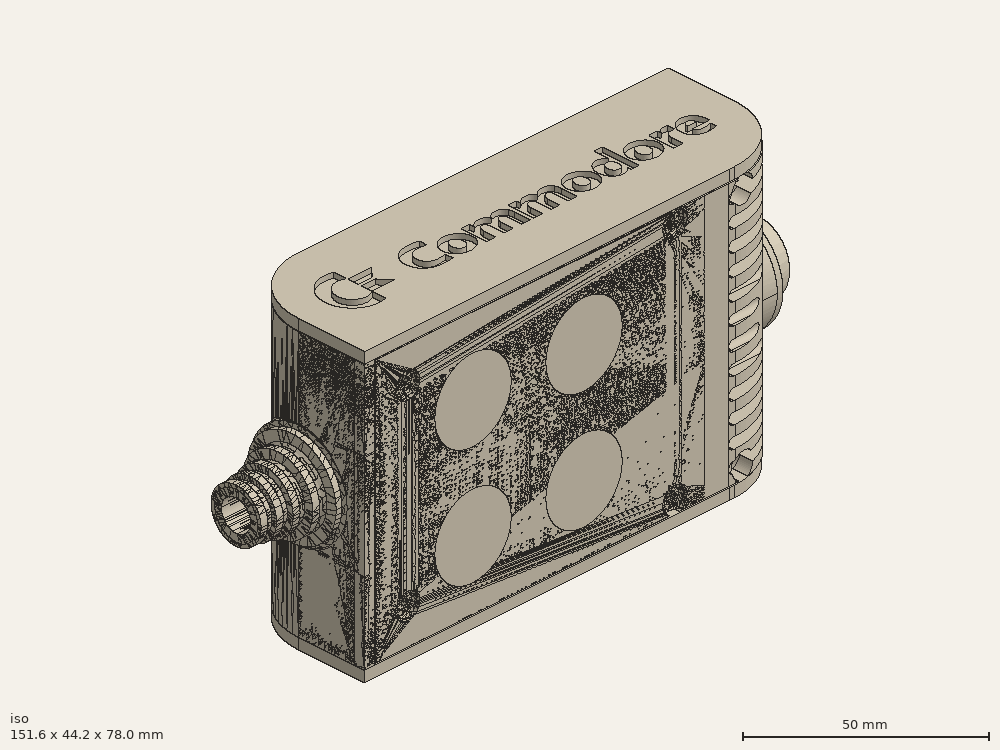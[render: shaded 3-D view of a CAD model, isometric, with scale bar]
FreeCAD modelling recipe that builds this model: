
FCSTD DOCUMENT  (FreeCAD 0.19R0.19.2)
Label: enclosure_219FCStd
License: All rights reserved
LicenseURL: http://en.wikipedia.org/wiki/All_rights_reserved
objects: Part::Revolution×152, Part::MultiFuse×146, Part::Feature×146, Sketcher::SketchObject×90, Part::Extrusion×74, Part::Cut×72, Part::Cylinder×70, Part::Fillet×58, Part::Box×36, App::MeasureDistance×4, Part::Chamfer×4, Part::FeaturePython×2, Image::ImagePlane×1, PartDesign::Body×1, Part::Mirroring×1
note: 852 computed .brp shape members not serialized (recipe doc carries the construction recipe); baked Part::Feature solids carry a one-line shape summary decoded from their .brp

FEATURE [Sketcher::SketchObject] Sketch  label="topSketch"
  FullyConstrained = true
  sketch-geometry (20):
    g0: LineSegment StartX=5.21097e-06 StartY=3 StartZ=0 EndX=5.21097e-06 EndY=19 EndZ=0
    g1: ArcOfCircle CenterX=19 CenterY=19 CenterZ=0 NormalX=0 NormalY=0 NormalZ=1 AngleXU=0 Radius=19 StartAngle=1.5708 EndAngle=3.14159
    g2: ArcOfCircle CenterX=19 CenterY=19 CenterZ=0 NormalX=0 NormalY=0 NormalZ=1 AngleXU=0 Radius=16 StartAngle=1.5708 EndAngle=3.14159
    g3: LineSegment StartX=114 StartY=35 StartZ=0 EndX=19 EndY=35 EndZ=0
    g4: LineSegment StartX=5.21097e-06 StartY=3 StartZ=0 EndX=5.21097e-06 EndY=0 EndZ=0
    g5: LineSegment StartX=3 StartY=0 StartZ=0 EndX=5.21097e-06 EndY=0 EndZ=0
    g6: LineSegment StartX=3 StartY=19 StartZ=0 EndX=3 EndY=0 EndZ=0
    g7: LineSegment StartX=19 StartY=38 StartZ=0 EndX=124 EndY=38 EndZ=0
    g8: Circle CenterX=119 CenterY=35 CenterZ=0 NormalX=0 NormalY=0 NormalZ=1 AngleXU=0 Radius=1
    g9: Circle CenterX=121 CenterY=35 CenterZ=0 NormalX=0 NormalY=0 NormalZ=1 AngleXU=0 Radius=1
    g10: Circle CenterX=121 CenterY=33 CenterZ=0 NormalX=0 NormalY=0 NormalZ=1 AngleXU=0 Radius=1
    g11: BSplineCurve PolesCount=3 KnotsCount=2 Degree=2 IsPeriodic=0
    g12: GeomPoint X=119 Y=35 Z=0
    g13: GeomPoint X=121 Y=33 Z=0
    g14: LineSegment StartX=119 StartY=35 StartZ=0 EndX=114 EndY=35 EndZ=0
    g15: ArcOfCircle CenterX=105 CenterY=19 CenterZ=0 NormalX=0 NormalY=0 NormalZ=1 AngleXU=0 Radius=19 StartAngle=5.7297 EndAngle=6.28319
    g16: ArcOfCircle CenterX=105 CenterY=19 CenterZ=0 NormalX=0 NormalY=0 NormalZ=1 AngleXU=0 Radius=16 StartAngle=5.60905 EndAngle=6.28319
    g17: LineSegment StartX=121 StartY=33 StartZ=0 EndX=121 EndY=19 EndZ=0
    g18: LineSegment StartX=124 StartY=38 StartZ=0 EndX=124 EndY=19 EndZ=0
    g19: LineSegment StartX=117.5 StartY=9.01251 StartZ=0 EndX=121.163 EndY=9.0125 EndZ=0
  constraints (46):
    c: Vertical(g0)
    c: Block(g0)
    c: Coincident(g1,g0)
    c: Block(g1)
    c: Coincident(g2,g1)
    c: Block(g2)
    c: Coincident(g3,g2)
    c: Horizontal(g3)
    c: Tangent(g3,g2)
    c: Coincident(g4,g0)
    c: Distance(g4) = 3
    c: Vertical(g4)
    c: Coincident(g5,g4)
    c: Horizontal(g5)
    c: Coincident(g6,g2)
    c: Coincident(g6,g5)
    c: Vertical(g6)
    c: Horizontal(g7)
    c: Distance(g7) = 105
    c: Coincident(g7,g1)
    c: Block(g3)
    c: Weight(g8) = 1
    c: Equal(g8,g9)
    c: Equal(g8,g10)
    c: InternalAlignment(g8,g11)
    c: InternalAlignment(g9,g11)
    c: InternalAlignment(g10,g11)
    c: InternalAlignment(g12,g11)
    c: InternalAlignment(g13,g11)
    c: Block(g11)
    c: Coincident(g14,g11)
    c: Coincident(g14,g3)
    c: Horizontal(g14)
    c: Block(g15)
    c: Coincident(g16,g15)
    c: Block(g16)
    c: Coincident(g17,g11)
    c: Coincident(g17,g16)
    c: Vertical(g17)
    c: Distance(g17) = 14
    c: Coincident(g18,g7)
    c: Coincident(g18,g15)
    c: Vertical(g18)
    c: Distance(g18) = 19
    c: Coincident(g19,g16)
    c: Coincident(g19,g15)
FEATURE [Sketcher::SketchObject] Sketch001  label="bottomSketch"
  FullyConstrained = true
  sketch-geometry (32):
    g0: LineSegment StartX=3.3 StartY=-6.03275e-07 StartZ=0 EndX=98 EndY=-6.03275e-07 EndZ=0
    g1: ArcOfCircle CenterX=98 CenterY=19 CenterZ=0 NormalX=0 NormalY=0 NormalZ=1 AngleXU=0 Radius=19 StartAngle=4.71239 EndAngle=5.71103
    g2: LineSegment StartX=6.3 StartY=8 StartZ=0 EndX=3.3 EndY=8 EndZ=0
    g3: LineSegment StartX=3.3 StartY=8 StartZ=0 EndX=3.3 EndY=-6.03275e-07 EndZ=0
    g4: ArcOfCircle CenterX=8.3 CenterY=5 CenterZ=0 NormalX=0 NormalY=0 NormalZ=1 AngleXU=0 Radius=2 StartAngle=3.14159 EndAngle=4.71239
    g5: LineSegment StartX=6.3 StartY=8 StartZ=0 EndX=6.3 EndY=5 EndZ=0
    g6: ArcOfCircle CenterX=98 CenterY=19 CenterZ=0 NormalX=0 NormalY=0 NormalZ=1 AngleXU=0 Radius=12.7 StartAngle=4.71239 EndAngle=6.28319
    g7: LineSegment StartX=94.7 StartY=3 StartZ=0 EndX=8.3 EndY=3 EndZ=0
    g8-g12: Circle x5 (B-spline internal-alignment scaffolding for g13; pole/knot coordinates omitted)
    g13: BSplineCurve PolesCount=5 KnotsCount=3 Degree=3 IsPeriodic=0
    g14: GeomPoint X=98 Y=6.3 Z=0
    g15: GeomPoint X=96.3938 Y=4.71946 Z=0
    g16: GeomPoint X=94.7 Y=3 Z=0
    g17-g23: Circle x7 (B-spline internal-alignment scaffolding for g24; pole/knot coordinates omitted)
    g24: BSplineCurve PolesCount=7 KnotsCount=5 Degree=3 IsPeriodic=0
    g25-g29: GeomPoint x5 (B-spline internal-alignment scaffolding for g24; pole/knot coordinates omitted)
    g30: ArcOfCircle CenterX=98 CenterY=19 CenterZ=0 NormalX=0 NormalY=0 NormalZ=1 AngleXU=0 Radius=15.7 StartAngle=5.81226 EndAngle=6.28319
    g31: LineSegment StartX=110.7 StartY=19 StartZ=0 EndX=113.7 EndY=19 EndZ=0
  constraints (41):
    c: Horizontal(g0)
    c: Coincident(g1,g0)
    c: Block(g1)
    c: Horizontal(g2)
    c: Distance(g2) = 3
    c: Coincident(g3,g2)
    c: Vertical(g3)
    c: Coincident(g3,g0)
    c: Block(g4)
    c: Block(g2)
    c: Coincident(g5,g2)
    c: Coincident(g5,g4)
    c: Vertical(g5)
    c: Coincident(g6,g1)
    c: Block(g6)
    c: Coincident(g7,g4)
    c: Horizontal(g7)
    c: Block(g0)
    c: Block(g7)
    c: Block(g3)
    c: Coincident(g13,g6)
    c: Weight(g8) = 1
    c: Equal(g8, g9-g12) x4
    c: Coincident(g13,g7)
    c: InternalAlignment(g8-g12 -> g13) x5
    c: InternalAlignment(g14,g13)
    c: InternalAlignment(g15,g13)
    c: InternalAlignment(g16,g13)
    c: Block(g13)
    c: Weight(g17) = 1
    c: Equal(g17, g18-g23) x6
    c: Coincident(g24,g1)
    c: InternalAlignment(g17-g23 -> g24) x7
    c: InternalAlignment(g25-g29 -> g24) x5
    c: Block(g24)
    c: Coincident(g30,g24)
    c: Coincident(g31,g6)
    c: Coincident(g31,g30)
    c: Horizontal(g31)
    c: Block(g31)
    c: Block(g30)
FEATURE [Part::Extrusion] Extrude  label="top"
  Base = -> Sketch
  Dir = (0,0,1)
  DirMode = 2
  FaceMakerClass = Part::FaceMakerBullseye
  LengthFwd = 72
  LengthRev = 0
  Solid = true
  Symmetric = false
FEATURE [Part::Extrusion] Extrude001  label="bottom"
  Base = -> Sketch001
  Dir = (0,0,1)
  DirMode = 2
  FaceMakerClass = Part::FaceMakerBullseye
  LengthFwd = 71.4
  LengthRev = 0
  Placement = pos=(0,0,0.3) rot=(0,0,1;0rad)
  Solid = true
  Symmetric = false
FEATURE [Sketcher::SketchObject] Sketch002  label="topSketch001"
  FullyConstrained = true
  sketch-geometry (8):
    g0: ArcOfCircle CenterX=19 CenterY=19.0975 CenterZ=0 NormalX=0 NormalY=0 NormalZ=1 AngleXU=0 Radius=18.9025 StartAngle=1.5708 EndAngle=3.14674
    g1: LineSegment StartX=0.0977805 StartY=19.0003 StartZ=0 EndX=0.0977805 EndY=0.000251602 EndZ=0
    g2: LineSegment StartX=19 StartY=38 StartZ=0 EndX=124 EndY=38 EndZ=0
    g3: LineSegment StartX=0.0977805 StartY=0.000251602 StartZ=0 EndX=105.098 EndY=0.000251602 EndZ=0
    g4: LineSegment StartX=124 StartY=38 StartZ=0 EndX=125.616 EndY=38 EndZ=0
    g5: LineSegment StartX=105.098 StartY=0.000251602 StartZ=0 EndX=106.713 EndY=0.000251602 EndZ=0
    g6: ArcOfCircle CenterX=106.616 CenterY=19 CenterZ=0 NormalX=0 NormalY=0 NormalZ=1 AngleXU=0 Radius=19 StartAngle=4.71754 EndAngle=6.28319
    g7: LineSegment StartX=125.616 StartY=38 StartZ=0 EndX=125.616 EndY=19 EndZ=0
  constraints (21):
    c: Block(g0)
    c: Coincident(g1,g0)
    c: Vertical(g1)
    c: Horizontal(g2)
    c: Distance(g2) = 105
    c: Coincident(g2,g0)
    c: Distance(g1) = 19
    c: Coincident(g3,g1)
    c: Horizontal(g3)
    c: Distance(g3) = 105
    c: Coincident(g4,g2)
    c: Horizontal(g4)
    c: Distance(g4) = 1.61553
    c: Horizontal(g5)
    c: Equal(g4,g5) = 1.61553
    c: Coincident(g5,g3)
    c: Block(g6)
    c: Coincident(g6,g5)
    c: Coincident(g7,g4)
    c: Coincident(g7,g6)
    c: Vertical(g7)
FEATURE [Part::Extrusion] Extrude002  label="sideA"
  Base = -> Sketch002
  Dir = (0,0,1)
  DirMode = 2
  FaceMakerClass = Part::FaceMakerBullseye
  LengthFwd = 3
  LengthRev = 0
  Placement = pos=(0,0,-3) rot=(0,0,1;0rad)
  Solid = true
  Symmetric = false
FEATURE [Sketcher::SketchObject] Sketch003  label="topSketch002"
  FullyConstrained = true
  sketch-geometry (6):
    g0: LineSegment StartX=19 StartY=38 StartZ=0 EndX=117 EndY=38 EndZ=0
    g1: ArcOfCircle CenterX=19 CenterY=19 CenterZ=0 NormalX=0 NormalY=0 NormalZ=1 AngleXU=0 Radius=19 StartAngle=1.5708 EndAngle=3.14159
    g2: LineSegment StartX=117 StartY=38 StartZ=0 EndX=117 EndY=19 EndZ=0
    g3: LineSegment StartX=98 StartY=1.0161e-12 StartZ=0 EndX=5.22862e-06 EndY=1.0161e-12 EndZ=0
    g4: LineSegment StartX=5.22862e-06 StartY=19 StartZ=0 EndX=5.22862e-06 EndY=1.0161e-12 EndZ=0
    g5: ArcOfCircle CenterX=98 CenterY=19 CenterZ=0 NormalX=0 NormalY=0 NormalZ=1 AngleXU=0 Radius=19 StartAngle=4.71239 EndAngle=6.28319
  constraints (16):
    c: Horizontal(g0)
    c: Distance(g0) = 98
    c: Coincident(g1,g0)
    c: Block(g1)
    c: Coincident(g2,g0)
    c: Vertical(g2)
    c: Distance(g2) = 19
    c: Horizontal(g3)
    c: Coincident(g4,g1)
    c: Vertical(g4)
    c: Coincident(g3,g4)
    c: Block(g3)
    c: Coincident(g5,g2)
    c: Coincident(g5,g3)
    c: Block(g0)
    c: Block(g5)
FEATURE [Sketcher::SketchObject] Sketch004
  FullyConstrained = true
  MapMode = 3
  Placement = pos=(0,0,0) rot=(1,0,0;1.5708rad)
  Support = -> [Extrude]
  sketch-geometry (8):
    g0: Circle CenterX=80.351 CenterY=-67.6202 CenterZ=0 NormalX=0 NormalY=0 NormalZ=1 AngleXU=0 Radius=2
    g1: Circle CenterX=80.351 CenterY=-67.6202 CenterZ=0 NormalX=0 NormalY=0 NormalZ=1 AngleXU=0 Radius=3
    g2: Circle CenterX=80.351 CenterY=-4.92017 CenterZ=0 NormalX=0 NormalY=0 NormalZ=1 AngleXU=0 Radius=2
    g3: Circle CenterX=80.351 CenterY=-4.92017 CenterZ=0 NormalX=0 NormalY=0 NormalZ=1 AngleXU=0 Radius=3
    g4: Circle CenterX=23.851 CenterY=-4.92017 CenterZ=0 NormalX=0 NormalY=0 NormalZ=1 AngleXU=0 Radius=2
    g5: Circle CenterX=23.851 CenterY=-4.92017 CenterZ=0 NormalX=0 NormalY=0 NormalZ=1 AngleXU=0 Radius=3
    g6: Circle CenterX=23.851 CenterY=-67.6202 CenterZ=0 NormalX=0 NormalY=0 NormalZ=1 AngleXU=0 Radius=2
    g7: Circle CenterX=23.851 CenterY=-67.6202 CenterZ=0 NormalX=0 NormalY=0 NormalZ=1 AngleXU=0 Radius=3
  constraints (8):
    c: Block(g3)
    c: Block(g2)
    c: Block(g1)
    c: Block(g0)
    c: Block(g6)
    c: Block(g7)
    c: Block(g4)
    c: Block(g5)
FEATURE [Part::Extrusion] Extrude004
  Base = -> Sketch004
  Dir = (0,-1,2e-16)
  DirMode = 2
  FaceMakerClass = Part::FaceMakerBullseye
  LengthFwd = 6
  LengthRev = 0
  Placement = pos=(0,9,0) rot=(0,0,1;0rad)
  Solid = true
  Symmetric = false
FEATURE [Sketcher::SketchObject] Sketch005
  FullyConstrained = true
  MapMode = 3
  Placement = pos=(0,0,0) rot=(1,0,0;1.5708rad)
  Support = -> [Extrude]
  sketch-geometry (8):
    g0: Circle CenterX=80.351 CenterY=-67.6202 CenterZ=0 NormalX=0 NormalY=0 NormalZ=1 AngleXU=0 Radius=3
    g1: Circle CenterX=80.351 CenterY=-4.92017 CenterZ=0 NormalX=0 NormalY=0 NormalZ=1 AngleXU=0 Radius=3
    g2: Circle CenterX=23.851 CenterY=-4.92017 CenterZ=0 NormalX=0 NormalY=0 NormalZ=1 AngleXU=0 Radius=3
    g3: Circle CenterX=23.851 CenterY=-67.6202 CenterZ=0 NormalX=0 NormalY=0 NormalZ=1 AngleXU=0 Radius=3
    g4: Circle CenterX=23.851 CenterY=-67.6202 CenterZ=0 NormalX=0 NormalY=0 NormalZ=1 AngleXU=0 Radius=5
    g5: Circle CenterX=80.351 CenterY=-67.6202 CenterZ=0 NormalX=0 NormalY=0 NormalZ=1 AngleXU=0 Radius=5
    g6: Circle CenterX=23.851 CenterY=-4.92017 CenterZ=0 NormalX=0 NormalY=0 NormalZ=1 AngleXU=0 Radius=5
    g7: Circle CenterX=80.351 CenterY=-4.92017 CenterZ=0 NormalX=0 NormalY=0 NormalZ=1 AngleXU=0 Radius=5
  constraints (8):
    c: Block(g1)
    c: Block(g0)
    c: Block(g3)
    c: Block(g2)
    c: Block(g5)
    c: Block(g4)
    c: Block(g6)
    c: Block(g7)
FEATURE [Part::Extrusion] Extrude005
  Base = -> Sketch005
  Dir = (0,-1,2e-16)
  DirMode = 2
  FaceMakerClass = Part::FaceMakerBullseye
  LengthFwd = 2
  LengthRev = 0
  Solid = true
  Symmetric = false
FEATURE [Sketcher::SketchObject] Sketch006
  FullyConstrained = true
  MapMode = 3
  Placement = pos=(0,0,0) rot=(1,0,0;1.5708rad)
  sketch-geometry (8):
    g0: Circle CenterX=80.351 CenterY=-67.6202 CenterZ=0 NormalX=0 NormalY=0 NormalZ=1 AngleXU=0 Radius=3
    g1: Circle CenterX=80.351 CenterY=-4.92017 CenterZ=0 NormalX=0 NormalY=0 NormalZ=1 AngleXU=0 Radius=3
    g2: Circle CenterX=23.851 CenterY=-4.92017 CenterZ=0 NormalX=0 NormalY=0 NormalZ=1 AngleXU=0 Radius=3
    g3: Circle CenterX=23.851 CenterY=-67.6202 CenterZ=0 NormalX=0 NormalY=0 NormalZ=1 AngleXU=0 Radius=3
    g4: Circle CenterX=23.851 CenterY=-67.6202 CenterZ=0 NormalX=0 NormalY=0 NormalZ=1 AngleXU=0 Radius=5
    g5: Circle CenterX=80.351 CenterY=-67.6202 CenterZ=0 NormalX=0 NormalY=0 NormalZ=1 AngleXU=0 Radius=5
    g6: Circle CenterX=23.851 CenterY=-4.92017 CenterZ=0 NormalX=0 NormalY=0 NormalZ=1 AngleXU=0 Radius=5
    g7: Circle CenterX=80.351 CenterY=-4.92017 CenterZ=0 NormalX=0 NormalY=0 NormalZ=1 AngleXU=0 Radius=5
  constraints (8):
    c: Block(g1)
    c: Block(g0)
    c: Block(g3)
    c: Block(g2)
    c: Block(g5)
    c: Block(g4)
    c: Block(g6)
    c: Block(g7)
FEATURE [Part::Extrusion] Extrude007
  Base = -> Sketch006
  Dir = (0,-1,2e-16)
  DirMode = 2
  FaceMakerClass = Part::FaceMakerBullseye
  LengthFwd = 2
  LengthRev = 0
  Solid = true
  Symmetric = false
FEATURE [Part::Fillet] Fillet
  Base = -> Extrude007
  Edges = 4 edges r=1.99: [Edge6,Edge12,Edge18,Edge24]
FEATURE [Part::Cut] Cut
  Base = -> Extrude005
  Placement = pos=(0,5,0) rot=(0,0,1;0rad)
  Tool = -> Fillet
FEATURE [Part::MultiFuse] Fusion  label="pCBScrews"
  Placement = pos=(-2.5,0,72.3) rot=(0,0,1;0rad)
  Shapes = -> [Extrude004,Cut]
FEATURE [App::MeasureDistance] Distance  label="Distance: 0.69 mm"
  Distance = 0.685967
  P1 = (24.0138,2.9647,0.3)
  P2 = (23.8901,3,-0.373787)
FEATURE [App::MeasureDistance] Distance001  label="Distance: 0.53 mm"
  Distance = 0.533607
  P1 = (80.2939,3,72.2334)
  P2 = (80.281,2.99661,71.7)
FEATURE [Part::Fillet] Fillet001
  Base = -> Extrude001
  Edges = 1 edges r=2.4: [Edge17]
FEATURE [Part::Fillet] Fillet002  label="bottom001"
  Base = -> Fillet001
  Edges = 1 edges r=2.4: [Edge36]
FEATURE [Part::Fillet] Fillet003  label="top001"
  Base = -> Extrude
  Edges = 1 edges r=2: [Edge1]
FEATURE [Sketcher::SketchObject] Sketch007
  FullyConstrained = true
  sketch-geometry (16):
    g0: LineSegment StartX=4 StartY=0 StartZ=0 EndX=4 EndY=2.4 EndZ=0
    g1: LineSegment StartX=4 StartY=2.4 StartZ=0 EndX=7 EndY=2.4 EndZ=0
    g2: LineSegment StartX=4 StartY=0 StartZ=0 EndX=5.7 EndY=0 EndZ=0
    g3: LineSegment StartX=5.7 StartY=0 StartZ=0 EndX=5.7 EndY=-5.6 EndZ=0
    g4-g8: Circle x5 (B-spline internal-alignment scaffolding for g9; pole/knot coordinates omitted)
    g9: BSplineCurve PolesCount=5 KnotsCount=3 Degree=3 IsPeriodic=0
    g10: GeomPoint X=7 Y=2.4 Z=0
    g11: GeomPoint X=10.4582 Y=-1.55472 Z=0
    g12: GeomPoint X=14 Y=-5.6 Z=0
    g13: LineSegment StartX=14 StartY=-5.6 StartZ=0 EndX=14 EndY=-14.1 EndZ=0
    g14: LineSegment StartX=14 StartY=-14.1 StartZ=0 EndX=6.5 EndY=-14.1 EndZ=0
    g15: LineSegment StartX=5.7 StartY=-5.6 StartZ=0 EndX=6.5 EndY=-14.1 EndZ=0
  constraints (28):
    c: Distance(g0) = 2.4
    c: Vertical(g0)
    c: Block(g0)
    c: Coincident(g1,g0)
    c: Horizontal(g1)
    c: Distance(g1) = 3
    c: Coincident(g2,g0)
    c: Horizontal(g2)
    c: Distance(g2) = 1.7
    c: Coincident(g3,g2)
    c: Vertical(g3)
    c: Distance(g3) = 5.6
    c: Coincident(g9,g1)
    c: Weight(g4) = 1
    c: Equal(g4, g5-g8) x4
    c: InternalAlignment(g4-g8 -> g9) x5
    c: InternalAlignment(g10,g9)
    c: InternalAlignment(g11,g9)
    c: InternalAlignment(g12,g9)
    c: Block(g9)
    c: Coincident(g13,g9)
    c: Vertical(g13)
    c: Distance(g13) = 8.5
    c: Coincident(g14,g13)
    c: Horizontal(g14)
    c: Distance(g14) = 7.5
    c: Coincident(g15,g3)
    c: Coincident(g15,g14)
FEATURE [Part::Feature] Face
  shape: bbox 10 x 16.5 x 2e-07 mm, 1 faces, 0 solids (baked)
FEATURE [Part::Revolution] Revolve  label="plugHousing"
  Angle = 360
  Axis = (0,1,0)
  Base = (0,0,0)
  FaceMakerClass = Part::FaceMakerBullseye
  Placement = pos=(0,0,36.15) rot=(0,0,1;0rad)
  Solid = false
  Source = -> Face
  Symmetric = false
FEATURE [Part::Feature] Face001
  shape: bbox 10 x 16.5 x 2e-07 mm, 1 faces, 0 solids (baked)
FEATURE [Part::Revolution] Revolve001  label="plugHousing001"
  Angle = 360
  Axis = (0,1,0)
  Base = (0,0,0)
  FaceMakerClass = Part::FaceMakerBullseye
  Placement = pos=(0,0,36.15) rot=(0,0,1;0rad)
  Solid = false
  Source = -> Face001
  Symmetric = false
FEATURE [Part::MultiFuse] Fusion001  label="plugHousing002"
  Placement = pos=(0,0,0) rot=(0,0,1;1.5708rad)
  Shapes = -> [Revolve001,Revolve]
FEATURE [Part::Feature] Face002
  shape: bbox 10 x 16.5 x 2e-07 mm, 1 faces, 0 solids (baked)
FEATURE [Part::Revolution] Revolve003  label="plugHousing005"
  Angle = 360
  Axis = (0,1,0)
  Base = (0,0,0)
  FaceMakerClass = Part::FaceMakerBullseye
  Placement = pos=(0,0,36.15) rot=(0,0,1;0rad)
  Solid = false
  Source = -> Face002
  Symmetric = false
FEATURE [Part::Feature] Face003
  shape: bbox 10 x 16.5 x 2e-07 mm, 1 faces, 0 solids (baked)
FEATURE [Part::Revolution] Revolve002  label="plugHousing003"
  Angle = 360
  Axis = (0,1,0)
  Base = (0,0,0)
  FaceMakerClass = Part::FaceMakerBullseye
  Placement = pos=(0,0,36.15) rot=(0,0,1;0rad)
  Solid = false
  Source = -> Face003
  Symmetric = false
FEATURE [Part::MultiFuse] Fusion002  label="plugHousing004"
  Placement = pos=(0,0,0) rot=(0,0,1;1.5708rad)
  Shapes = -> [Revolve002,Revolve003]
FEATURE [Part::MultiFuse] Fusion003  label="plugHousing006"
  Placement = pos=(0,19,0) rot=(0,0,1;3.14159rad)
  Shapes = -> [Fusion002,Fusion001]
FEATURE [Part::Feature] Face004
  shape: bbox 10 x 16.5 x 2e-07 mm, 1 faces, 0 solids (baked)
FEATURE [Part::Revolution] Revolve006  label="plugHousing010"
  Angle = 360
  Axis = (0,1,0)
  Base = (0,0,0)
  FaceMakerClass = Part::FaceMakerBullseye
  Placement = pos=(0,0,36.15) rot=(0,0,1;0rad)
  Solid = false
  Source = -> Face004
  Symmetric = false
FEATURE [Part::Feature] Face005
  shape: bbox 10 x 16.5 x 2e-07 mm, 1 faces, 0 solids (baked)
FEATURE [Part::Revolution] Revolve007  label="plugHousing011"
  Angle = 360
  Axis = (0,1,0)
  Base = (0,0,0)
  FaceMakerClass = Part::FaceMakerBullseye
  Placement = pos=(0,0,36.15) rot=(0,0,1;0rad)
  Solid = false
  Source = -> Face005
  Symmetric = false
FEATURE [Part::Feature] Face006
  shape: bbox 10 x 16.5 x 2e-07 mm, 1 faces, 0 solids (baked)
FEATURE [Part::Revolution] Revolve004  label="plugHousing007"
  Angle = 360
  Axis = (0,1,0)
  Base = (0,0,0)
  FaceMakerClass = Part::FaceMakerBullseye
  Placement = pos=(0,0,36.15) rot=(0,0,1;0rad)
  Solid = false
  Source = -> Face006
  Symmetric = false
FEATURE [Part::MultiFuse] Fusion004  label="plugHousing009"
  Placement = pos=(0,0,0) rot=(0,0,1;1.5708rad)
  Shapes = -> [Revolve004,Revolve007]
FEATURE [Part::Feature] Face007
  shape: bbox 10 x 16.5 x 2e-07 mm, 1 faces, 0 solids (baked)
FEATURE [Part::Revolution] Revolve005  label="plugHousing008"
  Angle = 360
  Axis = (0,1,0)
  Base = (0,0,0)
  FaceMakerClass = Part::FaceMakerBullseye
  Placement = pos=(0,0,36.15) rot=(0,0,1;0rad)
  Solid = false
  Source = -> Face007
  Symmetric = false
FEATURE [Part::MultiFuse] Fusion005  label="plugHousing012"
  Placement = pos=(0,0,0) rot=(0,0,1;1.5708rad)
  Shapes = -> [Revolve006,Revolve005]
FEATURE [Part::MultiFuse] Fusion006  label="plugHousing013"
  Placement = pos=(0,19,0) rot=(0,0,1;3.14159rad)
  Shapes = -> [Fusion005,Fusion004]
FEATURE [Part::MultiFuse] Fusion007  label="plugHousing014"
  Placement = pos=(122.621,0,-0.15) rot=(0,0,1;0rad)
  Shapes = -> [Fusion003,Fusion006]
FEATURE [Part::Cylinder] Cylinder002
  Angle = 360
  AttacherType = Attacher::AttachEngine3D
  Height = 20
  Placement = pos=(0,0,36.15) rot=(0,0,1;0rad)
  Radius = 4
FEATURE [Part::Cylinder] Cylinder003
  Angle = 360
  AttacherType = Attacher::AttachEngine3D
  Height = 10
  Placement = pos=(0,0,36.15) rot=(0,0,1;0rad)
  Radius = 4
FEATURE [Part::MultiFuse] Fusion009  label="removeToCreateHoleForPlugHousing"
  Placement = pos=(70,19,36.15) rot=(0,1,0;1.5708rad)
  Shapes = -> [Cylinder002,Cylinder003]
FEATURE [Part::Cylinder] Cylinder004
  Angle = 360
  AttacherType = Attacher::AttachEngine3D
  Height = 20
  Placement = pos=(0,0,36.15) rot=(0,0,1;0rad)
  Radius = 4
FEATURE [Part::Cylinder] Cylinder005
  Angle = 360
  AttacherType = Attacher::AttachEngine3D
  Height = 10
  Placement = pos=(0,0,36.15) rot=(0,0,1;0rad)
  Radius = 4
FEATURE [Part::MultiFuse] Fusion010  label="removeToCreateHoleForPlugHousing001"
  Placement = pos=(70,19,36.15) rot=(0,1,0;1.5708rad)
  Shapes = -> [Cylinder004,Cylinder005]
FEATURE [Part::Cut] Cut001
  Base = -> Fillet003
  Tool = -> Fusion010
FEATURE [Part::Cut] Cut002  label="Bottom"
  Base = -> Fillet002
  Tool = -> Fusion009
FEATURE [Part::Feature] Face008
  shape: bbox 10 x 16.5 x 2e-07 mm, 1 faces, 0 solids (baked)
FEATURE [Part::Revolution] Revolve011  label="plugHousing021"
  Angle = 360
  Axis = (0,1,0)
  Base = (0,0,0)
  FaceMakerClass = Part::FaceMakerBullseye
  Placement = pos=(0,0,36.15) rot=(0,0,1;0rad)
  Solid = false
  Source = -> Face008
  Symmetric = false
FEATURE [Part::Feature] Face009
  shape: bbox 10 x 16.5 x 2e-07 mm, 1 faces, 0 solids (baked)
FEATURE [Part::Revolution] Revolve012  label="plugHousing022"
  Angle = 360
  Axis = (0,1,0)
  Base = (0,0,0)
  FaceMakerClass = Part::FaceMakerBullseye
  Placement = pos=(0,0,36.15) rot=(0,0,1;0rad)
  Solid = false
  Source = -> Face009
  Symmetric = false
FEATURE [Part::Feature] Face010 .. Face013  x4 (patterned run collapsed; names and placements below)
  shape: bbox 10 x 16.5 x 2e-07 mm, 1 faces, 0 solids (baked)
FEATURE [Part::Revolution] Revolve015  label="plugHousing027"
  Angle = 360
  Axis = (0,1,0)
  Base = (0,0,0)
  FaceMakerClass = Part::FaceMakerBullseye
  Placement = pos=(0,0,36.15) rot=(0,0,1;0rad)
  Solid = false
  Source = -> Face013
  Symmetric = false
FEATURE [Part::Feature] Face014
  shape: bbox 10 x 16.5 x 2e-07 mm, 1 faces, 0 solids (baked)
FEATURE [Part::Feature] Face015
  shape: bbox 10 x 16.5 x 2e-07 mm, 1 faces, 0 solids (baked)
FEATURE [Part::Feature] Face016
  shape: bbox 10 x 16.5 x 2e-07 mm, 1 faces, 0 solids (baked)
FEATURE [Part::Revolution] Revolve019  label="plugHousing033"
  Angle = 360
  Axis = (0,1,0)
  Base = (0,0,0)
  FaceMakerClass = Part::FaceMakerBullseye
  Placement = pos=(0,0,36.15) rot=(0,0,1;0rad)
  Solid = false
  Source = -> Face016
  Symmetric = false
FEATURE [Part::Feature] Face017
  shape: bbox 10 x 16.5 x 2e-07 mm, 1 faces, 0 solids (baked)
FEATURE [Part::Revolution] Revolve020  label="plugHousing034"
  Angle = 360
  Axis = (0,1,0)
  Base = (0,0,0)
  FaceMakerClass = Part::FaceMakerBullseye
  Placement = pos=(0,0,36.15) rot=(0,0,1;0rad)
  Solid = false
  Source = -> Face017
  Symmetric = false
FEATURE [Part::Feature] Face018
  shape: bbox 10 x 16.5 x 2e-07 mm, 1 faces, 0 solids (baked)
FEATURE [Part::Revolution] Revolve016  label="plugHousing030"
  Angle = 360
  Axis = (0,1,0)
  Base = (0,0,0)
  FaceMakerClass = Part::FaceMakerBullseye
  Placement = pos=(0,0,36.15) rot=(0,0,1;0rad)
  Solid = false
  Source = -> Face018
  Symmetric = false
FEATURE [Part::MultiFuse] Fusion020  label="plugHousing038"
  Placement = pos=(0,0,0) rot=(0,0,1;1.5708rad)
  Shapes = -> [Revolve016,Revolve020]
FEATURE [Part::Feature] Face019
  shape: bbox 10 x 16.5 x 2e-07 mm, 1 faces, 0 solids (baked)
FEATURE [Part::Feature] Face020
  shape: bbox 10 x 16.5 x 2e-07 mm, 1 faces, 0 solids (baked)
FEATURE [Part::Revolution] Revolve017  label="plugHousing031"
  Angle = 360
  Axis = (0,1,0)
  Base = (0,0,0)
  FaceMakerClass = Part::FaceMakerBullseye
  Placement = pos=(0,0,36.15) rot=(0,0,1;0rad)
  Solid = false
  Source = -> Face020
  Symmetric = false
FEATURE [Part::MultiFuse] Fusion021  label="plugHousing039"
  Placement = pos=(0,0,0) rot=(0,0,1;1.5708rad)
  Shapes = -> [Revolve019,Revolve017]
FEATURE [Part::MultiFuse] Fusion023  label="plugHousing041"
  Placement = pos=(0,19,0) rot=(0,0,1;3.14159rad)
  Shapes = -> [Fusion021,Fusion020]
FEATURE [Part::Revolution] Revolve022  label="plugHousing043"
  Angle = 360
  Axis = (0,1,0)
  Base = (0,0,0)
  FaceMakerClass = Part::FaceMakerBullseye
  Placement = pos=(0,0,36.15) rot=(0,0,1;0rad)
  Solid = false
  Source = -> Face019
  Symmetric = false
FEATURE [Part::Feature] Face021
  shape: bbox 10 x 16.5 x 2e-07 mm, 1 faces, 0 solids (baked)
FEATURE [Part::Revolution] Revolve023  label="plugHousing044"
  Angle = 360
  Axis = (0,1,0)
  Base = (0,0,0)
  FaceMakerClass = Part::FaceMakerBullseye
  Placement = pos=(0,0,36.15) rot=(0,0,1;0rad)
  Solid = false
  Source = -> Face021
  Symmetric = false
FEATURE [Part::Feature] Face022
  shape: bbox 10 x 16.5 x 2e-07 mm, 1 faces, 0 solids (baked)
FEATURE [Part::Revolution] Revolve018  label="plugHousing032"
  Angle = 360
  Axis = (0,1,0)
  Base = (0,0,0)
  FaceMakerClass = Part::FaceMakerBullseye
  Placement = pos=(0,0,36.15) rot=(0,0,1;0rad)
  Solid = false
  Source = -> Face022
  Symmetric = false
FEATURE [Part::MultiFuse] Fusion022  label="plugHousing040"
  Placement = pos=(0,0,0) rot=(0,0,1;1.5708rad)
  Shapes = -> [Revolve018,Revolve023]
FEATURE [Part::Feature] Face023
  shape: bbox 10 x 16.5 x 2e-07 mm, 1 faces, 0 solids (baked)
FEATURE [Part::Revolution] Revolve021  label="plugHousing035"
  Angle = 360
  Axis = (0,1,0)
  Base = (0,0,0)
  FaceMakerClass = Part::FaceMakerBullseye
  Placement = pos=(0,0,36.15) rot=(0,0,1;0rad)
  Solid = false
  Source = -> Face023
  Symmetric = false
FEATURE [Part::MultiFuse] Fusion018  label="plugHousing036"
  Placement = pos=(0,0,0) rot=(0,0,1;1.5708rad)
  Shapes = -> [Revolve022,Revolve021]
FEATURE [Part::MultiFuse] Fusion019  label="plugHousing037"
  Placement = pos=(0,19,0) rot=(0,0,1;3.14159rad)
  Shapes = -> [Fusion018,Fusion022]
FEATURE [Part::MultiFuse] Fusion024  label="plugHousing042"
  Placement = pos=(122.621,0,-0.15) rot=(0,0,1;0rad)
  Shapes = -> [Fusion023,Fusion019]
FEATURE [Part::Cylinder] Cylinder006
  Angle = 360
  AttacherType = Attacher::AttachEngine3D
  Height = 20
  Placement = pos=(0,0,36.15) rot=(0,0,1;0rad)
  Radius = 14.3
FEATURE [Part::Cylinder] Cylinder007
  Angle = 360
  AttacherType = Attacher::AttachEngine3D
  Height = 10
  Placement = pos=(0,0,36.15) rot=(0,0,1;0rad)
  Radius = 4
FEATURE [Part::MultiFuse] Fusion026  label="removeToCreteHoleForPlugHousing"
  Placement = pos=(70,19,36) rot=(0,1,0;1.5708rad)
  Shapes = -> [Cylinder006,Cylinder007]
FEATURE [Part::Box] Box001  label="Cube001"
  AttacherType = Attacher::AttachEngine3D
  Height = 28
  Length = 3
  Placement = pos=(110.7,19,22) rot=(0,0,1;0rad)
  Width = 15.7
FEATURE [Part::Cut] Cut003  label="top002"
  Base = -> Cut001
  Tool = -> Fusion007
FEATURE [Part::Revolution] Revolve008  label="plugHousing015"
  Angle = 360
  Axis = (0,1,0)
  Base = (0,0,0)
  FaceMakerClass = Part::FaceMakerBullseye
  Placement = pos=(0,0,36.15) rot=(0,0,1;0rad)
  Solid = false
  Source = -> Face010
  Symmetric = false
FEATURE [Part::MultiFuse] Fusion013  label="plugHousing020"
  Placement = pos=(0,0,0) rot=(0,0,1;1.5708rad)
  Shapes = -> [Revolve008,Revolve012]
FEATURE [Part::Cut] Cut004  label="top003"
  Base = -> Cut003
  Placement = pos=(1,0,0) rot=(0,0,1;0rad)
  Tool = -> Fusion026
FEATURE [Part::Cylinder] Cylinder008
  Angle = 360
  AttacherType = Attacher::AttachEngine3D
  Height = 20
  Placement = pos=(0,0,36.15) rot=(0,0,1;0rad)
  Radius = 10.3
FEATURE [Part::Cylinder] Cylinder009
  Angle = 360
  AttacherType = Attacher::AttachEngine3D
  Height = 10
  Placement = pos=(0,0,36.15) rot=(0,0,1;0rad)
  Radius = 4
FEATURE [Part::MultiFuse] Fusion027  label="removeToCreteHoleForPlugHousing001"
  Placement = pos=(70,19,36) rot=(0,1,0;1.5708rad)
  Shapes = -> [Cylinder008,Cylinder009]
FEATURE [Part::Cut] Cut005  label="plugHousingTab"
  Base = -> Box001
  Tool = -> Fusion027
FEATURE [Part::MultiFuse] Fusion028  label="plugHousing045"
  Shapes = -> [Fusion024,Cut005]
FEATURE [Part::Box] Box002  label="Cube002"
  AttacherType = Attacher::AttachEngine3D
  Height = 28.8
  Length = 3
  Placement = pos=(107.3,28,21.6) rot=(0,0,1;0rad)
  Width = 7
FEATURE [Part::Box] Box003  label="Cube003"
  AttacherType = Attacher::AttachEngine3D
  Height = 3
  Length = 6.4
  Placement = pos=(107.3,28,18.6) rot=(0,0,1;0rad)
  Width = 7
FEATURE [Part::Box] Box004  label="Cube004"
  AttacherType = Attacher::AttachEngine3D
  Height = 3
  Length = 6.4
  Placement = pos=(107.3,28,50.4) rot=(0,0,1;0rad)
  Width = 7
FEATURE [Part::MultiFuse] Fusion029  label="plugHousingBracketHolder"
  Shapes = -> [Box004,Box002,Box003]
FEATURE [Part::Cylinder] Cylinder010
  Angle = 360
  AttacherType = Attacher::AttachEngine3D
  Height = 20
  Placement = pos=(0,0,36.15) rot=(0,0,1;0rad)
  Radius = 14.3
FEATURE [Part::Cylinder] Cylinder011
  Angle = 360
  AttacherType = Attacher::AttachEngine3D
  Height = 10
  Placement = pos=(0,0,36.15) rot=(0,0,1;0rad)
  Radius = 4
FEATURE [Part::MultiFuse] Fusion030  label="removeToCreteHoleForPlugHousing002"
  Placement = pos=(70,19,36) rot=(0,1,0;1.5708rad)
  Shapes = -> [Cylinder010,Cylinder011]
FEATURE [Part::Cut] Cut006  label="plugHousingBracketHolder001"
  Base = -> Fusion029
  Tool = -> Fusion030
FEATURE [Part::Cylinder] Cylinder012
  Angle = 360
  AttacherType = Attacher::AttachEngine3D
  Height = 20
  Placement = pos=(0,0,36.15) rot=(0,0,1;0rad)
  Radius = 7
FEATURE [Part::Cylinder] Cylinder013
  Angle = 360
  AttacherType = Attacher::AttachEngine3D
  Height = 10
  Placement = pos=(0,0,36.15) rot=(0,0,1;0rad)
  Radius = 4
FEATURE [Part::MultiFuse] Fusion032  label="removeToCreteHoleForPlugHousing003"
  Placement = pos=(70,19,36) rot=(0,1,0;1.5708rad)
  Shapes = -> [Cylinder012,Cylinder013]
FEATURE [Part::Cut] Cut007  label="bottom002"
  Base = -> Cut002
  Tool = -> Fusion032
FEATURE [Sketcher::SketchObject] Sketch008
  FullyConstrained = true
  sketch-geometry (54):
    g0: LineSegment StartX=-4.2 StartY=0 StartZ=0 EndX=-6.2 EndY=0 EndZ=0
    g1: LineSegment StartX=-14 StartY=-18 StartZ=0 EndX=-14 EndY=-26.5 EndZ=0
    g2: LineSegment StartX=-4.2 StartY=0 StartZ=0 EndX=-4.2 EndY=-13.4877 EndZ=0
    g3: Circle CenterX=-4.2 CenterY=-13.4877 CenterZ=0 NormalX=0 NormalY=0 NormalZ=1 AngleXU=0 Radius=1
    g4: Circle CenterX=-4.2 CenterY=-26.5 CenterZ=0 NormalX=0 NormalY=0 NormalZ=1 AngleXU=0 Radius=1
    g5: Circle CenterX=-8.2 CenterY=-26.5 CenterZ=0 NormalX=0 NormalY=0 NormalZ=1 AngleXU=0 Radius=1
    g6: BSplineCurve PolesCount=3 KnotsCount=2 Degree=2 IsPeriodic=0
    g7: GeomPoint X=-4.2 Y=-13.4877 Z=0
    g8: GeomPoint X=-8.2 Y=-26.5 Z=0
    g9: LineSegment StartX=-14 StartY=-26.5 StartZ=0 EndX=-8.2 EndY=-26.5 EndZ=0
    g10: LineSegment StartX=-10.15 StartY=-12 StartZ=0 EndX=-10.15 EndY=-14 EndZ=0
    g11: LineSegment StartX=-12.8401 StartY=-16 StartZ=0 EndX=-10.1571 EndY=-16 EndZ=0
    g12: LineSegment StartX=-10.15 StartY=-14 StartZ=0 EndX=-8.70761 EndY=-14 EndZ=0
    g13: LineSegment StartX=-12.8401 StartY=-16 StartZ=0 EndX=-12.8401 EndY=-17.6958 EndZ=0
    g14: LineSegment StartX=-10.15 StartY=-12 StartZ=0 EndX=-7.79258 EndY=-12 EndZ=0
    g15: Circle CenterX=-6.2215 CenterY=-2 CenterZ=0 NormalX=0 NormalY=0 NormalZ=1 AngleXU=0 Radius=1
    g16: Circle CenterX=-6.22762 CenterY=-2.58724 CenterZ=0 NormalX=0 NormalY=0 NormalZ=1 AngleXU=0 Radius=1
    g17: Circle CenterX=-6.32538 CenterY=-4 CenterZ=0 NormalX=0 NormalY=0 NormalZ=1 AngleXU=0 Radius=1
    g18: BSplineCurve PolesCount=3 KnotsCount=2 Degree=2 IsPeriodic=0
    g19: GeomPoint X=-6.2215 Y=-2 Z=0
    g20: GeomPoint X=-6.32538 Y=-4 Z=0
    g21: Circle CenterX=-6.48644 CenterY=-5.99526 CenterZ=0 NormalX=0 NormalY=0 NormalZ=1 AngleXU=0 Radius=1
    g22: Circle CenterX=-6.58486 CenterY=-6.99526 CenterZ=0 NormalX=0 NormalY=0 NormalZ=1 AngleXU=0 Radius=1
    g23: Circle CenterX=-6.77343 CenterY=-8 CenterZ=0 NormalX=0 NormalY=0 NormalZ=1 AngleXU=0 Radius=1
    g24: BSplineCurve PolesCount=3 KnotsCount=2 Degree=2 IsPeriodic=0
    g25: GeomPoint X=-6.48644 Y=-5.99526 Z=0
    g26: GeomPoint X=-6.77343 Y=-8 Z=0
    g27: Circle CenterX=-7.19003 CenterY=-10 CenterZ=0 NormalX=0 NormalY=0 NormalZ=1 AngleXU=0 Radius=1
    g28: Circle CenterX=-7.44407 CenterY=-11.0915 CenterZ=0 NormalX=0 NormalY=0 NormalZ=1 AngleXU=0 Radius=1
    g29: Circle CenterX=-7.79258 CenterY=-12 CenterZ=0 NormalX=0 NormalY=0 NormalZ=1 AngleXU=0 Radius=1
    g30: BSplineCurve PolesCount=3 KnotsCount=2 Degree=2 IsPeriodic=0
    g31: GeomPoint X=-7.19003 Y=-10 Z=0
    g32: GeomPoint X=-7.79258 Y=-12 Z=0
    g33: Circle CenterX=-8.70761 CenterY=-14 CenterZ=0 NormalX=0 NormalY=0 NormalZ=1 AngleXU=0 Radius=1
    g34: Circle CenterX=-9.33087 CenterY=-15.1837 CenterZ=0 NormalX=0 NormalY=0 NormalZ=1 AngleXU=0 Radius=1
    g35: Circle CenterX=-10.1571 CenterY=-16 CenterZ=0 NormalX=0 NormalY=0 NormalZ=1 AngleXU=0 Radius=1
    g36: BSplineCurve PolesCount=3 KnotsCount=2 Degree=2 IsPeriodic=0
    g37: GeomPoint X=-8.70761 Y=-14 Z=0
    g38: GeomPoint X=-10.1571 Y=-16 Z=0
    g39: Circle CenterX=-12.8401 CenterY=-17.6958 CenterZ=0 NormalX=0 NormalY=0 NormalZ=1 AngleXU=0 Radius=1
    g40: Circle CenterX=-13.3521 CenterY=-17.9027 CenterZ=0 NormalX=0 NormalY=0 NormalZ=1 AngleXU=0 Radius=1
    g41: Circle CenterX=-14 CenterY=-18 CenterZ=0 NormalX=0 NormalY=0 NormalZ=1 AngleXU=0 Radius=1
    g42: BSplineCurve PolesCount=3 KnotsCount=2 Degree=2 IsPeriodic=0
    g43: GeomPoint X=-12.8401 Y=-17.6958 Z=0
    g44: GeomPoint X=-14 Y=-18 Z=0
    g45: LineSegment StartX=-6.2 StartY=0 StartZ=0 EndX=-7.2 EndY=0 EndZ=0
    g46: LineSegment StartX=-7.2 StartY=0 StartZ=0 EndX=-7.2 EndY=-2 EndZ=0
    g47: LineSegment StartX=-7.2 StartY=-2 StartZ=0 EndX=-6.2215 EndY=-2 EndZ=0
    g48: LineSegment StartX=-6.32538 StartY=-4 StartZ=0 EndX=-7.65538 EndY=-4 EndZ=0
    g49: LineSegment StartX=-7.65538 StartY=-4 StartZ=0 EndX=-7.65538 EndY=-5.99526 EndZ=0
    g50: LineSegment StartX=-7.65538 StartY=-5.99526 StartZ=0 EndX=-6.48644 EndY=-5.99526 EndZ=0
    g51: LineSegment StartX=-6.77343 StartY=-8 StartZ=0 EndX=-8.43343 EndY=-8 EndZ=0
    g52: LineSegment StartX=-8.43343 StartY=-8 StartZ=0 EndX=-8.43343 EndY=-10 EndZ=0
    g53: LineSegment StartX=-8.43343 StartY=-10 StartZ=0 EndX=-7.19003 EndY=-10 EndZ=0
  constraints (112):
    c: Horizontal(g0)
    c: Distance(g0) = 2
    c: Block(g0)
    c: Vertical(g1)
    c: Coincident(g2,g0)
    c: Vertical(g2)
    c: Block(g2)
    c: Coincident(g6,g2)
    c: Weight(g3) = 1
    c: Equal(g3,g4)
    c: Equal(g3,g5)
    c: InternalAlignment(g3,g6)
    c: InternalAlignment(g4,g6)
    c: InternalAlignment(g5,g6)
    c: InternalAlignment(g7,g6)
    c: InternalAlignment(g8,g6)
    c: Block(g6)
    c: Coincident(g9,g1)
    c: Coincident(g9,g6)
    c: Horizontal(g9)
    c: Vertical(g10)
    c: Block(g10)
    c: Horizontal(g11)
    c: Block(g11)
    c: Coincident(g12,g10)
    c: Horizontal(g12)
    c: Block(g12)
    c: Coincident(g13,g11)
    c: Vertical(g13)
    c: Block(g13)
    c: Coincident(g14,g10)
    c: Horizontal(g14)
    c: Block(g14)
    c: Block(g9)
    c: Block(g1)
    c: Weight(g15) = 1
    c: Equal(g15,g16)
    c: Equal(g15,g17)
    c: InternalAlignment(g15,g18)
    c: InternalAlignment(g16,g18)
    c: InternalAlignment(g17,g18)
    c: InternalAlignment(g19,g18)
    c: InternalAlignment(g20,g18)
    c: Weight(g21) = 1
    c: Equal(g21,g22)
    c: Equal(g21,g23)
    c: InternalAlignment(g21,g24)
    c: InternalAlignment(g22,g24)
    c: InternalAlignment(g23,g24)
    c: InternalAlignment(g25,g24)
    c: InternalAlignment(g26,g24)
    c: Weight(g27) = 1
    c: Equal(g27,g28)
    c: Equal(g27,g29)
    c: Coincident(g30,g14)
    c: InternalAlignment(g27,g30)
    c: InternalAlignment(g28,g30)
    c: InternalAlignment(g29,g30)
    c: InternalAlignment(g31,g30)
    c: InternalAlignment(g32,g30)
    c: Coincident(g36,g12)
    c: Weight(g33) = 1
    c: Equal(g33,g34)
    c: Equal(g33,g35)
    c: Coincident(g36,g11)
    c: InternalAlignment(g33,g36)
    c: InternalAlignment(g34,g36)
    c: InternalAlignment(g35,g36)
    c: InternalAlignment(g37,g36)
    c: InternalAlignment(g38,g36)
    c: Coincident(g42,g13)
    c: Weight(g39) = 1
    c: Equal(g39,g40)
    c: Equal(g39,g41)
    c: Coincident(g42,g1)
    c: InternalAlignment(g39,g42)
    c: InternalAlignment(g40,g42)
    c: InternalAlignment(g41,g42)
    c: InternalAlignment(g43,g42)
    c: InternalAlignment(g44,g42)
    c: Block(g18)
    c: Block(g24)
    c: Block(g30)
    c: Block(g36)
    c: Block(g42)
    c: Horizontal(g45)
    c: Coincident(g45,g0)
    c: Vertical(g46)
    c: Coincident(g46,g45)
    c: Coincident(g47,g46)
    c: Coincident(g47,g18)
    c: Horizontal(g47)
    c: Block(g46)
    c: Coincident(g48,g18)
    c: Horizontal(g48)
    c: Distance(g48) = 1.33
    c: Vertical(g49)
    c: Coincident(g49,g48)
    c: Coincident(g50,g49)
    c: Coincident(g50,g24)
    c: Horizontal(g50)
    c: Tangent(g50,g22)
    c: Horizontal(g51)
    c: Coincident(g51,g24)
    c: Block(g51)
    c: Vertical(g52)
    c: Block(g52)
    c: Coincident(g52,g51)
    c: Coincident(g53,g52)
    c: Coincident(g53,g30)
    c: Horizontal(g53)
    c: Distance(g1) = 8.5
FEATURE [Part::Feature] Face024
  shape: bbox 9.8 x 26.5 x 2e-07 mm, 1 faces, 0 solids (baked)
FEATURE [Part::Revolution] Revolve024
  Angle = 360
  Axis = (0,1,0)
  Base = (0,0,0)
  FaceMakerClass = Part::FaceMakerBullseye
  Placement = pos=(0,0,0) rot=(0,0,1;1.5708rad)
  Solid = false
  Source = -> Face024
  Symmetric = false
FEATURE [Part::Feature] Face025
  shape: bbox 9.8 x 26.5 x 2e-07 mm, 1 faces, 0 solids (baked)
FEATURE [Part::Revolution] Revolve025
  Angle = 360
  Axis = (0,1,0)
  Base = (0,0,0)
  FaceMakerClass = Part::FaceMakerBullseye
  Placement = pos=(0,0,0) rot=(0,0,1;1.5708rad)
  Solid = false
  Source = -> Face025
  Symmetric = false
FEATURE [Part::MultiFuse] Fusion033
  Placement = pos=(-18,19,36) rot=(0,0,1;0rad)
  Shapes = -> [Revolve025,Revolve024]
FEATURE [Part::Cylinder] Cylinder014
  Angle = 360
  AttacherType = Attacher::AttachEngine3D
  Height = 20
  Placement = pos=(0,0,36.15) rot=(0,0,1;0rad)
  Radius = 14.3
FEATURE [Part::Cylinder] Cylinder015
  Angle = 360
  AttacherType = Attacher::AttachEngine3D
  Height = 10
  Placement = pos=(0,0,36.15) rot=(0,0,1;0rad)
  Radius = 4
FEATURE [Part::MultiFuse] Fusion034  label="removeToCreteHoleForPlugHousing004"
  Placement = pos=(-42,19,36) rot=(0,1,0;1.5708rad)
  Shapes = -> [Cylinder014,Cylinder015]
FEATURE [Part::Cut] Cut008  label="top004"
  Base = -> Cut004
  Placement = pos=(-1,0,0) rot=(0,0,1;0rad)
  Tool = -> Fusion034
FEATURE [Part::Box] Box005  label="Cube005"
  AttacherType = Attacher::AttachEngine3D
  Height = 28
  Length = 3
  Placement = pos=(110.7,19,22) rot=(0,0,1;0rad)
  Width = 15.7
FEATURE [Part::Cylinder] Cylinder016
  Angle = 360
  AttacherType = Attacher::AttachEngine3D
  Height = 10
  Placement = pos=(0,0,36.15) rot=(0,0,1;0rad)
  Radius = 4
FEATURE [Part::Cylinder] Cylinder017
  Angle = 360
  AttacherType = Attacher::AttachEngine3D
  Height = 20
  Placement = pos=(0,0,36.15) rot=(0,0,1;0rad)
  Radius = 10.3
FEATURE [Part::MultiFuse] Fusion035  label="removeToCreteHoleForPlugHousing005"
  Placement = pos=(70,19,36) rot=(0,1,0;1.5708rad)
  Shapes = -> [Cylinder017,Cylinder016]
FEATURE [Part::Cut] Cut009  label="plugHousingTab001"
  Base = -> Box005
  Placement = pos=(-107.4,-14,0) rot=(0,0,1;0rad)
  Tool = -> Fusion035
FEATURE [Part::Box] Box006  label="Cube006"
  AttacherType = Attacher::AttachEngine3D
  Height = 28
  Length = 3
  Placement = pos=(110.7,19,22) rot=(0,0,1;0rad)
  Width = 15.7
FEATURE [Part::Cylinder] Cylinder018
  Angle = 360
  AttacherType = Attacher::AttachEngine3D
  Height = 10
  Placement = pos=(0,0,36.15) rot=(0,0,1;0rad)
  Radius = 4
FEATURE [Part::Cylinder] Cylinder019
  Angle = 360
  AttacherType = Attacher::AttachEngine3D
  Height = 20
  Placement = pos=(0,0,36.15) rot=(0,0,1;0rad)
  Radius = 10.3
FEATURE [Part::MultiFuse] Fusion036  label="removeToCreteHoleForPlugHousing006"
  Placement = pos=(70,19,36) rot=(0,1,0;1.5708rad)
  Shapes = -> [Cylinder019,Cylinder018]
FEATURE [Part::Cut] Cut010  label="plugHousingTab002"
  Base = -> Box006
  Placement = pos=(-107.4,-14,0) rot=(0,0,1;0rad)
  Tool = -> Fusion036
FEATURE [Part::MultiFuse] Fusion037
  Placement = pos=(9.6,23,0) rot=(0,0,1;3.14159rad)
  Shapes = -> [Cut009,Cut010]
FEATURE [Part::Box] Box  label="Cube"
  AttacherType = Attacher::AttachEngine3D
  Height = 10
  Length = 3
  Placement = pos=(3.3,4,12) rot=(0,0,1;0rad)
  Width = 10
FEATURE [Part::Fillet] Fillet004
  Base = -> Fusion028
  Edges = 1 edges r=2: [Edge25]
FEATURE [Part::Fillet] Fillet005  label="plugHousing046"
  Base = -> Fillet004
  Edges = 1 edges r=2: [Edge8]
FEATURE [Part::Fillet] Fillet006
  Base = -> Box
  Edges = 1 edges r=2: [Edge11]
FEATURE [Part::Box] Box007  label="Cube007"
  AttacherType = Attacher::AttachEngine3D
  Height = 10
  Length = 3
  Placement = pos=(3.3,4,50) rot=(0,0,1;0rad)
  Width = 10
FEATURE [Part::Fillet] Fillet007
  Base = -> Box007
  Edges = 1 edges r=2: [Edge12]
FEATURE [Part::Box] Box008  label="Cube008"
  AttacherType = Attacher::AttachEngine3D
  Height = 28
  Length = 4
  Placement = pos=(5,0,22) rot=(0,0,1;0rad)
  Width = 10
FEATURE [Part::Fillet] Fillet008
  Base = -> Box008
  Edges = 1 edges r=1: [Edge7]
FEATURE [Part::Fillet] Fillet009
  Base = -> Fillet008
  Edges = 1 edges r=2: [Edge5]
FEATURE [Part::Fillet] Fillet010
  Base = -> Fillet009
  Edges = 1 edges r=2: [Edge2]
FEATURE [Sketcher::SketchObject] Sketch009  label="topSketch003"
  FullyConstrained = true
  sketch-geometry (4):
    g0: LineSegment StartX=16.8446 StartY=31.512 StartZ=0 EndX=16.3251 EndY=34.4666 EndZ=0
    g1: ArcOfCircle CenterX=19 CenterY=19.2524 CenterZ=0 NormalX=0 NormalY=0 NormalZ=1 AngleXU=0 Radius=15.4476 StartAngle=1.74483 EndAngle=2.72717
    g2: ArcOfCircle CenterX=19 CenterY=19.2524 CenterZ=0 NormalX=0 NormalY=0 NormalZ=1 AngleXU=0 Radius=12.4476 StartAngle=1.74483 EndAngle=2.73189
    g3: LineSegment StartX=4.86004 StartY=25.4725 StartZ=0 EndX=7.58253 EndY=24.2107 EndZ=0
  constraints (7):
    c: Block(g0)
    c: Coincident(g1,g0)
    c: Coincident(g2,g0)
    c: Coincident(g3,g1)
    c: Coincident(g3,g2)
    c: Block(g1)
    c: Block(g2)
FEATURE [Part::Extrusion] Extrude008
  Base = -> Sketch009
  Dir = (0,0,1)
  DirMode = 2
  FaceMakerClass = Part::FaceMakerBullseye
  LengthFwd = 10
  LengthRev = 0
  Placement = pos=(0,0,31) rot=(0,0,1;0rad)
  Solid = true
  Symmetric = false
FEATURE [Part::Cylinder] Cylinder020
  Angle = 360
  AttacherType = Attacher::AttachEngine3D
  Height = 20
  Placement = pos=(0,0,36.15) rot=(0,0,1;0rad)
  Radius = 8.2
FEATURE [Part::Cylinder] Cylinder021
  Angle = 360
  AttacherType = Attacher::AttachEngine3D
  Height = 10
  Placement = pos=(0,0,36.15) rot=(0,0,1;0rad)
  Radius = 4
FEATURE [Part::MultiFuse] Fusion038  label="removeToCreteHoleForPlugHousing007"
  Placement = pos=(-42,19,36) rot=(0,1,0;1.5708rad)
  Shapes = -> [Cylinder020,Cylinder021]
FEATURE [Part::Cut] Cut011
  Base = -> Extrude008
  Tool = -> Fusion038
FEATURE [Part::Fillet] Fillet011
  Base = -> Cut011
  Edges = 1 edges r=2: [Edge1]
FEATURE [Part::Fillet] Fillet012
  Base = -> Fillet011
  Edges = 1 edges r=2.5: [Edge1]
FEATURE [Part::Fillet] Fillet013
  Base = -> Fillet012
  Edges = 1 edges r=2.5: [Edge2]
FEATURE [Part::Box] Box010  label="Cube010"
  AttacherType = Attacher::AttachEngine3D
  Height = 16
  Length = 8
  Placement = pos=(12.7,31.52,28) rot=(0,0,1;0rad)
  Width = 4
FEATURE [Sketcher::SketchObject] Sketch010  label="topSketch004"
  FullyConstrained = true
  sketch-geometry (4):
    g0: LineSegment StartX=16.8446 StartY=31.512 StartZ=0 EndX=16.3251 EndY=34.4666 EndZ=0
    g1: ArcOfCircle CenterX=19 CenterY=19.2524 CenterZ=0 NormalX=0 NormalY=0 NormalZ=1 AngleXU=0 Radius=15.4476 StartAngle=1.74483 EndAngle=2.72717
    g2: ArcOfCircle CenterX=19 CenterY=19.2524 CenterZ=0 NormalX=0 NormalY=0 NormalZ=1 AngleXU=0 Radius=12.4476 StartAngle=1.74483 EndAngle=2.73189
    g3: LineSegment StartX=4.86004 StartY=25.4725 StartZ=0 EndX=7.58253 EndY=24.2107 EndZ=0
  constraints (7):
    c: Block(g0)
    c: Coincident(g1,g0)
    c: Coincident(g2,g0)
    c: Coincident(g3,g1)
    c: Coincident(g3,g2)
    c: Block(g1)
    c: Block(g2)
FEATURE [Part::Cylinder] Cylinder022
  Angle = 360
  AttacherType = Attacher::AttachEngine3D
  Height = 10
  Placement = pos=(0,0,36.15) rot=(0,0,1;0rad)
  Radius = 4
FEATURE [Sketcher::SketchObject] Sketch011  label="topSketch005"
  FullyConstrained = true
  sketch-geometry (4):
    g0: LineSegment StartX=16.8446 StartY=31.512 StartZ=0 EndX=16.3251 EndY=34.4666 EndZ=0
    g1: ArcOfCircle CenterX=19 CenterY=19.2524 CenterZ=0 NormalX=0 NormalY=0 NormalZ=1 AngleXU=0 Radius=15.4476 StartAngle=1.74483 EndAngle=2.72717
    g2: ArcOfCircle CenterX=19 CenterY=19.2524 CenterZ=0 NormalX=0 NormalY=0 NormalZ=1 AngleXU=0 Radius=12.4476 StartAngle=1.74483 EndAngle=2.73189
    g3: LineSegment StartX=4.86004 StartY=25.4725 StartZ=0 EndX=7.58253 EndY=24.2107 EndZ=0
  constraints (7):
    c: Block(g0)
    c: Coincident(g1,g0)
    c: Coincident(g2,g0)
    c: Coincident(g3,g1)
    c: Coincident(g3,g2)
    c: Block(g1)
    c: Block(g2)
FEATURE [Part::Extrusion] Extrude010
  Base = -> Sketch011
  Dir = (0,0,1)
  DirMode = 2
  FaceMakerClass = Part::FaceMakerBullseye
  LengthFwd = 10.6
  LengthRev = 0
  Placement = pos=(0,0,31) rot=(0,0,1;0rad)
  Solid = true
  Symmetric = false
FEATURE [Part::Cylinder] Cylinder023
  Angle = 360
  AttacherType = Attacher::AttachEngine3D
  Height = 20
  Placement = pos=(0,0,36.15) rot=(0,0,1;0rad)
  Radius = 8.2
FEATURE [Part::MultiFuse] Fusion039  label="removeToCreteHoleForPlugHousing008"
  Placement = pos=(-42,19,36) rot=(0,1,0;1.5708rad)
  Shapes = -> [Cylinder023,Cylinder022]
FEATURE [Part::Cut] Cut012
  Base = -> Extrude010
  Placement = pos=(0,0,-0.3) rot=(0,0,1;0rad)
  Tool = -> Fusion039
FEATURE [Part::Cut] Cut013
  Base = -> Box010
  Tool = -> Cut012
FEATURE [Part::Fillet] Fillet014
  Base = -> Cut013
  Edges = 1 edges r=0.7: [Edge13]
FEATURE [Part::Fillet] Fillet015
  Base = -> Fillet014
  Edges = 1 edges r=0.7: [Edge13]
FEATURE [Part::Fillet] Fillet016
  Base = -> Fillet015
  Edges = 1 edges r=0.7: [Edge16]
FEATURE [Part::Fillet] Fillet017
  Base = -> Fillet016
  Edges = 1 edges r=0.7: [Edge11]
FEATURE [Part::Fillet] Fillet018
  Base = -> Fillet017
  Edges = 1 edges r=0.7: [Edge10]
FEATURE [Part::Fillet] Fillet019
  Base = -> Fillet018
  Edges = 1 edges r=1.2: [Edge5]
FEATURE [Part::Fillet] Fillet020
  Base = -> Fillet019
  Edges = 1 edges r=1.2: [Edge12]
FEATURE [Part::Fillet] Fillet021
  Base = -> Fillet020
  Edges = 1 edges r=2: [Edge1]
  Placement = pos=(0.3,0,0) rot=(0,0,1;0rad)
FEATURE [Part::MultiFuse] Fusion040  label="top005"
  Shapes = -> [Cut008,Fillet021]
FEATURE [Part::MultiFuse] Fusion041  label="wireHolder"
  Shapes = -> [Fusion033,Fillet013]
FEATURE [Part::MultiFuse] Fusion042
  Shapes = -> [Fillet007,Fusion041]
FEATURE [Part::MultiFuse] Fusion043  label="wireHolder001"
  Shapes = -> [Fusion042,Fillet010]
FEATURE [Part::MultiFuse] Fusion044  label="wireHolder002"
  Shapes = -> [Fillet006,Fusion037,Fusion043]
FEATURE [Part::Feature] Face026
  shape: bbox 11 x 6 x 2e-07 mm, 1 faces, 0 solids (baked)
FEATURE [Part::Revolution] Revolve026
  Angle = 360
  Axis = (0,1,0)
  Base = (0,0,0)
  FaceMakerClass = Part::FaceMakerBullseye
  Placement = pos=(30.3,-1,19.7) rot=(0,0,1;0rad)
  Solid = false
  Source = -> Face026
  Symmetric = false
FEATURE [Sketcher::SketchObject] Sketch013  label="topSketch006"
  FullyConstrained = true
  sketch-geometry (13):
    g0: LineSegment StartX=117 StartY=19 StartZ=0 EndX=117 EndY=38 EndZ=0
    g1: ArcOfCircle CenterX=98 CenterY=19 CenterZ=0 NormalX=0 NormalY=0 NormalZ=1 AngleXU=0 Radius=19 StartAngle=5.7297 EndAngle=6.28319
    g2: LineSegment StartX=0 StartY=3 StartZ=0 EndX=0 EndY=19 EndZ=0
    g3: LineSegment StartX=19 StartY=38 StartZ=0 EndX=117 EndY=38 EndZ=0
    g4: ArcOfCircle CenterX=19 CenterY=19 CenterZ=0 NormalX=0 NormalY=0 NormalZ=1 AngleXU=0 Radius=19 StartAngle=1.5708 EndAngle=3.14159
    g5: ArcOfCircle CenterX=19 CenterY=19 CenterZ=0 NormalX=0 NormalY=0 NormalZ=1 AngleXU=0 Radius=16 StartAngle=1.5708 EndAngle=3.14159
    g6: ArcOfCircle CenterX=98 CenterY=19 CenterZ=0 NormalX=0 NormalY=0 NormalZ=1 AngleXU=0 Radius=16 StartAngle=5.60905 EndAngle=6.28319
    g7: LineSegment StartX=114 StartY=19 StartZ=0 EndX=114 EndY=35 EndZ=0
    g8: LineSegment StartX=110.5 StartY=9.01251 StartZ=0 EndX=114.163 EndY=9.01251 EndZ=0
    g9: LineSegment StartX=114 StartY=35 StartZ=0 EndX=19 EndY=35 EndZ=0
    g10: LineSegment StartX=0 StartY=3 StartZ=0 EndX=0 EndY=0 EndZ=0
    g11: LineSegment StartX=3 StartY=0 StartZ=0 EndX=0 EndY=0 EndZ=0
    g12: LineSegment StartX=3 StartY=19 StartZ=0 EndX=3 EndY=0 EndZ=0
  constraints (33):
    c: Vertical(g0)
    c: Distance(g0) = 19
    c: Block(g0)
    c: Coincident(g1,g0)
    c: Block(g1)
    c: Vertical(g2)
    c: Block(g2)
    c: Coincident(g3,g0)
    c: Horizontal(g3)
    c: Distance(g3) = 98
    c: Coincident(g4,g3)
    c: Coincident(g4,g2)
    c: Block(g4)
    c: Coincident(g5,g4)
    c: Coincident(g6,g1)
    c: Block(g6)
    c: Block(g5)
    c: Coincident(g7,g6)
    c: Vertical(g7)
    c: Coincident(g8,g6)
    c: Coincident(g8,g1)
    c: Coincident(g9,g7)
    c: Coincident(g9,g5)
    c: Horizontal(g9)
    c: Tangent(g9,g5)
    c: Coincident(g10,g2)
    c: Distance(g10) = 3
    c: Vertical(g10)
    c: Coincident(g11,g10)
    c: Horizontal(g11)
    c: Coincident(g12,g5)
    c: Coincident(g12,g11)
    c: Vertical(g12)
FEATURE [Part::Extrusion] Extrude011  label="top006"
  Base = -> Sketch013
  Dir = (0,0,1)
  DirMode = 2
  FaceMakerClass = Part::FaceMakerBullseye
  LengthFwd = 72
  LengthRev = 0
  Solid = true
  Symmetric = false
FEATURE [Sketcher::SketchObject] Sketch014
  FullyConstrained = true
  MapMode = 3
  Placement = pos=(0,0,0) rot=(1,0,0;1.5708rad)
  Support = -> [Extrude011]
  sketch-geometry (8):
    g0: Circle CenterX=80.351 CenterY=-67.6202 CenterZ=0 NormalX=0 NormalY=0 NormalZ=1 AngleXU=0 Radius=2
    g1: Circle CenterX=80.351 CenterY=-67.6202 CenterZ=0 NormalX=0 NormalY=0 NormalZ=1 AngleXU=0 Radius=3
    g2: Circle CenterX=80.351 CenterY=-4.92017 CenterZ=0 NormalX=0 NormalY=0 NormalZ=1 AngleXU=0 Radius=2
    g3: Circle CenterX=80.351 CenterY=-4.92017 CenterZ=0 NormalX=0 NormalY=0 NormalZ=1 AngleXU=0 Radius=3
    g4: Circle CenterX=23.851 CenterY=-4.92017 CenterZ=0 NormalX=0 NormalY=0 NormalZ=1 AngleXU=0 Radius=2
    g5: Circle CenterX=23.851 CenterY=-4.92017 CenterZ=0 NormalX=0 NormalY=0 NormalZ=1 AngleXU=0 Radius=3
    g6: Circle CenterX=23.851 CenterY=-67.6202 CenterZ=0 NormalX=0 NormalY=0 NormalZ=1 AngleXU=0 Radius=2
    g7: Circle CenterX=23.851 CenterY=-67.6202 CenterZ=0 NormalX=0 NormalY=0 NormalZ=1 AngleXU=0 Radius=3
  constraints (8):
    c: Block(g3)
    c: Block(g2)
    c: Block(g1)
    c: Block(g0)
    c: Block(g6)
    c: Block(g7)
    c: Block(g4)
    c: Block(g5)
FEATURE [Part::Feature] Face027
  shape: bbox 11 x 6 x 2e-07 mm, 1 faces, 0 solids (baked)
FEATURE [Part::Revolution] Revolve027
  Angle = 360
  Axis = (0,1,0)
  Base = (0,0,0)
  FaceMakerClass = Part::FaceMakerBullseye
  Placement = pos=(30.3,-1,51.7) rot=(0,0,1;0rad)
  Solid = false
  Source = -> Face027
  Symmetric = false
FEATURE [Part::Feature] Face028
  shape: bbox 11 x 6 x 2e-07 mm, 1 faces, 0 solids (baked)
FEATURE [Part::Revolution] Revolve028
  Angle = 360
  Axis = (0,1,0)
  Base = (0,0,0)
  FaceMakerClass = Part::FaceMakerBullseye
  Placement = pos=(62.3,-1,19.7) rot=(0,0,1;0rad)
  Solid = false
  Source = -> Face028
  Symmetric = false
FEATURE [Part::Feature] Face029
  shape: bbox 11 x 6 x 2e-07 mm, 1 faces, 0 solids (baked)
FEATURE [Part::Revolution] Revolve029
  Angle = 360
  Axis = (0,1,0)
  Base = (0,0,0)
  FaceMakerClass = Part::FaceMakerBullseye
  Placement = pos=(62.3,-1,51.7) rot=(0,0,1;0rad)
  Solid = false
  Source = -> Face029
  Symmetric = false
FEATURE [Part::Feature] Wire
  shape: bbox 11 x 5.2 x 2e-07 mm, 0 faces, 0 solids (baked)
FEATURE [Part::Revolution] Revolve030
  Angle = 360
  Axis = (0,1,0)
  Base = (0,0,0)
  FaceMakerClass = Part::FaceMakerBullseye
  Placement = pos=(30.3,38,19.7) rot=(0,0,1;0rad)
  Solid = true
  Source = -> Wire
  Symmetric = false
FEATURE [Part::Feature] Wire001
  shape: bbox 11 x 5.2 x 2e-07 mm, 0 faces, 0 solids (baked)
FEATURE [Part::Revolution] Revolve031
  Angle = 360
  Axis = (0,1,0)
  Base = (0,0,0)
  FaceMakerClass = Part::FaceMakerBullseye
  Placement = pos=(30.3,38,51.7) rot=(0,0,1;0rad)
  Solid = true
  Source = -> Wire001
  Symmetric = false
FEATURE [Part::Feature] Wire002
  shape: bbox 11 x 5.2 x 2e-07 mm, 0 faces, 0 solids (baked)
FEATURE [Part::Revolution] Revolve032
  Angle = 360
  Axis = (0,1,0)
  Base = (0,0,0)
  FaceMakerClass = Part::FaceMakerBullseye
  Placement = pos=(62.3,38,51.7) rot=(0,0,1;0rad)
  Solid = true
  Source = -> Wire002
  Symmetric = false
FEATURE [Part::Feature] Wire003
  shape: bbox 11 x 5.2 x 2e-07 mm, 0 faces, 0 solids (baked)
FEATURE [Part::Revolution] Revolve033
  Angle = 360
  Axis = (0,1,0)
  Base = (0,0,0)
  FaceMakerClass = Part::FaceMakerBullseye
  Placement = pos=(62.3,38,19.7) rot=(0,0,1;0rad)
  Solid = true
  Source = -> Wire003
  Symmetric = false
FEATURE [Part::MultiFuse] Fusion045  label="altRandScrewHousing"
  Shapes = -> [Revolve029,Revolve027,Revolve028,Revolve026]
FEATURE [Part::MultiFuse] Fusion046  label="fanScrewHousing"
  Shapes = -> [Revolve033,Revolve032,Revolve031,Revolve030]
FEATURE [Sketcher::SketchObject] Sketch015
  FullyConstrained = true
  sketch-geometry (17):
    g0: Circle CenterX=-3.5 CenterY=23.5 CenterZ=0 NormalX=0 NormalY=0 NormalZ=1 AngleXU=0 Radius=1
    g1: Circle CenterX=-1 CenterY=15.25 CenterZ=0 NormalX=0 NormalY=0 NormalZ=1 AngleXU=0 Radius=1
    g2: Circle CenterX=-3.5 CenterY=7 CenterZ=0 NormalX=0 NormalY=0 NormalZ=1 AngleXU=0 Radius=1
    g3: BSplineCurve PolesCount=3 KnotsCount=2 Degree=2 IsPeriodic=0
    g4: GeomPoint X=-3.5 Y=23.5 Z=0
    g5: GeomPoint X=-3.5 Y=7 Z=0
    g6: Circle CenterX=-4.8 CenterY=30.5 CenterZ=0 NormalX=0 NormalY=0 NormalZ=1 AngleXU=0 Radius=1
    g7: Circle CenterX=-3.5 CenterY=30.5 CenterZ=0 NormalX=0 NormalY=0 NormalZ=1 AngleXU=0 Radius=1
    g8: Circle CenterX=-3.5 CenterY=29.2 CenterZ=0 NormalX=0 NormalY=0 NormalZ=1 AngleXU=0 Radius=1
    g9: BSplineCurve PolesCount=3 KnotsCount=2 Degree=2 IsPeriodic=0
    g10: GeomPoint X=-4.8 Y=30.5 Z=0
    g11: GeomPoint X=-3.5 Y=29.2 Z=0
    g12: LineSegment StartX=-3.5 StartY=29.2 StartZ=0 EndX=-3.5 EndY=23.5 EndZ=0
    g13: LineSegment StartX=-4.8 StartY=30.5 StartZ=0 EndX=0 EndY=30.5 EndZ=0
    g14: LineSegment StartX=-3.5 StartY=0.3 StartZ=0 EndX=0 EndY=0.3 EndZ=0
    g15: LineSegment StartX=-3.5 StartY=0.3 StartZ=0 EndX=-3.5 EndY=7 EndZ=0
    g16: LineSegment StartX=0 StartY=0.3 StartZ=0 EndX=0 EndY=30.5 EndZ=0
  constraints (34):
    c: Weight(g0) = 1
    c: Equal(g0,g1)
    c: Equal(g0,g2)
    c: InternalAlignment(g0,g3)
    c: InternalAlignment(g1,g3)
    c: InternalAlignment(g2,g3)
    c: InternalAlignment(g4,g3)
    c: InternalAlignment(g5,g3)
    c: Block(g3)
    c: Weight(g6) = 1
    c: Equal(g6,g7)
    c: Equal(g6,g8)
    c: InternalAlignment(g6,g9)
    c: InternalAlignment(g7,g9)
    c: InternalAlignment(g8,g9)
    c: InternalAlignment(g10,g9)
    c: InternalAlignment(g11,g9)
    c: Block(g9)
    c: Coincident(g12,g9)
    c: Coincident(g12,g3)
    c: Vertical(g12)
    c: Coincident(g13,g9)
    c: Horizontal(g13)
    c: Distance(g13) = 4.8
    c: Horizontal(g14)
    c: Block(g14)
    c: Coincident(g15,g14)
    c: Coincident(g15,g3)
    c: Vertical(g15)
    c: Coincident(g16,g14)
    c: Coincident(g16,g13)
    c: Vertical(g16)
    c: Tangent(g16,g1)
    c: Distance(g14) = 3.5
FEATURE [Sketcher::SketchObject] Sketch016
  FullyConstrained = true
  sketch-geometry (16):
    g0: Circle CenterX=-3.5 CenterY=23.5 CenterZ=0 NormalX=0 NormalY=0 NormalZ=1 AngleXU=0 Radius=1
    g1: Circle CenterX=-1 CenterY=15.25 CenterZ=0 NormalX=0 NormalY=0 NormalZ=1 AngleXU=0 Radius=1
    g2: Circle CenterX=-3.5 CenterY=7 CenterZ=0 NormalX=0 NormalY=0 NormalZ=1 AngleXU=0 Radius=1
    g3: BSplineCurve PolesCount=3 KnotsCount=2 Degree=2 IsPeriodic=0
    g4: GeomPoint X=-3.5 Y=23.5 Z=0
    g5: GeomPoint X=-3.5 Y=7 Z=0
    g6: LineSegment StartX=-3.5 StartY=28.2 StartZ=0 EndX=-3.5 EndY=23.5 EndZ=0
    g7: LineSegment StartX=0 StartY=29.5 StartZ=0 EndX=0 EndY=30 EndZ=0
    g8: LineSegment StartX=-3.5 StartY=28.2 StartZ=0 EndX=-3.5 EndY=30 EndZ=0
    g9: LineSegment StartX=0 StartY=30 StartZ=0 EndX=0 EndY=30.5 EndZ=0
    g10: LineSegment StartX=0 StartY=30.5 StartZ=0 EndX=-3.5 EndY=30.5 EndZ=0
    g11: LineSegment StartX=-3.5 StartY=30.5 StartZ=0 EndX=-3.5 EndY=30 EndZ=0
    g12: LineSegment StartX=0 StartY=29.5 StartZ=0 EndX=0 EndY=5 EndZ=0
    g13: LineSegment StartX=-3.5 StartY=0.3 StartZ=0 EndX=-3.5 EndY=7 EndZ=0
    g14: LineSegment StartX=-3.5 StartY=0.3 StartZ=0 EndX=0 EndY=0.3 EndZ=0
    g15: LineSegment StartX=0 StartY=5 StartZ=0 EndX=0 EndY=0.3 EndZ=0
  constraints (39):
    c: Weight(g0) = 1
    c: Equal(g0,g1)
    c: Equal(g0,g2)
    c: InternalAlignment(g0,g3)
    c: InternalAlignment(g1,g3)
    c: InternalAlignment(g2,g3)
    c: InternalAlignment(g4,g3)
    c: InternalAlignment(g5,g3)
    c: Block(g3)
    c: Coincident(g6,g3)
    c: Vertical(g6)
    c: Vertical(g7)
    c: Distance(g7) = 0.5
    c: Coincident(g8,g6)
    c: Vertical(g8)
    c: Block(g6)
    c: Block(g7)
    c: Vertical(g9)
    c: Equal(g7,g9) = 0.5
    c: Block(g9)
    c: Coincident(g9,g7)
    c: Horizontal(g10)
    c: Coincident(g10,g9)
    c: Coincident(g11,g10)
    c: Coincident(g11,g8)
    c: Vertical(g11)
    c: Block(g11)
    c: Coincident(g12,g7)
    c: Vertical(g12)
    c: Coincident(g13,g3)
    c: Vertical(g13)
    c: Distance(g13) = 6.7
    c: Coincident(g14,g13)
    c: Horizontal(g14)
    c: Block(g14)
    c: Coincident(g15,g12)
    c: Coincident(g15,g14)
    c: Vertical(g15)
    c: Block(g15)
FEATURE [Sketcher::SketchObject] Sketch017
  FullyConstrained = true
  sketch-geometry (11):
    g0: LineSegment StartX=-3.5 StartY=1e-16 StartZ=0 EndX=-1.6 EndY=1e-16 EndZ=0
    g1: LineSegment StartX=-1.6 StartY=1e-16 StartZ=0 EndX=-1.6 EndY=1.5 EndZ=0
    g2: LineSegment StartX=-3.5 StartY=1.5 StartZ=0 EndX=-1.6 EndY=1.5 EndZ=0
    g3: LineSegment StartX=-3.5 StartY=1e-16 StartZ=0 EndX=-4.8 EndY=1e-16 EndZ=0
    g4: Circle CenterX=-3.5 CenterY=1.3 CenterZ=0 NormalX=0 NormalY=0 NormalZ=1 AngleXU=0 Radius=1
    g5: Circle CenterX=-3.5 CenterY=1e-16 CenterZ=0 NormalX=0 NormalY=0 NormalZ=1 AngleXU=0 Radius=1
    g6: Circle CenterX=-4.8 CenterY=1e-16 CenterZ=0 NormalX=0 NormalY=0 NormalZ=1 AngleXU=0 Radius=1
    g7: BSplineCurve PolesCount=3 KnotsCount=2 Degree=2 IsPeriodic=0
    g8: GeomPoint X=-3.5 Y=1.3 Z=0
    g9: GeomPoint X=-4.8 Y=1e-16 Z=0
    g10: LineSegment StartX=-3.5 StartY=1.3 StartZ=0 EndX=-3.5 EndY=1.5 EndZ=0
  constraints (24):
    c: Horizontal(g0)
    c: Distance(g0) = 1.9
    c: Block(g0)
    c: Coincident(g1,g0)
    c: Vertical(g1)
    c: Coincident(g2,g1)
    c: Horizontal(g2)
    c: Coincident(g3,g0)
    c: Horizontal(g3)
    c: Distance(g3) = 1.3
    c: Weight(g4) = 1
    c: Equal(g4,g5)
    c: Coincident(g5,g0)
    c: Equal(g4,g6)
    c: Coincident(g7,g3)
    c: InternalAlignment(g4,g7)
    c: InternalAlignment(g5,g7)
    c: InternalAlignment(g6,g7)
    c: InternalAlignment(g8,g7)
    c: InternalAlignment(g9,g7)
    c: Coincident(g10,g7)
    c: Coincident(g10,g2)
    c: Vertical(g10)
    c: Block(g10)
FEATURE [Part::Feature] Face035
  shape: bbox 3.2 x 1.5 x 2e-07 mm, 1 faces, 0 solids (baked)
FEATURE [Part::Revolution] Revolve039  label="backCaseScrewRetainer"
  Angle = 360
  Axis = (0,1,0)
  Base = (0,0,0)
  FaceMakerClass = Part::FaceMakerBullseye
  Placement = pos=(12.5,3,62) rot=(0,0,1;0rad)
  Solid = false
  Source = -> Face035
  Symmetric = false
FEATURE [Part::Feature] Face036
  shape: bbox 3.2 x 1.5 x 2e-07 mm, 1 faces, 0 solids (baked)
FEATURE [Part::Feature] Face039
  shape: bbox 4.8 x 30.2 x 2e-07 mm, 1 faces, 0 solids (baked)
FEATURE [Part::Revolution] Revolve043  label="frontCaseScrewPost002"
  Angle = 360
  Axis = (0,1,0)
  Base = (0,0,0)
  FaceMakerClass = Part::FaceMakerBullseye
  Placement = pos=(89.5,4.5,3.5) rot=(0,0,1;0rad)
  Solid = false
  Source = -> Face039
  Symmetric = false
FEATURE [Part::Feature] Face042
  shape: bbox 4.8 x 30.2 x 2e-07 mm, 1 faces, 0 solids (baked)
FEATURE [Part::Revolution] Revolve046  label="frontCaseScrewPost003"
  Angle = 360
  Axis = (0,1,0)
  Base = (0,0,0)
  FaceMakerClass = Part::FaceMakerBullseye
  Placement = pos=(89.5,4.5,68.5) rot=(0,0,1;0rad)
  Solid = false
  Source = -> Face042
  Symmetric = false
FEATURE [Part::Feature] Face043
  shape: bbox 3.2 x 1.5 x 2e-07 mm, 1 faces, 0 solids (baked)
FEATURE [Part::Revolution] Revolve047  label="frontCaseScrewRetainer002"
  Angle = 360
  Axis = (0,1,0)
  Base = (0,0,0)
  FaceMakerClass = Part::FaceMakerBullseye
  Placement = pos=(89.5,3,68.5) rot=(0,0,1;0rad)
  Solid = false
  Source = -> Face043
  Symmetric = false
FEATURE [Part::Feature] Face044
  shape: bbox 3.2 x 1.5 x 2e-07 mm, 1 faces, 0 solids (baked)
FEATURE [Part::Revolution] Revolve048  label="frontCaseScrewRetainer003"
  Angle = 360
  Axis = (0,1,0)
  Base = (0,0,0)
  FaceMakerClass = Part::FaceMakerBullseye
  Placement = pos=(89.5,3,3.5) rot=(0,0,1;0rad)
  Solid = false
  Source = -> Face044
  Symmetric = false
FEATURE [App::MeasureDistance] Distance002  label="Distance: 1.67 mm"
  Distance = 1.66921
  P1 = (99.2361,4.7524,71.7)
  P2 = (99.2347,6.42161,71.7)
FEATURE [Sketcher::SketchObject] Sketch018
  FullyConstrained = true
  sketch-geometry (7):
    g0: LineSegment StartX=0 StartY=0 StartZ=0 EndX=0 EndY=6 EndZ=0
    g1: Circle CenterX=0 CenterY=0 CenterZ=0 NormalX=0 NormalY=0 NormalZ=1 AngleXU=0 Radius=1
    g2: Circle CenterX=8 CenterY=6 CenterZ=0 NormalX=0 NormalY=0 NormalZ=1 AngleXU=0 Radius=1
    g3: BSplineCurve PolesCount=3 KnotsCount=2 Degree=2 IsPeriodic=0
    g4: GeomPoint X=0 Y=0 Z=0
    g5: GeomPoint X=8 Y=6 Z=0
    g6: LineSegment StartX=0 StartY=6 StartZ=0 EndX=8 EndY=6 EndZ=0
  constraints (14):
    c: Coincident(g0,g-1)
    c: Distance(g0) = 6
    c: Vertical(g0)
    c: Coincident(g3,g0)
    c: Weight(g1) = 1
    c: Equal(g1,g2)
    c: InternalAlignment(g1,g3)
    c: InternalAlignment(g2,g3)
    c: InternalAlignment(g4,g3)
    c: InternalAlignment(g5,g3)
    c: Block(g3)
    c: Coincident(g6,g0)
    c: Coincident(g6,g3)
    c: Horizontal(g6)
FEATURE [Part::Extrusion] Extrude012  label="caseScrewPillarBracket"
  Base = -> Sketch018
  Dir = (0,0,1)
  DirMode = 2
  FaceMakerClass = Part::FaceMakerBullseye
  LengthFwd = 2.4
  LengthRev = 0
  Placement = pos=(15.76,29,8.8) rot=(0,1,0;0rad)
  Solid = true
  Symmetric = false
FEATURE [Sketcher::SketchObject] Sketch019
  FullyConstrained = true
  sketch-geometry (7):
    g0: LineSegment StartX=0 StartY=0 StartZ=0 EndX=0 EndY=6 EndZ=0
    g1: Circle CenterX=0 CenterY=0 CenterZ=0 NormalX=0 NormalY=0 NormalZ=1 AngleXU=0 Radius=1
    g2: Circle CenterX=8 CenterY=6 CenterZ=0 NormalX=0 NormalY=0 NormalZ=1 AngleXU=0 Radius=1
    g3: BSplineCurve PolesCount=3 KnotsCount=2 Degree=2 IsPeriodic=0
    g4: GeomPoint X=0 Y=0 Z=0
    g5: GeomPoint X=8 Y=6 Z=0
    g6: LineSegment StartX=0 StartY=6 StartZ=0 EndX=8 EndY=6 EndZ=0
  constraints (14):
    c: Coincident(g0,g-1)
    c: Distance(g0) = 6
    c: Vertical(g0)
    c: Coincident(g3,g0)
    c: Weight(g1) = 1
    c: Equal(g1,g2)
    c: InternalAlignment(g1,g3)
    c: InternalAlignment(g2,g3)
    c: InternalAlignment(g4,g3)
    c: InternalAlignment(g5,g3)
    c: Block(g3)
    c: Coincident(g6,g0)
    c: Coincident(g6,g3)
    c: Horizontal(g6)
FEATURE [Part::Extrusion] Extrude013  label="caseScrewPillarBracket001"
  Base = -> Sketch019
  Dir = (0,0,1)
  DirMode = 2
  FaceMakerClass = Part::FaceMakerBullseye
  LengthFwd = 2.4
  LengthRev = 0
  Placement = pos=(15.76,29,60.8) rot=(0,0,1;0rad)
  Solid = true
  Symmetric = false
FEATURE [Sketcher::SketchObject] Sketch020
  FullyConstrained = true
  sketch-geometry (7):
    g0: LineSegment StartX=0 StartY=0 StartZ=0 EndX=0 EndY=6 EndZ=0
    g1: Circle CenterX=0 CenterY=0 CenterZ=0 NormalX=0 NormalY=0 NormalZ=1 AngleXU=0 Radius=1
    g2: Circle CenterX=8 CenterY=6 CenterZ=0 NormalX=0 NormalY=0 NormalZ=1 AngleXU=0 Radius=1
    g3: BSplineCurve PolesCount=3 KnotsCount=2 Degree=2 IsPeriodic=0
    g4: GeomPoint X=0 Y=0 Z=0
    g5: GeomPoint X=8 Y=6 Z=0
    g6: LineSegment StartX=0 StartY=6 StartZ=0 EndX=8 EndY=6 EndZ=0
  constraints (14):
    c: Coincident(g0,g-1)
    c: Distance(g0) = 6
    c: Vertical(g0)
    c: Coincident(g3,g0)
    c: Weight(g1) = 1
    c: Equal(g1,g2)
    c: InternalAlignment(g1,g3)
    c: InternalAlignment(g2,g3)
    c: InternalAlignment(g4,g3)
    c: InternalAlignment(g5,g3)
    c: Block(g3)
    c: Coincident(g6,g0)
    c: Coincident(g6,g3)
    c: Horizontal(g6)
FEATURE [Part::Extrusion] Extrude014  label="caseScrewPillarBracket002"
  Base = -> Sketch020
  Dir = (0,0,1)
  DirMode = 2
  FaceMakerClass = Part::FaceMakerBullseye
  LengthFwd = 2.4
  LengthRev = 0
  Placement = pos=(13.7,29,13.26) rot=(0,-1,0;1.5708rad)
  Solid = true
  Symmetric = false
FEATURE [Sketcher::SketchObject] Sketch021
  FullyConstrained = true
  sketch-geometry (7):
    g0: LineSegment StartX=0 StartY=0 StartZ=0 EndX=0 EndY=6 EndZ=0
    g1: Circle CenterX=0 CenterY=0 CenterZ=0 NormalX=0 NormalY=0 NormalZ=1 AngleXU=0 Radius=1
    g2: Circle CenterX=8 CenterY=6 CenterZ=0 NormalX=0 NormalY=0 NormalZ=1 AngleXU=0 Radius=1
    g3: BSplineCurve PolesCount=3 KnotsCount=2 Degree=2 IsPeriodic=0
    g4: GeomPoint X=0 Y=0 Z=0
    g5: GeomPoint X=8 Y=6 Z=0
    g6: LineSegment StartX=0 StartY=6 StartZ=0 EndX=8 EndY=6 EndZ=0
  constraints (14):
    c: Coincident(g0,g-1)
    c: Distance(g0) = 6
    c: Vertical(g0)
    c: Coincident(g3,g0)
    c: Weight(g1) = 1
    c: Equal(g1,g2)
    c: InternalAlignment(g1,g3)
    c: InternalAlignment(g2,g3)
    c: InternalAlignment(g4,g3)
    c: InternalAlignment(g5,g3)
    c: Block(g3)
    c: Coincident(g6,g0)
    c: Coincident(g6,g3)
    c: Horizontal(g6)
FEATURE [Part::Extrusion] Extrude015  label="caseScrewPillarBracket003"
  Base = -> Sketch021
  Dir = (0,0,1)
  DirMode = 2
  FaceMakerClass = Part::FaceMakerBullseye
  LengthFwd = 2.4
  LengthRev = 0
  Placement = pos=(11.3,29,58.74) rot=(0,1,0;1.5708rad)
  Solid = true
  Symmetric = false
FEATURE [Sketcher::SketchObject] Sketch022
  FullyConstrained = true
  sketch-geometry (7):
    g0: LineSegment StartX=0 StartY=0 StartZ=0 EndX=0 EndY=6 EndZ=0
    g1: Circle CenterX=0 CenterY=0 CenterZ=0 NormalX=0 NormalY=0 NormalZ=1 AngleXU=0 Radius=1
    g2: Circle CenterX=8 CenterY=6 CenterZ=0 NormalX=0 NormalY=0 NormalZ=1 AngleXU=0 Radius=1
    g3: BSplineCurve PolesCount=3 KnotsCount=2 Degree=2 IsPeriodic=0
    g4: GeomPoint X=0 Y=0 Z=0
    g5: GeomPoint X=8 Y=6 Z=0
    g6: LineSegment StartX=0 StartY=6 StartZ=0 EndX=8 EndY=6 EndZ=0
  constraints (14):
    c: Coincident(g0,g-1)
    c: Distance(g0) = 6
    c: Vertical(g0)
    c: Coincident(g3,g0)
    c: Weight(g1) = 1
    c: Equal(g1,g2)
    c: InternalAlignment(g1,g3)
    c: InternalAlignment(g2,g3)
    c: InternalAlignment(g4,g3)
    c: InternalAlignment(g5,g3)
    c: Block(g3)
    c: Coincident(g6,g0)
    c: Coincident(g6,g3)
    c: Horizontal(g6)
FEATURE [Part::Extrusion] Extrude016  label="caseScrewPillarBracket004"
  Base = -> Sketch022
  Dir = (0,0,1)
  DirMode = 2
  FaceMakerClass = Part::FaceMakerBullseye
  LengthFwd = 2.4
  LengthRev = 0
  Placement = pos=(88.3,29,65.23) rot=(0,1,0;1.5708rad)
  Solid = true
  Symmetric = false
FEATURE [Sketcher::SketchObject] Sketch023
  FullyConstrained = true
  sketch-geometry (7):
    g0: LineSegment StartX=0 StartY=0 StartZ=0 EndX=0 EndY=6 EndZ=0
    g1: Circle CenterX=0 CenterY=0 CenterZ=0 NormalX=0 NormalY=0 NormalZ=1 AngleXU=0 Radius=1
    g2: Circle CenterX=8 CenterY=6 CenterZ=0 NormalX=0 NormalY=0 NormalZ=1 AngleXU=0 Radius=1
    g3: BSplineCurve PolesCount=3 KnotsCount=2 Degree=2 IsPeriodic=0
    g4: GeomPoint X=0 Y=0 Z=0
    g5: GeomPoint X=8 Y=6 Z=0
    g6: LineSegment StartX=0 StartY=6 StartZ=0 EndX=8 EndY=6 EndZ=0
  constraints (14):
    c: Coincident(g0,g-1)
    c: Distance(g0) = 6
    c: Vertical(g0)
    c: Coincident(g3,g0)
    c: Weight(g1) = 1
    c: Equal(g1,g2)
    c: InternalAlignment(g1,g3)
    c: InternalAlignment(g2,g3)
    c: InternalAlignment(g4,g3)
    c: InternalAlignment(g5,g3)
    c: Block(g3)
    c: Coincident(g6,g0)
    c: Coincident(g6,g3)
    c: Horizontal(g6)
FEATURE [Part::Extrusion] Extrude017  label="caseScrewPillarBracket005"
  Base = -> Sketch023
  Dir = (0,0,1)
  DirMode = 2
  FaceMakerClass = Part::FaceMakerBullseye
  LengthFwd = 2.4
  LengthRev = 0
  Placement = pos=(90.7,29,6.77) rot=(0,-1,0;1.5708rad)
  Solid = true
  Symmetric = false
FEATURE [Sketcher::SketchObject] Sketch024
  FullyConstrained = true
  sketch-geometry (7):
    g0: LineSegment StartX=0 StartY=0 StartZ=0 EndX=0 EndY=6 EndZ=0
    g1: Circle CenterX=0 CenterY=0 CenterZ=0 NormalX=0 NormalY=0 NormalZ=1 AngleXU=0 Radius=1
    g2: Circle CenterX=8 CenterY=6 CenterZ=0 NormalX=0 NormalY=0 NormalZ=1 AngleXU=0 Radius=1
    g3: BSplineCurve PolesCount=3 KnotsCount=2 Degree=2 IsPeriodic=0
    g4: GeomPoint X=0 Y=0 Z=0
    g5: GeomPoint X=8 Y=6 Z=0
    g6: LineSegment StartX=0 StartY=6 StartZ=0 EndX=8 EndY=6 EndZ=0
  constraints (14):
    c: Coincident(g0,g-1)
    c: Distance(g0) = 6
    c: Vertical(g0)
    c: Coincident(g3,g0)
    c: Weight(g1) = 1
    c: Equal(g1,g2)
    c: InternalAlignment(g1,g3)
    c: InternalAlignment(g2,g3)
    c: InternalAlignment(g4,g3)
    c: InternalAlignment(g5,g3)
    c: Block(g3)
    c: Coincident(g6,g0)
    c: Coincident(g6,g3)
    c: Horizontal(g6)
FEATURE [Part::Extrusion] Extrude018  label="caseScrewPillarBracket006"
  Base = -> Sketch024
  Dir = (0,0,1)
  DirMode = 2
  FaceMakerClass = Part::FaceMakerBullseye
  LengthFwd = 2.4
  LengthRev = 0
  Placement = pos=(103.7,29,6.77) rot=(0,-1,0;1.5708rad)
  Solid = true
  Symmetric = false
FEATURE [Sketcher::SketchObject] Sketch025
  FullyConstrained = true
  sketch-geometry (7):
    g0: LineSegment StartX=0 StartY=0 StartZ=0 EndX=0 EndY=6 EndZ=0
    g1: Circle CenterX=0 CenterY=0 CenterZ=0 NormalX=0 NormalY=0 NormalZ=1 AngleXU=0 Radius=1
    g2: Circle CenterX=8 CenterY=6 CenterZ=0 NormalX=0 NormalY=0 NormalZ=1 AngleXU=0 Radius=1
    g3: BSplineCurve PolesCount=3 KnotsCount=2 Degree=2 IsPeriodic=0
    g4: GeomPoint X=0 Y=0 Z=0
    g5: GeomPoint X=8 Y=6 Z=0
    g6: LineSegment StartX=0 StartY=6 StartZ=0 EndX=8 EndY=6 EndZ=0
  constraints (14):
    c: Coincident(g0,g-1)
    c: Distance(g0) = 6
    c: Vertical(g0)
    c: Coincident(g3,g0)
    c: Weight(g1) = 1
    c: Equal(g1,g2)
    c: InternalAlignment(g1,g3)
    c: InternalAlignment(g2,g3)
    c: InternalAlignment(g4,g3)
    c: InternalAlignment(g5,g3)
    c: Block(g3)
    c: Coincident(g6,g0)
    c: Coincident(g6,g3)
    c: Horizontal(g6)
FEATURE [Part::Extrusion] Extrude019  label="caseScrewPillarBracket007"
  Base = -> Sketch025
  Dir = (0,0,1)
  DirMode = 2
  FaceMakerClass = Part::FaceMakerBullseye
  LengthFwd = 2.4
  LengthRev = 0
  Placement = pos=(101.3,29,65.23) rot=(0,1,0;1.5708rad)
  Solid = true
  Symmetric = false
FEATURE [Part::Box] Box011  label="frontCaseScrewPillarBracket"
  AttacherType = Attacher::AttachEngine3D
  Height = 2.4
  Length = 16
  Placement = pos=(87,28,2.3) rot=(0,0,1;0rad)
  Width = 7
FEATURE [Part::Box] Box012  label="frontCaseScrewPillarBracket001"
  AttacherType = Attacher::AttachEngine3D
  Height = 2.4
  Length = 16
  Placement = pos=(87,28,67.3) rot=(0,0,1;0rad)
  Width = 7
FEATURE [Sketcher::SketchObject] Sketch026
  FullyConstrained = true
  sketch-geometry (17):
    g0: Circle CenterX=-3.5 CenterY=23.5 CenterZ=0 NormalX=0 NormalY=0 NormalZ=1 AngleXU=0 Radius=1
    g1: Circle CenterX=-1 CenterY=15.25 CenterZ=0 NormalX=0 NormalY=0 NormalZ=1 AngleXU=0 Radius=1
    g2: Circle CenterX=-3.5 CenterY=7 CenterZ=0 NormalX=0 NormalY=0 NormalZ=1 AngleXU=0 Radius=1
    g3: BSplineCurve PolesCount=3 KnotsCount=2 Degree=2 IsPeriodic=0
    g4: GeomPoint X=-3.5 Y=23.5 Z=0
    g5: GeomPoint X=-3.5 Y=7 Z=0
    g6: Circle CenterX=-4.8 CenterY=30.5 CenterZ=0 NormalX=0 NormalY=0 NormalZ=1 AngleXU=0 Radius=1
    g7: Circle CenterX=-3.5 CenterY=30.5 CenterZ=0 NormalX=0 NormalY=0 NormalZ=1 AngleXU=0 Radius=1
    g8: Circle CenterX=-3.5 CenterY=29.2 CenterZ=0 NormalX=0 NormalY=0 NormalZ=1 AngleXU=0 Radius=1
    g9: BSplineCurve PolesCount=3 KnotsCount=2 Degree=2 IsPeriodic=0
    g10: GeomPoint X=-4.8 Y=30.5 Z=0
    g11: GeomPoint X=-3.5 Y=29.2 Z=0
    g12: LineSegment StartX=-3.5 StartY=29.2 StartZ=0 EndX=-3.5 EndY=23.5 EndZ=0
    g13: LineSegment StartX=-4.8 StartY=30.5 StartZ=0 EndX=0 EndY=30.5 EndZ=0
    g14: LineSegment StartX=-3.5 StartY=5 StartZ=0 EndX=-3.5 EndY=7 EndZ=0
    g15: LineSegment StartX=0 StartY=5 StartZ=0 EndX=0 EndY=30.5 EndZ=0
    g16: LineSegment StartX=-3.5 StartY=5 StartZ=0 EndX=0 EndY=5 EndZ=0
  constraints (33):
    c: Weight(g0) = 1
    c: Equal(g0,g1)
    c: Equal(g0,g2)
    c: InternalAlignment(g0,g3)
    c: InternalAlignment(g1,g3)
    c: InternalAlignment(g2,g3)
    c: InternalAlignment(g4,g3)
    c: InternalAlignment(g5,g3)
    c: Block(g3)
    c: Weight(g6) = 1
    c: Equal(g6,g7)
    c: Equal(g6,g8)
    c: InternalAlignment(g6,g9)
    c: InternalAlignment(g7,g9)
    c: InternalAlignment(g8,g9)
    c: InternalAlignment(g10,g9)
    c: InternalAlignment(g11,g9)
    c: Block(g9)
    c: Coincident(g12,g9)
    c: Coincident(g12,g3)
    c: Vertical(g12)
    c: Coincident(g13,g9)
    c: Horizontal(g13)
    c: Distance(g13) = 4.8
    c: Coincident(g14,g3)
    c: Vertical(g14)
    c: Coincident(g15,g13)
    c: Vertical(g15)
    c: Tangent(g15,g1)
    c: Distance(g14) = 2
    c: Coincident(g16,g14)
    c: Horizontal(g16)
    c: Coincident(g15,g16)
FEATURE [Part::Feature] Face050
  shape: bbox 4.8 x 25.5 x 2e-07 mm, 1 faces, 0 solids (baked)
FEATURE [Part::Revolution] Revolve054  label="moreFrontCaseScrewPost001"
  Angle = 360
  Axis = (0,1,0)
  Base = (0,0,0)
  FaceMakerClass = Part::FaceMakerBullseye
  Placement = pos=(102.5,4.5,3.5) rot=(0,0,1;0rad)
  Solid = false
  Source = -> Face050
  Symmetric = false
FEATURE [Part::Feature] Face051
  shape: bbox 4.8 x 25.5 x 2e-07 mm, 1 faces, 0 solids (baked)
FEATURE [Part::Revolution] Revolve055  label="moreFrontCaseScrewPost002"
  Angle = 360
  Axis = (0,1,0)
  Base = (0,0,0)
  FaceMakerClass = Part::FaceMakerBullseye
  Placement = pos=(102.5,4.5,68.5) rot=(0,0,1;0rad)
  Solid = false
  Source = -> Face051
  Symmetric = false
FEATURE [Sketcher::SketchObject] Sketch027
  FullyConstrained = true
  sketch-geometry (10):
    g0: LineSegment StartX=-1.6 StartY=4.7 StartZ=0 EndX=-1.6 EndY=1.7 EndZ=0
    g1: LineSegment StartX=-3.5 StartY=4.7 StartZ=0 EndX=-1.6 EndY=4.7 EndZ=0
    g2: LineSegment StartX=-1.6 StartY=1.7 StartZ=0 EndX=-1.6 EndY=1.5 EndZ=0
    g3: LineSegment StartX=-1.6 StartY=1.5 StartZ=0 EndX=-5.2 EndY=1.5 EndZ=0
    g4: Circle CenterX=-3.5 CenterY=4.7 CenterZ=0 NormalX=0 NormalY=0 NormalZ=1 AngleXU=0 Radius=1
    g5: Circle CenterX=-3.59627 CenterY=2.99743 CenterZ=0 NormalX=0 NormalY=0 NormalZ=1 AngleXU=0 Radius=1
    g6: Circle CenterX=-5.2 CenterY=1.5 CenterZ=0 NormalX=0 NormalY=0 NormalZ=1 AngleXU=0 Radius=1
    g7: BSplineCurve PolesCount=3 KnotsCount=2 Degree=2 IsPeriodic=0
    g8: GeomPoint X=-3.5 Y=4.7 Z=0
    g9: GeomPoint X=-5.2 Y=1.5 Z=0
  constraints (23):
    c: Vertical(g0)
    c: Distance(g0) = 3
    c: Coincident(g1,g0)
    c: Horizontal(g1)
    c: Block(g0)
    c: Block(g1)
    c: Coincident(g2,g0)
    c: Vertical(g2)
    c: Distance(g2) = 0.2
    c: Coincident(g3,g2)
    c: Horizontal(g3)
    c: Block(g3)
    c: Coincident(g7,g1)
    c: Weight(g4) = 1
    c: Equal(g4,g5)
    c: Equal(g4,g6)
    c: Coincident(g7,g3)
    c: InternalAlignment(g4,g7)
    c: InternalAlignment(g5,g7)
    c: InternalAlignment(g6,g7)
    c: InternalAlignment(g8,g7)
    c: InternalAlignment(g9,g7)
    c: Block(g7)
FEATURE [Sketcher::SketchObject] Sketch028
  FullyConstrained = true
  sketch-geometry (18):
    g0: LineSegment StartX=0 StartY=3e-16 StartZ=0 EndX=0 EndY=1.7 EndZ=0
    g1: LineSegment StartX=-3.5 StartY=0 StartZ=0 EndX=-3.5 EndY=0.9 EndZ=0
    g2: Circle CenterX=-2.7 CenterY=1.7 CenterZ=0 NormalX=0 NormalY=0 NormalZ=1 AngleXU=0 Radius=1
    g3: Circle CenterX=-3.5 CenterY=1.7 CenterZ=0 NormalX=0 NormalY=0 NormalZ=1 AngleXU=0 Radius=1
    g4: Circle CenterX=-3.5 CenterY=0.9 CenterZ=0 NormalX=0 NormalY=0 NormalZ=1 AngleXU=0 Radius=1
    g5: BSplineCurve PolesCount=3 KnotsCount=2 Degree=2 IsPeriodic=0
    g6: GeomPoint X=-2.7 Y=1.7 Z=0
    g7: GeomPoint X=-3.5 Y=0.9 Z=0
    g8: LineSegment StartX=-3.5 StartY=0 StartZ=0 EndX=-3.5 EndY=-7 EndZ=0
    g9: LineSegment StartX=0 StartY=3e-16 StartZ=0 EndX=0 EndY=-7 EndZ=0
    g10: LineSegment StartX=-3.5 StartY=-7 StartZ=0 EndX=0 EndY=-7 EndZ=0
    g11: LineSegment StartX=-2.7 StartY=1.7 StartZ=0 EndX=-1.6 EndY=1.7 EndZ=0
    g12: LineSegment StartX=0 StartY=1.7 StartZ=0 EndX=0 EndY=4.5 EndZ=0
    g13: LineSegment StartX=0 StartY=4.5 StartZ=0 EndX=0 EndY=10.8 EndZ=0
    g14: LineSegment StartX=0 StartY=10.8 StartZ=0 EndX=-2 EndY=10.8 EndZ=0
    g15: LineSegment StartX=-1.6 StartY=4.7 StartZ=0 EndX=-1.6 EndY=1.7 EndZ=0
    g16: LineSegment StartX=-1.6 StartY=4.7 StartZ=0 EndX=-2 EndY=4.7 EndZ=0
    g17: LineSegment StartX=-2 StartY=4.7 StartZ=0 EndX=-2 EndY=10.8 EndZ=0
  constraints (44):
    c: Vertical(g0)
    c: Vertical(g1)
    c: Distance(g1) = 0.9
    c: Block(g0)
    c: Distance(g0) = 1.7
    c: Weight(g2) = 1
    c: Equal(g2,g3)
    c: Equal(g2,g4)
    c: Coincident(g5,g1)
    c: InternalAlignment(g2,g5)
    c: InternalAlignment(g3,g5)
    c: InternalAlignment(g4,g5)
    c: InternalAlignment(g6,g5)
    c: InternalAlignment(g7,g5)
    c: Block(g5)
    c: Coincident(g8,g1)
    c: Vertical(g8)
    c: Distance(g8) = 7
    c: Vertical(g9)
    c: Equal(g8,g9) = 7
    c: Coincident(g9,g0)
    c: Coincident(g10,g8)
    c: Coincident(g10,g9)
    c: Horizontal(g10)
    c: Coincident(g11,g5)
    c: Horizontal(g11)
    c: Coincident(g12,g0)
    c: Vertical(g12)
    c: Distance(g12) = 2.8
    c: Coincident(g13,g12)
    c: Vertical(g13)
    c: Distance(g13) = 6.3
    c: Coincident(g14,g13)
    c: Horizontal(g14)
    c: Distance(g14) = 2
    c: Vertical(g15)
    c: Distance(g15) = 3
    c: Block(g11)
    c: Coincident(g15,g11)
    c: Coincident(g16,g15)
    c: Horizontal(g16)
    c: Coincident(g17,g16)
    c: Coincident(g17,g14)
    c: Vertical(g17)
FEATURE [Part::Revolution] Revolve040  label="backCaseScrewRetainer001"
  Angle = 360
  Axis = (0,1,0)
  Base = (0,0,0)
  FaceMakerClass = Part::FaceMakerBullseye
  Placement = pos=(12.5,3,10) rot=(0,0,1;0rad)
  Solid = false
  Source = -> Face036
  Symmetric = false
FEATURE [Part::Feature] Face055
  shape: bbox 3.5 x 30.2 x 2e-07 mm, 1 faces, 0 solids (baked)
FEATURE [Part::Revolution] Revolve059  label="backCaseScrewPost"
  Angle = 360
  Axis = (0,1,0)
  Base = (0,0,0)
  FaceMakerClass = Part::FaceMakerBullseye
  Placement = pos=(12.5,4.5,10) rot=(0,0,1;0rad)
  Solid = false
  Source = -> Face055
  Symmetric = false
FEATURE [Part::Feature] Face056
  shape: bbox 3.5 x 30.2 x 2e-07 mm, 1 faces, 0 solids (baked)
FEATURE [Part::Revolution] Revolve060  label="backCaseScrewPost001"
  Angle = 360
  Axis = (0,1,0)
  Base = (0,0,0)
  FaceMakerClass = Part::FaceMakerBullseye
  Placement = pos=(12.5,4.5,62) rot=(0,0,1;0rad)
  Solid = false
  Source = -> Face056
  Symmetric = false
FEATURE [Part::Feature] Face057
  shape: bbox 3.5 x 17.8 x 2e-07 mm, 1 faces, 0 solids (baked)
FEATURE [Part::Revolution] Revolve061  label="removeToCreateScrewAndThreadedInsertHole"
  Angle = 360
  Axis = (0,1,0)
  Base = (0,0,0)
  FaceMakerClass = Part::FaceMakerBullseye
  Placement = pos=(12.5,0,10) rot=(0,0,1;0rad)
  Solid = false
  Source = -> Face057
  Symmetric = false
FEATURE [Part::Feature] Face058
  shape: bbox 3.5 x 17.8 x 2e-07 mm, 1 faces, 0 solids (baked)
FEATURE [Part::Revolution] Revolve062  label="removeToCreateScrewAndThreadedInsertHole001"
  Angle = 360
  Axis = (0,1,0)
  Base = (0,0,0)
  FaceMakerClass = Part::FaceMakerBullseye
  Placement = pos=(12.5,0,62) rot=(0,0,1;0rad)
  Solid = false
  Source = -> Face058
  Symmetric = false
FEATURE [Part::Feature] Face059
  shape: bbox 3.5 x 17.8 x 2e-07 mm, 1 faces, 0 solids (baked)
FEATURE [Part::Revolution] Revolve063  label="removeToCreateScrewAndThreadedInsertHole002"
  Angle = 360
  Axis = (0,1,0)
  Base = (0,0,0)
  FaceMakerClass = Part::FaceMakerBullseye
  Placement = pos=(89.5,0,68.5) rot=(0,0,1;0rad)
  Solid = false
  Source = -> Face059
  Symmetric = false
FEATURE [Part::Feature] Face060
  shape: bbox 3.5 x 17.8 x 2e-07 mm, 1 faces, 0 solids (baked)
FEATURE [Part::Revolution] Revolve064  label="removeToCreateScrewAndThreadedInsertHole003"
  Angle = 360
  Axis = (0,1,0)
  Base = (0,0,0)
  FaceMakerClass = Part::FaceMakerBullseye
  Placement = pos=(89.5,0,3.5) rot=(0,0,1;0rad)
  Solid = false
  Source = -> Face060
  Symmetric = false
FEATURE [Part::Feature] Face061
  shape: bbox 3.5 x 17.8 x 2e-07 mm, 1 faces, 0 solids (baked)
FEATURE [Part::Revolution] Revolve065  label="removeToCreateScrewAndThreadedInsertHole004"
  Angle = 360
  Axis = (0,1,0)
  Base = (0,0,0)
  FaceMakerClass = Part::FaceMakerBullseye
  Placement = pos=(102.5,4.7,3.5) rot=(0,0,1;0rad)
  Solid = false
  Source = -> Face061
  Symmetric = false
FEATURE [Part::Feature] Face062
  shape: bbox 3.5 x 17.8 x 2e-07 mm, 1 faces, 0 solids (baked)
FEATURE [Part::Revolution] Revolve066  label="removeToCreateScrewAndThreadedInsertHole005"
  Angle = 360
  Axis = (0,1,0)
  Base = (0,0,0)
  FaceMakerClass = Part::FaceMakerBullseye
  Placement = pos=(102.5,4.7,68.5) rot=(0,0,1;0rad)
  Solid = false
  Source = -> Face062
  Symmetric = false
FEATURE [Part::MultiFuse] Fusion047  label="makeHoles"
  Shapes = -> [Revolve066,Revolve065,Revolve064,Revolve063,Revolve062,Revolve061]
FEATURE [Part::Feature] Face063
  shape: bbox 3.6 x 3.2 x 2e-07 mm, 1 faces, 0 solids (baked)
FEATURE [Part::Revolution] Revolve067  label="moreFrontCaseScrewRetainer002"
  Angle = 360
  Axis = (0,1,0)
  Base = (0,0,0)
  FaceMakerClass = Part::FaceMakerBullseye
  Placement = pos=(102.5,4.5,68.5) rot=(0,0,1;0rad)
  Solid = false
  Source = -> Face063
  Symmetric = false
FEATURE [Part::Feature] Face064
  shape: bbox 3.6 x 3.2 x 2e-07 mm, 1 faces, 0 solids (baked)
FEATURE [Part::Revolution] Revolve068  label="moreFrontCaseScrewRetainer003"
  Angle = 360
  Axis = (0,1,0)
  Base = (0,0,0)
  FaceMakerClass = Part::FaceMakerBullseye
  Placement = pos=(102.5,4.5,3.5) rot=(0,0,1;0rad)
  Solid = false
  Source = -> Face064
  Symmetric = false
FEATURE [Part::Feature] Face065
  shape: bbox 3.5 x 17.8 x 2e-07 mm, 1 faces, 0 solids (baked)
FEATURE [Part::Revolution] Revolve069  label="removeToCreateScrewAndThreadedInsertHole006"
  Angle = 360
  Axis = (0,1,0)
  Base = (0,0,0)
  FaceMakerClass = Part::FaceMakerBullseye
  Placement = pos=(12.5,0,10) rot=(0,0,1;0rad)
  Solid = false
  Source = -> Face065
  Symmetric = false
FEATURE [Part::Feature] Face066
  shape: bbox 3.5 x 17.8 x 2e-07 mm, 1 faces, 0 solids (baked)
FEATURE [Part::Revolution] Revolve070  label="removeToCreateScrewAndThreadedInsertHole007"
  Angle = 360
  Axis = (0,1,0)
  Base = (0,0,0)
  FaceMakerClass = Part::FaceMakerBullseye
  Placement = pos=(12.5,0,62) rot=(0,0,1;0rad)
  Solid = false
  Source = -> Face066
  Symmetric = false
FEATURE [Part::Feature] Face067
  shape: bbox 3.5 x 17.8 x 2e-07 mm, 1 faces, 0 solids (baked)
FEATURE [Part::Revolution] Revolve071  label="removeToCreateScrewAndThreadedInsertHole008"
  Angle = 360
  Axis = (0,1,0)
  Base = (0,0,0)
  FaceMakerClass = Part::FaceMakerBullseye
  Placement = pos=(89.5,0,68.5) rot=(0,0,1;0rad)
  Solid = false
  Source = -> Face067
  Symmetric = false
FEATURE [Part::Feature] Face068
  shape: bbox 3.5 x 17.8 x 2e-07 mm, 1 faces, 0 solids (baked)
FEATURE [Part::Revolution] Revolve072  label="removeToCreateScrewAndThreadedInsertHole009"
  Angle = 360
  Axis = (0,1,0)
  Base = (0,0,0)
  FaceMakerClass = Part::FaceMakerBullseye
  Placement = pos=(89.5,0,3.5) rot=(0,0,1;0rad)
  Solid = false
  Source = -> Face068
  Symmetric = false
FEATURE [Part::Feature] Face069
  shape: bbox 3.5 x 17.8 x 2e-07 mm, 1 faces, 0 solids (baked)
FEATURE [Part::Feature] Face070
  shape: bbox 3.5 x 17.8 x 2e-07 mm, 1 faces, 0 solids (baked)
FEATURE [Part::Revolution] Revolve073  label="removeToCreateScrewAndThreadedInsertHole010"
  Angle = 360
  Axis = (0,1,0)
  Base = (0,0,0)
  FaceMakerClass = Part::FaceMakerBullseye
  Placement = pos=(102.5,4.7,3.5) rot=(0,0,1;0rad)
  Solid = false
  Source = -> Face069
  Symmetric = false
FEATURE [Part::Revolution] Revolve074  label="removeToCreateScrewAndThreadedInsertHole011"
  Angle = 360
  Axis = (0,1,0)
  Base = (0,0,0)
  FaceMakerClass = Part::FaceMakerBullseye
  Placement = pos=(102.5,4.7,68.5) rot=(0,0,1;0rad)
  Solid = false
  Source = -> Face070
  Symmetric = false
FEATURE [Part::MultiFuse] Fusion048  label="makeHoles001"
  Shapes = -> [Revolve074,Revolve073,Revolve072,Revolve071,Revolve070,Revolve069]
FEATURE [Part::MultiFuse] Fusion049  label="caseScrewRetainers"
  Shapes = -> [Revolve067,Revolve068,Revolve048,Revolve047,Revolve039,Revolve040]
FEATURE [Part::Cut] Cut015  label="caseScrewRetainers001"
  Base = -> Fusion049
  Tool = -> Fusion048
FEATURE [Part::MultiFuse] Fusion050  label="casePillars"
  Shapes = -> [Revolve055,Revolve054,Revolve043,Revolve046,Revolve059,Revolve060]
FEATURE [Part::Feature] Face071 .. Face076  x6 (patterned run collapsed; names and placements below)
  shape: bbox 3.5 x 17.8 x 2e-07 mm, 1 faces, 0 solids (baked)
FEATURE [Part::Revolution] Revolve075  label="removeToCreateScrewAndThreadedInsertHole012"
  Angle = 360
  Axis = (0,1,0)
  Base = (0,0,0)
  FaceMakerClass = Part::FaceMakerBullseye
  Placement = pos=(12.5,0,10) rot=(0,0,1;0rad)
  Solid = false
  Source = -> Face071
  Symmetric = false
FEATURE [Part::Revolution] Revolve076  label="removeToCreateScrewAndThreadedInsertHole013"
  Angle = 360
  Axis = (0,1,0)
  Base = (0,0,0)
  FaceMakerClass = Part::FaceMakerBullseye
  Placement = pos=(12.5,0,62) rot=(0,0,1;0rad)
  Solid = false
  Source = -> Face072
  Symmetric = false
FEATURE [Part::Revolution] Revolve077  label="removeToCreateScrewAndThreadedInsertHole014"
  Angle = 360
  Axis = (0,1,0)
  Base = (0,0,0)
  FaceMakerClass = Part::FaceMakerBullseye
  Placement = pos=(89.5,0,68.5) rot=(0,0,1;0rad)
  Solid = false
  Source = -> Face073
  Symmetric = false
FEATURE [Part::Revolution] Revolve078  label="removeToCreateScrewAndThreadedInsertHole015"
  Angle = 360
  Axis = (0,1,0)
  Base = (0,0,0)
  FaceMakerClass = Part::FaceMakerBullseye
  Placement = pos=(89.5,0,3.5) rot=(0,0,1;0rad)
  Solid = false
  Source = -> Face074
  Symmetric = false
FEATURE [Part::Revolution] Revolve079  label="removeToCreateScrewAndThreadedInsertHole016"
  Angle = 360
  Axis = (0,1,0)
  Base = (0,0,0)
  FaceMakerClass = Part::FaceMakerBullseye
  Placement = pos=(102.5,4.7,3.5) rot=(0,0,1;0rad)
  Solid = false
  Source = -> Face075
  Symmetric = false
FEATURE [Part::Revolution] Revolve080  label="removeToCreateScrewAndThreadedInsertHole017"
  Angle = 360
  Axis = (0,1,0)
  Base = (0,0,0)
  FaceMakerClass = Part::FaceMakerBullseye
  Placement = pos=(102.5,4.7,68.5) rot=(0,0,1;0rad)
  Solid = false
  Source = -> Face076
  Symmetric = false
FEATURE [Part::MultiFuse] Fusion051  label="makeHoles002"
  Shapes = -> [Revolve080,Revolve079,Revolve078,Revolve077,Revolve076,Revolve075]
FEATURE [Part::Cut] Cut016  label="caesPillars"
  Base = -> Fusion050
  Tool = -> Fusion051
FEATURE [Part::Revolution] Revolve009  label="plugHousing016"
  Angle = 360
  Axis = (0,1,0)
  Base = (0,0,0)
  FaceMakerClass = Part::FaceMakerBullseye
  Placement = pos=(0,0,36.15) rot=(0,0,1;0rad)
  Solid = false
  Source = -> Face012
  Symmetric = false
FEATURE [Part::MultiFuse] Fusion014  label="plugHousing023"
  Placement = pos=(0,0,0) rot=(0,0,1;1.5708rad)
  Shapes = -> [Revolve011,Revolve009]
FEATURE [Part::Revolution] Revolve010  label="plugHousing017"
  Angle = 360
  Axis = (0,1,0)
  Base = (0,0,0)
  FaceMakerClass = Part::FaceMakerBullseye
  Placement = pos=(0,0,36.15) rot=(0,0,1;0rad)
  Solid = false
  Source = -> Face014
  Symmetric = false
FEATURE [Part::MultiFuse] Fusion015  label="plugHousing024"
  Placement = pos=(0,0,0) rot=(0,0,1;1.5708rad)
  Shapes = -> [Revolve010,Revolve015]
FEATURE [Part::Revolution] Revolve014  label="plugHousing026"
  Angle = 360
  Axis = (0,1,0)
  Base = (0,0,0)
  FaceMakerClass = Part::FaceMakerBullseye
  Placement = pos=(0,0,36.15) rot=(0,0,1;0rad)
  Solid = false
  Source = -> Face011
  Symmetric = false
FEATURE [Part::Revolution] Revolve013  label="plugHousing025"
  Angle = 360
  Axis = (0,1,0)
  Base = (0,0,0)
  FaceMakerClass = Part::FaceMakerBullseye
  Placement = pos=(0,0,36.15) rot=(0,0,1;0rad)
  Solid = false
  Source = -> Face015
  Symmetric = false
FEATURE [Part::MultiFuse] Fusion016  label="plugHousing028"
  Placement = pos=(0,19,0) rot=(0,0,1;3.14159rad)
  Shapes = -> [Fusion014,Fusion013]
FEATURE [Part::MultiFuse] Fusion011  label="plugHousing018"
  Placement = pos=(0,0,0) rot=(0,0,1;1.5708rad)
  Shapes = -> [Revolve014,Revolve013]
FEATURE [Part::MultiFuse] Fusion012  label="plugHousing019"
  Placement = pos=(0,19,0) rot=(0,0,1;3.14159rad)
  Shapes = -> [Fusion011,Fusion015]
FEATURE [Part::MultiFuse] Fusion017  label="plugHousing029"
  Placement = pos=(122.621,0,-0.15) rot=(0,0,1;0rad)
  Shapes = -> [Fusion016,Fusion012]
FEATURE [Part::MultiFuse] Fusion052  label="casePillarRetainers"
  Shapes = -> [Extrude012,Extrude013,Extrude014,Extrude015,Extrude016,Extrude017,Extrude018,Extrude019,Box011,Box012]
FEATURE [Part::Feature] Face077
  shape: bbox 3.5 x 17.8 x 2e-07 mm, 1 faces, 0 solids (baked)
FEATURE [Part::Revolution] Revolve081  label="removeToCreateScrewAndThreadedInsertHole018"
  Angle = 360
  Axis = (0,1,0)
  Base = (0,0,0)
  FaceMakerClass = Part::FaceMakerBullseye
  Placement = pos=(62.3,30.3,19.7) rot=(0,0,1;0rad)
  Solid = false
  Source = -> Face077
  Symmetric = false
FEATURE [Part::Feature] Face078
  shape: bbox 3.5 x 17.8 x 2e-07 mm, 1 faces, 0 solids (baked)
FEATURE [Part::Revolution] Revolve082  label="removeToCreateScrewAndThreadedInsertHole019"
  Angle = 360
  Axis = (0,1,0)
  Base = (0,0,0)
  FaceMakerClass = Part::FaceMakerBullseye
  Placement = pos=(62.3,30.3,51.7) rot=(0,0,1;0rad)
  Solid = false
  Source = -> Face078
  Symmetric = false
FEATURE [Part::Feature] Face079
  shape: bbox 3.5 x 17.8 x 2e-07 mm, 1 faces, 0 solids (baked)
FEATURE [Part::Revolution] Revolve083  label="removeToCreateScrewAndThreadedInsertHole020"
  Angle = 360
  Axis = (0,1,0)
  Base = (0,0,0)
  FaceMakerClass = Part::FaceMakerBullseye
  Placement = pos=(30.3,30.3,19.7) rot=(0,0,1;0rad)
  Solid = false
  Source = -> Face079
  Symmetric = false
FEATURE [Part::Feature] Face080
  shape: bbox 3.5 x 17.8 x 2e-07 mm, 1 faces, 0 solids (baked)
FEATURE [Part::Revolution] Revolve084  label="removeToCreateScrewAndThreadedInsertHole021"
  Angle = 360
  Axis = (0,1,0)
  Base = (0,0,0)
  FaceMakerClass = Part::FaceMakerBullseye
  Placement = pos=(30.3,30.3,51.7) rot=(0,0,1;0rad)
  Solid = false
  Source = -> Face080
  Symmetric = false
FEATURE [Part::MultiFuse] Fusion053  label="createThreadedInsertHolesForFan"
  Shapes = -> [Revolve081,Revolve082,Revolve083,Revolve084]
FEATURE [Part::Cut] Cut017  label="fanScrewHousing001"
  Base = -> Fusion046
  Tool = -> Fusion053
FEATURE [Part::Feature] Face081
  shape: bbox 3.5 x 17.8 x 2e-07 mm, 1 faces, 0 solids (baked)
FEATURE [Part::Revolution] Revolve085  label="removeToCreateScrewAndThreadedInsertHole022"
  Angle = 360
  Axis = (0,1,0)
  Base = (0,0,0)
  FaceMakerClass = Part::FaceMakerBullseye
  Placement = pos=(62.3,30.3,19.7) rot=(0,0,1;0rad)
  Solid = false
  Source = -> Face081
  Symmetric = false
FEATURE [Part::Feature] Face082
  shape: bbox 3.5 x 17.8 x 2e-07 mm, 1 faces, 0 solids (baked)
FEATURE [Part::Revolution] Revolve086  label="removeToCreateScrewAndThreadedInsertHole023"
  Angle = 360
  Axis = (0,1,0)
  Base = (0,0,0)
  FaceMakerClass = Part::FaceMakerBullseye
  Placement = pos=(62.3,30.3,51.7) rot=(0,0,1;0rad)
  Solid = false
  Source = -> Face082
  Symmetric = false
FEATURE [Part::Feature] Face083
  shape: bbox 3.5 x 17.8 x 2e-07 mm, 1 faces, 0 solids (baked)
FEATURE [Part::Revolution] Revolve087  label="removeToCreateScrewAndThreadedInsertHole024"
  Angle = 360
  Axis = (0,1,0)
  Base = (0,0,0)
  FaceMakerClass = Part::FaceMakerBullseye
  Placement = pos=(30.3,30.3,19.7) rot=(0,0,1;0rad)
  Solid = false
  Source = -> Face083
  Symmetric = false
FEATURE [Part::Feature] Face084
  shape: bbox 3.5 x 17.8 x 2e-07 mm, 1 faces, 0 solids (baked)
FEATURE [Part::Revolution] Revolve088  label="removeToCreateScrewAndThreadedInsertHole025"
  Angle = 360
  Axis = (0,1,0)
  Base = (0,0,0)
  FaceMakerClass = Part::FaceMakerBullseye
  Placement = pos=(30.3,30.3,51.7) rot=(0,0,1;0rad)
  Solid = false
  Source = -> Face084
  Symmetric = false
FEATURE [Part::MultiFuse] Fusion054  label="createThreadedInsertHolesForFan001"
  Shapes = -> [Revolve085,Revolve086,Revolve087,Revolve088]
FEATURE [Part::Cut] Cut018  label="top007"
  Base = -> Fusion040
  Tool = -> Fusion054
FEATURE [Sketcher::SketchObject] Sketch029
  FullyConstrained = false
  Placement = pos=(0,0,0) rot=(1,0,0;1.5708rad)
  sketch-geometry (24):
    g0: ArcOfCircle CenterX=-4 CenterY=-10.5 CenterZ=0 NormalX=0 NormalY=0 NormalZ=1 AngleXU=0 Radius=1.5 StartAngle=6e-16 EndAngle=3.14159
    g1: ArcOfCircle CenterX=-34.2 CenterY=-10.5 CenterZ=0 NormalX=0 NormalY=0 NormalZ=1 AngleXU=0 Radius=1.5 StartAngle=0 EndAngle=3.14159
    g2: ArcOfCircle CenterX=-34.2 CenterY=-27.7 CenterZ=0 NormalX=0 NormalY=0 NormalZ=1 AngleXU=0 Radius=1.5 StartAngle=3.14159 EndAngle=6.28319
    g3: ArcOfCircle CenterX=-4 CenterY=-27.7 CenterZ=0 NormalX=0 NormalY=0 NormalZ=1 AngleXU=0 Radius=1.5 StartAngle=3.1416 EndAngle=6.28319
    g4: ArcOfCircle CenterX=-10 CenterY=-4.3 CenterZ=0 NormalX=0 NormalY=0 NormalZ=1 AngleXU=0 Radius=1.5 StartAngle=2e-16 EndAngle=3.14159
    g5: ArcOfCircle CenterX=-16.1 CenterY=-1.8 CenterZ=0 NormalX=0 NormalY=0 NormalZ=1 AngleXU=0 Radius=1.5 StartAngle=5e-16 EndAngle=3.14159
    g6: ArcOfCircle CenterX=-22.1 CenterY=-1.8 CenterZ=0 NormalX=0 NormalY=0 NormalZ=1 AngleXU=0 Radius=1.5 StartAngle=5e-16 EndAngle=3.14159
    g7: ArcOfCircle CenterX=-28.2 CenterY=-4.3 CenterZ=0 NormalX=0 NormalY=0 NormalZ=1 AngleXU=0 Radius=1.5 StartAngle=2e-16 EndAngle=3.14159
    g8: ArcOfCircle CenterX=-10 CenterY=-33.9 CenterZ=0 NormalX=0 NormalY=0 NormalZ=1 AngleXU=0 Radius=1.5 StartAngle=3.14159 EndAngle=6.28319
    g9: ArcOfCircle CenterX=-16.1 CenterY=-36.4 CenterZ=0 NormalX=0 NormalY=0 NormalZ=1 AngleXU=0 Radius=1.5 StartAngle=3.14159 EndAngle=6.28319
    g10: ArcOfCircle CenterX=-22.1 CenterY=-36.4 CenterZ=0 NormalX=0 NormalY=0 NormalZ=1 AngleXU=0 Radius=1.5 StartAngle=3.14159 EndAngle=6.28319
    g11: ArcOfCircle CenterX=-28.2 CenterY=-33.9 CenterZ=0 NormalX=0 NormalY=0 NormalZ=1 AngleXU=0 Radius=1.5 StartAngle=3.14159 EndAngle=6.28319
    g12: LineSegment StartX=-35.7 StartY=-10.5 StartZ=0 EndX=-35.7 EndY=-27.7 EndZ=0
    g13: LineSegment StartX=-32.7 StartY=-10.5 StartZ=0 EndX=-32.7 EndY=-27.7 EndZ=0
    g14: LineSegment StartX=-29.7 StartY=-33.9 StartZ=0 EndX=-29.7 EndY=-4.3 EndZ=0
    g15: LineSegment StartX=-26.7 StartY=-33.9 StartZ=0 EndX=-26.7 EndY=-4.3 EndZ=0
    g16: LineSegment StartX=-2.5 StartY=-10.5 StartZ=0 EndX=-2.5 EndY=-27.7 EndZ=0
    g17: LineSegment StartX=-8.5 StartY=-4.3 StartZ=0 EndX=-8.5 EndY=-33.9 EndZ=0
    g18: LineSegment StartX=-5.5 StartY=-10.5 StartZ=0 EndX=-5.5 EndY=-27.7 EndZ=0
    g19: LineSegment StartX=-11.5 StartY=-4.3 StartZ=0 EndX=-11.5 EndY=-33.9 EndZ=0
    g20: LineSegment StartX=-14.6 StartY=-1.8 StartZ=0 EndX=-14.6 EndY=-36.4 EndZ=0
    g21: LineSegment StartX=-17.6 StartY=-1.8 StartZ=0 EndX=-17.6 EndY=-36.4 EndZ=0
    g22: LineSegment StartX=-20.6 StartY=-36.4 StartZ=0 EndX=-20.6 EndY=-1.8 EndZ=0
    g23: LineSegment StartX=-23.6 StartY=-1.8 StartZ=0 EndX=-23.6 EndY=-36.4 EndZ=0
  constraints (48):
    c: Block(g0)
    c: Block(g1)
    c: Block(g2)
    c: Block(g3)
    c: Block(g4)
    c: Block(g5)
    c: Block(g6)
    c: Block(g7)
    c: Block(g8)
    c: Block(g9)
    c: Block(g10)
    c: Block(g11)
    c: Coincident(g12,g1)
    c: Coincident(g12,g2)
    c: Vertical(g12)
    c: Coincident(g13,g1)
    c: Coincident(g13,g2)
    c: Vertical(g13)
    c: Coincident(g14,g11)
    c: Coincident(g14,g7)
    c: Vertical(g14)
    c: Coincident(g15,g11)
    c: Coincident(g15,g7)
    c: Vertical(g15)
    c: Coincident(g16,g0)
    c: Coincident(g16,g3)
    c: Vertical(g16)
    c: Coincident(g17,g4)
    c: Coincident(g17,g8)
    c: Vertical(g17)
    c: Coincident(g18,g0)
    c: Coincident(g18,g3)
    c: Vertical(g18)
    c: Coincident(g19,g4)
    c: Coincident(g19,g8)
    c: Vertical(g19)
    c: Coincident(g20,g5)
    c: Coincident(g20,g9)
    c: Vertical(g20)
    c: Coincident(g21,g5)
    c: Coincident(g21,g9)
    c: Vertical(g21)
    c: Coincident(g22,g10)
    c: Coincident(g22,g6)
    c: Vertical(g22)
    c: Coincident(g23,g6)
    c: Coincident(g23,g10)
    c: Vertical(g23)
FEATURE [Part::Extrusion] Extrude020  label="removeToCreateFanGrillHoles"
  Base = -> Sketch029
  Dir = (0,-1,6e-16)
  DirMode = 2
  FaceMakerClass = Part::FaceMakerBullseye
  LengthFwd = 10
  LengthRev = 0
  Placement = pos=(65.4,44,54.82) rot=(0,0,1;0rad)
  Solid = true
  Symmetric = false
FEATURE [Part::MultiFuse] Fusion055  label="top008"
  Shapes = -> [Cut017,Cut018]
FEATURE [Part::Cut] Cut019  label="top009"
  Base = -> Fusion055
  Tool = -> Extrude020
FEATURE [App::MeasureDistance] Distance003  label="Distance: 71.95 mm"
  Distance = 71.9513
  P1 = (117,38,72)
  P2 = (117,38,0.0487319)
FEATURE [Sketcher::SketchObject] Sketch030
  FullyConstrained = true
  Placement = pos=(117,19,0) rot=(0.57735,0.57735,0.57735;2.0944rad)
  sketch-geometry (48):
    g0: LineSegment StartX=-49.19 StartY=69.25 StartZ=0 EndX=-49.19 EndY=66.25 EndZ=0
    g1: LineSegment StartX=-49.19 StartY=63.5 StartZ=0 EndX=-49.19 EndY=60.5 EndZ=0
    g2: LineSegment StartX=-49.19 StartY=57.75 StartZ=0 EndX=-49.19 EndY=54.75 EndZ=0
    g3: LineSegment StartX=-49.19 StartY=52 StartZ=0 EndX=-49.19 EndY=49 EndZ=0
    g4: LineSegment StartX=-49.19 StartY=46.25 StartZ=0 EndX=-49.19 EndY=43.25 EndZ=0
    g5: LineSegment StartX=-49.19 StartY=40.5 StartZ=0 EndX=-49.19 EndY=37.5 EndZ=0
    g6: LineSegment StartX=-49.19 StartY=34.5 StartZ=0 EndX=-49.19 EndY=31.5 EndZ=0
    g7: LineSegment StartX=-49.19 StartY=28.75 StartZ=0 EndX=-49.19 EndY=25.75 EndZ=0
    g8: LineSegment StartX=-49.19 StartY=23 StartZ=0 EndX=-49.19 EndY=20 EndZ=0
    g9: LineSegment StartX=-49.19 StartY=17.25 StartZ=0 EndX=-49.19 EndY=14.25 EndZ=0
    g10: LineSegment StartX=-49.19 StartY=11.5 StartZ=0 EndX=-49.19 EndY=8.5 EndZ=0
    g11: LineSegment StartX=-49.19 StartY=5.75 StartZ=0 EndX=-49.19 EndY=2.75 EndZ=0
    g12: ArcOfCircle CenterX=-1.5 CenterY=67.75 CenterZ=0 NormalX=0 NormalY=0 NormalZ=1 AngleXU=0 Radius=1.5 StartAngle=4.71239 EndAngle=7.85398
    g13: ArcOfCircle CenterX=-1.5 CenterY=62 CenterZ=0 NormalX=0 NormalY=0 NormalZ=1 AngleXU=0 Radius=1.5 StartAngle=4.71239 EndAngle=7.85398
    g14: ArcOfCircle CenterX=-1.5 CenterY=56.25 CenterZ=0 NormalX=0 NormalY=0 NormalZ=1 AngleXU=0 Radius=1.5 StartAngle=4.71239 EndAngle=7.85398
    g15: ArcOfCircle CenterX=-11.49 CenterY=50.5 CenterZ=0 NormalX=0 NormalY=0 NormalZ=1 AngleXU=0 Radius=1.5 StartAngle=4.71239 EndAngle=7.85398
    g16: ArcOfCircle CenterX=-16.28 CenterY=44.75 CenterZ=0 NormalX=0 NormalY=0 NormalZ=1 AngleXU=0 Radius=1.5 StartAngle=4.71239 EndAngle=7.85398
    g17: ArcOfCircle CenterX=-18.2337 CenterY=39 CenterZ=0 NormalX=0 NormalY=0 NormalZ=1 AngleXU=0 Radius=1.5 StartAngle=4.71485 EndAngle=7.85398
    g18: ArcOfCircle CenterX=-16.2837 CenterY=27.25 CenterZ=0 NormalX=0 NormalY=0 NormalZ=1 AngleXU=0 Radius=1.5 StartAngle=4.71485 EndAngle=7.85398
    g19: ArcOfCircle CenterX=-18.2337 CenterY=33 CenterZ=0 NormalX=0 NormalY=0 NormalZ=1 AngleXU=0 Radius=1.5 StartAngle=4.71485 EndAngle=7.85398
    g20: ArcOfCircle CenterX=-11.49 CenterY=21.5 CenterZ=0 NormalX=0 NormalY=0 NormalZ=1 AngleXU=0 Radius=1.5 StartAngle=4.71239 EndAngle=7.85398
    g21: ArcOfCircle CenterX=-1.5 CenterY=4.25 CenterZ=0 NormalX=0 NormalY=0 NormalZ=1 AngleXU=0 Radius=1.5 StartAngle=4.71239 EndAngle=7.85398
    g22: ArcOfCircle CenterX=-1.5 CenterY=10 CenterZ=0 NormalX=0 NormalY=0 NormalZ=1 AngleXU=0 Radius=1.5 StartAngle=4.71239 EndAngle=7.85398
    g23: ArcOfCircle CenterX=-1.5 CenterY=15.75 CenterZ=0 NormalX=0 NormalY=0 NormalZ=1 AngleXU=0 Radius=1.5 StartAngle=4.71239 EndAngle=7.85398
    g24: LineSegment StartX=-49.19 StartY=69.25 StartZ=0 EndX=-1.5 EndY=69.25 EndZ=0
    g25: LineSegment StartX=-49.19 StartY=66.25 StartZ=0 EndX=-1.5 EndY=66.25 EndZ=0
    g26: LineSegment StartX=-49.19 StartY=63.5 StartZ=0 EndX=-1.5 EndY=63.5 EndZ=0
    g27: LineSegment StartX=-49.19 StartY=60.5 StartZ=0 EndX=-1.5 EndY=60.5 EndZ=0
    g28: LineSegment StartX=-49.19 StartY=57.75 StartZ=0 EndX=-1.5 EndY=57.75 EndZ=0
    g29: LineSegment StartX=-49.19 StartY=54.75 StartZ=0 EndX=-1.5 EndY=54.75 EndZ=0
    g30: LineSegment StartX=-49.19 StartY=52 StartZ=0 EndX=-11.49 EndY=52 EndZ=0
    g31: LineSegment StartX=-49.19 StartY=49 StartZ=0 EndX=-11.49 EndY=49 EndZ=0
    g32: LineSegment StartX=-49.19 StartY=46.25 StartZ=0 EndX=-16.28 EndY=46.25 EndZ=0
    g33: LineSegment StartX=-49.19 StartY=43.25 StartZ=0 EndX=-16.28 EndY=43.25 EndZ=0
    g34: LineSegment StartX=-49.19 StartY=40.5 StartZ=0 EndX=-18.2337 EndY=40.5 EndZ=0
    g35: LineSegment StartX=-49.19 StartY=37.5 StartZ=0 EndX=-18.23 EndY=37.5 EndZ=0
    g36: LineSegment StartX=-49.19 StartY=34.5 StartZ=0 EndX=-18.2337 EndY=34.5 EndZ=0
    g37: LineSegment StartX=-49.19 StartY=31.5 StartZ=0 EndX=-18.23 EndY=31.5 EndZ=0
    g38: LineSegment StartX=-49.19 StartY=28.75 StartZ=0 EndX=-16.2837 EndY=28.75 EndZ=0
    g39: LineSegment StartX=-49.19 StartY=25.75 StartZ=0 EndX=-16.28 EndY=25.75 EndZ=0
    g40: LineSegment StartX=-49.19 StartY=23 StartZ=0 EndX=-11.49 EndY=23 EndZ=0
    g41: LineSegment StartX=-49.19 StartY=20 StartZ=0 EndX=-11.49 EndY=20 EndZ=0
    g42: LineSegment StartX=-49.19 StartY=17.25 StartZ=0 EndX=-1.5 EndY=17.25 EndZ=0
    g43: LineSegment StartX=-49.19 StartY=14.25 StartZ=0 EndX=-1.5 EndY=14.25 EndZ=0
    g44: LineSegment StartX=-49.19 StartY=11.5 StartZ=0 EndX=-1.5 EndY=11.5 EndZ=0
    g45: LineSegment StartX=-49.19 StartY=8.5 StartZ=0 EndX=-1.5 EndY=8.5 EndZ=0
    g46: LineSegment StartX=-49.19 StartY=5.75 StartZ=0 EndX=-1.5 EndY=5.75 EndZ=0
    g47: LineSegment StartX=-49.19 StartY=2.75 StartZ=0 EndX=-1.5 EndY=2.75 EndZ=0
  constraints (120):
    c: Vertical(g0)
    c: Distance(g0) = 3
    c: Block(g0)
    c: Vertical(g1)
    c: Distance(g1) = 3
    c: Vertical(g2)
    c: Equal(g0,g2) = 3
    c: Block(g2)
    c: Vertical(g3)
    c: Equal(g1,g3) = 3
    c: Vertical(g4)
    c: Equal(g0,g4) = 3
    c: Block(g4)
    c: Vertical(g5)
    c: Equal(g1,g5) = 3
    c: Vertical(g6)
    c: Equal(g0,g6) = 3
    c: Block(g6)
    c: Vertical(g7)
    c: Equal(g1,g7) = 3
    c: Vertical(g8)
    c: Equal(g0,g8) = 3
    c: Block(g8)
    c: Vertical(g9)
    c: Equal(g1,g9) = 3
    c: Vertical(g10)
    c: Equal(g0,g10) = 3
    c: Block(g10)
    c: Vertical(g11)
    c: Equal(g1,g11) = 3
    c: Block(g12)
    c: Block(g13)
    c: Block(g14)
    c: Block(g15)
    c: Block(g16)
    c: Block(g17)
    c: Block(g18)
    c: Block(g19)
    c: Block(g20)
    c: Block(g21)
    c: Block(g22)
    c: Block(g23)
    c: Block(g11)
    c: Block(g9)
    c: Block(g7)
    c: Block(g5)
    c: Block(g3)
    c: Block(g1)
    c: Coincident(g24,g0)
    c: Coincident(g24,g12)
    c: Horizontal(g24)
    c: Coincident(g25,g0)
    c: Coincident(g25,g12)
    c: Horizontal(g25)
    c: Coincident(g26,g1)
    c: Coincident(g26,g13)
    c: Horizontal(g26)
    c: Coincident(g27,g1)
    c: Coincident(g27,g13)
    c: Horizontal(g27)
    c: Coincident(g28,g2)
    c: Coincident(g28,g14)
    c: Horizontal(g28)
    c: Coincident(g29,g2)
    c: Coincident(g29,g14)
    c: Horizontal(g29)
    c: Coincident(g30,g3)
    c: Coincident(g30,g15)
    c: Horizontal(g30)
    c: Coincident(g31,g3)
    c: Coincident(g31,g15)
    c: Horizontal(g31)
    c: Coincident(g32,g4)
    c: Coincident(g32,g16)
    c: Horizontal(g32)
    c: Coincident(g33,g4)
    c: Coincident(g33,g16)
    c: Horizontal(g33)
    c: Coincident(g34,g5)
    c: Coincident(g34,g17)
    c: Horizontal(g34)
    c: Coincident(g35,g5)
    c: Coincident(g35,g17)
    c: Horizontal(g35)
    c: Coincident(g36,g6)
    c: Coincident(g36,g19)
    c: Horizontal(g36)
    c: Coincident(g37,g6)
    c: Coincident(g37,g19)
    c: Horizontal(g37)
    c: Coincident(g38,g7)
    c: Coincident(g38,g18)
    c: Horizontal(g38)
    c: Coincident(g39,g7)
    c: Coincident(g39,g18)
    c: Horizontal(g39)
    c: Coincident(g40,g8)
    c: Coincident(g40,g20)
    c: Horizontal(g40)
    c: Coincident(g41,g8)
    c: Coincident(g41,g20)
    c: Horizontal(g41)
    c: Coincident(g42,g9)
    c: Coincident(g42,g23)
    c: Horizontal(g42)
    c: Coincident(g43,g9)
    c: Coincident(g43,g23)
    c: Horizontal(g43)
    c: Coincident(g44,g10)
    c: Coincident(g44,g22)
    c: Horizontal(g44)
    c: Coincident(g45,g10)
    c: Coincident(g45,g22)
    c: Horizontal(g45)
    c: Coincident(g46,g11)
    c: Coincident(g46,g21)
    c: Horizontal(g46)
    c: Coincident(g47,g11)
    c: Coincident(g47,g21)
    c: Horizontal(g47)
FEATURE [Sketcher::SketchObject] Sketch031
  FullyConstrained = true
  Placement = pos=(117,19,0) rot=(0.57735,0.57735,0.57735;2.0944rad)
  sketch-geometry (24):
    g0: ArcOfCircle CenterX=-49.19 CenterY=67.75 CenterZ=0 NormalX=0 NormalY=0 NormalZ=1 AngleXU=0 Radius=1.5 StartAngle=1.5708 EndAngle=4.71239
    g1: ArcOfCircle CenterX=-49.19 CenterY=62 CenterZ=0 NormalX=0 NormalY=0 NormalZ=1 AngleXU=0 Radius=1.5 StartAngle=1.5708 EndAngle=4.71239
    g2: ArcOfCircle CenterX=-49.19 CenterY=56.25 CenterZ=0 NormalX=0 NormalY=0 NormalZ=1 AngleXU=0 Radius=1.5 StartAngle=1.5708 EndAngle=4.71239
    g3: ArcOfCircle CenterX=-49.19 CenterY=50.5 CenterZ=0 NormalX=0 NormalY=0 NormalZ=1 AngleXU=0 Radius=1.5 StartAngle=1.5708 EndAngle=4.71239
    g4: ArcOfCircle CenterX=-49.19 CenterY=44.75 CenterZ=0 NormalX=0 NormalY=0 NormalZ=1 AngleXU=0 Radius=1.5 StartAngle=1.5708 EndAngle=4.71239
    g5: ArcOfCircle CenterX=-49.19 CenterY=39 CenterZ=0 NormalX=0 NormalY=0 NormalZ=1 AngleXU=0 Radius=1.5 StartAngle=1.5708 EndAngle=4.71239
    g6: ArcOfCircle CenterX=-49.19 CenterY=33 CenterZ=0 NormalX=0 NormalY=0 NormalZ=1 AngleXU=0 Radius=1.5 StartAngle=1.5708 EndAngle=4.71239
    g7: ArcOfCircle CenterX=-49.19 CenterY=27.25 CenterZ=0 NormalX=0 NormalY=0 NormalZ=1 AngleXU=0 Radius=1.5 StartAngle=1.5708 EndAngle=4.71239
    g8: ArcOfCircle CenterX=-49.19 CenterY=21.5 CenterZ=0 NormalX=0 NormalY=0 NormalZ=1 AngleXU=0 Radius=1.5 StartAngle=1.5708 EndAngle=4.71239
    g9: ArcOfCircle CenterX=-49.19 CenterY=15.75 CenterZ=0 NormalX=0 NormalY=0 NormalZ=1 AngleXU=0 Radius=1.5 StartAngle=1.5708 EndAngle=4.71239
    g10: ArcOfCircle CenterX=-49.19 CenterY=10 CenterZ=0 NormalX=0 NormalY=0 NormalZ=1 AngleXU=0 Radius=1.5 StartAngle=1.5708 EndAngle=4.71239
    g11: ArcOfCircle CenterX=-49.19 CenterY=4.25 CenterZ=0 NormalX=0 NormalY=0 NormalZ=1 AngleXU=0 Radius=1.5 StartAngle=1.5708 EndAngle=4.71239
    g12: LineSegment StartX=-49.19 StartY=69.25 StartZ=0 EndX=-49.19 EndY=66.25 EndZ=0
    g13: LineSegment StartX=-49.19 StartY=63.5 StartZ=0 EndX=-49.19 EndY=60.5 EndZ=0
    g14: LineSegment StartX=-49.19 StartY=57.75 StartZ=0 EndX=-49.19 EndY=54.75 EndZ=0
    g15: LineSegment StartX=-49.19 StartY=52 StartZ=0 EndX=-49.19 EndY=49 EndZ=0
    g16: LineSegment StartX=-49.19 StartY=46.25 StartZ=0 EndX=-49.19 EndY=43.25 EndZ=0
    g17: LineSegment StartX=-49.19 StartY=40.5 StartZ=0 EndX=-49.19 EndY=37.5 EndZ=0
    g18: LineSegment StartX=-49.19 StartY=34.5 StartZ=0 EndX=-49.19 EndY=31.5 EndZ=0
    g19: LineSegment StartX=-49.19 StartY=28.75 StartZ=0 EndX=-49.19 EndY=25.75 EndZ=0
    g20: LineSegment StartX=-49.19 StartY=23 StartZ=0 EndX=-49.19 EndY=20 EndZ=0
    g21: LineSegment StartX=-49.19 StartY=17.25 StartZ=0 EndX=-49.19 EndY=14.25 EndZ=0
    g22: LineSegment StartX=-49.19 StartY=11.5 StartZ=0 EndX=-49.19 EndY=8.5 EndZ=0
    g23: LineSegment StartX=-49.19 StartY=5.75 StartZ=0 EndX=-49.19 EndY=2.75 EndZ=0
  constraints (48):
    c: Block(g0)
    c: Block(g1)
    c: Block(g2)
    c: Block(g3)
    c: Block(g4)
    c: Block(g5)
    c: Block(g6)
    c: Block(g7)
    c: Block(g8)
    c: Block(g9)
    c: Block(g10)
    c: Block(g11)
    c: Coincident(g12,g0)
    c: Coincident(g12,g0)
    c: Vertical(g12)
    c: Vertical(g13)
    c: Coincident(g13,g1)
    c: Vertical(g14)
    c: Coincident(g14,g2)
    c: Vertical(g15)
    c: Coincident(g15,g3)
    c: Vertical(g16)
    c: Coincident(g16,g4)
    c: Vertical(g17)
    c: Coincident(g17,g5)
    c: Vertical(g18)
    c: Coincident(g18,g6)
    c: Vertical(g19)
    c: Coincident(g19,g7)
    c: Vertical(g20)
    c: Coincident(g20,g8)
    c: Vertical(g21)
    c: Coincident(g21,g9)
    c: Vertical(g22)
    c: Coincident(g22,g10)
    c: Vertical(g23)
    c: Coincident(g23,g11)
    c: Block(g23)
    c: Block(g22)
    c: Block(g21)
    c: Block(g20)
    c: Block(g13)
    c: Block(g14)
    c: Block(g15)
    c: Block(g16)
    c: Block(g17)
    c: Block(g18)
    c: Block(g19)
FEATURE [Part::Extrusion] Extrude022
  Base = -> Sketch030
  Dir = (1,-2e-16,2e-16)
  DirMode = 2
  FaceMakerClass = Part::FaceMakerBullseye
  LengthFwd = 19
  LengthRev = 0
  Placement = pos=(-19,0,0) rot=(0,0,1;0rad)
  Solid = true
  Symmetric = false
FEATURE [Part::Fillet] Fillet022
  Base = -> Extrude022
  Edges = 24 edges r=1.49: [Edge6,Edge11,Edge18,Edge23,Edge30,Edge35,Edge42,Edge47,Edge54,Edge59,Edge66,Edge71,Edge78,Edge83,Edge90,Edge95,Edge102,Edge107,Edge114,Edge119,Edge126,Edge131,Edge138,Edge143]
FEATURE [Part::Cut] Cut020  label="top010"
  Base = -> Cut019
  Tool = -> Fillet022
FEATURE [Sketcher::SketchObject] Sketch032
  FullyConstrained = true
  Placement = pos=(117,19,0) rot=(0.57735,0.57735,0.57735;2.0944rad)
  sketch-geometry (48):
    g0: LineSegment StartX=-49.19 StartY=69.25 StartZ=0 EndX=-49.19 EndY=66.25 EndZ=0
    g1: LineSegment StartX=-49.19 StartY=63.5 StartZ=0 EndX=-49.19 EndY=60.5 EndZ=0
    g2: LineSegment StartX=-49.19 StartY=57.75 StartZ=0 EndX=-49.19 EndY=54.75 EndZ=0
    g3: LineSegment StartX=-49.19 StartY=52 StartZ=0 EndX=-49.19 EndY=49 EndZ=0
    g4: LineSegment StartX=-49.19 StartY=46.25 StartZ=0 EndX=-49.19 EndY=43.25 EndZ=0
    g5: LineSegment StartX=-49.19 StartY=40.5 StartZ=0 EndX=-49.19 EndY=37.5 EndZ=0
    g6: LineSegment StartX=-49.19 StartY=34.5 StartZ=0 EndX=-49.19 EndY=31.5 EndZ=0
    g7: LineSegment StartX=-49.19 StartY=28.75 StartZ=0 EndX=-49.19 EndY=25.75 EndZ=0
    g8: LineSegment StartX=-49.19 StartY=23 StartZ=0 EndX=-49.19 EndY=20 EndZ=0
    g9: LineSegment StartX=-49.19 StartY=17.25 StartZ=0 EndX=-49.19 EndY=14.25 EndZ=0
    g10: LineSegment StartX=-49.19 StartY=11.5 StartZ=0 EndX=-49.19 EndY=8.5 EndZ=0
    g11: LineSegment StartX=-49.19 StartY=5.75 StartZ=0 EndX=-49.19 EndY=2.75 EndZ=0
    g12: ArcOfCircle CenterX=-1.5 CenterY=67.75 CenterZ=0 NormalX=0 NormalY=0 NormalZ=1 AngleXU=0 Radius=1.5 StartAngle=4.71239 EndAngle=7.85398
    g13: ArcOfCircle CenterX=-1.5 CenterY=62 CenterZ=0 NormalX=0 NormalY=0 NormalZ=1 AngleXU=0 Radius=1.5 StartAngle=4.71239 EndAngle=7.85398
    g14: ArcOfCircle CenterX=-1.5 CenterY=56.25 CenterZ=0 NormalX=0 NormalY=0 NormalZ=1 AngleXU=0 Radius=1.5 StartAngle=4.71239 EndAngle=7.85398
    g15: ArcOfCircle CenterX=-11.49 CenterY=50.5 CenterZ=0 NormalX=0 NormalY=0 NormalZ=1 AngleXU=0 Radius=1.5 StartAngle=4.71239 EndAngle=7.85398
    g16: ArcOfCircle CenterX=-16.28 CenterY=44.75 CenterZ=0 NormalX=0 NormalY=0 NormalZ=1 AngleXU=0 Radius=1.5 StartAngle=4.71239 EndAngle=7.85398
    g17: ArcOfCircle CenterX=-18.2337 CenterY=39 CenterZ=0 NormalX=0 NormalY=0 NormalZ=1 AngleXU=0 Radius=1.5 StartAngle=4.71485 EndAngle=7.85398
    g18: ArcOfCircle CenterX=-16.2837 CenterY=27.25 CenterZ=0 NormalX=0 NormalY=0 NormalZ=1 AngleXU=0 Radius=1.5 StartAngle=4.71485 EndAngle=7.85398
    g19: ArcOfCircle CenterX=-18.2337 CenterY=33 CenterZ=0 NormalX=0 NormalY=0 NormalZ=1 AngleXU=0 Radius=1.5 StartAngle=4.71485 EndAngle=7.85398
    g20: ArcOfCircle CenterX=-11.49 CenterY=21.5 CenterZ=0 NormalX=0 NormalY=0 NormalZ=1 AngleXU=0 Radius=1.5 StartAngle=4.71239 EndAngle=7.85398
    g21: ArcOfCircle CenterX=-1.5 CenterY=4.25 CenterZ=0 NormalX=0 NormalY=0 NormalZ=1 AngleXU=0 Radius=1.5 StartAngle=4.71239 EndAngle=7.85398
    g22: ArcOfCircle CenterX=-1.5 CenterY=10 CenterZ=0 NormalX=0 NormalY=0 NormalZ=1 AngleXU=0 Radius=1.5 StartAngle=4.71239 EndAngle=7.85398
    g23: ArcOfCircle CenterX=-1.5 CenterY=15.75 CenterZ=0 NormalX=0 NormalY=0 NormalZ=1 AngleXU=0 Radius=1.5 StartAngle=4.71239 EndAngle=7.85398
    g24: LineSegment StartX=-49.19 StartY=69.25 StartZ=0 EndX=-1.5 EndY=69.25 EndZ=0
    g25: LineSegment StartX=-49.19 StartY=66.25 StartZ=0 EndX=-1.5 EndY=66.25 EndZ=0
    g26: LineSegment StartX=-49.19 StartY=63.5 StartZ=0 EndX=-1.5 EndY=63.5 EndZ=0
    g27: LineSegment StartX=-49.19 StartY=60.5 StartZ=0 EndX=-1.5 EndY=60.5 EndZ=0
    g28: LineSegment StartX=-49.19 StartY=57.75 StartZ=0 EndX=-1.5 EndY=57.75 EndZ=0
    g29: LineSegment StartX=-49.19 StartY=54.75 StartZ=0 EndX=-1.5 EndY=54.75 EndZ=0
    g30: LineSegment StartX=-49.19 StartY=52 StartZ=0 EndX=-11.49 EndY=52 EndZ=0
    g31: LineSegment StartX=-49.19 StartY=49 StartZ=0 EndX=-11.49 EndY=49 EndZ=0
    g32: LineSegment StartX=-49.19 StartY=46.25 StartZ=0 EndX=-16.28 EndY=46.25 EndZ=0
    g33: LineSegment StartX=-49.19 StartY=43.25 StartZ=0 EndX=-16.28 EndY=43.25 EndZ=0
    g34: LineSegment StartX=-49.19 StartY=40.5 StartZ=0 EndX=-18.2337 EndY=40.5 EndZ=0
    g35: LineSegment StartX=-49.19 StartY=37.5 StartZ=0 EndX=-18.23 EndY=37.5 EndZ=0
    g36: LineSegment StartX=-49.19 StartY=34.5 StartZ=0 EndX=-18.2337 EndY=34.5 EndZ=0
    g37: LineSegment StartX=-49.19 StartY=31.5 StartZ=0 EndX=-18.23 EndY=31.5 EndZ=0
    g38: LineSegment StartX=-49.19 StartY=28.75 StartZ=0 EndX=-16.2837 EndY=28.75 EndZ=0
    g39: LineSegment StartX=-49.19 StartY=25.75 StartZ=0 EndX=-16.28 EndY=25.75 EndZ=0
    g40: LineSegment StartX=-49.19 StartY=23 StartZ=0 EndX=-11.49 EndY=23 EndZ=0
    g41: LineSegment StartX=-49.19 StartY=20 StartZ=0 EndX=-11.49 EndY=20 EndZ=0
    g42: LineSegment StartX=-49.19 StartY=17.25 StartZ=0 EndX=-1.5 EndY=17.25 EndZ=0
    g43: LineSegment StartX=-49.19 StartY=14.25 StartZ=0 EndX=-1.5 EndY=14.25 EndZ=0
    g44: LineSegment StartX=-49.19 StartY=11.5 StartZ=0 EndX=-1.5 EndY=11.5 EndZ=0
    g45: LineSegment StartX=-49.19 StartY=8.5 StartZ=0 EndX=-1.5 EndY=8.5 EndZ=0
    g46: LineSegment StartX=-49.19 StartY=5.75 StartZ=0 EndX=-1.5 EndY=5.75 EndZ=0
    g47: LineSegment StartX=-49.19 StartY=2.75 StartZ=0 EndX=-1.5 EndY=2.75 EndZ=0
  constraints (120):
    c: Vertical(g0)
    c: Distance(g0) = 3
    c: Block(g0)
    c: Vertical(g1)
    c: Distance(g1) = 3
    c: Vertical(g2)
    c: Equal(g0,g2) = 3
    c: Block(g2)
    c: Vertical(g3)
    c: Equal(g1,g3) = 3
    c: Vertical(g4)
    c: Equal(g0,g4) = 3
    c: Block(g4)
    c: Vertical(g5)
    c: Equal(g1,g5) = 3
    c: Vertical(g6)
    c: Equal(g0,g6) = 3
    c: Block(g6)
    c: Vertical(g7)
    c: Equal(g1,g7) = 3
    c: Vertical(g8)
    c: Equal(g0,g8) = 3
    c: Block(g8)
    c: Vertical(g9)
    c: Equal(g1,g9) = 3
    c: Vertical(g10)
    c: Equal(g0,g10) = 3
    c: Block(g10)
    c: Vertical(g11)
    c: Equal(g1,g11) = 3
    c: Block(g12)
    c: Block(g13)
    c: Block(g14)
    c: Block(g15)
    c: Block(g16)
    c: Block(g17)
    c: Block(g18)
    c: Block(g19)
    c: Block(g20)
    c: Block(g21)
    c: Block(g22)
    c: Block(g23)
    c: Block(g11)
    c: Block(g9)
    c: Block(g7)
    c: Block(g5)
    c: Block(g3)
    c: Block(g1)
    c: Coincident(g24,g0)
    c: Coincident(g24,g12)
    c: Horizontal(g24)
    c: Coincident(g25,g0)
    c: Coincident(g25,g12)
    c: Horizontal(g25)
    c: Coincident(g26,g1)
    c: Coincident(g26,g13)
    c: Horizontal(g26)
    c: Coincident(g27,g1)
    c: Coincident(g27,g13)
    c: Horizontal(g27)
    c: Coincident(g28,g2)
    c: Coincident(g28,g14)
    c: Horizontal(g28)
    c: Coincident(g29,g2)
    c: Coincident(g29,g14)
    c: Horizontal(g29)
    c: Coincident(g30,g3)
    c: Coincident(g30,g15)
    c: Horizontal(g30)
    c: Coincident(g31,g3)
    c: Coincident(g31,g15)
    c: Horizontal(g31)
    c: Coincident(g32,g4)
    c: Coincident(g32,g16)
    c: Horizontal(g32)
    c: Coincident(g33,g4)
    c: Coincident(g33,g16)
    c: Horizontal(g33)
    c: Coincident(g34,g5)
    c: Coincident(g34,g17)
    c: Horizontal(g34)
    c: Coincident(g35,g5)
    c: Coincident(g35,g17)
    c: Horizontal(g35)
    c: Coincident(g36,g6)
    c: Coincident(g36,g19)
    c: Horizontal(g36)
    c: Coincident(g37,g6)
    c: Coincident(g37,g19)
    c: Horizontal(g37)
    c: Coincident(g38,g7)
    c: Coincident(g38,g18)
    c: Horizontal(g38)
    c: Coincident(g39,g7)
    c: Coincident(g39,g18)
    c: Horizontal(g39)
    c: Coincident(g40,g8)
    c: Coincident(g40,g20)
    c: Horizontal(g40)
    c: Coincident(g41,g8)
    c: Coincident(g41,g20)
    c: Horizontal(g41)
    c: Coincident(g42,g9)
    c: Coincident(g42,g23)
    c: Horizontal(g42)
    c: Coincident(g43,g9)
    c: Coincident(g43,g23)
    c: Horizontal(g43)
    c: Coincident(g44,g10)
    c: Coincident(g44,g22)
    c: Horizontal(g44)
    c: Coincident(g45,g10)
    c: Coincident(g45,g22)
    c: Horizontal(g45)
    c: Coincident(g46,g11)
    c: Coincident(g46,g21)
    c: Horizontal(g46)
    c: Coincident(g47,g11)
    c: Coincident(g47,g21)
    c: Horizontal(g47)
FEATURE [Part::Extrusion] Extrude023
  Base = -> Sketch032
  Dir = (1,-2e-16,2e-16)
  DirMode = 2
  FaceMakerClass = Part::FaceMakerBullseye
  LengthFwd = 19
  LengthRev = 0
  Placement = pos=(-19,0,0) rot=(0,0,1;0rad)
  Solid = true
  Symmetric = false
FEATURE [Part::Fillet] Fillet023
  Base = -> Extrude023
  Edges = <same value as first occurrence — deduplicated (x6 in doc)>
  Placement = pos=(0,0.05,0) rot=(0,0,1;0rad)
FEATURE [Part::Cut] Cut014  label="bottom003"
  Base = -> Cut007
  Tool = -> Fusion047
FEATURE [Part::Cut] Cut021  label="bottom004"
  Base = -> Cut014
  Tool = -> Fillet023
FEATURE [Sketcher::SketchObject] Sketch033
  FullyConstrained = true
  Placement = pos=(117,19,0) rot=(0.57735,0.57735,0.57735;2.0944rad)
  sketch-geometry (8):
    g0: LineSegment StartX=-49.19 StartY=69.25 StartZ=0 EndX=-49.19 EndY=66.25 EndZ=0
    g1: LineSegment StartX=-49.19 StartY=5.75 StartZ=0 EndX=-49.19 EndY=2.75 EndZ=0
    g2: ArcOfCircle CenterX=-1.5 CenterY=67.75 CenterZ=0 NormalX=0 NormalY=0 NormalZ=1 AngleXU=0 Radius=1.5 StartAngle=4.71239 EndAngle=7.85398
    g3: ArcOfCircle CenterX=-1.5 CenterY=4.25 CenterZ=0 NormalX=0 NormalY=0 NormalZ=1 AngleXU=0 Radius=1.5 StartAngle=4.71239 EndAngle=7.85398
    g4: LineSegment StartX=-49.19 StartY=69.25 StartZ=0 EndX=-1.5 EndY=69.25 EndZ=0
    g5: LineSegment StartX=-49.19 StartY=66.25 StartZ=0 EndX=-1.5 EndY=66.25 EndZ=0
    g6: LineSegment StartX=-49.19 StartY=5.75 StartZ=0 EndX=-1.5 EndY=5.75 EndZ=0
    g7: LineSegment StartX=-49.19 StartY=2.75 StartZ=0 EndX=-1.5 EndY=2.75 EndZ=0
  constraints (19):
    c: Vertical(g0)
    c: Distance(g0) = 3
    c: Block(g0)
    c: Vertical(g1)
    c: Block(g2)
    c: Block(g3)
    c: Block(g1)
    c: Coincident(g4,g0)
    c: Coincident(g4,g2)
    c: Horizontal(g4)
    c: Coincident(g5,g0)
    c: Coincident(g5,g2)
    c: Horizontal(g5)
    c: Coincident(g6,g1)
    c: Coincident(g6,g3)
    c: Horizontal(g6)
    c: Coincident(g7,g1)
    c: Coincident(g7,g3)
    c: Horizontal(g7)
FEATURE [Sketcher::SketchObject] Sketch034
  FullyConstrained = true
  Placement = pos=(117,19,0) rot=(0.57735,0.57735,0.57735;2.0944rad)
  sketch-geometry (8):
    g0: LineSegment StartX=-49.19 StartY=63.5 StartZ=0 EndX=-49.19 EndY=60.5 EndZ=0
    g1: LineSegment StartX=-49.19 StartY=11.5 StartZ=0 EndX=-49.19 EndY=8.5 EndZ=0
    g2: ArcOfCircle CenterX=-1.5 CenterY=62 CenterZ=0 NormalX=0 NormalY=0 NormalZ=1 AngleXU=0 Radius=1.5 StartAngle=4.71239 EndAngle=7.85398
    g3: ArcOfCircle CenterX=-1.5 CenterY=10 CenterZ=0 NormalX=0 NormalY=0 NormalZ=1 AngleXU=0 Radius=1.5 StartAngle=4.71239 EndAngle=7.85398
    g4: LineSegment StartX=-49.19 StartY=63.5 StartZ=0 EndX=-1.5 EndY=63.5 EndZ=0
    g5: LineSegment StartX=-49.19 StartY=60.5 StartZ=0 EndX=-1.5 EndY=60.5 EndZ=0
    g6: LineSegment StartX=-49.19 StartY=11.5 StartZ=0 EndX=-1.5 EndY=11.5 EndZ=0
    g7: LineSegment StartX=-49.19 StartY=8.5 StartZ=0 EndX=-1.5 EndY=8.5 EndZ=0
  constraints (19):
    c: Vertical(g0)
    c: Distance(g0) = 3
    c: Vertical(g1)
    c: Block(g1)
    c: Block(g2)
    c: Block(g3)
    c: Block(g0)
    c: Coincident(g4,g0)
    c: Coincident(g4,g2)
    c: Horizontal(g4)
    c: Coincident(g5,g0)
    c: Coincident(g5,g2)
    c: Horizontal(g5)
    c: Coincident(g6,g1)
    c: Coincident(g6,g3)
    c: Horizontal(g6)
    c: Coincident(g7,g1)
    c: Coincident(g7,g3)
    c: Horizontal(g7)
FEATURE [Part::Extrusion] Extrude024
  Base = -> Sketch033
  Dir = (1,0,0)
  DirMode = 2
  FaceMakerClass = Part::FaceMakerBullseye
  LengthFwd = 10
  LengthRev = 0
  Solid = true
  Symmetric = false
FEATURE [Part::Extrusion] Extrude025
  Base = -> Sketch034
  Dir = (1,0,0)
  DirMode = 2
  FaceMakerClass = Part::FaceMakerBullseye
  LengthFwd = 10
  LengthRev = 0
  Solid = true
  Symmetric = false
FEATURE [Part::Fillet] Fillet024  label="removeFromtMoreFrontCaseScrewRetainers"
  Base = -> Extrude024
  Edges = 4 edges r=1.49: [Edge6,Edge11,Edge18,Edge23]
  Placement = pos=(-11,0,0) rot=(0,0,1;0rad)
FEATURE [Part::Fillet] Fillet025  label="removeFromtMoreFrontCaseScrewRetainers001"
  Base = -> Extrude025
  Edges = 4 edges r=1.49: [Edge6,Edge11,Edge18,Edge23]
  Placement = pos=(-19,0,0) rot=(0,0,1;0rad)
FEATURE [Part::Cut] Cut022
  Base = -> Cut015
  Tool = -> Fillet025
FEATURE [Part::Cut] Cut023  label="screwRetainers"
  Base = -> Cut022
  Tool = -> Fillet024
FEATURE [Part::MultiFuse] Fusion056  label="bottom005"
  Shapes = -> [Fusion044,Cut021]
FEATURE [Part::MultiFuse] Fusion057  label="casePillars001"
  Shapes = -> [Cut016,Fusion052]
FEATURE [Part::MultiFuse] Fusion058  label="bottom006"
  Shapes = -> [Fusion056,Cut023]
FEATURE [Part::MultiFuse] Fusion059  label="bottom007"
  Shapes = -> [Fusion058,Fillet005]
FEATURE [Part::MultiFuse] Fusion060  label="bottom008"
  Shapes = -> [Fusion059,Fusion]
FEATURE [Part::MultiFuse] Fusion061  label="top011"
  Shapes = -> [Cut006,Cut020]
FEATURE [Part::MultiFuse] Fusion062  label="top012"
  Shapes = -> [Fusion057,Fusion061]
FEATURE [Sketcher::SketchObject] Sketch035  label="topSketch007"
  FullyConstrained = true
  sketch-geometry (6):
    g0: LineSegment StartX=19 StartY=38 StartZ=0 EndX=117 EndY=38 EndZ=0
    g1: ArcOfCircle CenterX=19 CenterY=19 CenterZ=0 NormalX=0 NormalY=0 NormalZ=1 AngleXU=0 Radius=19 StartAngle=1.5708 EndAngle=3.14159
    g2: LineSegment StartX=117 StartY=38 StartZ=0 EndX=117 EndY=19 EndZ=0
    g3: LineSegment StartX=98 StartY=1.0161e-12 StartZ=0 EndX=5.22862e-06 EndY=1.0161e-12 EndZ=0
    g4: LineSegment StartX=5.22862e-06 StartY=19 StartZ=0 EndX=5.22862e-06 EndY=1.0161e-12 EndZ=0
    g5: ArcOfCircle CenterX=98 CenterY=19 CenterZ=0 NormalX=0 NormalY=0 NormalZ=1 AngleXU=0 Radius=19 StartAngle=4.71239 EndAngle=6.28319
  constraints (16):
    c: Horizontal(g0)
    c: Distance(g0) = 98
    c: Coincident(g1,g0)
    c: Block(g1)
    c: Coincident(g2,g0)
    c: Vertical(g2)
    c: Distance(g2) = 19
    c: Horizontal(g3)
    c: Coincident(g4,g1)
    c: Vertical(g4)
    c: Coincident(g3,g4)
    c: Block(g3)
    c: Coincident(g5,g2)
    c: Coincident(g5,g3)
    c: Block(g0)
    c: Block(g5)
FEATURE [Part::Extrusion] Extrude026  label="sideA001"
  Base = -> Sketch035
  Dir = (0,0,1)
  DirMode = 2
  FaceMakerClass = Part::FaceMakerBullseye
  LengthFwd = 3
  LengthRev = 0
  Placement = pos=(0,0,-2.7) rot=(0,0,1;0rad)
  Solid = true
  Symmetric = false
FEATURE [Sketcher::SketchObject] Sketch036  label="topSketch008"
  FullyConstrained = true
  sketch-geometry (6):
    g0: LineSegment StartX=19 StartY=38 StartZ=0 EndX=117 EndY=38 EndZ=0
    g1: ArcOfCircle CenterX=19 CenterY=19 CenterZ=0 NormalX=0 NormalY=0 NormalZ=1 AngleXU=0 Radius=19 StartAngle=1.5708 EndAngle=3.14159
    g2: LineSegment StartX=117 StartY=38 StartZ=0 EndX=117 EndY=19 EndZ=0
    g3: LineSegment StartX=98 StartY=1.0161e-12 StartZ=0 EndX=5.22862e-06 EndY=1.0161e-12 EndZ=0
    g4: LineSegment StartX=5.22862e-06 StartY=19 StartZ=0 EndX=5.22862e-06 EndY=1.0161e-12 EndZ=0
    g5: ArcOfCircle CenterX=98 CenterY=19 CenterZ=0 NormalX=0 NormalY=0 NormalZ=1 AngleXU=0 Radius=19 StartAngle=4.71239 EndAngle=6.28319
  constraints (16):
    c: Horizontal(g0)
    c: Distance(g0) = 98
    c: Coincident(g1,g0)
    c: Block(g1)
    c: Coincident(g2,g0)
    c: Vertical(g2)
    c: Distance(g2) = 19
    c: Horizontal(g3)
    c: Coincident(g4,g1)
    c: Vertical(g4)
    c: Coincident(g3,g4)
    c: Block(g3)
    c: Coincident(g5,g2)
    c: Coincident(g5,g3)
    c: Block(g0)
    c: Block(g5)
FEATURE [Part::Extrusion] Extrude027  label="sideB001"
  Base = -> Sketch036
  Dir = (0,0,1)
  DirMode = 2
  FaceMakerClass = Part::FaceMakerBullseye
  LengthFwd = 3
  LengthRev = 0
  Placement = pos=(0,0,71.7) rot=(0,0,1;0rad)
  Solid = true
  Symmetric = false
FEATURE [Part::MultiFuse] Fusion064  label="removeFromBottom"
  Shapes = -> [Extrude026,Extrude027]
FEATURE [Part::Cut] Cut024  label="bottom009"
  Base = -> Fusion060
  Tool = -> Fusion064
FEATURE [Sketcher::SketchObject] Sketch037  label="topSketch009"
  FullyConstrained = true
  sketch-geometry (8):
    g0: ArcOfCircle CenterX=19 CenterY=19.1201 CenterZ=0 NormalX=0 NormalY=0 NormalZ=1 AngleXU=0 Radius=18.8799 StartAngle=1.5708 EndAngle=3.14793
    g1: LineSegment StartX=0.120501 StartY=19.0004 StartZ=0 EndX=0.120501 EndY=0.000382114 EndZ=0
    g2: LineSegment StartX=19 StartY=38 StartZ=0 EndX=124 EndY=38 EndZ=0
    g3: LineSegment StartX=0.120501 StartY=0.000382114 StartZ=0 EndX=105.121 EndY=0.000382114 EndZ=0
    g4: LineSegment StartX=124 StartY=38 StartZ=0 EndX=125.616 EndY=38 EndZ=0
    g5: LineSegment StartX=105.121 StartY=0.000382114 StartZ=0 EndX=106.736 EndY=0.000382114 EndZ=0
    g6: ArcOfCircle CenterX=106.616 CenterY=19 CenterZ=0 NormalX=0 NormalY=0 NormalZ=1 AngleXU=0 Radius=19 StartAngle=4.71873 EndAngle=6.28319
    g7: LineSegment StartX=125.616 StartY=38 StartZ=0 EndX=125.616 EndY=19 EndZ=0
  constraints (21):
    c: Block(g0)
    c: Coincident(g1,g0)
    c: Vertical(g1)
    c: Horizontal(g2)
    c: Distance(g2) = 105
    c: Coincident(g2,g0)
    c: Distance(g1) = 19
    c: Coincident(g3,g1)
    c: Horizontal(g3)
    c: Distance(g3) = 105
    c: Coincident(g4,g2)
    c: Horizontal(g4)
    c: Distance(g4) = 1.61553
    c: Horizontal(g5)
    c: Equal(g4,g5) = 1.61553
    c: Coincident(g5,g3)
    c: Block(g6)
    c: Coincident(g6,g5)
    c: Coincident(g7,g4)
    c: Coincident(g7,g6)
    c: Vertical(g7)
FEATURE [Part::Extrusion] Extrude028  label="sideB"
  Base = -> Sketch037
  Dir = (0,0,1)
  DirMode = 2
  FaceMakerClass = Part::FaceMakerBullseye
  LengthFwd = 3
  LengthRev = 0
  Placement = pos=(0,0,72) rot=(0,0,1;0rad)
  Solid = true
  Symmetric = false
FEATURE [Sketcher::SketchObject] Sketch038  label="topSketch010"
  FullyConstrained = true
  sketch-geometry (22):
    g0: LineSegment StartX=5.21097e-06 StartY=3 StartZ=0 EndX=5.21097e-06 EndY=19 EndZ=0
    g1: ArcOfCircle CenterX=19 CenterY=19 CenterZ=0 NormalX=0 NormalY=0 NormalZ=1 AngleXU=0 Radius=19 StartAngle=1.5708 EndAngle=3.14159
    g2: ArcOfCircle CenterX=19 CenterY=19 CenterZ=0 NormalX=0 NormalY=0 NormalZ=1 AngleXU=0 Radius=16 StartAngle=1.5708 EndAngle=3.14159
    g3: LineSegment StartX=114 StartY=35 StartZ=0 EndX=19 EndY=35 EndZ=0
    g4: LineSegment StartX=5.21097e-06 StartY=3 StartZ=0 EndX=5.21097e-06 EndY=0 EndZ=0
    g5: LineSegment StartX=3 StartY=0 StartZ=0 EndX=5.21097e-06 EndY=0 EndZ=0
    g6: LineSegment StartX=3 StartY=19 StartZ=0 EndX=3 EndY=0 EndZ=0
    g7: LineSegment StartX=19 StartY=38 StartZ=0 EndX=124 EndY=38 EndZ=0
    g8: Circle CenterX=119 CenterY=35 CenterZ=0 NormalX=0 NormalY=0 NormalZ=1 AngleXU=0 Radius=1
    g9: Circle CenterX=121 CenterY=35 CenterZ=0 NormalX=0 NormalY=0 NormalZ=1 AngleXU=0 Radius=1
    g10: Circle CenterX=121 CenterY=33 CenterZ=0 NormalX=0 NormalY=0 NormalZ=1 AngleXU=0 Radius=1
    g11: BSplineCurve PolesCount=3 KnotsCount=2 Degree=2 IsPeriodic=0
    g12: GeomPoint X=119 Y=35 Z=0
    g13: GeomPoint X=121 Y=33 Z=0
    g14: LineSegment StartX=119 StartY=35 StartZ=0 EndX=114 EndY=35 EndZ=0
    g15: ArcOfCircle CenterX=105 CenterY=19 CenterZ=0 NormalX=0 NormalY=0 NormalZ=1 AngleXU=0 Radius=16 StartAngle=5.60905 EndAngle=6.28319
    g16: LineSegment StartX=121 StartY=33 StartZ=0 EndX=121 EndY=19 EndZ=0
    g17: LineSegment StartX=117.5 StartY=9.01251 StartZ=0 EndX=121.163 EndY=9.0125 EndZ=0
    g18: ArcOfCircle CenterX=105 CenterY=19 CenterZ=0 NormalX=0 NormalY=0 NormalZ=1 AngleXU=0 Radius=20.6155 StartAngle=5.7297 EndAngle=6.28319
    g19: LineSegment StartX=121.163 StartY=9.0125 StartZ=0 EndX=122.538 EndY=8.16329 EndZ=0
    g20: LineSegment StartX=124 StartY=38 StartZ=0 EndX=125.616 EndY=38 EndZ=0
    g21: LineSegment StartX=125.616 StartY=19 StartZ=0 EndX=125.616 EndY=38 EndZ=0
  constraints (49):
    c: Vertical(g0)
    c: Block(g0)
    c: Coincident(g1,g0)
    c: Block(g1)
    c: Coincident(g2,g1)
    c: Block(g2)
    c: Coincident(g3,g2)
    c: Horizontal(g3)
    c: Tangent(g3,g2)
    c: Coincident(g4,g0)
    c: Distance(g4) = 3
    c: Vertical(g4)
    c: Coincident(g5,g4)
    c: Horizontal(g5)
    c: Coincident(g6,g2)
    c: Coincident(g6,g5)
    c: Vertical(g6)
    c: Horizontal(g7)
    c: Distance(g7) = 105
    c: Coincident(g7,g1)
    c: Block(g3)
    c: Weight(g8) = 1
    c: Equal(g8,g9)
    c: Equal(g8,g10)
    c: InternalAlignment(g8,g11)
    c: InternalAlignment(g9,g11)
    c: InternalAlignment(g10,g11)
    c: InternalAlignment(g12,g11)
    c: InternalAlignment(g13,g11)
    c: Block(g11)
    c: Coincident(g14,g11)
    c: Coincident(g14,g3)
    c: Horizontal(g14)
    c: Block(g15)
    c: Coincident(g16,g11)
    c: Coincident(g16,g15)
    c: Vertical(g16)
    c: Distance(g16) = 14
    c: Coincident(g17,g15)
    c: Block(g18)
    c: Coincident(g19,g18)
    c: Coincident(g20,g7)
    c: Horizontal(g20)
    c: Vertical(g21)
    c: Coincident(g20,g21)
    c: Block(g20)
    c: Block(g21)
    c: Block(g19)
    c: Block(g17)
FEATURE [Part::Extrusion] Extrude029
  Base = -> Sketch038
  Dir = (0,0,1)
  DirMode = 2
  FaceMakerClass = Part::FaceMakerBullseye
  LengthFwd = 72
  LengthRev = 0
  Solid = true
  Symmetric = false
FEATURE [Part::Feature] Face085
  shape: bbox 4.8 x 25.5 x 2e-07 mm, 1 faces, 0 solids (baked)
FEATURE [Part::Revolution] Revolve089  label="moreFrontCaseScrewPost003"
  Angle = 360
  Axis = (0,1,0)
  Base = (0,0,0)
  FaceMakerClass = Part::FaceMakerBullseye
  Placement = pos=(109.5,4.5,3.5) rot=(0,0,1;0rad)
  Solid = false
  Source = -> Face085
  Symmetric = false
FEATURE [Part::Feature] Face086
  shape: bbox 4.8 x 25.5 x 2e-07 mm, 1 faces, 0 solids (baked)
FEATURE [Part::Revolution] Revolve090  label="moreFrontCaseScrewPost004"
  Angle = 360
  Axis = (0,1,0)
  Base = (0,0,0)
  FaceMakerClass = Part::FaceMakerBullseye
  Placement = pos=(109.5,4.5,68.5) rot=(0,0,1;0rad)
  Solid = false
  Source = -> Face086
  Symmetric = false
FEATURE [Part::Fillet] Fillet026  label="top013"
  Base = -> Extrude029
  Edges = 1 edges r=2: [Edge35]
FEATURE [Sketcher::SketchObject] Sketch039
  FullyConstrained = true
  sketch-geometry (7):
    g0: LineSegment StartX=0 StartY=0 StartZ=0 EndX=0 EndY=6 EndZ=0
    g1: Circle CenterX=0 CenterY=0 CenterZ=0 NormalX=0 NormalY=0 NormalZ=1 AngleXU=0 Radius=1
    g2: Circle CenterX=8 CenterY=6 CenterZ=0 NormalX=0 NormalY=0 NormalZ=1 AngleXU=0 Radius=1
    g3: BSplineCurve PolesCount=3 KnotsCount=2 Degree=2 IsPeriodic=0
    g4: GeomPoint X=0 Y=0 Z=0
    g5: GeomPoint X=8 Y=6 Z=0
    g6: LineSegment StartX=0 StartY=6 StartZ=0 EndX=8 EndY=6 EndZ=0
  constraints (14):
    c: Coincident(g0,g-1)
    c: Distance(g0) = 6
    c: Vertical(g0)
    c: Coincident(g3,g0)
    c: Weight(g1) = 1
    c: Equal(g1,g2)
    c: InternalAlignment(g1,g3)
    c: InternalAlignment(g2,g3)
    c: InternalAlignment(g4,g3)
    c: InternalAlignment(g5,g3)
    c: Block(g3)
    c: Coincident(g6,g0)
    c: Coincident(g6,g3)
    c: Horizontal(g6)
FEATURE [Sketcher::SketchObject] Sketch040
  FullyConstrained = true
  sketch-geometry (7):
    g0: LineSegment StartX=0 StartY=0 StartZ=0 EndX=0 EndY=6 EndZ=0
    g1: Circle CenterX=0 CenterY=0 CenterZ=0 NormalX=0 NormalY=0 NormalZ=1 AngleXU=0 Radius=1
    g2: Circle CenterX=8 CenterY=6 CenterZ=0 NormalX=0 NormalY=0 NormalZ=1 AngleXU=0 Radius=1
    g3: BSplineCurve PolesCount=3 KnotsCount=2 Degree=2 IsPeriodic=0
    g4: GeomPoint X=0 Y=0 Z=0
    g5: GeomPoint X=8 Y=6 Z=0
    g6: LineSegment StartX=0 StartY=6 StartZ=0 EndX=8 EndY=6 EndZ=0
  constraints (14):
    c: Coincident(g0,g-1)
    c: Distance(g0) = 6
    c: Vertical(g0)
    c: Coincident(g3,g0)
    c: Weight(g1) = 1
    c: Equal(g1,g2)
    c: InternalAlignment(g1,g3)
    c: InternalAlignment(g2,g3)
    c: InternalAlignment(g4,g3)
    c: InternalAlignment(g5,g3)
    c: Block(g3)
    c: Coincident(g6,g0)
    c: Coincident(g6,g3)
    c: Horizontal(g6)
FEATURE [Sketcher::SketchObject] Sketch041
  FullyConstrained = true
  sketch-geometry (7):
    g0: LineSegment StartX=0 StartY=0 StartZ=0 EndX=0 EndY=6 EndZ=0
    g1: Circle CenterX=0 CenterY=0 CenterZ=0 NormalX=0 NormalY=0 NormalZ=1 AngleXU=0 Radius=1
    g2: Circle CenterX=8 CenterY=6 CenterZ=0 NormalX=0 NormalY=0 NormalZ=1 AngleXU=0 Radius=1
    g3: BSplineCurve PolesCount=3 KnotsCount=2 Degree=2 IsPeriodic=0
    g4: GeomPoint X=0 Y=0 Z=0
    g5: GeomPoint X=8 Y=6 Z=0
    g6: LineSegment StartX=0 StartY=6 StartZ=0 EndX=8 EndY=6 EndZ=0
  constraints (14):
    c: Coincident(g0,g-1)
    c: Distance(g0) = 6
    c: Vertical(g0)
    c: Coincident(g3,g0)
    c: Weight(g1) = 1
    c: Equal(g1,g2)
    c: InternalAlignment(g1,g3)
    c: InternalAlignment(g2,g3)
    c: InternalAlignment(g4,g3)
    c: InternalAlignment(g5,g3)
    c: Block(g3)
    c: Coincident(g6,g0)
    c: Coincident(g6,g3)
    c: Horizontal(g6)
FEATURE [Sketcher::SketchObject] Sketch042
  FullyConstrained = true
  sketch-geometry (7):
    g0: LineSegment StartX=0 StartY=0 StartZ=0 EndX=0 EndY=6 EndZ=0
    g1: Circle CenterX=0 CenterY=0 CenterZ=0 NormalX=0 NormalY=0 NormalZ=1 AngleXU=0 Radius=1
    g2: Circle CenterX=8 CenterY=6 CenterZ=0 NormalX=0 NormalY=0 NormalZ=1 AngleXU=0 Radius=1
    g3: BSplineCurve PolesCount=3 KnotsCount=2 Degree=2 IsPeriodic=0
    g4: GeomPoint X=0 Y=0 Z=0
    g5: GeomPoint X=8 Y=6 Z=0
    g6: LineSegment StartX=0 StartY=6 StartZ=0 EndX=8 EndY=6 EndZ=0
  constraints (14):
    c: Coincident(g0,g-1)
    c: Distance(g0) = 6
    c: Vertical(g0)
    c: Coincident(g3,g0)
    c: Weight(g1) = 1
    c: Equal(g1,g2)
    c: InternalAlignment(g1,g3)
    c: InternalAlignment(g2,g3)
    c: InternalAlignment(g4,g3)
    c: InternalAlignment(g5,g3)
    c: Block(g3)
    c: Coincident(g6,g0)
    c: Coincident(g6,g3)
    c: Horizontal(g6)
FEATURE [Part::Extrusion] Extrude030  label="caseScrewPillarBracket008"
  Base = -> Sketch039
  Dir = (0,0,1)
  DirMode = 2
  FaceMakerClass = Part::FaceMakerBullseye
  LengthFwd = 2.4
  LengthRev = 0
  Placement = pos=(15.76,29,8.8) rot=(0,1,0;0rad)
  Solid = true
  Symmetric = false
FEATURE [Part::Extrusion] Extrude031  label="caseScrewPillarBracket009"
  Base = -> Sketch040
  Dir = (0,0,1)
  DirMode = 2
  FaceMakerClass = Part::FaceMakerBullseye
  LengthFwd = 2.4
  LengthRev = 0
  Placement = pos=(15.76,29,60.8) rot=(0,0,1;0rad)
  Solid = true
  Symmetric = false
FEATURE [Part::Extrusion] Extrude032  label="caseScrewPillarBracket010"
  Base = -> Sketch041
  Dir = (0,0,1)
  DirMode = 2
  FaceMakerClass = Part::FaceMakerBullseye
  LengthFwd = 2.4
  LengthRev = 0
  Placement = pos=(13.7,29,13.26) rot=(0,-1,0;1.5708rad)
  Solid = true
  Symmetric = false
FEATURE [Part::Extrusion] Extrude033  label="caseScrewPillarBracket011"
  Base = -> Sketch042
  Dir = (0,0,1)
  DirMode = 2
  FaceMakerClass = Part::FaceMakerBullseye
  LengthFwd = 2.4
  LengthRev = 0
  Placement = pos=(11.3,29,58.74) rot=(0,1,0;1.5708rad)
  Solid = true
  Symmetric = false
FEATURE [Sketcher::SketchObject] Sketch043
  FullyConstrained = true
  sketch-geometry (7):
    g0: LineSegment StartX=0 StartY=0 StartZ=0 EndX=0 EndY=6 EndZ=0
    g1: Circle CenterX=0 CenterY=0 CenterZ=0 NormalX=0 NormalY=0 NormalZ=1 AngleXU=0 Radius=1
    g2: Circle CenterX=8 CenterY=6 CenterZ=0 NormalX=0 NormalY=0 NormalZ=1 AngleXU=0 Radius=1
    g3: BSplineCurve PolesCount=3 KnotsCount=2 Degree=2 IsPeriodic=0
    g4: GeomPoint X=0 Y=0 Z=0
    g5: GeomPoint X=8 Y=6 Z=0
    g6: LineSegment StartX=0 StartY=6 StartZ=0 EndX=8 EndY=6 EndZ=0
  constraints (14):
    c: Coincident(g0,g-1)
    c: Distance(g0) = 6
    c: Vertical(g0)
    c: Coincident(g3,g0)
    c: Weight(g1) = 1
    c: Equal(g1,g2)
    c: InternalAlignment(g1,g3)
    c: InternalAlignment(g2,g3)
    c: InternalAlignment(g4,g3)
    c: InternalAlignment(g5,g3)
    c: Block(g3)
    c: Coincident(g6,g0)
    c: Coincident(g6,g3)
    c: Horizontal(g6)
FEATURE [Part::Extrusion] Extrude034  label="caseScrewPillarBracket012"
  Base = -> Sketch043
  Dir = (0,0,1)
  DirMode = 2
  FaceMakerClass = Part::FaceMakerBullseye
  LengthFwd = 2.4
  LengthRev = 0
  Placement = pos=(88.3,29,65.23) rot=(0,1,0;1.5708rad)
  Solid = true
  Symmetric = false
FEATURE [Sketcher::SketchObject] Sketch044
  FullyConstrained = true
  sketch-geometry (7):
    g0: LineSegment StartX=0 StartY=0 StartZ=0 EndX=0 EndY=6 EndZ=0
    g1: Circle CenterX=0 CenterY=0 CenterZ=0 NormalX=0 NormalY=0 NormalZ=1 AngleXU=0 Radius=1
    g2: Circle CenterX=8 CenterY=6 CenterZ=0 NormalX=0 NormalY=0 NormalZ=1 AngleXU=0 Radius=1
    g3: BSplineCurve PolesCount=3 KnotsCount=2 Degree=2 IsPeriodic=0
    g4: GeomPoint X=0 Y=0 Z=0
    g5: GeomPoint X=8 Y=6 Z=0
    g6: LineSegment StartX=0 StartY=6 StartZ=0 EndX=8 EndY=6 EndZ=0
  constraints (14):
    c: Coincident(g0,g-1)
    c: Distance(g0) = 6
    c: Vertical(g0)
    c: Coincident(g3,g0)
    c: Weight(g1) = 1
    c: Equal(g1,g2)
    c: InternalAlignment(g1,g3)
    c: InternalAlignment(g2,g3)
    c: InternalAlignment(g4,g3)
    c: InternalAlignment(g5,g3)
    c: Block(g3)
    c: Coincident(g6,g0)
    c: Coincident(g6,g3)
    c: Horizontal(g6)
FEATURE [Part::Extrusion] Extrude035  label="caseScrewPillarBracket013"
  Base = -> Sketch044
  Dir = (0,0,1)
  DirMode = 2
  FaceMakerClass = Part::FaceMakerBullseye
  LengthFwd = 2.4
  LengthRev = 0
  Placement = pos=(90.7,29,6.77) rot=(0,-1,0;1.5708rad)
  Solid = true
  Symmetric = false
FEATURE [Sketcher::SketchObject] Sketch045
  FullyConstrained = true
  sketch-geometry (7):
    g0: LineSegment StartX=0 StartY=0 StartZ=0 EndX=0 EndY=6 EndZ=0
    g1: Circle CenterX=0 CenterY=0 CenterZ=0 NormalX=0 NormalY=0 NormalZ=1 AngleXU=0 Radius=1
    g2: Circle CenterX=8 CenterY=6 CenterZ=0 NormalX=0 NormalY=0 NormalZ=1 AngleXU=0 Radius=1
    g3: BSplineCurve PolesCount=3 KnotsCount=2 Degree=2 IsPeriodic=0
    g4: GeomPoint X=0 Y=0 Z=0
    g5: GeomPoint X=8 Y=6 Z=0
    g6: LineSegment StartX=0 StartY=6 StartZ=0 EndX=8 EndY=6 EndZ=0
  constraints (14):
    c: Coincident(g0,g-1)
    c: Distance(g0) = 6
    c: Vertical(g0)
    c: Coincident(g3,g0)
    c: Weight(g1) = 1
    c: Equal(g1,g2)
    c: InternalAlignment(g1,g3)
    c: InternalAlignment(g2,g3)
    c: InternalAlignment(g4,g3)
    c: InternalAlignment(g5,g3)
    c: Block(g3)
    c: Coincident(g6,g0)
    c: Coincident(g6,g3)
    c: Horizontal(g6)
FEATURE [Sketcher::SketchObject] Sketch046
  FullyConstrained = true
  sketch-geometry (7):
    g0: LineSegment StartX=0 StartY=0 StartZ=0 EndX=0 EndY=6 EndZ=0
    g1: Circle CenterX=0 CenterY=0 CenterZ=0 NormalX=0 NormalY=0 NormalZ=1 AngleXU=0 Radius=1
    g2: Circle CenterX=8 CenterY=6 CenterZ=0 NormalX=0 NormalY=0 NormalZ=1 AngleXU=0 Radius=1
    g3: BSplineCurve PolesCount=3 KnotsCount=2 Degree=2 IsPeriodic=0
    g4: GeomPoint X=0 Y=0 Z=0
    g5: GeomPoint X=8 Y=6 Z=0
    g6: LineSegment StartX=0 StartY=6 StartZ=0 EndX=8 EndY=6 EndZ=0
  constraints (14):
    c: Coincident(g0,g-1)
    c: Distance(g0) = 6
    c: Vertical(g0)
    c: Coincident(g3,g0)
    c: Weight(g1) = 1
    c: Equal(g1,g2)
    c: InternalAlignment(g1,g3)
    c: InternalAlignment(g2,g3)
    c: InternalAlignment(g4,g3)
    c: InternalAlignment(g5,g3)
    c: Block(g3)
    c: Coincident(g6,g0)
    c: Coincident(g6,g3)
    c: Horizontal(g6)
FEATURE [Part::Extrusion] Extrude036  label="caseScrewPillarBracket014"
  Base = -> Sketch045
  Dir = (0,0,1)
  DirMode = 2
  FaceMakerClass = Part::FaceMakerBullseye
  LengthFwd = 2.4
  LengthRev = 0
  Placement = pos=(110.7,29,6.77) rot=(0,-1,0;1.5708rad)
  Solid = true
  Symmetric = false
FEATURE [Part::Extrusion] Extrude037  label="caseScrewPillarBracket015"
  Base = -> Sketch046
  Dir = (0,0,1)
  DirMode = 2
  FaceMakerClass = Part::FaceMakerBullseye
  LengthFwd = 2.4
  LengthRev = 0
  Placement = pos=(108.3,29,65.23) rot=(0,1,0;1.5708rad)
  Solid = true
  Symmetric = false
FEATURE [Part::Box] Box013  label="frontCaseScrewPillarBracket002"
  AttacherType = Attacher::AttachEngine3D
  Height = 2.4
  Length = 22
  Placement = pos=(87,28,2.3) rot=(0,0,1;0rad)
  Width = 7
FEATURE [Part::Box] Box014  label="frontCaseScrewPillarBracket003"
  AttacherType = Attacher::AttachEngine3D
  Height = 2.4
  Length = 22
  Placement = pos=(87,28,67.3) rot=(0,0,1;0rad)
  Width = 7
FEATURE [Part::Feature] Face087
  shape: bbox 4.8 x 30.2 x 2e-07 mm, 1 faces, 0 solids (baked)
FEATURE [Part::Revolution] Revolve091  label="frontCaseScrewPost004"
  Angle = 360
  Axis = (0,1,0)
  Base = (0,0,0)
  FaceMakerClass = Part::FaceMakerBullseye
  Placement = pos=(89.5,4.5,3.5) rot=(0,0,1;0rad)
  Solid = false
  Source = -> Face087
  Symmetric = false
FEATURE [Part::Feature] Face088
  shape: bbox 4.8 x 30.2 x 2e-07 mm, 1 faces, 0 solids (baked)
FEATURE [Part::Revolution] Revolve092  label="frontCaseScrewPost005"
  Angle = 360
  Axis = (0,1,0)
  Base = (0,0,0)
  FaceMakerClass = Part::FaceMakerBullseye
  Placement = pos=(89.5,4.5,68.5) rot=(0,0,1;0rad)
  Solid = false
  Source = -> Face088
  Symmetric = false
FEATURE [Part::Feature] Face089
  shape: bbox 3.5 x 30.2 x 2e-07 mm, 1 faces, 0 solids (baked)
FEATURE [Part::Revolution] Revolve093  label="backCaseScrewPost002"
  Angle = 360
  Axis = (0,1,0)
  Base = (0,0,0)
  FaceMakerClass = Part::FaceMakerBullseye
  Placement = pos=(12.5,4.5,10) rot=(0,0,1;0rad)
  Solid = false
  Source = -> Face089
  Symmetric = false
FEATURE [Part::Feature] Face090
  shape: bbox 3.5 x 30.2 x 2e-07 mm, 1 faces, 0 solids (baked)
FEATURE [Part::Revolution] Revolve094  label="backCaseScrewPost003"
  Angle = 360
  Axis = (0,1,0)
  Base = (0,0,0)
  FaceMakerClass = Part::FaceMakerBullseye
  Placement = pos=(12.5,4.5,62) rot=(0,0,1;0rad)
  Solid = false
  Source = -> Face090
  Symmetric = false
FEATURE [Part::Box] Box015  label="Cube011"
  AttacherType = Attacher::AttachEngine3D
  Height = 28.8
  Length = 3
  Placement = pos=(107.3,28,21.6) rot=(0,0,1;0rad)
  Width = 7
FEATURE [Part::Box] Box016  label="Cube012"
  AttacherType = Attacher::AttachEngine3D
  Height = 3
  Length = 7.4
  Placement = pos=(107.3,28,18.6) rot=(0,0,1;0rad)
  Width = 7
FEATURE [Part::Box] Box017  label="Cube013"
  AttacherType = Attacher::AttachEngine3D
  Height = 3
  Length = 7.4
  Placement = pos=(107.3,28,50.4) rot=(0,0,1;0rad)
  Width = 7
FEATURE [Part::Cylinder] Cylinder024
  Angle = 360
  AttacherType = Attacher::AttachEngine3D
  Height = 20
  Placement = pos=(0,0,36.15) rot=(0,0,1;0rad)
  Radius = 14.3
FEATURE [Part::Cylinder] Cylinder025
  Angle = 360
  AttacherType = Attacher::AttachEngine3D
  Height = 10
  Placement = pos=(0,0,36.15) rot=(0,0,1;0rad)
  Radius = 4
FEATURE [Part::MultiFuse] Fusion066  label="removeToCreteHoleForPlugHousing009"
  Placement = pos=(70,19,36) rot=(0,1,0;1.5708rad)
  Shapes = -> [Cylinder024,Cylinder025]
FEATURE [Part::MultiFuse] Fusion065  label="plugHousingBracketHolder002"
  Shapes = -> [Box017,Box015,Box016]
FEATURE [Part::Cut] Cut025  label="plugHousingBracketHolder003"
  Base = -> Fusion065
  Placement = pos=(7,0,0) rot=(0,0,1;0rad)
  Tool = -> Fusion066
FEATURE [Sketcher::SketchObject] Sketch047
  FullyConstrained = false
  Placement = pos=(0,0,0) rot=(1,0,0;1.5708rad)
  sketch-geometry (24):
    g0: ArcOfCircle CenterX=-4 CenterY=-10.5 CenterZ=0 NormalX=0 NormalY=0 NormalZ=1 AngleXU=0 Radius=1.5 StartAngle=6e-16 EndAngle=3.14159
    g1: ArcOfCircle CenterX=-34.2 CenterY=-10.5 CenterZ=0 NormalX=0 NormalY=0 NormalZ=1 AngleXU=0 Radius=1.5 StartAngle=0 EndAngle=3.14159
    g2: ArcOfCircle CenterX=-34.2 CenterY=-27.7 CenterZ=0 NormalX=0 NormalY=0 NormalZ=1 AngleXU=0 Radius=1.5 StartAngle=3.14159 EndAngle=6.28319
    g3: ArcOfCircle CenterX=-4 CenterY=-27.7 CenterZ=0 NormalX=0 NormalY=0 NormalZ=1 AngleXU=0 Radius=1.5 StartAngle=3.1416 EndAngle=6.28319
    g4: ArcOfCircle CenterX=-10 CenterY=-4.3 CenterZ=0 NormalX=0 NormalY=0 NormalZ=1 AngleXU=0 Radius=1.5 StartAngle=2e-16 EndAngle=3.14159
    g5: ArcOfCircle CenterX=-16.1 CenterY=-1.8 CenterZ=0 NormalX=0 NormalY=0 NormalZ=1 AngleXU=0 Radius=1.5 StartAngle=5e-16 EndAngle=3.14159
    g6: ArcOfCircle CenterX=-22.1 CenterY=-1.8 CenterZ=0 NormalX=0 NormalY=0 NormalZ=1 AngleXU=0 Radius=1.5 StartAngle=5e-16 EndAngle=3.14159
    g7: ArcOfCircle CenterX=-28.2 CenterY=-4.3 CenterZ=0 NormalX=0 NormalY=0 NormalZ=1 AngleXU=0 Radius=1.5 StartAngle=2e-16 EndAngle=3.14159
    g8: ArcOfCircle CenterX=-10 CenterY=-33.9 CenterZ=0 NormalX=0 NormalY=0 NormalZ=1 AngleXU=0 Radius=1.5 StartAngle=3.14159 EndAngle=6.28319
    g9: ArcOfCircle CenterX=-16.1 CenterY=-36.4 CenterZ=0 NormalX=0 NormalY=0 NormalZ=1 AngleXU=0 Radius=1.5 StartAngle=3.14159 EndAngle=6.28319
    g10: ArcOfCircle CenterX=-22.1 CenterY=-36.4 CenterZ=0 NormalX=0 NormalY=0 NormalZ=1 AngleXU=0 Radius=1.5 StartAngle=3.14159 EndAngle=6.28319
    g11: ArcOfCircle CenterX=-28.2 CenterY=-33.9 CenterZ=0 NormalX=0 NormalY=0 NormalZ=1 AngleXU=0 Radius=1.5 StartAngle=3.14159 EndAngle=6.28319
    g12: LineSegment StartX=-35.7 StartY=-10.5 StartZ=0 EndX=-35.7 EndY=-27.7 EndZ=0
    g13: LineSegment StartX=-32.7 StartY=-10.5 StartZ=0 EndX=-32.7 EndY=-27.7 EndZ=0
    g14: LineSegment StartX=-29.7 StartY=-33.9 StartZ=0 EndX=-29.7 EndY=-4.3 EndZ=0
    g15: LineSegment StartX=-26.7 StartY=-33.9 StartZ=0 EndX=-26.7 EndY=-4.3 EndZ=0
    g16: LineSegment StartX=-2.5 StartY=-10.5 StartZ=0 EndX=-2.5 EndY=-27.7 EndZ=0
    g17: LineSegment StartX=-8.5 StartY=-4.3 StartZ=0 EndX=-8.5 EndY=-33.9 EndZ=0
    g18: LineSegment StartX=-5.5 StartY=-10.5 StartZ=0 EndX=-5.5 EndY=-27.7 EndZ=0
    g19: LineSegment StartX=-11.5 StartY=-4.3 StartZ=0 EndX=-11.5 EndY=-33.9 EndZ=0
    g20: LineSegment StartX=-14.6 StartY=-1.8 StartZ=0 EndX=-14.6 EndY=-36.4 EndZ=0
    g21: LineSegment StartX=-17.6 StartY=-1.8 StartZ=0 EndX=-17.6 EndY=-36.4 EndZ=0
    g22: LineSegment StartX=-20.6 StartY=-36.4 StartZ=0 EndX=-20.6 EndY=-1.8 EndZ=0
    g23: LineSegment StartX=-23.6 StartY=-1.8 StartZ=0 EndX=-23.6 EndY=-36.4 EndZ=0
  constraints (48):
    c: Block(g0)
    c: Block(g1)
    c: Block(g2)
    c: Block(g3)
    c: Block(g4)
    c: Block(g5)
    c: Block(g6)
    c: Block(g7)
    c: Block(g8)
    c: Block(g9)
    c: Block(g10)
    c: Block(g11)
    c: Coincident(g12,g1)
    c: Coincident(g12,g2)
    c: Vertical(g12)
    c: Coincident(g13,g1)
    c: Coincident(g13,g2)
    c: Vertical(g13)
    c: Coincident(g14,g11)
    c: Coincident(g14,g7)
    c: Vertical(g14)
    c: Coincident(g15,g11)
    c: Coincident(g15,g7)
    c: Vertical(g15)
    c: Coincident(g16,g0)
    c: Coincident(g16,g3)
    c: Vertical(g16)
    c: Coincident(g17,g4)
    c: Coincident(g17,g8)
    c: Vertical(g17)
    c: Coincident(g18,g0)
    c: Coincident(g18,g3)
    c: Vertical(g18)
    c: Coincident(g19,g4)
    c: Coincident(g19,g8)
    c: Vertical(g19)
    c: Coincident(g20,g5)
    c: Coincident(g20,g9)
    c: Vertical(g20)
    c: Coincident(g21,g5)
    c: Coincident(g21,g9)
    c: Vertical(g21)
    c: Coincident(g22,g10)
    c: Coincident(g22,g6)
    c: Vertical(g22)
    c: Coincident(g23,g6)
    c: Coincident(g23,g10)
    c: Vertical(g23)
FEATURE [Part::Extrusion] Extrude038  label="removeToCreateFanGrillHoles001"
  Base = -> Sketch047
  Dir = (0,-1,6e-16)
  DirMode = 2
  FaceMakerClass = Part::FaceMakerBullseye
  LengthFwd = 10
  LengthRev = 0
  Placement = pos=(65.4,44,54.82) rot=(0,0,1;0rad)
  Solid = true
  Symmetric = false
FEATURE [Part::Feature] Wire004
  shape: bbox 11 x 5.2 x 2e-07 mm, 0 faces, 0 solids (baked)
FEATURE [Part::Revolution] Revolve095
  Angle = 360
  Axis = (0,1,0)
  Base = (0,0,0)
  FaceMakerClass = Part::FaceMakerBullseye
  Placement = pos=(30.3,38,19.7) rot=(0,0,1;0rad)
  Solid = true
  Source = -> Wire004
  Symmetric = false
FEATURE [Part::Feature] Wire005
  shape: bbox 11 x 5.2 x 2e-07 mm, 0 faces, 0 solids (baked)
FEATURE [Part::Revolution] Revolve096
  Angle = 360
  Axis = (0,1,0)
  Base = (0,0,0)
  FaceMakerClass = Part::FaceMakerBullseye
  Placement = pos=(30.3,38,51.7) rot=(0,0,1;0rad)
  Solid = true
  Source = -> Wire005
  Symmetric = false
FEATURE [Part::Feature] Wire006
  shape: bbox 11 x 5.2 x 2e-07 mm, 0 faces, 0 solids (baked)
FEATURE [Part::Revolution] Revolve097
  Angle = 360
  Axis = (0,1,0)
  Base = (0,0,0)
  FaceMakerClass = Part::FaceMakerBullseye
  Placement = pos=(62.3,38,51.7) rot=(0,0,1;0rad)
  Solid = true
  Source = -> Wire006
  Symmetric = false
FEATURE [Part::Feature] Wire007
  shape: bbox 11 x 5.2 x 2e-07 mm, 0 faces, 0 solids (baked)
FEATURE [Part::Revolution] Revolve098
  Angle = 360
  Axis = (0,1,0)
  Base = (0,0,0)
  FaceMakerClass = Part::FaceMakerBullseye
  Placement = pos=(62.3,38,19.7) rot=(0,0,1;0rad)
  Solid = true
  Source = -> Wire007
  Symmetric = false
FEATURE [Part::MultiFuse] Fusion067  label="fanScrewHousing002"
  Shapes = -> [Revolve098,Revolve097,Revolve096,Revolve095]
FEATURE [Part::Feature] Face091 .. Face094  x4 (patterned run collapsed; names and placements below)
  shape: bbox 3.5 x 17.8 x 2e-07 mm, 1 faces, 0 solids (baked)
FEATURE [Part::Revolution] Revolve099  label="removeToCreateScrewAndThreadedInsertHole026"
  Angle = 360
  Axis = (0,1,0)
  Base = (0,0,0)
  FaceMakerClass = Part::FaceMakerBullseye
  Placement = pos=(62.3,30.3,19.7) rot=(0,0,1;0rad)
  Solid = false
  Source = -> Face091
  Symmetric = false
FEATURE [Part::Revolution] Revolve100  label="removeToCreateScrewAndThreadedInsertHole027"
  Angle = 360
  Axis = (0,1,0)
  Base = (0,0,0)
  FaceMakerClass = Part::FaceMakerBullseye
  Placement = pos=(62.3,30.3,51.7) rot=(0,0,1;0rad)
  Solid = false
  Source = -> Face092
  Symmetric = false
FEATURE [Part::Revolution] Revolve101  label="removeToCreateScrewAndThreadedInsertHole028"
  Angle = 360
  Axis = (0,1,0)
  Base = (0,0,0)
  FaceMakerClass = Part::FaceMakerBullseye
  Placement = pos=(30.3,30.3,19.7) rot=(0,0,1;0rad)
  Solid = false
  Source = -> Face093
  Symmetric = false
FEATURE [Part::Revolution] Revolve102  label="removeToCreateScrewAndThreadedInsertHole029"
  Angle = 360
  Axis = (0,1,0)
  Base = (0,0,0)
  FaceMakerClass = Part::FaceMakerBullseye
  Placement = pos=(30.3,30.3,51.7) rot=(0,0,1;0rad)
  Solid = false
  Source = -> Face094
  Symmetric = false
FEATURE [Part::MultiFuse] Fusion068  label="createThreadedInsertHolesForFan002"
  Shapes = -> [Revolve099,Revolve100,Revolve101,Revolve102]
FEATURE [Part::Cut] Cut026  label="fanScrewHousing003"
  Base = -> Fusion067
  Tool = -> Fusion068
FEATURE [Sketcher::SketchObject] Sketch048
  FullyConstrained = false
  Placement = pos=(0,0,0) rot=(1,0,0;1.5708rad)
  sketch-geometry (24):
    g0: ArcOfCircle CenterX=-4 CenterY=-10.5 CenterZ=0 NormalX=0 NormalY=0 NormalZ=1 AngleXU=0 Radius=1.5 StartAngle=6e-16 EndAngle=3.14159
    g1: ArcOfCircle CenterX=-34.2 CenterY=-10.5 CenterZ=0 NormalX=0 NormalY=0 NormalZ=1 AngleXU=0 Radius=1.5 StartAngle=0 EndAngle=3.14159
    g2: ArcOfCircle CenterX=-34.2 CenterY=-27.7 CenterZ=0 NormalX=0 NormalY=0 NormalZ=1 AngleXU=0 Radius=1.5 StartAngle=3.14159 EndAngle=6.28319
    g3: ArcOfCircle CenterX=-4 CenterY=-27.7 CenterZ=0 NormalX=0 NormalY=0 NormalZ=1 AngleXU=0 Radius=1.5 StartAngle=3.1416 EndAngle=6.28319
    g4: ArcOfCircle CenterX=-10 CenterY=-4.3 CenterZ=0 NormalX=0 NormalY=0 NormalZ=1 AngleXU=0 Radius=1.5 StartAngle=2e-16 EndAngle=3.14159
    g5: ArcOfCircle CenterX=-16.1 CenterY=-1.8 CenterZ=0 NormalX=0 NormalY=0 NormalZ=1 AngleXU=0 Radius=1.5 StartAngle=5e-16 EndAngle=3.14159
    g6: ArcOfCircle CenterX=-22.1 CenterY=-1.8 CenterZ=0 NormalX=0 NormalY=0 NormalZ=1 AngleXU=0 Radius=1.5 StartAngle=5e-16 EndAngle=3.14159
    g7: ArcOfCircle CenterX=-28.2 CenterY=-4.3 CenterZ=0 NormalX=0 NormalY=0 NormalZ=1 AngleXU=0 Radius=1.5 StartAngle=2e-16 EndAngle=3.14159
    g8: ArcOfCircle CenterX=-10 CenterY=-33.9 CenterZ=0 NormalX=0 NormalY=0 NormalZ=1 AngleXU=0 Radius=1.5 StartAngle=3.14159 EndAngle=6.28319
    g9: ArcOfCircle CenterX=-16.1 CenterY=-36.4 CenterZ=0 NormalX=0 NormalY=0 NormalZ=1 AngleXU=0 Radius=1.5 StartAngle=3.14159 EndAngle=6.28319
    g10: ArcOfCircle CenterX=-22.1 CenterY=-36.4 CenterZ=0 NormalX=0 NormalY=0 NormalZ=1 AngleXU=0 Radius=1.5 StartAngle=3.14159 EndAngle=6.28319
    g11: ArcOfCircle CenterX=-28.2 CenterY=-33.9 CenterZ=0 NormalX=0 NormalY=0 NormalZ=1 AngleXU=0 Radius=1.5 StartAngle=3.14159 EndAngle=6.28319
    g12: LineSegment StartX=-35.7 StartY=-10.5 StartZ=0 EndX=-35.7 EndY=-27.7 EndZ=0
    g13: LineSegment StartX=-32.7 StartY=-10.5 StartZ=0 EndX=-32.7 EndY=-27.7 EndZ=0
    g14: LineSegment StartX=-29.7 StartY=-33.9 StartZ=0 EndX=-29.7 EndY=-4.3 EndZ=0
    g15: LineSegment StartX=-26.7 StartY=-33.9 StartZ=0 EndX=-26.7 EndY=-4.3 EndZ=0
    g16: LineSegment StartX=-2.5 StartY=-10.5 StartZ=0 EndX=-2.5 EndY=-27.7 EndZ=0
    g17: LineSegment StartX=-8.5 StartY=-4.3 StartZ=0 EndX=-8.5 EndY=-33.9 EndZ=0
    g18: LineSegment StartX=-5.5 StartY=-10.5 StartZ=0 EndX=-5.5 EndY=-27.7 EndZ=0
    g19: LineSegment StartX=-11.5 StartY=-4.3 StartZ=0 EndX=-11.5 EndY=-33.9 EndZ=0
    g20: LineSegment StartX=-14.6 StartY=-1.8 StartZ=0 EndX=-14.6 EndY=-36.4 EndZ=0
    g21: LineSegment StartX=-17.6 StartY=-1.8 StartZ=0 EndX=-17.6 EndY=-36.4 EndZ=0
    g22: LineSegment StartX=-20.6 StartY=-36.4 StartZ=0 EndX=-20.6 EndY=-1.8 EndZ=0
    g23: LineSegment StartX=-23.6 StartY=-1.8 StartZ=0 EndX=-23.6 EndY=-36.4 EndZ=0
  constraints (48):
    c: Block(g0)
    c: Block(g1)
    c: Block(g2)
    c: Block(g3)
    c: Block(g4)
    c: Block(g5)
    c: Block(g6)
    c: Block(g7)
    c: Block(g8)
    c: Block(g9)
    c: Block(g10)
    c: Block(g11)
    c: Coincident(g12,g1)
    c: Coincident(g12,g2)
    c: Vertical(g12)
    c: Coincident(g13,g1)
    c: Coincident(g13,g2)
    c: Vertical(g13)
    c: Coincident(g14,g11)
    c: Coincident(g14,g7)
    c: Vertical(g14)
    c: Coincident(g15,g11)
    c: Coincident(g15,g7)
    c: Vertical(g15)
    c: Coincident(g16,g0)
    c: Coincident(g16,g3)
    c: Vertical(g16)
    c: Coincident(g17,g4)
    c: Coincident(g17,g8)
    c: Vertical(g17)
    c: Coincident(g18,g0)
    c: Coincident(g18,g3)
    c: Vertical(g18)
    c: Coincident(g19,g4)
    c: Coincident(g19,g8)
    c: Vertical(g19)
    c: Coincident(g20,g5)
    c: Coincident(g20,g9)
    c: Vertical(g20)
    c: Coincident(g21,g5)
    c: Coincident(g21,g9)
    c: Vertical(g21)
    c: Coincident(g22,g10)
    c: Coincident(g22,g6)
    c: Vertical(g22)
    c: Coincident(g23,g6)
    c: Coincident(g23,g10)
    c: Vertical(g23)
FEATURE [Part::Extrusion] Extrude039  label="removeToCreateFanGrillHoles002"
  Base = -> Sketch048
  Dir = (0,-1,6e-16)
  DirMode = 2
  FaceMakerClass = Part::FaceMakerBullseye
  LengthFwd = 10
  LengthRev = 0
  Placement = pos=(65.4,44,54.82) rot=(0,0,1;0rad)
  Solid = true
  Symmetric = false
FEATURE [Part::Cut] Cut027  label="fanScrewHousing004"
  Base = -> Cut026
  Tool = -> Extrude038
FEATURE [Part::Cut] Cut028  label="top014"
  Base = -> Fillet026
  Tool = -> Extrude039
FEATURE [Part::Feature] Face095 .. Face098  x4 (patterned run collapsed; names and placements below)
  shape: bbox 3.5 x 17.8 x 2e-07 mm, 1 faces, 0 solids (baked)
FEATURE [Part::Revolution] Revolve103  label="removeToCreateScrewAndThreadedInsertHole030"
  Angle = 360
  Axis = (0,1,0)
  Base = (0,0,0)
  FaceMakerClass = Part::FaceMakerBullseye
  Placement = pos=(62.3,30.3,19.7) rot=(0,0,1;0rad)
  Solid = false
  Source = -> Face095
  Symmetric = false
FEATURE [Part::Revolution] Revolve104  label="removeToCreateScrewAndThreadedInsertHole031"
  Angle = 360
  Axis = (0,1,0)
  Base = (0,0,0)
  FaceMakerClass = Part::FaceMakerBullseye
  Placement = pos=(62.3,30.3,51.7) rot=(0,0,1;0rad)
  Solid = false
  Source = -> Face096
  Symmetric = false
FEATURE [Part::Revolution] Revolve105  label="removeToCreateScrewAndThreadedInsertHole032"
  Angle = 360
  Axis = (0,1,0)
  Base = (0,0,0)
  FaceMakerClass = Part::FaceMakerBullseye
  Placement = pos=(30.3,30.3,19.7) rot=(0,0,1;0rad)
  Solid = false
  Source = -> Face097
  Symmetric = false
FEATURE [Part::Revolution] Revolve106  label="removeToCreateScrewAndThreadedInsertHole033"
  Angle = 360
  Axis = (0,1,0)
  Base = (0,0,0)
  FaceMakerClass = Part::FaceMakerBullseye
  Placement = pos=(30.3,30.3,51.7) rot=(0,0,1;0rad)
  Solid = false
  Source = -> Face098
  Symmetric = false
FEATURE [Part::MultiFuse] Fusion069  label="createThreadedInsertHolesForFan003"
  Shapes = -> [Revolve103,Revolve104,Revolve105,Revolve106]
FEATURE [Part::Cut] Cut029  label="top015"
  Base = -> Cut028
  Tool = -> Fusion054
FEATURE [Part::Cut] Cut030  label="fanScrewHousing005"
  Base = -> Cut027
  Tool = -> Fusion069
FEATURE [Part::Cylinder] Cylinder026  label="removeToCreteHoleForPlugHousing010"
  Angle = 360
  AttacherType = Attacher::AttachEngine3D
  Height = 20
  Placement = pos=(-2,19,36) rot=(0,1,0;1.5708rad)
  Radius = 14.3
FEATURE [Part::Box] Box018  label="removeToCreteHoleForPlugHousing011"
  AttacherType = Attacher::AttachEngine3D
  Height = 28.6
  Length = 10
  Placement = pos=(-2,0,21.7) rot=(0,0,1;0rad)
  Width = 19
FEATURE [Part::Box] Box019  label="wireHolderBottomCaseBit"
  AttacherType = Attacher::AttachEngine3D
  Height = 28
  Length = 3
  Placement = pos=(0,0,22) rot=(0,0,1;0rad)
  Width = 21
FEATURE [Part::Cylinder] Cylinder027  label="removeToCreteHoleForPlugHousing012"
  Angle = 360
  AttacherType = Attacher::AttachEngine3D
  Height = 20
  Placement = pos=(-2,19,36) rot=(0,1,0;1.5708rad)
  Radius = 14.3
FEATURE [Part::Cut] Cut031  label="wireHolderBottomCaseBit001"
  Base = -> Box019
  Tool = -> Cylinder027
FEATURE [Part::MultiFuse] Fusion070  label="removeToCreteHoleForPlugHousing013"
  Shapes = -> [Box018,Cylinder026]
FEATURE [Part::Cut] Cut032  label="top016"
  Base = -> Cut029
  Tool = -> Fusion070
FEATURE [Part::Cylinder] Cylinder028
  Angle = 360
  AttacherType = Attacher::AttachEngine3D
  Height = 20
  Placement = pos=(0,0,36.15) rot=(0,0,1;0rad)
  Radius = 14.3
FEATURE [Part::Cylinder] Cylinder029
  Angle = 360
  AttacherType = Attacher::AttachEngine3D
  Height = 10
  Placement = pos=(0,0,36.15) rot=(0,0,1;0rad)
  Radius = 4
FEATURE [Part::MultiFuse] Fusion071  label="removeToCreteHoleForPlugHousing014"
  Placement = pos=(70,19,36) rot=(0,1,0;1.5708rad)
  Shapes = -> [Cylinder028,Cylinder029]
FEATURE [Sketcher::SketchObject] Sketch049  label="topSketch011"
  FullyConstrained = true
  sketch-geometry (4):
    g0: ArcOfCircle CenterX=105 CenterY=19 CenterZ=0 NormalX=0 NormalY=0 NormalZ=1 AngleXU=0 Radius=20.6155 StartAngle=5.54125 EndAngle=6.28319
    g1: ArcOfCircle CenterX=105 CenterY=19 CenterZ=0 NormalX=0 NormalY=0 NormalZ=1 AngleXU=0 Radius=13 StartAngle=5.54125 EndAngle=6.28319
    g2: LineSegment StartX=118 StartY=19 StartZ=0 EndX=125.616 EndY=19 EndZ=0
    g3: LineSegment StartX=114.583 StartY=10.2157 StartZ=0 EndX=120.197 EndY=5.06982 EndZ=0
  constraints (7):
    c: Block(g0)
    c: Block(g1)
    c: Coincident(g2,g1)
    c: Coincident(g2,g0)
    c: Horizontal(g2)
    c: Coincident(g3,g1)
    c: Coincident(g3,g0)
FEATURE [Part::Box] Box020  label="removeToCreteHoleForPlugHousing015"
  AttacherType = Attacher::AttachEngine3D
  Height = 28.6
  Length = 20
  Placement = pos=(106.15,0,21.7) rot=(0,0,1;0rad)
  Width = 19
FEATURE [Part::MultiFuse] Fusion072  label="removeToCreteHoleForPlugHousing016"
  Shapes = -> [Box020,Fusion071]
FEATURE [Part::Cut] Cut033  label="removeToCreteHoleForPlugHousing017"
  Base = -> Cut032
  Tool = -> Fusion072
FEATURE [Part::Cylinder] Cylinder030
  Angle = 360
  AttacherType = Attacher::AttachEngine3D
  Height = 20
  Placement = pos=(0,0,36.15) rot=(0,0,1;0rad)
  Radius = 14.3
FEATURE [Part::Cylinder] Cylinder031
  Angle = 360
  AttacherType = Attacher::AttachEngine3D
  Height = 10
  Placement = pos=(0,0,36.15) rot=(0,0,1;0rad)
  Radius = 4
FEATURE [Part::Box] Box021  label="removeToCreteHoleForPlugHousing019"
  AttacherType = Attacher::AttachEngine3D
  Height = 28.6
  Length = 20
  Placement = pos=(106.15,0,21.7) rot=(0,0,1;0rad)
  Width = 19
FEATURE [Part::MultiFuse] Fusion074  label="removeToCreteHoleForPlugHousing020"
  Placement = pos=(70,19,36) rot=(0,1,0;1.5708rad)
  Shapes = -> [Cylinder030,Cylinder031]
FEATURE [Part::MultiFuse] Fusion073  label="removeToCreteHoleForPlugHousing018"
  Placement = pos=(0,0,28.3) rot=(0,0,1;0rad)
  Shapes = -> [Box021,Fusion074]
FEATURE [Part::Cylinder] Cylinder032
  Angle = 360
  AttacherType = Attacher::AttachEngine3D
  Height = 20
  Placement = pos=(0,0,36.15) rot=(0,0,1;0rad)
  Radius = 14.3
FEATURE [Part::Cylinder] Cylinder033
  Angle = 360
  AttacherType = Attacher::AttachEngine3D
  Height = 10
  Placement = pos=(0,0,36.15) rot=(0,0,1;0rad)
  Radius = 4
FEATURE [Part::Box] Box022  label="removeToCreteHoleForPlugHousing021"
  AttacherType = Attacher::AttachEngine3D
  Height = 28.6
  Length = 20
  Placement = pos=(106.15,0,21.7) rot=(0,0,1;0rad)
  Width = 19
FEATURE [Part::MultiFuse] Fusion076  label="removeToCreteHoleForPlugHousing023"
  Placement = pos=(70,19,36) rot=(0,1,0;1.5708rad)
  Shapes = -> [Cylinder032,Cylinder033]
FEATURE [Part::MultiFuse] Fusion075  label="removeToCreteHoleForPlugHousing022"
  Placement = pos=(0,0,-28.3) rot=(0,0,1;0rad)
  Shapes = -> [Box022,Fusion076]
FEATURE [Part::MultiFuse] Fusion077  label="removeToCreatePlugHousingBottomBit"
  Shapes = -> [Fusion075,Fusion073]
FEATURE [Part::Cylinder] Cylinder034
  Angle = 360
  AttacherType = Attacher::AttachEngine3D
  Height = 20
  Placement = pos=(0,0,36.15) rot=(0,0,1;0rad)
  Radius = 14
FEATURE [Part::Cylinder] Cylinder035
  Angle = 360
  AttacherType = Attacher::AttachEngine3D
  Height = 10
  Placement = pos=(0,0,36.15) rot=(0,0,1;0rad)
  Radius = 4
FEATURE [Part::MultiFuse] Fusion078  label="removeToCreteHoleForPlugHousing024"
  Placement = pos=(70,19,36) rot=(0,1,0;1.5708rad)
  Shapes = -> [Cylinder034,Cylinder035]
FEATURE [Part::MultiFuse] Fusion079  label="removeToCreatePlugHousingBottomBit001"
  Shapes = -> [Fusion078,Fusion077]
FEATURE [Part::Extrusion] Extrude040  label="bottomPlugHousingBit"
  Base = -> Sketch049
  Dir = (0,0,1)
  DirMode = 2
  FaceMakerClass = Part::FaceMakerBullseye
  LengthFwd = 72
  LengthRev = 0
  Solid = true
  Symmetric = false
FEATURE [Part::Cut] Cut034  label="bottomPlugHousingBit001"
  Base = -> Extrude040
  Placement = pos=(-0.09,0,0) rot=(0,0,1;0rad)
  Tool = -> Fusion079
FEATURE [Part::Box] Box023  label="Cube014"
  AttacherType = Attacher::AttachEngine3D
  Height = 16
  Length = 8
  Placement = pos=(12.7,31.52,28) rot=(0,0,1;0rad)
  Width = 4
FEATURE [Part::Cylinder] Cylinder036
  Angle = 360
  AttacherType = Attacher::AttachEngine3D
  Height = 10
  Placement = pos=(0,0,36.15) rot=(0,0,1;0rad)
  Radius = 4
FEATURE [Part::Cylinder] Cylinder037
  Angle = 360
  AttacherType = Attacher::AttachEngine3D
  Height = 20
  Placement = pos=(0,0,36.15) rot=(0,0,1;0rad)
  Radius = 8.2
FEATURE [Part::MultiFuse] Fusion080  label="removeToCreteHoleForPlugHousing025"
  Placement = pos=(-42,19,36) rot=(0,1,0;1.5708rad)
  Shapes = -> [Cylinder037,Cylinder036]
FEATURE [Sketcher::SketchObject] Sketch050  label="topSketch012"
  FullyConstrained = true
  sketch-geometry (4):
    g0: LineSegment StartX=16.8446 StartY=31.512 StartZ=0 EndX=16.3251 EndY=34.4666 EndZ=0
    g1: ArcOfCircle CenterX=19 CenterY=19.2524 CenterZ=0 NormalX=0 NormalY=0 NormalZ=1 AngleXU=0 Radius=15.4476 StartAngle=1.74483 EndAngle=2.72717
    g2: ArcOfCircle CenterX=19 CenterY=19.2524 CenterZ=0 NormalX=0 NormalY=0 NormalZ=1 AngleXU=0 Radius=12.4476 StartAngle=1.74483 EndAngle=2.73189
    g3: LineSegment StartX=4.86004 StartY=25.4725 StartZ=0 EndX=7.58253 EndY=24.2107 EndZ=0
  constraints (7):
    c: Block(g0)
    c: Coincident(g1,g0)
    c: Coincident(g2,g0)
    c: Coincident(g3,g1)
    c: Coincident(g3,g2)
    c: Block(g1)
    c: Block(g2)
FEATURE [Part::Extrusion] Extrude041
  Base = -> Sketch050
  Dir = (0,0,1)
  DirMode = 2
  FaceMakerClass = Part::FaceMakerBullseye
  LengthFwd = 10.6
  LengthRev = 0
  Placement = pos=(0,0,31) rot=(0,0,1;0rad)
  Solid = true
  Symmetric = false
FEATURE [Part::Cut] Cut035
  Base = -> Extrude041
  Placement = pos=(0,0,-0.3) rot=(0,0,1;0rad)
  Tool = -> Fusion080
FEATURE [Part::Cut] Cut036
  Base = -> Box023
  Tool = -> Cut035
FEATURE [Part::Fillet] Fillet027
  Base = -> Cut036
  Edges = 1 edges r=0.7: [Edge13]
FEATURE [Part::Fillet] Fillet028
  Base = -> Fillet027
  Edges = 1 edges r=0.7: [Edge13]
FEATURE [Part::Fillet] Fillet029
  Base = -> Fillet028
  Edges = 1 edges r=0.7: [Edge16]
FEATURE [Part::Fillet] Fillet030
  Base = -> Fillet029
  Edges = 1 edges r=0.7: [Edge11]
FEATURE [Part::Fillet] Fillet031
  Base = -> Fillet030
  Edges = 1 edges r=0.7: [Edge10]
FEATURE [Part::Fillet] Fillet032
  Base = -> Fillet031
  Edges = 1 edges r=1.2: [Edge5]
FEATURE [Part::Fillet] Fillet033
  Base = -> Fillet032
  Edges = 1 edges r=1.2: [Edge12]
FEATURE [Part::Fillet] Fillet034  label="wireHousingRetainer"
  Base = -> Fillet033
  Edges = 1 edges r=2: [Edge1]
  Placement = pos=(0.3,0,0) rot=(0,0,1;0rad)
FEATURE [Part::Feature] Face099
  shape: bbox 3.5 x 17.8 x 2e-07 mm, 1 faces, 0 solids (baked)
FEATURE [Part::Revolution] Revolve107  label="removeToCreateScrewAndThreadedInsertHole034"
  Angle = 360
  Axis = (0,1,0)
  Base = (0,0,0)
  FaceMakerClass = Part::FaceMakerBullseye
  Placement = pos=(12.5,0,10) rot=(0,0,1;0rad)
  Solid = false
  Source = -> Face099
  Symmetric = false
FEATURE [Part::Feature] Face100
  shape: bbox 3.5 x 17.8 x 2e-07 mm, 1 faces, 0 solids (baked)
FEATURE [Part::Revolution] Revolve108  label="removeToCreateScrewAndThreadedInsertHole035"
  Angle = 360
  Axis = (0,1,0)
  Base = (0,0,0)
  FaceMakerClass = Part::FaceMakerBullseye
  Placement = pos=(12.5,0,62) rot=(0,0,1;0rad)
  Solid = false
  Source = -> Face100
  Symmetric = false
FEATURE [Part::Feature] Face101
  shape: bbox 3.5 x 17.8 x 2e-07 mm, 1 faces, 0 solids (baked)
FEATURE [Part::Revolution] Revolve109  label="removeToCreateScrewAndThreadedInsertHole036"
  Angle = 360
  Axis = (0,1,0)
  Base = (0,0,0)
  FaceMakerClass = Part::FaceMakerBullseye
  Placement = pos=(89.5,0,68.5) rot=(0,0,1;0rad)
  Solid = false
  Source = -> Face101
  Symmetric = false
FEATURE [Part::Feature] Face102
  shape: bbox 3.5 x 17.8 x 2e-07 mm, 1 faces, 0 solids (baked)
FEATURE [Part::Revolution] Revolve110  label="removeToCreateScrewAndThreadedInsertHole037"
  Angle = 360
  Axis = (0,1,0)
  Base = (0,0,0)
  FaceMakerClass = Part::FaceMakerBullseye
  Placement = pos=(89.5,0,3.5) rot=(0,0,1;0rad)
  Solid = false
  Source = -> Face102
  Symmetric = false
FEATURE [Part::Feature] Face103
  shape: bbox 3.5 x 17.8 x 2e-07 mm, 1 faces, 0 solids (baked)
FEATURE [Part::Revolution] Revolve111  label="removeToCreateScrewAndThreadedInsertHole038"
  Angle = 360
  Axis = (0,1,0)
  Base = (0,0,0)
  FaceMakerClass = Part::FaceMakerBullseye
  Placement = pos=(109.5,4.7,3.5) rot=(0,0,1;0rad)
  Solid = false
  Source = -> Face103
  Symmetric = false
FEATURE [Part::Feature] Face104
  shape: bbox 3.5 x 17.8 x 2e-07 mm, 1 faces, 0 solids (baked)
FEATURE [Part::Revolution] Revolve112  label="removeToCreateScrewAndThreadedInsertHole039"
  Angle = 360
  Axis = (0,1,0)
  Base = (0,0,0)
  FaceMakerClass = Part::FaceMakerBullseye
  Placement = pos=(109.5,4.7,68.5) rot=(0,0,1;0rad)
  Solid = false
  Source = -> Face104
  Symmetric = false
FEATURE [Part::MultiFuse] Fusion081  label="removeToCreateScrewAndThreadedInsertHole040"
  Shapes = -> [Revolve107,Revolve108,Revolve109,Revolve110,Revolve111,Revolve112]
FEATURE [Part::MultiFuse] Fusion082  label="casePillars002"
  Shapes = -> [Revolve094,Revolve092,Revolve090,Revolve089,Revolve091,Revolve093]
FEATURE [Part::Cut] Cut037  label="casePillars003"
  Base = -> Fusion082
  Tool = -> Fusion081
FEATURE [Sketcher::SketchObject] Sketch051
  FullyConstrained = true
  Placement = pos=(117,19,0) rot=(0.57735,0.57735,0.57735;2.0944rad)
  sketch-geometry (48):
    g0: LineSegment StartX=-49.19 StartY=69.25 StartZ=0 EndX=-49.19 EndY=66.25 EndZ=0
    g1: LineSegment StartX=-49.19 StartY=63.5 StartZ=0 EndX=-49.19 EndY=60.5 EndZ=0
    g2: LineSegment StartX=-49.19 StartY=57.75 StartZ=0 EndX=-49.19 EndY=54.75 EndZ=0
    g3: LineSegment StartX=-49.19 StartY=52 StartZ=0 EndX=-49.19 EndY=49 EndZ=0
    g4: LineSegment StartX=-49.19 StartY=46.25 StartZ=0 EndX=-49.19 EndY=43.25 EndZ=0
    g5: LineSegment StartX=-49.19 StartY=40.5 StartZ=0 EndX=-49.19 EndY=37.5 EndZ=0
    g6: LineSegment StartX=-49.19 StartY=34.5 StartZ=0 EndX=-49.19 EndY=31.5 EndZ=0
    g7: LineSegment StartX=-49.19 StartY=28.75 StartZ=0 EndX=-49.19 EndY=25.75 EndZ=0
    g8: LineSegment StartX=-49.19 StartY=23 StartZ=0 EndX=-49.19 EndY=20 EndZ=0
    g9: LineSegment StartX=-49.19 StartY=17.25 StartZ=0 EndX=-49.19 EndY=14.25 EndZ=0
    g10: LineSegment StartX=-49.19 StartY=11.5 StartZ=0 EndX=-49.19 EndY=8.5 EndZ=0
    g11: LineSegment StartX=-49.19 StartY=5.75 StartZ=0 EndX=-49.19 EndY=2.75 EndZ=0
    g12: ArcOfCircle CenterX=-1.5 CenterY=67.75 CenterZ=0 NormalX=0 NormalY=0 NormalZ=1 AngleXU=0 Radius=1.5 StartAngle=4.71239 EndAngle=7.85398
    g13: ArcOfCircle CenterX=-1.5 CenterY=62 CenterZ=0 NormalX=0 NormalY=0 NormalZ=1 AngleXU=0 Radius=1.5 StartAngle=4.71239 EndAngle=7.85398
    g14: ArcOfCircle CenterX=-1.5 CenterY=56.25 CenterZ=0 NormalX=0 NormalY=0 NormalZ=1 AngleXU=0 Radius=1.5 StartAngle=4.71239 EndAngle=7.85398
    g15: ArcOfCircle CenterX=-11.49 CenterY=50.5 CenterZ=0 NormalX=0 NormalY=0 NormalZ=1 AngleXU=0 Radius=1.5 StartAngle=4.71239 EndAngle=7.85398
    g16: ArcOfCircle CenterX=-16.28 CenterY=44.75 CenterZ=0 NormalX=0 NormalY=0 NormalZ=1 AngleXU=0 Radius=1.5 StartAngle=4.71239 EndAngle=7.85398
    g17: ArcOfCircle CenterX=-18.2337 CenterY=39 CenterZ=0 NormalX=0 NormalY=0 NormalZ=1 AngleXU=0 Radius=1.5 StartAngle=4.71485 EndAngle=7.85398
    g18: ArcOfCircle CenterX=-16.2837 CenterY=27.25 CenterZ=0 NormalX=0 NormalY=0 NormalZ=1 AngleXU=0 Radius=1.5 StartAngle=4.71485 EndAngle=7.85398
    g19: ArcOfCircle CenterX=-18.2337 CenterY=33 CenterZ=0 NormalX=0 NormalY=0 NormalZ=1 AngleXU=0 Radius=1.5 StartAngle=4.71485 EndAngle=7.85398
    g20: ArcOfCircle CenterX=-11.49 CenterY=21.5 CenterZ=0 NormalX=0 NormalY=0 NormalZ=1 AngleXU=0 Radius=1.5 StartAngle=4.71239 EndAngle=7.85398
    g21: ArcOfCircle CenterX=-1.5 CenterY=4.25 CenterZ=0 NormalX=0 NormalY=0 NormalZ=1 AngleXU=0 Radius=1.5 StartAngle=4.71239 EndAngle=7.85398
    g22: ArcOfCircle CenterX=-1.5 CenterY=10 CenterZ=0 NormalX=0 NormalY=0 NormalZ=1 AngleXU=0 Radius=1.5 StartAngle=4.71239 EndAngle=7.85398
    g23: ArcOfCircle CenterX=-1.5 CenterY=15.75 CenterZ=0 NormalX=0 NormalY=0 NormalZ=1 AngleXU=0 Radius=1.5 StartAngle=4.71239 EndAngle=7.85398
    g24: LineSegment StartX=-49.19 StartY=69.25 StartZ=0 EndX=-1.5 EndY=69.25 EndZ=0
    g25: LineSegment StartX=-49.19 StartY=66.25 StartZ=0 EndX=-1.5 EndY=66.25 EndZ=0
    g26: LineSegment StartX=-49.19 StartY=63.5 StartZ=0 EndX=-1.5 EndY=63.5 EndZ=0
    g27: LineSegment StartX=-49.19 StartY=60.5 StartZ=0 EndX=-1.5 EndY=60.5 EndZ=0
    g28: LineSegment StartX=-49.19 StartY=57.75 StartZ=0 EndX=-1.5 EndY=57.75 EndZ=0
    g29: LineSegment StartX=-49.19 StartY=54.75 StartZ=0 EndX=-1.5 EndY=54.75 EndZ=0
    g30: LineSegment StartX=-49.19 StartY=52 StartZ=0 EndX=-11.49 EndY=52 EndZ=0
    g31: LineSegment StartX=-49.19 StartY=49 StartZ=0 EndX=-11.49 EndY=49 EndZ=0
    g32: LineSegment StartX=-49.19 StartY=46.25 StartZ=0 EndX=-16.28 EndY=46.25 EndZ=0
    g33: LineSegment StartX=-49.19 StartY=43.25 StartZ=0 EndX=-16.28 EndY=43.25 EndZ=0
    g34: LineSegment StartX=-49.19 StartY=40.5 StartZ=0 EndX=-18.2337 EndY=40.5 EndZ=0
    g35: LineSegment StartX=-49.19 StartY=37.5 StartZ=0 EndX=-18.23 EndY=37.5 EndZ=0
    g36: LineSegment StartX=-49.19 StartY=34.5 StartZ=0 EndX=-18.2337 EndY=34.5 EndZ=0
    g37: LineSegment StartX=-49.19 StartY=31.5 StartZ=0 EndX=-18.23 EndY=31.5 EndZ=0
    g38: LineSegment StartX=-49.19 StartY=28.75 StartZ=0 EndX=-16.2837 EndY=28.75 EndZ=0
    g39: LineSegment StartX=-49.19 StartY=25.75 StartZ=0 EndX=-16.28 EndY=25.75 EndZ=0
    g40: LineSegment StartX=-49.19 StartY=23 StartZ=0 EndX=-11.49 EndY=23 EndZ=0
    g41: LineSegment StartX=-49.19 StartY=20 StartZ=0 EndX=-11.49 EndY=20 EndZ=0
    g42: LineSegment StartX=-49.19 StartY=17.25 StartZ=0 EndX=-1.5 EndY=17.25 EndZ=0
    g43: LineSegment StartX=-49.19 StartY=14.25 StartZ=0 EndX=-1.5 EndY=14.25 EndZ=0
    g44: LineSegment StartX=-49.19 StartY=11.5 StartZ=0 EndX=-1.5 EndY=11.5 EndZ=0
    g45: LineSegment StartX=-49.19 StartY=8.5 StartZ=0 EndX=-1.5 EndY=8.5 EndZ=0
    g46: LineSegment StartX=-49.19 StartY=5.75 StartZ=0 EndX=-1.5 EndY=5.75 EndZ=0
    g47: LineSegment StartX=-49.19 StartY=2.75 StartZ=0 EndX=-1.5 EndY=2.75 EndZ=0
  constraints (120):
    c: Vertical(g0)
    c: Distance(g0) = 3
    c: Block(g0)
    c: Vertical(g1)
    c: Distance(g1) = 3
    c: Vertical(g2)
    c: Equal(g0,g2) = 3
    c: Block(g2)
    c: Vertical(g3)
    c: Equal(g1,g3) = 3
    c: Vertical(g4)
    c: Equal(g0,g4) = 3
    c: Block(g4)
    c: Vertical(g5)
    c: Equal(g1,g5) = 3
    c: Vertical(g6)
    c: Equal(g0,g6) = 3
    c: Block(g6)
    c: Vertical(g7)
    c: Equal(g1,g7) = 3
    c: Vertical(g8)
    c: Equal(g0,g8) = 3
    c: Block(g8)
    c: Vertical(g9)
    c: Equal(g1,g9) = 3
    c: Vertical(g10)
    c: Equal(g0,g10) = 3
    c: Block(g10)
    c: Vertical(g11)
    c: Equal(g1,g11) = 3
    c: Block(g12)
    c: Block(g13)
    c: Block(g14)
    c: Block(g15)
    c: Block(g16)
    c: Block(g17)
    c: Block(g18)
    c: Block(g19)
    c: Block(g20)
    c: Block(g21)
    c: Block(g22)
    c: Block(g23)
    c: Block(g11)
    c: Block(g9)
    c: Block(g7)
    c: Block(g5)
    c: Block(g3)
    c: Block(g1)
    c: Coincident(g24,g0)
    c: Coincident(g24,g12)
    c: Horizontal(g24)
    c: Coincident(g25,g0)
    c: Coincident(g25,g12)
    c: Horizontal(g25)
    c: Coincident(g26,g1)
    c: Coincident(g26,g13)
    c: Horizontal(g26)
    c: Coincident(g27,g1)
    c: Coincident(g27,g13)
    c: Horizontal(g27)
    c: Coincident(g28,g2)
    c: Coincident(g28,g14)
    c: Horizontal(g28)
    c: Coincident(g29,g2)
    c: Coincident(g29,g14)
    c: Horizontal(g29)
    c: Coincident(g30,g3)
    c: Coincident(g30,g15)
    c: Horizontal(g30)
    c: Coincident(g31,g3)
    c: Coincident(g31,g15)
    c: Horizontal(g31)
    c: Coincident(g32,g4)
    c: Coincident(g32,g16)
    c: Horizontal(g32)
    c: Coincident(g33,g4)
    c: Coincident(g33,g16)
    c: Horizontal(g33)
    c: Coincident(g34,g5)
    c: Coincident(g34,g17)
    c: Horizontal(g34)
    c: Coincident(g35,g5)
    c: Coincident(g35,g17)
    c: Horizontal(g35)
    c: Coincident(g36,g6)
    c: Coincident(g36,g19)
    c: Horizontal(g36)
    c: Coincident(g37,g6)
    c: Coincident(g37,g19)
    c: Horizontal(g37)
    c: Coincident(g38,g7)
    c: Coincident(g38,g18)
    c: Horizontal(g38)
    c: Coincident(g39,g7)
    c: Coincident(g39,g18)
    c: Horizontal(g39)
    c: Coincident(g40,g8)
    c: Coincident(g40,g20)
    c: Horizontal(g40)
    c: Coincident(g41,g8)
    c: Coincident(g41,g20)
    c: Horizontal(g41)
    c: Coincident(g42,g9)
    c: Coincident(g42,g23)
    c: Horizontal(g42)
    c: Coincident(g43,g9)
    c: Coincident(g43,g23)
    c: Horizontal(g43)
    c: Coincident(g44,g10)
    c: Coincident(g44,g22)
    c: Horizontal(g44)
    c: Coincident(g45,g10)
    c: Coincident(g45,g22)
    c: Horizontal(g45)
    c: Coincident(g46,g11)
    c: Coincident(g46,g21)
    c: Horizontal(g46)
    c: Coincident(g47,g11)
    c: Coincident(g47,g21)
    c: Horizontal(g47)
FEATURE [Part::Extrusion] Extrude042
  Base = -> Sketch051
  Dir = (1,-2e-16,2e-16)
  DirMode = 2
  FaceMakerClass = Part::FaceMakerBullseye
  LengthFwd = 19
  LengthRev = 0
  Placement = pos=(-19,0,0) rot=(0,0,1;0rad)
  Solid = true
  Symmetric = false
FEATURE [Part::Fillet] Fillet035  label="removeToCreateVentalationHoles"
  Base = -> Extrude042
  Edges = <same value as first occurrence — deduplicated (x6 in doc)>
  Placement = pos=(7,0,0) rot=(0,0,1;0rad)
FEATURE [Part::Cut] Cut038  label="top017"
  Base = -> Cut033
  Tool = -> Fillet035
FEATURE [Sketcher::SketchObject] Sketch052  label="bottomSketch001"
  FullyConstrained = true
  sketch-geometry (45):
    g0: LineSegment StartX=6.29999 StartY=8 StartZ=0 EndX=3.29999 EndY=8 EndZ=0
    g1: LineSegment StartX=3.29999 StartY=8 StartZ=0 EndX=3.29999 EndY=-6.03275e-07 EndZ=0
    g2: ArcOfCircle CenterX=8.29999 CenterY=5 CenterZ=0 NormalX=0 NormalY=0 NormalZ=1 AngleXU=0 Radius=2 StartAngle=3.14159 EndAngle=4.71239
    g3: LineSegment StartX=6.29999 StartY=8 StartZ=0 EndX=6.29999 EndY=5 EndZ=0
    g4: ArcOfCircle CenterX=105 CenterY=19 CenterZ=0 NormalX=0 NormalY=0 NormalZ=1 AngleXU=0 Radius=12.7 StartAngle=4.71239 EndAngle=5.94289
    g5-g11: Circle x7 (B-spline internal-alignment scaffolding for g12; pole/knot coordinates omitted)
    g12: BSplineCurve PolesCount=7 KnotsCount=5 Degree=3 IsPeriodic=0
    g13-g17: GeomPoint x5 (B-spline internal-alignment scaffolding for g12; pole/knot coordinates omitted)
    g18: ArcOfCircle CenterX=105 CenterY=19 CenterZ=0 NormalX=0 NormalY=0 NormalZ=1 AngleXU=0 Radius=15.7 StartAngle=5.81226 EndAngle=6.28319
    g19: BSplineCurve PolesCount=5 KnotsCount=3 Degree=3 IsPeriodic=0
    g20: LineSegment StartX=8.29999 StartY=3 StartZ=0 EndX=101.7 EndY=3 EndZ=0
    g21: LineSegment StartX=3.29999 StartY=-6.03275e-07 StartZ=0 EndX=105 EndY=-6.03275e-07 EndZ=0
    g22: LineSegment StartX=120.974 StartY=8.71251 StartZ=0 EndX=122.332 EndY=7.83778 EndZ=0
    g23: LineSegment StartX=105 StartY=-6.03274e-07 StartZ=0 EndX=113 EndY=-6.03274e-07 EndZ=0
    g24: ArcOfCircle CenterX=105 CenterY=19 CenterZ=0 NormalX=0 NormalY=0 NormalZ=1 AngleXU=0 Radius=20.6155 StartAngle=5.11091 EndAngle=5.71103
    g25: ArcOfCircle CenterX=117.7 CenterY=19 CenterZ=0 NormalX=0 NormalY=0 NormalZ=1 AngleXU=0 Radius=3 StartAngle=1.2e-15 EndAngle=2.10468
    g26: Circle CenterX=116.345 CenterY=16.3232 CenterZ=0 NormalX=0 NormalY=0 NormalZ=1 AngleXU=0 Radius=1
    g27: Circle CenterX=117.24 CenterY=15.7584 CenterZ=0 NormalX=0 NormalY=0 NormalZ=1 AngleXU=0 Radius=1
    g28: Circle CenterX=116.972 CenterY=14.7612 CenterZ=0 NormalX=0 NormalY=0 NormalZ=1 AngleXU=0 Radius=1
    g29: BSplineCurve PolesCount=3 KnotsCount=2 Degree=2 IsPeriodic=0
    g30: GeomPoint X=116.345 Y=16.3232 Z=0
    g31: GeomPoint X=116.972 Y=14.7612 Z=0
    g32: Circle CenterX=115.828 CenterY=17.157 CenterZ=0 NormalX=0 NormalY=0 NormalZ=1 AngleXU=0 Radius=1
    g33: Circle CenterX=115.841 CenterY=16.639 CenterZ=0 NormalX=0 NormalY=0 NormalZ=1 AngleXU=0 Radius=1
    g34: Circle CenterX=116.345 CenterY=16.3232 CenterZ=0 NormalX=0 NormalY=0 NormalZ=1 AngleXU=0 Radius=1
    g35: BSplineCurve PolesCount=3 KnotsCount=2 Degree=2 IsPeriodic=0
    g36: GeomPoint X=115.828 Y=17.157 Z=0
    g37: GeomPoint X=116.345 Y=16.3232 Z=0
    g38: LineSegment StartX=115.828 StartY=17.157 StartZ=0 EndX=115.828 EndY=20.8307 EndZ=0
    g39: Circle CenterX=115.828 CenterY=20.8307 CenterZ=0 NormalX=0 NormalY=0 NormalZ=1 AngleXU=0 Radius=1
    g40: Circle CenterX=115.831 CenterY=21.3396 CenterZ=0 NormalX=0 NormalY=0 NormalZ=1 AngleXU=0 Radius=1
    g41: Circle CenterX=116.173 CenterY=21.5825 CenterZ=0 NormalX=0 NormalY=0 NormalZ=1 AngleXU=0 Radius=1
    g42: BSplineCurve PolesCount=3 KnotsCount=2 Degree=2 IsPeriodic=0
    g43: GeomPoint X=115.828 Y=20.8307 Z=0
    g44: GeomPoint X=116.173 Y=21.5825 Z=0
  constraints (70):
    c: Horizontal(g0)
    c: Distance(g0) = 3
    c: Coincident(g1,g0)
    c: Vertical(g1)
    c: Block(g2)
    c: Block(g0)
    c: Coincident(g3,g0)
    c: Coincident(g3,g2)
    c: Vertical(g3)
    c: Block(g1)
    c: Block(g4)
    c: Coincident(g19,g4)
    c: Block(g19)
    c: Equal(g5, g6-g11) x6
    c: InternalAlignment(g5-g11 -> g12) x7
    c: InternalAlignment(g13-g17 -> g12) x5
    c: Block(g12)
    c: Coincident(g18,g12)
    c: Block(g18)
    c: Coincident(g20,g2)
    c: Coincident(g20,g19)
    c: Horizontal(g20)
    c: Distance(g20) = 93.4
    c: Coincident(g21,g1)
    c: Horizontal(g21)
    c: Distance(g21) = 101.7
    c: Horizontal(g23)
    c: Distance(g23) = 8
    c: Coincident(g24,g23)
    c: Block(g23)
    c: Coincident(g22,g24)
    c: Block(g24)
    c: Block(g22)
    c: Distance(g22) = 1.61553
    c: Coincident(g25,g18)
    c: Block(g25)
    c: Weight(g26) = 1
    c: Equal(g26,g27)
    c: Equal(g26,g28)
    c: Coincident(g29,g4)
    c: InternalAlignment(g26,g29)
    c: InternalAlignment(g27,g29)
    c: InternalAlignment(g28,g29)
    c: InternalAlignment(g30,g29)
    c: InternalAlignment(g31,g29)
    c: Block(g29)
    c: Weight(g32) = 1
    c: Equal(g32,g33)
    c: Equal(g32,g34)
    c: Coincident(g35,g29)
    c: InternalAlignment(g32,g35)
    c: InternalAlignment(g33,g35)
    c: InternalAlignment(g34,g35)
    c: InternalAlignment(g36,g35)
    c: InternalAlignment(g37,g35)
    c: Block(g35)
    c: Coincident(g38,g35)
    c: Vertical(g38)
    c: Block(g38)
    c: Coincident(g42,g38)
    c: Weight(g39) = 1
    c: Equal(g39,g40)
    c: Equal(g39,g41)
    c: Coincident(g42,g25)
    c: InternalAlignment(g39,g42)
    c: InternalAlignment(g40,g42)
    c: InternalAlignment(g41,g42)
    c: InternalAlignment(g43,g42)
    c: InternalAlignment(g44,g42)
    c: Block(g42)
FEATURE [Part::Extrusion] Extrude043  label="bottom010"
  Base = -> Sketch052
  Dir = (0,0,1)
  DirMode = 2
  FaceMakerClass = Part::FaceMakerBullseye
  LengthFwd = 71.4
  LengthRev = 0
  Placement = pos=(0,0,0.3) rot=(0,0,1;0rad)
  Solid = true
  Symmetric = false
FEATURE [Sketcher::SketchObject] Sketch053  label="topSketch013"
  FullyConstrained = true
  sketch-geometry (22):
    g0: LineSegment StartX=5.21097e-06 StartY=3 StartZ=0 EndX=5.21097e-06 EndY=19 EndZ=0
    g1: ArcOfCircle CenterX=19 CenterY=19 CenterZ=0 NormalX=0 NormalY=0 NormalZ=1 AngleXU=0 Radius=19 StartAngle=1.5708 EndAngle=3.14159
    g2: ArcOfCircle CenterX=19 CenterY=19 CenterZ=0 NormalX=0 NormalY=0 NormalZ=1 AngleXU=0 Radius=16 StartAngle=1.5708 EndAngle=3.14159
    g3: LineSegment StartX=114 StartY=35 StartZ=0 EndX=19 EndY=35 EndZ=0
    g4: LineSegment StartX=5.21097e-06 StartY=3 StartZ=0 EndX=5.21097e-06 EndY=0 EndZ=0
    g5: LineSegment StartX=3 StartY=0 StartZ=0 EndX=5.21097e-06 EndY=0 EndZ=0
    g6: LineSegment StartX=3 StartY=19 StartZ=0 EndX=3 EndY=0 EndZ=0
    g7: LineSegment StartX=19 StartY=38 StartZ=0 EndX=124 EndY=38 EndZ=0
    g8: Circle CenterX=119 CenterY=35 CenterZ=0 NormalX=0 NormalY=0 NormalZ=1 AngleXU=0 Radius=1
    g9: Circle CenterX=121 CenterY=35 CenterZ=0 NormalX=0 NormalY=0 NormalZ=1 AngleXU=0 Radius=1
    g10: Circle CenterX=121 CenterY=33 CenterZ=0 NormalX=0 NormalY=0 NormalZ=1 AngleXU=0 Radius=1
    g11: BSplineCurve PolesCount=3 KnotsCount=2 Degree=2 IsPeriodic=0
    g12: GeomPoint X=119 Y=35 Z=0
    g13: GeomPoint X=121 Y=33 Z=0
    g14: LineSegment StartX=119 StartY=35 StartZ=0 EndX=114 EndY=35 EndZ=0
    g15: ArcOfCircle CenterX=105 CenterY=19 CenterZ=0 NormalX=0 NormalY=0 NormalZ=1 AngleXU=0 Radius=16 StartAngle=5.60905 EndAngle=6.28319
    g16: LineSegment StartX=121 StartY=33 StartZ=0 EndX=121 EndY=19 EndZ=0
    g17: LineSegment StartX=117.5 StartY=9.01251 StartZ=0 EndX=121.163 EndY=9.0125 EndZ=0
    g18: ArcOfCircle CenterX=105 CenterY=19 CenterZ=0 NormalX=0 NormalY=0 NormalZ=1 AngleXU=0 Radius=20.6155 StartAngle=5.7297 EndAngle=6.28319
    g19: LineSegment StartX=121.163 StartY=9.0125 StartZ=0 EndX=122.538 EndY=8.16329 EndZ=0
    g20: LineSegment StartX=124 StartY=38 StartZ=0 EndX=125.616 EndY=38 EndZ=0
    g21: LineSegment StartX=125.616 StartY=19 StartZ=0 EndX=125.616 EndY=38 EndZ=0
  constraints (50):
    c: Vertical(g0)
    c: Block(g0)
    c: Coincident(g1,g0)
    c: Block(g1)
    c: Coincident(g2,g1)
    c: Block(g2)
    c: Coincident(g3,g2)
    c: Horizontal(g3)
    c: Tangent(g3,g2)
    c: Coincident(g4,g0)
    c: Distance(g4) = 3
    c: Vertical(g4)
    c: Coincident(g5,g4)
    c: Horizontal(g5)
    c: Coincident(g6,g2)
    c: Coincident(g6,g5)
    c: Vertical(g6)
    c: Horizontal(g7)
    c: Distance(g7) = 105
    c: Coincident(g7,g1)
    c: Block(g3)
    c: Weight(g8) = 1
    c: Equal(g8,g9)
    c: Equal(g8,g10)
    c: InternalAlignment(g8,g11)
    c: InternalAlignment(g9,g11)
    c: InternalAlignment(g10,g11)
    c: InternalAlignment(g12,g11)
    c: InternalAlignment(g13,g11)
    c: Block(g11)
    c: Coincident(g14,g11)
    c: Coincident(g14,g3)
    c: Horizontal(g14)
    c: Block(g15)
    c: Coincident(g16,g11)
    c: Coincident(g16,g15)
    c: Vertical(g16)
    c: Distance(g16) = 14
    c: Coincident(g17,g15)
    c: Block(g18)
    c: Coincident(g19,g18)
    c: Coincident(g20,g7)
    c: Horizontal(g20)
    c: Vertical(g21)
    c: Coincident(g20,g21)
    c: Block(g20)
    c: Block(g21)
    c: Block(g19)
    c: Block(g17)
    c: Distance(g20) = 1.61553
FEATURE [Part::Extrusion] Extrude044
  Base = -> Sketch053
  Dir = (0,0,1)
  DirMode = 2
  FaceMakerClass = Part::FaceMakerBullseye
  LengthFwd = 72
  LengthRev = 0
  Solid = true
  Symmetric = false
FEATURE [Part::Fillet] Fillet036  label="top018"
  Base = -> Extrude044
  Edges = 1 edges r=2: [Edge41]
FEATURE [Sketcher::SketchObject] Sketch054
  FullyConstrained = false
  Placement = pos=(0,0,0) rot=(1,0,0;1.5708rad)
  sketch-geometry (24):
    g0: ArcOfCircle CenterX=-4 CenterY=-10.5 CenterZ=0 NormalX=0 NormalY=0 NormalZ=1 AngleXU=0 Radius=1.5 StartAngle=6e-16 EndAngle=3.14159
    g1: ArcOfCircle CenterX=-34.2 CenterY=-10.5 CenterZ=0 NormalX=0 NormalY=0 NormalZ=1 AngleXU=0 Radius=1.5 StartAngle=0 EndAngle=3.14159
    g2: ArcOfCircle CenterX=-34.2 CenterY=-27.7 CenterZ=0 NormalX=0 NormalY=0 NormalZ=1 AngleXU=0 Radius=1.5 StartAngle=3.14159 EndAngle=6.28319
    g3: ArcOfCircle CenterX=-4 CenterY=-27.7 CenterZ=0 NormalX=0 NormalY=0 NormalZ=1 AngleXU=0 Radius=1.5 StartAngle=3.1416 EndAngle=6.28319
    g4: ArcOfCircle CenterX=-10 CenterY=-4.3 CenterZ=0 NormalX=0 NormalY=0 NormalZ=1 AngleXU=0 Radius=1.5 StartAngle=2e-16 EndAngle=3.14159
    g5: ArcOfCircle CenterX=-16.1 CenterY=-1.8 CenterZ=0 NormalX=0 NormalY=0 NormalZ=1 AngleXU=0 Radius=1.5 StartAngle=5e-16 EndAngle=3.14159
    g6: ArcOfCircle CenterX=-22.1 CenterY=-1.8 CenterZ=0 NormalX=0 NormalY=0 NormalZ=1 AngleXU=0 Radius=1.5 StartAngle=5e-16 EndAngle=3.14159
    g7: ArcOfCircle CenterX=-28.2 CenterY=-4.3 CenterZ=0 NormalX=0 NormalY=0 NormalZ=1 AngleXU=0 Radius=1.5 StartAngle=2e-16 EndAngle=3.14159
    g8: ArcOfCircle CenterX=-10 CenterY=-33.9 CenterZ=0 NormalX=0 NormalY=0 NormalZ=1 AngleXU=0 Radius=1.5 StartAngle=3.14159 EndAngle=6.28319
    g9: ArcOfCircle CenterX=-16.1 CenterY=-36.4 CenterZ=0 NormalX=0 NormalY=0 NormalZ=1 AngleXU=0 Radius=1.5 StartAngle=3.14159 EndAngle=6.28319
    g10: ArcOfCircle CenterX=-22.1 CenterY=-36.4 CenterZ=0 NormalX=0 NormalY=0 NormalZ=1 AngleXU=0 Radius=1.5 StartAngle=3.14159 EndAngle=6.28319
    g11: ArcOfCircle CenterX=-28.2 CenterY=-33.9 CenterZ=0 NormalX=0 NormalY=0 NormalZ=1 AngleXU=0 Radius=1.5 StartAngle=3.14159 EndAngle=6.28319
    g12: LineSegment StartX=-35.7 StartY=-10.5 StartZ=0 EndX=-35.7 EndY=-27.7 EndZ=0
    g13: LineSegment StartX=-32.7 StartY=-10.5 StartZ=0 EndX=-32.7 EndY=-27.7 EndZ=0
    g14: LineSegment StartX=-29.7 StartY=-33.9 StartZ=0 EndX=-29.7 EndY=-4.3 EndZ=0
    g15: LineSegment StartX=-26.7 StartY=-33.9 StartZ=0 EndX=-26.7 EndY=-4.3 EndZ=0
    g16: LineSegment StartX=-2.5 StartY=-10.5 StartZ=0 EndX=-2.5 EndY=-27.7 EndZ=0
    g17: LineSegment StartX=-8.5 StartY=-4.3 StartZ=0 EndX=-8.5 EndY=-33.9 EndZ=0
    g18: LineSegment StartX=-5.5 StartY=-10.5 StartZ=0 EndX=-5.5 EndY=-27.7 EndZ=0
    g19: LineSegment StartX=-11.5 StartY=-4.3 StartZ=0 EndX=-11.5 EndY=-33.9 EndZ=0
    g20: LineSegment StartX=-14.6 StartY=-1.8 StartZ=0 EndX=-14.6 EndY=-36.4 EndZ=0
    g21: LineSegment StartX=-17.6 StartY=-1.8 StartZ=0 EndX=-17.6 EndY=-36.4 EndZ=0
    g22: LineSegment StartX=-20.6 StartY=-36.4 StartZ=0 EndX=-20.6 EndY=-1.8 EndZ=0
    g23: LineSegment StartX=-23.6 StartY=-1.8 StartZ=0 EndX=-23.6 EndY=-36.4 EndZ=0
  constraints (48):
    c: Block(g0)
    c: Block(g1)
    c: Block(g2)
    c: Block(g3)
    c: Block(g4)
    c: Block(g5)
    c: Block(g6)
    c: Block(g7)
    c: Block(g8)
    c: Block(g9)
    c: Block(g10)
    c: Block(g11)
    c: Coincident(g12,g1)
    c: Coincident(g12,g2)
    c: Vertical(g12)
    c: Coincident(g13,g1)
    c: Coincident(g13,g2)
    c: Vertical(g13)
    c: Coincident(g14,g11)
    c: Coincident(g14,g7)
    c: Vertical(g14)
    c: Coincident(g15,g11)
    c: Coincident(g15,g7)
    c: Vertical(g15)
    c: Coincident(g16,g0)
    c: Coincident(g16,g3)
    c: Vertical(g16)
    c: Coincident(g17,g4)
    c: Coincident(g17,g8)
    c: Vertical(g17)
    c: Coincident(g18,g0)
    c: Coincident(g18,g3)
    c: Vertical(g18)
    c: Coincident(g19,g4)
    c: Coincident(g19,g8)
    c: Vertical(g19)
    c: Coincident(g20,g5)
    c: Coincident(g20,g9)
    c: Vertical(g20)
    c: Coincident(g21,g5)
    c: Coincident(g21,g9)
    c: Vertical(g21)
    c: Coincident(g22,g10)
    c: Coincident(g22,g6)
    c: Vertical(g22)
    c: Coincident(g23,g6)
    c: Coincident(g23,g10)
    c: Vertical(g23)
FEATURE [Part::Extrusion] Extrude045  label="removeToCreateFanGrillHoles003"
  Base = -> Sketch054
  Dir = (0,-1,6e-16)
  DirMode = 2
  FaceMakerClass = Part::FaceMakerBullseye
  LengthFwd = 10
  LengthRev = 0
  Placement = pos=(65.4,44,54.82) rot=(0,0,1;0rad)
  Solid = true
  Symmetric = false
FEATURE [Part::Feature] Face105 .. Face108  x4 (patterned run collapsed; names and placements below)
  shape: bbox 3.5 x 17.8 x 2e-07 mm, 1 faces, 0 solids (baked)
FEATURE [Part::Revolution] Revolve113  label="removeToCreateScrewAndThreadedInsertHole041"
  Angle = 360
  Axis = (0,1,0)
  Base = (0,0,0)
  FaceMakerClass = Part::FaceMakerBullseye
  Placement = pos=(62.3,30.3,19.7) rot=(0,0,1;0rad)
  Solid = false
  Source = -> Face105
  Symmetric = false
FEATURE [Part::Revolution] Revolve114  label="removeToCreateScrewAndThreadedInsertHole042"
  Angle = 360
  Axis = (0,1,0)
  Base = (0,0,0)
  FaceMakerClass = Part::FaceMakerBullseye
  Placement = pos=(62.3,30.3,51.7) rot=(0,0,1;0rad)
  Solid = false
  Source = -> Face106
  Symmetric = false
FEATURE [Part::Revolution] Revolve115  label="removeToCreateScrewAndThreadedInsertHole043"
  Angle = 360
  Axis = (0,1,0)
  Base = (0,0,0)
  FaceMakerClass = Part::FaceMakerBullseye
  Placement = pos=(30.3,30.3,19.7) rot=(0,0,1;0rad)
  Solid = false
  Source = -> Face107
  Symmetric = false
FEATURE [Part::Revolution] Revolve116  label="removeToCreateScrewAndThreadedInsertHole044"
  Angle = 360
  Axis = (0,1,0)
  Base = (0,0,0)
  FaceMakerClass = Part::FaceMakerBullseye
  Placement = pos=(30.3,30.3,51.7) rot=(0,0,1;0rad)
  Solid = false
  Source = -> Face108
  Symmetric = false
FEATURE [Part::MultiFuse] Fusion083  label="createThreadedInsertHolesForFan004"
  Shapes = -> [Revolve113,Revolve114,Revolve115,Revolve116]
FEATURE [Part::Box] Box024  label="removeToCreteHoleForPlugHousing026"
  AttacherType = Attacher::AttachEngine3D
  Height = 28.6
  Length = 10
  Placement = pos=(-2,0,21.7) rot=(0,0,1;0rad)
  Width = 19
FEATURE [Part::Cylinder] Cylinder038  label="removeToCreteHoleForPlugHousing027"
  Angle = 360
  AttacherType = Attacher::AttachEngine3D
  Height = 20
  Placement = pos=(-2,19,36) rot=(0,1,0;1.5708rad)
  Radius = 14.3
FEATURE [Part::MultiFuse] Fusion084  label="removeToCreteHoleForPlugHousing028"
  Shapes = -> [Box024,Cylinder038]
FEATURE [Part::Cylinder] Cylinder039
  Angle = 360
  AttacherType = Attacher::AttachEngine3D
  Height = 20
  Placement = pos=(0,0,36.15) rot=(0,0,1;0rad)
  Radius = 14.3
FEATURE [Part::Cylinder] Cylinder040
  Angle = 360
  AttacherType = Attacher::AttachEngine3D
  Height = 10
  Placement = pos=(0,0,36.15) rot=(0,0,1;0rad)
  Radius = 4
FEATURE [Part::Box] Box025  label="removeToCreteHoleForPlugHousing030"
  AttacherType = Attacher::AttachEngine3D
  Height = 28.6
  Length = 20
  Placement = pos=(106.15,0,21.7) rot=(0,0,1;0rad)
  Width = 19
FEATURE [Part::MultiFuse] Fusion086  label="removeToCreteHoleForPlugHousing031"
  Placement = pos=(70,19,36) rot=(0,1,0;1.5708rad)
  Shapes = -> [Cylinder039,Cylinder040]
FEATURE [Part::MultiFuse] Fusion085  label="removeToCreteHoleForPlugHousing029"
  Shapes = -> [Box025,Fusion086]
FEATURE [Sketcher::SketchObject] Sketch055
  FullyConstrained = true
  Placement = pos=(117,19,0) rot=(0.57735,0.57735,0.57735;2.0944rad)
  sketch-geometry (48):
    g0: LineSegment StartX=-49.19 StartY=69.25 StartZ=0 EndX=-49.19 EndY=66.25 EndZ=0
    g1: LineSegment StartX=-49.19 StartY=63.5 StartZ=0 EndX=-49.19 EndY=60.5 EndZ=0
    g2: LineSegment StartX=-49.19 StartY=57.75 StartZ=0 EndX=-49.19 EndY=54.75 EndZ=0
    g3: LineSegment StartX=-49.19 StartY=52 StartZ=0 EndX=-49.19 EndY=49 EndZ=0
    g4: LineSegment StartX=-49.19 StartY=46.25 StartZ=0 EndX=-49.19 EndY=43.25 EndZ=0
    g5: LineSegment StartX=-49.19 StartY=40.5 StartZ=0 EndX=-49.19 EndY=37.5 EndZ=0
    g6: LineSegment StartX=-49.19 StartY=34.5 StartZ=0 EndX=-49.19 EndY=31.5 EndZ=0
    g7: LineSegment StartX=-49.19 StartY=28.75 StartZ=0 EndX=-49.19 EndY=25.75 EndZ=0
    g8: LineSegment StartX=-49.19 StartY=23 StartZ=0 EndX=-49.19 EndY=20 EndZ=0
    g9: LineSegment StartX=-49.19 StartY=17.25 StartZ=0 EndX=-49.19 EndY=14.25 EndZ=0
    g10: LineSegment StartX=-49.19 StartY=11.5 StartZ=0 EndX=-49.19 EndY=8.5 EndZ=0
    g11: LineSegment StartX=-49.19 StartY=5.75 StartZ=0 EndX=-49.19 EndY=2.75 EndZ=0
    g12: ArcOfCircle CenterX=-1.5 CenterY=67.75 CenterZ=0 NormalX=0 NormalY=0 NormalZ=1 AngleXU=0 Radius=1.5 StartAngle=4.71239 EndAngle=7.85398
    g13: ArcOfCircle CenterX=-1.5 CenterY=62 CenterZ=0 NormalX=0 NormalY=0 NormalZ=1 AngleXU=0 Radius=1.5 StartAngle=4.71239 EndAngle=7.85398
    g14: ArcOfCircle CenterX=-1.5 CenterY=56.25 CenterZ=0 NormalX=0 NormalY=0 NormalZ=1 AngleXU=0 Radius=1.5 StartAngle=4.71239 EndAngle=7.85398
    g15: ArcOfCircle CenterX=-11.49 CenterY=50.5 CenterZ=0 NormalX=0 NormalY=0 NormalZ=1 AngleXU=0 Radius=1.5 StartAngle=4.71239 EndAngle=7.85398
    g16: ArcOfCircle CenterX=-16.28 CenterY=44.75 CenterZ=0 NormalX=0 NormalY=0 NormalZ=1 AngleXU=0 Radius=1.5 StartAngle=4.71239 EndAngle=7.85398
    g17: ArcOfCircle CenterX=-18.2337 CenterY=39 CenterZ=0 NormalX=0 NormalY=0 NormalZ=1 AngleXU=0 Radius=1.5 StartAngle=4.71485 EndAngle=7.85398
    g18: ArcOfCircle CenterX=-16.2837 CenterY=27.25 CenterZ=0 NormalX=0 NormalY=0 NormalZ=1 AngleXU=0 Radius=1.5 StartAngle=4.71485 EndAngle=7.85398
    g19: ArcOfCircle CenterX=-18.2337 CenterY=33 CenterZ=0 NormalX=0 NormalY=0 NormalZ=1 AngleXU=0 Radius=1.5 StartAngle=4.71485 EndAngle=7.85398
    g20: ArcOfCircle CenterX=-11.49 CenterY=21.5 CenterZ=0 NormalX=0 NormalY=0 NormalZ=1 AngleXU=0 Radius=1.5 StartAngle=4.71239 EndAngle=7.85398
    g21: ArcOfCircle CenterX=-1.5 CenterY=4.25 CenterZ=0 NormalX=0 NormalY=0 NormalZ=1 AngleXU=0 Radius=1.5 StartAngle=4.71239 EndAngle=7.85398
    g22: ArcOfCircle CenterX=-1.5 CenterY=10 CenterZ=0 NormalX=0 NormalY=0 NormalZ=1 AngleXU=0 Radius=1.5 StartAngle=4.71239 EndAngle=7.85398
    g23: ArcOfCircle CenterX=-1.5 CenterY=15.75 CenterZ=0 NormalX=0 NormalY=0 NormalZ=1 AngleXU=0 Radius=1.5 StartAngle=4.71239 EndAngle=7.85398
    g24: LineSegment StartX=-49.19 StartY=69.25 StartZ=0 EndX=-1.5 EndY=69.25 EndZ=0
    g25: LineSegment StartX=-49.19 StartY=66.25 StartZ=0 EndX=-1.5 EndY=66.25 EndZ=0
    g26: LineSegment StartX=-49.19 StartY=63.5 StartZ=0 EndX=-1.5 EndY=63.5 EndZ=0
    g27: LineSegment StartX=-49.19 StartY=60.5 StartZ=0 EndX=-1.5 EndY=60.5 EndZ=0
    g28: LineSegment StartX=-49.19 StartY=57.75 StartZ=0 EndX=-1.5 EndY=57.75 EndZ=0
    g29: LineSegment StartX=-49.19 StartY=54.75 StartZ=0 EndX=-1.5 EndY=54.75 EndZ=0
    g30: LineSegment StartX=-49.19 StartY=52 StartZ=0 EndX=-11.49 EndY=52 EndZ=0
    g31: LineSegment StartX=-49.19 StartY=49 StartZ=0 EndX=-11.49 EndY=49 EndZ=0
    g32: LineSegment StartX=-49.19 StartY=46.25 StartZ=0 EndX=-16.28 EndY=46.25 EndZ=0
    g33: LineSegment StartX=-49.19 StartY=43.25 StartZ=0 EndX=-16.28 EndY=43.25 EndZ=0
    g34: LineSegment StartX=-49.19 StartY=40.5 StartZ=0 EndX=-18.2337 EndY=40.5 EndZ=0
    g35: LineSegment StartX=-49.19 StartY=37.5 StartZ=0 EndX=-18.23 EndY=37.5 EndZ=0
    g36: LineSegment StartX=-49.19 StartY=34.5 StartZ=0 EndX=-18.2337 EndY=34.5 EndZ=0
    g37: LineSegment StartX=-49.19 StartY=31.5 StartZ=0 EndX=-18.23 EndY=31.5 EndZ=0
    g38: LineSegment StartX=-49.19 StartY=28.75 StartZ=0 EndX=-16.2837 EndY=28.75 EndZ=0
    g39: LineSegment StartX=-49.19 StartY=25.75 StartZ=0 EndX=-16.28 EndY=25.75 EndZ=0
    g40: LineSegment StartX=-49.19 StartY=23 StartZ=0 EndX=-11.49 EndY=23 EndZ=0
    g41: LineSegment StartX=-49.19 StartY=20 StartZ=0 EndX=-11.49 EndY=20 EndZ=0
    g42: LineSegment StartX=-49.19 StartY=17.25 StartZ=0 EndX=-1.5 EndY=17.25 EndZ=0
    g43: LineSegment StartX=-49.19 StartY=14.25 StartZ=0 EndX=-1.5 EndY=14.25 EndZ=0
    g44: LineSegment StartX=-49.19 StartY=11.5 StartZ=0 EndX=-1.5 EndY=11.5 EndZ=0
    g45: LineSegment StartX=-49.19 StartY=8.5 StartZ=0 EndX=-1.5 EndY=8.5 EndZ=0
    g46: LineSegment StartX=-49.19 StartY=5.75 StartZ=0 EndX=-1.5 EndY=5.75 EndZ=0
    g47: LineSegment StartX=-49.19 StartY=2.75 StartZ=0 EndX=-1.5 EndY=2.75 EndZ=0
  constraints (120):
    c: Vertical(g0)
    c: Distance(g0) = 3
    c: Block(g0)
    c: Vertical(g1)
    c: Distance(g1) = 3
    c: Vertical(g2)
    c: Equal(g0,g2) = 3
    c: Block(g2)
    c: Vertical(g3)
    c: Equal(g1,g3) = 3
    c: Vertical(g4)
    c: Equal(g0,g4) = 3
    c: Block(g4)
    c: Vertical(g5)
    c: Equal(g1,g5) = 3
    c: Vertical(g6)
    c: Equal(g0,g6) = 3
    c: Block(g6)
    c: Vertical(g7)
    c: Equal(g1,g7) = 3
    c: Vertical(g8)
    c: Equal(g0,g8) = 3
    c: Block(g8)
    c: Vertical(g9)
    c: Equal(g1,g9) = 3
    c: Vertical(g10)
    c: Equal(g0,g10) = 3
    c: Block(g10)
    c: Vertical(g11)
    c: Equal(g1,g11) = 3
    c: Block(g12)
    c: Block(g13)
    c: Block(g14)
    c: Block(g15)
    c: Block(g16)
    c: Block(g17)
    c: Block(g18)
    c: Block(g19)
    c: Block(g20)
    c: Block(g21)
    c: Block(g22)
    c: Block(g23)
    c: Block(g11)
    c: Block(g9)
    c: Block(g7)
    c: Block(g5)
    c: Block(g3)
    c: Block(g1)
    c: Coincident(g24,g0)
    c: Coincident(g24,g12)
    c: Horizontal(g24)
    c: Coincident(g25,g0)
    c: Coincident(g25,g12)
    c: Horizontal(g25)
    c: Coincident(g26,g1)
    c: Coincident(g26,g13)
    c: Horizontal(g26)
    c: Coincident(g27,g1)
    c: Coincident(g27,g13)
    c: Horizontal(g27)
    c: Coincident(g28,g2)
    c: Coincident(g28,g14)
    c: Horizontal(g28)
    c: Coincident(g29,g2)
    c: Coincident(g29,g14)
    c: Horizontal(g29)
    c: Coincident(g30,g3)
    c: Coincident(g30,g15)
    c: Horizontal(g30)
    c: Coincident(g31,g3)
    c: Coincident(g31,g15)
    c: Horizontal(g31)
    c: Coincident(g32,g4)
    c: Coincident(g32,g16)
    c: Horizontal(g32)
    c: Coincident(g33,g4)
    c: Coincident(g33,g16)
    c: Horizontal(g33)
    c: Coincident(g34,g5)
    c: Coincident(g34,g17)
    c: Horizontal(g34)
    c: Coincident(g35,g5)
    c: Coincident(g35,g17)
    c: Horizontal(g35)
    c: Coincident(g36,g6)
    c: Coincident(g36,g19)
    c: Horizontal(g36)
    c: Coincident(g37,g6)
    c: Coincident(g37,g19)
    c: Horizontal(g37)
    c: Coincident(g38,g7)
    c: Coincident(g38,g18)
    c: Horizontal(g38)
    c: Coincident(g39,g7)
    c: Coincident(g39,g18)
    c: Horizontal(g39)
    c: Coincident(g40,g8)
    c: Coincident(g40,g20)
    c: Horizontal(g40)
    c: Coincident(g41,g8)
    c: Coincident(g41,g20)
    c: Horizontal(g41)
    c: Coincident(g42,g9)
    c: Coincident(g42,g23)
    c: Horizontal(g42)
    c: Coincident(g43,g9)
    c: Coincident(g43,g23)
    c: Horizontal(g43)
    c: Coincident(g44,g10)
    c: Coincident(g44,g22)
    c: Horizontal(g44)
    c: Coincident(g45,g10)
    c: Coincident(g45,g22)
    c: Horizontal(g45)
    c: Coincident(g46,g11)
    c: Coincident(g46,g21)
    c: Horizontal(g46)
    c: Coincident(g47,g11)
    c: Coincident(g47,g21)
    c: Horizontal(g47)
FEATURE [Part::Extrusion] Extrude046
  Base = -> Sketch055
  Dir = (1,0,0)
  DirMode = 2
  FaceMakerClass = Part::FaceMakerBullseye
  LengthFwd = 23
  LengthRev = 0
  Placement = pos=(-19,0,0) rot=(0,0,1;0rad)
  Solid = true
  Symmetric = false
FEATURE [Part::Fillet] Fillet038  label="removeToCreateVentalationHoles001"
  Base = -> Extrude046
  Edges = <same value as first occurrence — deduplicated (x6 in doc)>
  Placement = pos=(7,0,0) rot=(0,0,1;0rad)
FEATURE [Sketcher::SketchObject] Sketch056  label="topSketch014"
  FullyConstrained = true
  sketch-geometry (22):
    g0: LineSegment StartX=5.21097e-06 StartY=3 StartZ=0 EndX=5.21097e-06 EndY=19 EndZ=0
    g1: ArcOfCircle CenterX=19 CenterY=19 CenterZ=0 NormalX=0 NormalY=0 NormalZ=1 AngleXU=0 Radius=19 StartAngle=1.5708 EndAngle=3.14159
    g2: ArcOfCircle CenterX=19 CenterY=19 CenterZ=0 NormalX=0 NormalY=0 NormalZ=1 AngleXU=0 Radius=16 StartAngle=1.5708 EndAngle=3.14159
    g3: LineSegment StartX=114 StartY=35 StartZ=0 EndX=19 EndY=35 EndZ=0
    g4: LineSegment StartX=5.21097e-06 StartY=3 StartZ=0 EndX=5.21097e-06 EndY=0 EndZ=0
    g5: LineSegment StartX=3 StartY=0 StartZ=0 EndX=5.21097e-06 EndY=0 EndZ=0
    g6: LineSegment StartX=3 StartY=19 StartZ=0 EndX=3 EndY=0 EndZ=0
    g7: LineSegment StartX=19 StartY=38 StartZ=0 EndX=124 EndY=38 EndZ=0
    g8: Circle CenterX=119 CenterY=35 CenterZ=0 NormalX=0 NormalY=0 NormalZ=1 AngleXU=0 Radius=1
    g9: Circle CenterX=121 CenterY=35 CenterZ=0 NormalX=0 NormalY=0 NormalZ=1 AngleXU=0 Radius=1
    g10: Circle CenterX=121 CenterY=33 CenterZ=0 NormalX=0 NormalY=0 NormalZ=1 AngleXU=0 Radius=1
    g11: BSplineCurve PolesCount=3 KnotsCount=2 Degree=2 IsPeriodic=0
    g12: GeomPoint X=119 Y=35 Z=0
    g13: GeomPoint X=121 Y=33 Z=0
    g14: LineSegment StartX=119 StartY=35 StartZ=0 EndX=114 EndY=35 EndZ=0
    g15: ArcOfCircle CenterX=105 CenterY=19 CenterZ=0 NormalX=0 NormalY=0 NormalZ=1 AngleXU=0 Radius=16 StartAngle=5.60905 EndAngle=6.28319
    g16: LineSegment StartX=121 StartY=33 StartZ=0 EndX=121 EndY=19 EndZ=0
    g17: LineSegment StartX=117.5 StartY=9.01251 StartZ=0 EndX=121.163 EndY=9.0125 EndZ=0
    g18: ArcOfCircle CenterX=105 CenterY=19 CenterZ=0 NormalX=0 NormalY=0 NormalZ=1 AngleXU=0 Radius=20.6155 StartAngle=5.7297 EndAngle=6.28319
    g19: LineSegment StartX=121.163 StartY=9.0125 StartZ=0 EndX=122.538 EndY=8.16329 EndZ=0
    g20: LineSegment StartX=124 StartY=38 StartZ=0 EndX=125.616 EndY=38 EndZ=0
    g21: LineSegment StartX=125.616 StartY=19 StartZ=0 EndX=125.616 EndY=38 EndZ=0
  constraints (49):
    c: Vertical(g0)
    c: Block(g0)
    c: Coincident(g1,g0)
    c: Block(g1)
    c: Coincident(g2,g1)
    c: Block(g2)
    c: Coincident(g3,g2)
    c: Horizontal(g3)
    c: Tangent(g3,g2)
    c: Coincident(g4,g0)
    c: Distance(g4) = 3
    c: Vertical(g4)
    c: Coincident(g5,g4)
    c: Horizontal(g5)
    c: Coincident(g6,g2)
    c: Coincident(g6,g5)
    c: Vertical(g6)
    c: Horizontal(g7)
    c: Distance(g7) = 105
    c: Coincident(g7,g1)
    c: Block(g3)
    c: Weight(g8) = 1
    c: Equal(g8,g9)
    c: Equal(g8,g10)
    c: InternalAlignment(g8,g11)
    c: InternalAlignment(g9,g11)
    c: InternalAlignment(g10,g11)
    c: InternalAlignment(g12,g11)
    c: InternalAlignment(g13,g11)
    c: Block(g11)
    c: Coincident(g14,g11)
    c: Coincident(g14,g3)
    c: Horizontal(g14)
    c: Block(g15)
    c: Coincident(g16,g11)
    c: Coincident(g16,g15)
    c: Vertical(g16)
    c: Distance(g16) = 14
    c: Coincident(g17,g15)
    c: Block(g18)
    c: Coincident(g19,g18)
    c: Coincident(g20,g7)
    c: Horizontal(g20)
    c: Vertical(g21)
    c: Coincident(g20,g21)
    c: Block(g20)
    c: Block(g21)
    c: Block(g19)
    c: Block(g17)
FEATURE [Part::Box] Box026  label="removeToCreteHoleForPlugHousing032"
  AttacherType = Attacher::AttachEngine3D
  Height = 28.6
  Length = 10
  Placement = pos=(-2,0,21.7) rot=(0,0,1;0rad)
  Width = 19
FEATURE [Part::Feature] Face109 .. Face112  x4 (patterned run collapsed; names and placements below)
  shape: bbox 3.5 x 17.8 x 2e-07 mm, 1 faces, 0 solids (baked)
FEATURE [Part::Revolution] Revolve117  label="removeToCreateScrewAndThreadedInsertHole045"
  Angle = 360
  Axis = (0,1,0)
  Base = (0,0,0)
  FaceMakerClass = Part::FaceMakerBullseye
  Placement = pos=(62.3,30.3,19.7) rot=(0,0,1;0rad)
  Solid = false
  Source = -> Face109
  Symmetric = false
FEATURE [Part::Revolution] Revolve118  label="removeToCreateScrewAndThreadedInsertHole046"
  Angle = 360
  Axis = (0,1,0)
  Base = (0,0,0)
  FaceMakerClass = Part::FaceMakerBullseye
  Placement = pos=(62.3,30.3,51.7) rot=(0,0,1;0rad)
  Solid = false
  Source = -> Face110
  Symmetric = false
FEATURE [Part::Revolution] Revolve119  label="removeToCreateScrewAndThreadedInsertHole047"
  Angle = 360
  Axis = (0,1,0)
  Base = (0,0,0)
  FaceMakerClass = Part::FaceMakerBullseye
  Placement = pos=(30.3,30.3,19.7) rot=(0,0,1;0rad)
  Solid = false
  Source = -> Face111
  Symmetric = false
FEATURE [Part::Revolution] Revolve120  label="removeToCreateScrewAndThreadedInsertHole048"
  Angle = 360
  Axis = (0,1,0)
  Base = (0,0,0)
  FaceMakerClass = Part::FaceMakerBullseye
  Placement = pos=(30.3,30.3,51.7) rot=(0,0,1;0rad)
  Solid = false
  Source = -> Face112
  Symmetric = false
FEATURE [Part::MultiFuse] Fusion087  label="createThreadedInsertHolesForFan005"
  Shapes = -> [Revolve117,Revolve118,Revolve119,Revolve120]
FEATURE [Part::Extrusion] Extrude047
  Base = -> Sketch056
  Dir = (0,0,1)
  DirMode = 2
  FaceMakerClass = Part::FaceMakerBullseye
  LengthFwd = 72
  LengthRev = 0
  Solid = true
  Symmetric = false
FEATURE [Part::Fillet] Fillet039  label="top019"
  Base = -> Extrude047
  Edges = 1 edges r=2: [Edge35]
FEATURE [Sketcher::SketchObject] Sketch057
  FullyConstrained = false
  Placement = pos=(0,0,0) rot=(1,0,0;1.5708rad)
  sketch-geometry (24):
    g0: ArcOfCircle CenterX=-4 CenterY=-10.5 CenterZ=0 NormalX=0 NormalY=0 NormalZ=1 AngleXU=0 Radius=1.5 StartAngle=6e-16 EndAngle=3.14159
    g1: ArcOfCircle CenterX=-34.2 CenterY=-10.5 CenterZ=0 NormalX=0 NormalY=0 NormalZ=1 AngleXU=0 Radius=1.5 StartAngle=0 EndAngle=3.14159
    g2: ArcOfCircle CenterX=-34.2 CenterY=-27.7 CenterZ=0 NormalX=0 NormalY=0 NormalZ=1 AngleXU=0 Radius=1.5 StartAngle=3.14159 EndAngle=6.28319
    g3: ArcOfCircle CenterX=-4 CenterY=-27.7 CenterZ=0 NormalX=0 NormalY=0 NormalZ=1 AngleXU=0 Radius=1.5 StartAngle=3.1416 EndAngle=6.28319
    g4: ArcOfCircle CenterX=-10 CenterY=-4.3 CenterZ=0 NormalX=0 NormalY=0 NormalZ=1 AngleXU=0 Radius=1.5 StartAngle=2e-16 EndAngle=3.14159
    g5: ArcOfCircle CenterX=-16.1 CenterY=-1.8 CenterZ=0 NormalX=0 NormalY=0 NormalZ=1 AngleXU=0 Radius=1.5 StartAngle=5e-16 EndAngle=3.14159
    g6: ArcOfCircle CenterX=-22.1 CenterY=-1.8 CenterZ=0 NormalX=0 NormalY=0 NormalZ=1 AngleXU=0 Radius=1.5 StartAngle=5e-16 EndAngle=3.14159
    g7: ArcOfCircle CenterX=-28.2 CenterY=-4.3 CenterZ=0 NormalX=0 NormalY=0 NormalZ=1 AngleXU=0 Radius=1.5 StartAngle=2e-16 EndAngle=3.14159
    g8: ArcOfCircle CenterX=-10 CenterY=-33.9 CenterZ=0 NormalX=0 NormalY=0 NormalZ=1 AngleXU=0 Radius=1.5 StartAngle=3.14159 EndAngle=6.28319
    g9: ArcOfCircle CenterX=-16.1 CenterY=-36.4 CenterZ=0 NormalX=0 NormalY=0 NormalZ=1 AngleXU=0 Radius=1.5 StartAngle=3.14159 EndAngle=6.28319
    g10: ArcOfCircle CenterX=-22.1 CenterY=-36.4 CenterZ=0 NormalX=0 NormalY=0 NormalZ=1 AngleXU=0 Radius=1.5 StartAngle=3.14159 EndAngle=6.28319
    g11: ArcOfCircle CenterX=-28.2 CenterY=-33.9 CenterZ=0 NormalX=0 NormalY=0 NormalZ=1 AngleXU=0 Radius=1.5 StartAngle=3.14159 EndAngle=6.28319
    g12: LineSegment StartX=-35.7 StartY=-10.5 StartZ=0 EndX=-35.7 EndY=-27.7 EndZ=0
    g13: LineSegment StartX=-32.7 StartY=-10.5 StartZ=0 EndX=-32.7 EndY=-27.7 EndZ=0
    g14: LineSegment StartX=-29.7 StartY=-33.9 StartZ=0 EndX=-29.7 EndY=-4.3 EndZ=0
    g15: LineSegment StartX=-26.7 StartY=-33.9 StartZ=0 EndX=-26.7 EndY=-4.3 EndZ=0
    g16: LineSegment StartX=-2.5 StartY=-10.5 StartZ=0 EndX=-2.5 EndY=-27.7 EndZ=0
    g17: LineSegment StartX=-8.5 StartY=-4.3 StartZ=0 EndX=-8.5 EndY=-33.9 EndZ=0
    g18: LineSegment StartX=-5.5 StartY=-10.5 StartZ=0 EndX=-5.5 EndY=-27.7 EndZ=0
    g19: LineSegment StartX=-11.5 StartY=-4.3 StartZ=0 EndX=-11.5 EndY=-33.9 EndZ=0
    g20: LineSegment StartX=-14.6 StartY=-1.8 StartZ=0 EndX=-14.6 EndY=-36.4 EndZ=0
    g21: LineSegment StartX=-17.6 StartY=-1.8 StartZ=0 EndX=-17.6 EndY=-36.4 EndZ=0
    g22: LineSegment StartX=-20.6 StartY=-36.4 StartZ=0 EndX=-20.6 EndY=-1.8 EndZ=0
    g23: LineSegment StartX=-23.6 StartY=-1.8 StartZ=0 EndX=-23.6 EndY=-36.4 EndZ=0
  constraints (48):
    c: Block(g0)
    c: Block(g1)
    c: Block(g2)
    c: Block(g3)
    c: Block(g4)
    c: Block(g5)
    c: Block(g6)
    c: Block(g7)
    c: Block(g8)
    c: Block(g9)
    c: Block(g10)
    c: Block(g11)
    c: Coincident(g12,g1)
    c: Coincident(g12,g2)
    c: Vertical(g12)
    c: Coincident(g13,g1)
    c: Coincident(g13,g2)
    c: Vertical(g13)
    c: Coincident(g14,g11)
    c: Coincident(g14,g7)
    c: Vertical(g14)
    c: Coincident(g15,g11)
    c: Coincident(g15,g7)
    c: Vertical(g15)
    c: Coincident(g16,g0)
    c: Coincident(g16,g3)
    c: Vertical(g16)
    c: Coincident(g17,g4)
    c: Coincident(g17,g8)
    c: Vertical(g17)
    c: Coincident(g18,g0)
    c: Coincident(g18,g3)
    c: Vertical(g18)
    c: Coincident(g19,g4)
    c: Coincident(g19,g8)
    c: Vertical(g19)
    c: Coincident(g20,g5)
    c: Coincident(g20,g9)
    c: Vertical(g20)
    c: Coincident(g21,g5)
    c: Coincident(g21,g9)
    c: Vertical(g21)
    c: Coincident(g22,g10)
    c: Coincident(g22,g6)
    c: Vertical(g22)
    c: Coincident(g23,g6)
    c: Coincident(g23,g10)
    c: Vertical(g23)
FEATURE [Part::Extrusion] Extrude048  label="removeToCreateFanGrillHoles004"
  Base = -> Sketch057
  Dir = (0,-1,6e-16)
  DirMode = 2
  FaceMakerClass = Part::FaceMakerBullseye
  LengthFwd = 10
  LengthRev = 0
  Placement = pos=(65.4,44,54.82) rot=(0,0,1;0rad)
  Solid = true
  Symmetric = false
FEATURE [Part::Cut] Cut040  label="top021"
  Base = -> Fillet039
  Tool = -> Extrude048
FEATURE [Part::Cylinder] Cylinder041  label="removeToCreteHoleForPlugHousing034"
  Angle = 360
  AttacherType = Attacher::AttachEngine3D
  Height = 20
  Placement = pos=(-2,19,36) rot=(0,1,0;1.5708rad)
  Radius = 14.3
FEATURE [Part::MultiFuse] Fusion089  label="removeToCreteHoleForPlugHousing035"
  Shapes = -> [Box026,Cylinder041]
FEATURE [Part::Cylinder] Cylinder042
  Angle = 360
  AttacherType = Attacher::AttachEngine3D
  Height = 20
  Placement = pos=(0,0,36.15) rot=(0,0,1;0rad)
  Radius = 14.3
FEATURE [Part::Cylinder] Cylinder043
  Angle = 360
  AttacherType = Attacher::AttachEngine3D
  Height = 10
  Placement = pos=(0,0,36.15) rot=(0,0,1;0rad)
  Radius = 4
FEATURE [Part::Box] Box027  label="removeToCreteHoleForPlugHousing036"
  AttacherType = Attacher::AttachEngine3D
  Height = 28.6
  Length = 20
  Placement = pos=(106.15,0,21.7) rot=(0,0,1;0rad)
  Width = 19
FEATURE [Part::Cut] Cut041  label="top022"
  Base = -> Cut040
  Tool = -> Fusion087
FEATURE [Part::Cut] Cut039  label="top020"
  Base = -> Cut041
  Tool = -> Fusion089
FEATURE [Part::MultiFuse] Fusion090  label="removeToCreteHoleForPlugHousing037"
  Placement = pos=(70,19,36) rot=(0,1,0;1.5708rad)
  Shapes = -> [Cylinder042,Cylinder043]
FEATURE [Part::MultiFuse] Fusion088  label="removeToCreteHoleForPlugHousing033"
  Shapes = -> [Box027,Fusion090]
FEATURE [Part::Cut] Cut042  label="removeToCreteHoleForPlugHousing038"
  Base = -> Cut039
  Tool = -> Fusion088
FEATURE [Part::MultiFuse] Fusion091  label="removeFromTop"
  Shapes = -> [Fillet038,Fusion085,Fusion084,Fusion083,Extrude045]
FEATURE [Part::Cut] Cut043  label="REAL TOP ====="
  Base = -> Fillet036
  Tool = -> Fusion091
FEATURE [Part::MultiFuse] Fusion092  label="caseScrewPillarBracket016"
  Shapes = -> [Extrude030,Extrude031,Extrude032,Extrude033,Extrude034,Extrude035,Extrude036,Extrude037,Box013,Box014]
FEATURE [Sketcher::SketchObject] Sketch058  label="topSketch015"
  FullyConstrained = true
  sketch-geometry (20):
    g0: LineSegment StartX=5.21097e-06 StartY=3 StartZ=0 EndX=5.21097e-06 EndY=19 EndZ=0
    g1: ArcOfCircle CenterX=19 CenterY=19 CenterZ=0 NormalX=0 NormalY=0 NormalZ=1 AngleXU=0 Radius=19 StartAngle=1.5708 EndAngle=3.14159
    g2: ArcOfCircle CenterX=19 CenterY=19 CenterZ=0 NormalX=0 NormalY=0 NormalZ=1 AngleXU=0 Radius=16 StartAngle=1.5708 EndAngle=3.14159
    g3: LineSegment StartX=114 StartY=35 StartZ=0 EndX=19 EndY=35 EndZ=0
    g4: LineSegment StartX=5.21097e-06 StartY=3 StartZ=0 EndX=5.21097e-06 EndY=0 EndZ=0
    g5: LineSegment StartX=3 StartY=0 StartZ=0 EndX=5.21097e-06 EndY=0 EndZ=0
    g6: LineSegment StartX=3 StartY=19 StartZ=0 EndX=3 EndY=0 EndZ=0
    g7: LineSegment StartX=19 StartY=38 StartZ=0 EndX=124 EndY=38 EndZ=0
    g8: Circle CenterX=119 CenterY=35 CenterZ=0 NormalX=0 NormalY=0 NormalZ=1 AngleXU=0 Radius=1
    g9: Circle CenterX=121 CenterY=35 CenterZ=0 NormalX=0 NormalY=0 NormalZ=1 AngleXU=0 Radius=1
    g10: Circle CenterX=121 CenterY=33 CenterZ=0 NormalX=0 NormalY=0 NormalZ=1 AngleXU=0 Radius=1
    g11: BSplineCurve PolesCount=3 KnotsCount=2 Degree=2 IsPeriodic=0
    g12: GeomPoint X=119 Y=35 Z=0
    g13: GeomPoint X=121 Y=33 Z=0
    g14: LineSegment StartX=119 StartY=35 StartZ=0 EndX=114 EndY=35 EndZ=0
    g15: ArcOfCircle CenterX=105 CenterY=19 CenterZ=0 NormalX=0 NormalY=0 NormalZ=1 AngleXU=0 Radius=19 StartAngle=5.7297 EndAngle=6.28319
    g16: ArcOfCircle CenterX=105 CenterY=19 CenterZ=0 NormalX=0 NormalY=0 NormalZ=1 AngleXU=0 Radius=16 StartAngle=5.60905 EndAngle=6.28319
    g17: LineSegment StartX=121 StartY=33 StartZ=0 EndX=121 EndY=19 EndZ=0
    g18: LineSegment StartX=124 StartY=38 StartZ=0 EndX=124 EndY=19 EndZ=0
    g19: LineSegment StartX=117.5 StartY=9.01251 StartZ=0 EndX=121.163 EndY=9.0125 EndZ=0
  constraints (46):
    c: Vertical(g0)
    c: Block(g0)
    c: Coincident(g1,g0)
    c: Block(g1)
    c: Coincident(g2,g1)
    c: Block(g2)
    c: Coincident(g3,g2)
    c: Horizontal(g3)
    c: Tangent(g3,g2)
    c: Coincident(g4,g0)
    c: Distance(g4) = 3
    c: Vertical(g4)
    c: Coincident(g5,g4)
    c: Horizontal(g5)
    c: Coincident(g6,g2)
    c: Coincident(g6,g5)
    c: Vertical(g6)
    c: Horizontal(g7)
    c: Distance(g7) = 105
    c: Coincident(g7,g1)
    c: Block(g3)
    c: Weight(g8) = 1
    c: Equal(g8,g9)
    c: Equal(g8,g10)
    c: InternalAlignment(g8,g11)
    c: InternalAlignment(g9,g11)
    c: InternalAlignment(g10,g11)
    c: InternalAlignment(g12,g11)
    c: InternalAlignment(g13,g11)
    c: Block(g11)
    c: Coincident(g14,g11)
    c: Coincident(g14,g3)
    c: Horizontal(g14)
    c: Block(g15)
    c: Coincident(g16,g15)
    c: Block(g16)
    c: Coincident(g17,g11)
    c: Coincident(g17,g16)
    c: Vertical(g17)
    c: Distance(g17) = 14
    c: Coincident(g18,g7)
    c: Coincident(g18,g15)
    c: Vertical(g18)
    c: Distance(g18) = 19
    c: Coincident(g19,g16)
    c: Coincident(g19,g15)
FEATURE [Part::Extrusion] Extrude049  label="top023"
  Base = -> Sketch058
  Dir = (0,0,1)
  DirMode = 2
  FaceMakerClass = Part::FaceMakerBullseye
  LengthFwd = 72
  LengthRev = 0
  Solid = true
  Symmetric = false
FEATURE [Sketcher::SketchObject] Sketch059
  FullyConstrained = true
  MapMode = 3
  Placement = pos=(0,0,0) rot=(1,0,0;1.5708rad)
  Support = -> [Extrude049]
  sketch-geometry (8):
    g0: Circle CenterX=80.351 CenterY=-67.6202 CenterZ=0 NormalX=0 NormalY=0 NormalZ=1 AngleXU=0 Radius=2
    g1: Circle CenterX=80.351 CenterY=-67.6202 CenterZ=0 NormalX=0 NormalY=0 NormalZ=1 AngleXU=0 Radius=3
    g2: Circle CenterX=80.351 CenterY=-4.92017 CenterZ=0 NormalX=0 NormalY=0 NormalZ=1 AngleXU=0 Radius=2
    g3: Circle CenterX=80.351 CenterY=-4.92017 CenterZ=0 NormalX=0 NormalY=0 NormalZ=1 AngleXU=0 Radius=3
    g4: Circle CenterX=23.851 CenterY=-4.92017 CenterZ=0 NormalX=0 NormalY=0 NormalZ=1 AngleXU=0 Radius=2
    g5: Circle CenterX=23.851 CenterY=-4.92017 CenterZ=0 NormalX=0 NormalY=0 NormalZ=1 AngleXU=0 Radius=3
    g6: Circle CenterX=23.851 CenterY=-67.6202 CenterZ=0 NormalX=0 NormalY=0 NormalZ=1 AngleXU=0 Radius=2
    g7: Circle CenterX=23.851 CenterY=-67.6202 CenterZ=0 NormalX=0 NormalY=0 NormalZ=1 AngleXU=0 Radius=3
  constraints (8):
    c: Block(g3)
    c: Block(g2)
    c: Block(g1)
    c: Block(g0)
    c: Block(g6)
    c: Block(g7)
    c: Block(g4)
    c: Block(g5)
FEATURE [Sketcher::SketchObject] Sketch060
  FullyConstrained = true
  MapMode = 3
  Placement = pos=(0,0,0) rot=(1,0,0;1.5708rad)
  Support = -> [Extrude049]
  sketch-geometry (8):
    g0: Circle CenterX=80.351 CenterY=-67.6202 CenterZ=0 NormalX=0 NormalY=0 NormalZ=1 AngleXU=0 Radius=3
    g1: Circle CenterX=80.351 CenterY=-4.92017 CenterZ=0 NormalX=0 NormalY=0 NormalZ=1 AngleXU=0 Radius=3
    g2: Circle CenterX=23.851 CenterY=-4.92017 CenterZ=0 NormalX=0 NormalY=0 NormalZ=1 AngleXU=0 Radius=3
    g3: Circle CenterX=23.851 CenterY=-67.6202 CenterZ=0 NormalX=0 NormalY=0 NormalZ=1 AngleXU=0 Radius=3
    g4: Circle CenterX=23.851 CenterY=-67.6202 CenterZ=0 NormalX=0 NormalY=0 NormalZ=1 AngleXU=0 Radius=5
    g5: Circle CenterX=80.351 CenterY=-67.6202 CenterZ=0 NormalX=0 NormalY=0 NormalZ=1 AngleXU=0 Radius=5
    g6: Circle CenterX=23.851 CenterY=-4.92017 CenterZ=0 NormalX=0 NormalY=0 NormalZ=1 AngleXU=0 Radius=5
    g7: Circle CenterX=80.351 CenterY=-4.92017 CenterZ=0 NormalX=0 NormalY=0 NormalZ=1 AngleXU=0 Radius=5
  constraints (8):
    c: Block(g1)
    c: Block(g0)
    c: Block(g3)
    c: Block(g2)
    c: Block(g5)
    c: Block(g4)
    c: Block(g6)
    c: Block(g7)
FEATURE [Sketcher::SketchObject] Sketch061
  FullyConstrained = true
  MapMode = 3
  Placement = pos=(0,0,0) rot=(1,0,0;1.5708rad)
  sketch-geometry (8):
    g0: Circle CenterX=80.351 CenterY=-67.6202 CenterZ=0 NormalX=0 NormalY=0 NormalZ=1 AngleXU=0 Radius=3
    g1: Circle CenterX=80.351 CenterY=-4.92017 CenterZ=0 NormalX=0 NormalY=0 NormalZ=1 AngleXU=0 Radius=3
    g2: Circle CenterX=23.851 CenterY=-4.92017 CenterZ=0 NormalX=0 NormalY=0 NormalZ=1 AngleXU=0 Radius=3
    g3: Circle CenterX=23.851 CenterY=-67.6202 CenterZ=0 NormalX=0 NormalY=0 NormalZ=1 AngleXU=0 Radius=3
    g4: Circle CenterX=23.851 CenterY=-67.6202 CenterZ=0 NormalX=0 NormalY=0 NormalZ=1 AngleXU=0 Radius=5
    g5: Circle CenterX=80.351 CenterY=-67.6202 CenterZ=0 NormalX=0 NormalY=0 NormalZ=1 AngleXU=0 Radius=5
    g6: Circle CenterX=23.851 CenterY=-4.92017 CenterZ=0 NormalX=0 NormalY=0 NormalZ=1 AngleXU=0 Radius=5
    g7: Circle CenterX=80.351 CenterY=-4.92017 CenterZ=0 NormalX=0 NormalY=0 NormalZ=1 AngleXU=0 Radius=5
  constraints (8):
    c: Block(g1)
    c: Block(g0)
    c: Block(g3)
    c: Block(g2)
    c: Block(g5)
    c: Block(g4)
    c: Block(g6)
    c: Block(g7)
FEATURE [Sketcher::SketchObject] Sketch062  label="topSketch016"
  FullyConstrained = true
  sketch-geometry (20):
    g0: LineSegment StartX=5.21097e-06 StartY=3 StartZ=0 EndX=5.21097e-06 EndY=19 EndZ=0
    g1: ArcOfCircle CenterX=19 CenterY=19 CenterZ=0 NormalX=0 NormalY=0 NormalZ=1 AngleXU=0 Radius=19 StartAngle=1.5708 EndAngle=3.14159
    g2: ArcOfCircle CenterX=19 CenterY=19 CenterZ=0 NormalX=0 NormalY=0 NormalZ=1 AngleXU=0 Radius=16 StartAngle=1.5708 EndAngle=3.14159
    g3: LineSegment StartX=114 StartY=35 StartZ=0 EndX=19 EndY=35 EndZ=0
    g4: LineSegment StartX=5.21097e-06 StartY=3 StartZ=0 EndX=5.21097e-06 EndY=0 EndZ=0
    g5: LineSegment StartX=3 StartY=0 StartZ=0 EndX=5.21097e-06 EndY=0 EndZ=0
    g6: LineSegment StartX=3 StartY=19 StartZ=0 EndX=3 EndY=0 EndZ=0
    g7: LineSegment StartX=19 StartY=38 StartZ=0 EndX=124 EndY=38 EndZ=0
    g8: Circle CenterX=119 CenterY=35 CenterZ=0 NormalX=0 NormalY=0 NormalZ=1 AngleXU=0 Radius=1
    g9: Circle CenterX=121 CenterY=35 CenterZ=0 NormalX=0 NormalY=0 NormalZ=1 AngleXU=0 Radius=1
    g10: Circle CenterX=121 CenterY=33 CenterZ=0 NormalX=0 NormalY=0 NormalZ=1 AngleXU=0 Radius=1
    g11: BSplineCurve PolesCount=3 KnotsCount=2 Degree=2 IsPeriodic=0
    g12: GeomPoint X=119 Y=35 Z=0
    g13: GeomPoint X=121 Y=33 Z=0
    g14: LineSegment StartX=119 StartY=35 StartZ=0 EndX=114 EndY=35 EndZ=0
    g15: ArcOfCircle CenterX=105 CenterY=19 CenterZ=0 NormalX=0 NormalY=0 NormalZ=1 AngleXU=0 Radius=19 StartAngle=5.7297 EndAngle=6.28319
    g16: ArcOfCircle CenterX=105 CenterY=19 CenterZ=0 NormalX=0 NormalY=0 NormalZ=1 AngleXU=0 Radius=16 StartAngle=5.60905 EndAngle=6.28319
    g17: LineSegment StartX=121 StartY=33 StartZ=0 EndX=121 EndY=19 EndZ=0
    g18: LineSegment StartX=124 StartY=38 StartZ=0 EndX=124 EndY=19 EndZ=0
    g19: LineSegment StartX=117.5 StartY=9.01251 StartZ=0 EndX=121.163 EndY=9.0125 EndZ=0
  constraints (46):
    c: Vertical(g0)
    c: Block(g0)
    c: Coincident(g1,g0)
    c: Block(g1)
    c: Coincident(g2,g1)
    c: Block(g2)
    c: Coincident(g3,g2)
    c: Horizontal(g3)
    c: Tangent(g3,g2)
    c: Coincident(g4,g0)
    c: Distance(g4) = 3
    c: Vertical(g4)
    c: Coincident(g5,g4)
    c: Horizontal(g5)
    c: Coincident(g6,g2)
    c: Coincident(g6,g5)
    c: Vertical(g6)
    c: Horizontal(g7)
    c: Distance(g7) = 105
    c: Coincident(g7,g1)
    c: Block(g3)
    c: Weight(g8) = 1
    c: Equal(g8,g9)
    c: Equal(g8,g10)
    c: InternalAlignment(g8,g11)
    c: InternalAlignment(g9,g11)
    c: InternalAlignment(g10,g11)
    c: InternalAlignment(g12,g11)
    c: InternalAlignment(g13,g11)
    c: Block(g11)
    c: Coincident(g14,g11)
    c: Coincident(g14,g3)
    c: Horizontal(g14)
    c: Block(g15)
    c: Coincident(g16,g15)
    c: Block(g16)
    c: Coincident(g17,g11)
    c: Coincident(g17,g16)
    c: Vertical(g17)
    c: Distance(g17) = 14
    c: Coincident(g18,g7)
    c: Coincident(g18,g15)
    c: Vertical(g18)
    c: Distance(g18) = 19
    c: Coincident(g19,g16)
    c: Coincident(g19,g15)
FEATURE [Part::Extrusion] Extrude053  label="top024"
  Base = -> Sketch062
  Dir = (0,0,1)
  DirMode = 2
  FaceMakerClass = Part::FaceMakerBullseye
  LengthFwd = 72
  LengthRev = 0
  Solid = true
  Symmetric = false
FEATURE [Sketcher::SketchObject] Sketch063
  FullyConstrained = true
  MapMode = 3
  Placement = pos=(0,0,0) rot=(1,0,0;1.5708rad)
  Support = -> [Extrude053]
  sketch-geometry (8):
    g0: Circle CenterX=80.351 CenterY=-67.6202 CenterZ=0 NormalX=0 NormalY=0 NormalZ=1 AngleXU=0 Radius=2
    g1: Circle CenterX=80.351 CenterY=-67.6202 CenterZ=0 NormalX=0 NormalY=0 NormalZ=1 AngleXU=0 Radius=3
    g2: Circle CenterX=80.351 CenterY=-4.92017 CenterZ=0 NormalX=0 NormalY=0 NormalZ=1 AngleXU=0 Radius=2
    g3: Circle CenterX=80.351 CenterY=-4.92017 CenterZ=0 NormalX=0 NormalY=0 NormalZ=1 AngleXU=0 Radius=3
    g4: Circle CenterX=23.851 CenterY=-4.92017 CenterZ=0 NormalX=0 NormalY=0 NormalZ=1 AngleXU=0 Radius=2
    g5: Circle CenterX=23.851 CenterY=-4.92017 CenterZ=0 NormalX=0 NormalY=0 NormalZ=1 AngleXU=0 Radius=3
    g6: Circle CenterX=23.851 CenterY=-67.6202 CenterZ=0 NormalX=0 NormalY=0 NormalZ=1 AngleXU=0 Radius=2
    g7: Circle CenterX=23.851 CenterY=-67.6202 CenterZ=0 NormalX=0 NormalY=0 NormalZ=1 AngleXU=0 Radius=3
  constraints (8):
    c: Block(g3)
    c: Block(g2)
    c: Block(g1)
    c: Block(g0)
    c: Block(g6)
    c: Block(g7)
    c: Block(g4)
    c: Block(g5)
FEATURE [Part::Extrusion] Extrude054
  Base = -> Sketch063
  Dir = (0,-1,2e-16)
  DirMode = 2
  FaceMakerClass = Part::FaceMakerBullseye
  LengthFwd = 6
  LengthRev = 0
  Placement = pos=(0,9,0) rot=(0,0,1;0rad)
  Solid = true
  Symmetric = false
FEATURE [Sketcher::SketchObject] Sketch064  label="topSketch017"
  FullyConstrained = true
  sketch-geometry (20):
    g0: LineSegment StartX=5.21097e-06 StartY=3 StartZ=0 EndX=5.21097e-06 EndY=19 EndZ=0
    g1: ArcOfCircle CenterX=19 CenterY=19 CenterZ=0 NormalX=0 NormalY=0 NormalZ=1 AngleXU=0 Radius=19 StartAngle=1.5708 EndAngle=3.14159
    g2: ArcOfCircle CenterX=19 CenterY=19 CenterZ=0 NormalX=0 NormalY=0 NormalZ=1 AngleXU=0 Radius=16 StartAngle=1.5708 EndAngle=3.14159
    g3: LineSegment StartX=114 StartY=35 StartZ=0 EndX=19 EndY=35 EndZ=0
    g4: LineSegment StartX=5.21097e-06 StartY=3 StartZ=0 EndX=5.21097e-06 EndY=0 EndZ=0
    g5: LineSegment StartX=3 StartY=0 StartZ=0 EndX=5.21097e-06 EndY=0 EndZ=0
    g6: LineSegment StartX=3 StartY=19 StartZ=0 EndX=3 EndY=0 EndZ=0
    g7: LineSegment StartX=19 StartY=38 StartZ=0 EndX=124 EndY=38 EndZ=0
    g8: Circle CenterX=119 CenterY=35 CenterZ=0 NormalX=0 NormalY=0 NormalZ=1 AngleXU=0 Radius=1
    g9: Circle CenterX=121 CenterY=35 CenterZ=0 NormalX=0 NormalY=0 NormalZ=1 AngleXU=0 Radius=1
    g10: Circle CenterX=121 CenterY=33 CenterZ=0 NormalX=0 NormalY=0 NormalZ=1 AngleXU=0 Radius=1
    g11: BSplineCurve PolesCount=3 KnotsCount=2 Degree=2 IsPeriodic=0
    g12: GeomPoint X=119 Y=35 Z=0
    g13: GeomPoint X=121 Y=33 Z=0
    g14: LineSegment StartX=119 StartY=35 StartZ=0 EndX=114 EndY=35 EndZ=0
    g15: ArcOfCircle CenterX=105 CenterY=19 CenterZ=0 NormalX=0 NormalY=0 NormalZ=1 AngleXU=0 Radius=19 StartAngle=5.7297 EndAngle=6.28319
    g16: ArcOfCircle CenterX=105 CenterY=19 CenterZ=0 NormalX=0 NormalY=0 NormalZ=1 AngleXU=0 Radius=16 StartAngle=5.60905 EndAngle=6.28319
    g17: LineSegment StartX=121 StartY=33 StartZ=0 EndX=121 EndY=19 EndZ=0
    g18: LineSegment StartX=124 StartY=38 StartZ=0 EndX=124 EndY=19 EndZ=0
    g19: LineSegment StartX=117.5 StartY=9.01251 StartZ=0 EndX=121.163 EndY=9.0125 EndZ=0
  constraints (46):
    c: Vertical(g0)
    c: Block(g0)
    c: Coincident(g1,g0)
    c: Block(g1)
    c: Coincident(g2,g1)
    c: Block(g2)
    c: Coincident(g3,g2)
    c: Horizontal(g3)
    c: Tangent(g3,g2)
    c: Coincident(g4,g0)
    c: Distance(g4) = 3
    c: Vertical(g4)
    c: Coincident(g5,g4)
    c: Horizontal(g5)
    c: Coincident(g6,g2)
    c: Coincident(g6,g5)
    c: Vertical(g6)
    c: Horizontal(g7)
    c: Distance(g7) = 105
    c: Coincident(g7,g1)
    c: Block(g3)
    c: Weight(g8) = 1
    c: Equal(g8,g9)
    c: Equal(g8,g10)
    c: InternalAlignment(g8,g11)
    c: InternalAlignment(g9,g11)
    c: InternalAlignment(g10,g11)
    c: InternalAlignment(g12,g11)
    c: InternalAlignment(g13,g11)
    c: Block(g11)
    c: Coincident(g14,g11)
    c: Coincident(g14,g3)
    c: Horizontal(g14)
    c: Block(g15)
    c: Coincident(g16,g15)
    c: Block(g16)
    c: Coincident(g17,g11)
    c: Coincident(g17,g16)
    c: Vertical(g17)
    c: Distance(g17) = 14
    c: Coincident(g18,g7)
    c: Coincident(g18,g15)
    c: Vertical(g18)
    c: Distance(g18) = 19
    c: Coincident(g19,g16)
    c: Coincident(g19,g15)
FEATURE [Sketcher::SketchObject] Sketch065
  FullyConstrained = true
  MapMode = 3
  Placement = pos=(0,0,0) rot=(1,0,0;1.5708rad)
  sketch-geometry (8):
    g0: Circle CenterX=80.351 CenterY=-67.6202 CenterZ=0 NormalX=0 NormalY=0 NormalZ=1 AngleXU=0 Radius=3
    g1: Circle CenterX=80.351 CenterY=-4.92017 CenterZ=0 NormalX=0 NormalY=0 NormalZ=1 AngleXU=0 Radius=3
    g2: Circle CenterX=23.851 CenterY=-4.92017 CenterZ=0 NormalX=0 NormalY=0 NormalZ=1 AngleXU=0 Radius=3
    g3: Circle CenterX=23.851 CenterY=-67.6202 CenterZ=0 NormalX=0 NormalY=0 NormalZ=1 AngleXU=0 Radius=3
    g4: Circle CenterX=23.851 CenterY=-67.6202 CenterZ=0 NormalX=0 NormalY=0 NormalZ=1 AngleXU=0 Radius=5
    g5: Circle CenterX=80.351 CenterY=-67.6202 CenterZ=0 NormalX=0 NormalY=0 NormalZ=1 AngleXU=0 Radius=5
    g6: Circle CenterX=23.851 CenterY=-4.92017 CenterZ=0 NormalX=0 NormalY=0 NormalZ=1 AngleXU=0 Radius=5
    g7: Circle CenterX=80.351 CenterY=-4.92017 CenterZ=0 NormalX=0 NormalY=0 NormalZ=1 AngleXU=0 Radius=5
  constraints (8):
    c: Block(g1)
    c: Block(g0)
    c: Block(g3)
    c: Block(g2)
    c: Block(g5)
    c: Block(g4)
    c: Block(g6)
    c: Block(g7)
FEATURE [Part::Extrusion] Extrude056
  Base = -> Sketch065
  Dir = (0,-1,2e-16)
  DirMode = 2
  FaceMakerClass = Part::FaceMakerBullseye
  LengthFwd = 2
  LengthRev = 0
  Solid = true
  Symmetric = false
FEATURE [Part::Extrusion] Extrude057  label="top025"
  Base = -> Sketch064
  Dir = (0,0,1)
  DirMode = 2
  FaceMakerClass = Part::FaceMakerBullseye
  LengthFwd = 72
  LengthRev = 0
  Solid = true
  Symmetric = false
FEATURE [Sketcher::SketchObject] Sketch066
  FullyConstrained = true
  MapMode = 3
  Placement = pos=(0,0,0) rot=(1,0,0;1.5708rad)
  Support = -> [Extrude057]
  sketch-geometry (8):
    g0: Circle CenterX=80.351 CenterY=-67.6202 CenterZ=0 NormalX=0 NormalY=0 NormalZ=1 AngleXU=0 Radius=3
    g1: Circle CenterX=80.351 CenterY=-4.92017 CenterZ=0 NormalX=0 NormalY=0 NormalZ=1 AngleXU=0 Radius=3
    g2: Circle CenterX=23.851 CenterY=-4.92017 CenterZ=0 NormalX=0 NormalY=0 NormalZ=1 AngleXU=0 Radius=3
    g3: Circle CenterX=23.851 CenterY=-67.6202 CenterZ=0 NormalX=0 NormalY=0 NormalZ=1 AngleXU=0 Radius=3
    g4: Circle CenterX=23.851 CenterY=-67.6202 CenterZ=0 NormalX=0 NormalY=0 NormalZ=1 AngleXU=0 Radius=5
    g5: Circle CenterX=80.351 CenterY=-67.6202 CenterZ=0 NormalX=0 NormalY=0 NormalZ=1 AngleXU=0 Radius=5
    g6: Circle CenterX=23.851 CenterY=-4.92017 CenterZ=0 NormalX=0 NormalY=0 NormalZ=1 AngleXU=0 Radius=5
    g7: Circle CenterX=80.351 CenterY=-4.92017 CenterZ=0 NormalX=0 NormalY=0 NormalZ=1 AngleXU=0 Radius=5
  constraints (8):
    c: Block(g1)
    c: Block(g0)
    c: Block(g3)
    c: Block(g2)
    c: Block(g5)
    c: Block(g4)
    c: Block(g6)
    c: Block(g7)
FEATURE [Part::Extrusion] Extrude055
  Base = -> Sketch066
  Dir = (0,-1,2e-16)
  DirMode = 2
  FaceMakerClass = Part::FaceMakerBullseye
  LengthFwd = 2
  LengthRev = 0
  Solid = true
  Symmetric = false
FEATURE [Part::Fillet] Fillet041
  Base = -> Extrude056
  Edges = 4 edges r=1.99: [Edge6,Edge12,Edge18,Edge24]
FEATURE [Part::Cut] Cut045
  Base = -> Extrude055
  Placement = pos=(0,6,0) rot=(0,0,1;0rad)
  Tool = -> Fillet041
FEATURE [Part::MultiFuse] Fusion095  label="pcbScrewPillars"
  Placement = pos=(-3.2,-1,72.3) rot=(0,0,1;0rad)
  Shapes = -> [Cut045,Extrude054]
FEATURE [Part::Feature] Face113
  shape: bbox 3.2 x 1.5 x 2e-07 mm, 1 faces, 0 solids (baked)
FEATURE [Part::Revolution] Revolve121  label="backCaseScrewRetainer002"
  Angle = 360
  Axis = (0,1,0)
  Base = (0,0,0)
  FaceMakerClass = Part::FaceMakerBullseye
  Placement = pos=(12.5,3,62) rot=(0,0,1;0rad)
  Solid = false
  Source = -> Face113
  Symmetric = false
FEATURE [Part::Feature] Face114
  shape: bbox 3.2 x 1.5 x 2e-07 mm, 1 faces, 0 solids (baked)
FEATURE [Part::Feature] Face115
  shape: bbox 3.2 x 1.5 x 2e-07 mm, 1 faces, 0 solids (baked)
FEATURE [Part::Feature] Face116
  shape: bbox 3.2 x 1.5 x 2e-07 mm, 1 faces, 0 solids (baked)
FEATURE [Part::Revolution] Revolve122  label="frontCaseScrewRetainer004"
  Angle = 360
  Axis = (0,1,0)
  Base = (0,0,0)
  FaceMakerClass = Part::FaceMakerBullseye
  Placement = pos=(89.5,3,68.5) rot=(0,0,1;0rad)
  Solid = false
  Source = -> Face115
  Symmetric = false
FEATURE [Part::Revolution] Revolve123  label="frontCaseScrewRetainer005"
  Angle = 360
  Axis = (0,1,0)
  Base = (0,0,0)
  FaceMakerClass = Part::FaceMakerBullseye
  Placement = pos=(89.5,3,3.5) rot=(0,0,1;0rad)
  Solid = false
  Source = -> Face116
  Symmetric = false
FEATURE [Part::Revolution] Revolve124  label="backCaseScrewRetainer003"
  Angle = 360
  Axis = (0,1,0)
  Base = (0,0,0)
  FaceMakerClass = Part::FaceMakerBullseye
  Placement = pos=(12.5,3,10) rot=(0,0,1;0rad)
  Solid = false
  Source = -> Face114
  Symmetric = false
FEATURE [Part::Feature] Face117
  shape: bbox 3.6 x 3.2 x 2e-07 mm, 1 faces, 0 solids (baked)
FEATURE [Part::Revolution] Revolve125  label="moreFrontCaseScrewRetainer004"
  Angle = 360
  Axis = (0,1,0)
  Base = (0,0,0)
  FaceMakerClass = Part::FaceMakerBullseye
  Placement = pos=(109.5,4.5,68.5) rot=(0,0,1;0rad)
  Solid = false
  Source = -> Face117
  Symmetric = false
FEATURE [Part::Feature] Face118
  shape: bbox 3.6 x 3.2 x 2e-07 mm, 1 faces, 0 solids (baked)
FEATURE [Part::Revolution] Revolve126  label="moreFrontCaseScrewRetainer005"
  Angle = 360
  Axis = (0,1,0)
  Base = (0,0,0)
  FaceMakerClass = Part::FaceMakerBullseye
  Placement = pos=(109.5,4.5,3.5) rot=(0,0,1;0rad)
  Solid = false
  Source = -> Face118
  Symmetric = false
FEATURE [Part::MultiFuse] Fusion096  label="screwRetainers001"
  Shapes = -> [Revolve126,Revolve125,Revolve124,Revolve123,Revolve122,Revolve121]
FEATURE [Part::Feature] Face119
  shape: bbox 10 x 16.5 x 2e-07 mm, 1 faces, 0 solids (baked)
FEATURE [Part::Revolution] Revolve130  label="plugHousing050"
  Angle = 360
  Axis = (0,1,0)
  Base = (0,0,0)
  FaceMakerClass = Part::FaceMakerBullseye
  Placement = pos=(0,0,36.15) rot=(0,0,1;0rad)
  Solid = false
  Source = -> Face119
  Symmetric = false
FEATURE [Part::Feature] Face120
  shape: bbox 10 x 16.5 x 2e-07 mm, 1 faces, 0 solids (baked)
FEATURE [Part::Feature] Face121
  shape: bbox 10 x 16.5 x 2e-07 mm, 1 faces, 0 solids (baked)
FEATURE [Part::Revolution] Revolve127  label="plugHousing047"
  Angle = 360
  Axis = (0,1,0)
  Base = (0,0,0)
  FaceMakerClass = Part::FaceMakerBullseye
  Placement = pos=(0,0,36.15) rot=(0,0,1;0rad)
  Solid = false
  Source = -> Face121
  Symmetric = false
FEATURE [Part::Feature] Face122
  shape: bbox 10 x 16.5 x 2e-07 mm, 1 faces, 0 solids (baked)
FEATURE [Part::Feature] Face123
  shape: bbox 10 x 16.5 x 2e-07 mm, 1 faces, 0 solids (baked)
FEATURE [Part::Revolution] Revolve128  label="plugHousing048"
  Angle = 360
  Axis = (0,1,0)
  Base = (0,0,0)
  FaceMakerClass = Part::FaceMakerBullseye
  Placement = pos=(0,0,36.15) rot=(0,0,1;0rad)
  Solid = false
  Source = -> Face123
  Symmetric = false
FEATURE [Part::MultiFuse] Fusion100  label="plugHousing054"
  Placement = pos=(0,0,0) rot=(0,0,1;1.5708rad)
  Shapes = -> [Revolve130,Revolve128]
FEATURE [Part::Feature] Face124
  shape: bbox 10 x 16.5 x 2e-07 mm, 1 faces, 0 solids (baked)
FEATURE [Part::Feature] Face125
  shape: bbox 10 x 16.5 x 2e-07 mm, 1 faces, 0 solids (baked)
FEATURE [Part::Revolution] Revolve129  label="plugHousing049"
  Angle = 360
  Axis = (0,1,0)
  Base = (0,0,0)
  FaceMakerClass = Part::FaceMakerBullseye
  Placement = pos=(0,0,36.15) rot=(0,0,1;0rad)
  Solid = false
  Source = -> Face125
  Symmetric = false
FEATURE [Part::Feature] Face126
  shape: bbox 10 x 16.5 x 2e-07 mm, 1 faces, 0 solids (baked)
FEATURE [Part::Revolution] Revolve131  label="plugHousing058"
  Angle = 360
  Axis = (0,1,0)
  Base = (0,0,0)
  FaceMakerClass = Part::FaceMakerBullseye
  Placement = pos=(0,0,36.15) rot=(0,0,1;0rad)
  Solid = false
  Source = -> Face120
  Symmetric = false
FEATURE [Part::MultiFuse] Fusion099  label="plugHousing053"
  Placement = pos=(0,0,0) rot=(0,0,1;1.5708rad)
  Shapes = -> [Revolve127,Revolve131]
FEATURE [Part::MultiFuse] Fusion102  label="plugHousing056"
  Placement = pos=(0,19,0) rot=(0,0,1;3.14159rad)
  Shapes = -> [Fusion100,Fusion099]
FEATURE [Part::Revolution] Revolve132  label="plugHousing059"
  Angle = 360
  Axis = (0,1,0)
  Base = (0,0,0)
  FaceMakerClass = Part::FaceMakerBullseye
  Placement = pos=(0,0,36.15) rot=(0,0,1;0rad)
  Solid = false
  Source = -> Face126
  Symmetric = false
FEATURE [Part::Revolution] Revolve133  label="plugHousing060"
  Angle = 360
  Axis = (0,1,0)
  Base = (0,0,0)
  FaceMakerClass = Part::FaceMakerBullseye
  Placement = pos=(0,0,36.15) rot=(0,0,1;0rad)
  Solid = false
  Source = -> Face122
  Symmetric = false
FEATURE [Part::MultiFuse] Fusion097  label="plugHousing051"
  Placement = pos=(0,0,0) rot=(0,0,1;1.5708rad)
  Shapes = -> [Revolve133,Revolve132]
FEATURE [Part::Revolution] Revolve134  label="plugHousing061"
  Angle = 360
  Axis = (0,1,0)
  Base = (0,0,0)
  FaceMakerClass = Part::FaceMakerBullseye
  Placement = pos=(0,0,36.15) rot=(0,0,1;0rad)
  Solid = false
  Source = -> Face124
  Symmetric = false
FEATURE [Part::MultiFuse] Fusion101  label="plugHousing055"
  Placement = pos=(0,0,0) rot=(0,0,1;1.5708rad)
  Shapes = -> [Revolve129,Revolve134]
FEATURE [Part::MultiFuse] Fusion098  label="plugHousing052"
  Placement = pos=(0,19,0) rot=(0,0,1;3.14159rad)
  Shapes = -> [Fusion097,Fusion101]
FEATURE [Part::MultiFuse] Fusion103  label="plugHousing057"
  Placement = pos=(122.621,0,-0.15) rot=(0,0,1;0rad)
  Shapes = -> [Fusion102,Fusion098]
FEATURE [Part::Box] Box028  label="Cube015"
  AttacherType = Attacher::AttachEngine3D
  Height = 28
  Length = 3
  Placement = pos=(110.7,19,22) rot=(0,0,1;0rad)
  Width = 15.7
FEATURE [Part::Cylinder] Cylinder044
  Angle = 360
  AttacherType = Attacher::AttachEngine3D
  Height = 20
  Placement = pos=(0,0,36.15) rot=(0,0,1;0rad)
  Radius = 10.3
FEATURE [Part::Cylinder] Cylinder045
  Angle = 360
  AttacherType = Attacher::AttachEngine3D
  Height = 10
  Placement = pos=(0,0,36.15) rot=(0,0,1;0rad)
  Radius = 4
FEATURE [Part::MultiFuse] Fusion104  label="removeToCreteHoleForPlugHousing040"
  Placement = pos=(70,19,36) rot=(0,1,0;1.5708rad)
  Shapes = -> [Cylinder044,Cylinder045]
FEATURE [Part::Cut] Cut046  label="plugHousingTab003"
  Base = -> Box028
  Tool = -> Fusion104
FEATURE [Part::MultiFuse] Fusion105  label="plugHousing062"
  Shapes = -> [Fusion103,Cut046]
FEATURE [Part::Fillet] Fillet042
  Base = -> Fusion105
  Edges = 1 edges r=2: [Edge25]
FEATURE [Part::Fillet] Fillet043  label="plugHousing063"
  Base = -> Fillet042
  Edges = 1 edges r=2: [Edge8]
  Placement = pos=(7,0,0) rot=(0,0,1;0rad)
FEATURE [Part::Feature] Face127
  shape: bbox 10 x 16.5 x 2e-07 mm, 1 faces, 0 solids (baked)
FEATURE [Part::Feature] Face128
  shape: bbox 10 x 16.5 x 2e-07 mm, 1 faces, 0 solids (baked)
FEATURE [Part::Revolution] Revolve137  label="plugHousing070"
  Angle = 360
  Axis = (0,1,0)
  Base = (0,0,0)
  FaceMakerClass = Part::FaceMakerBullseye
  Placement = pos=(0,0,36.15) rot=(0,0,1;0rad)
  Solid = false
  Source = -> Face127
  Symmetric = false
FEATURE [Part::Revolution] Revolve140  label="plugHousing073"
  Angle = 360
  Axis = (0,1,0)
  Base = (0,0,0)
  FaceMakerClass = Part::FaceMakerBullseye
  Placement = pos=(0,0,36.15) rot=(0,0,1;0rad)
  Solid = false
  Source = -> Face128
  Symmetric = false
FEATURE [Part::Feature] Face129
  shape: bbox 10 x 16.5 x 2e-07 mm, 1 faces, 0 solids (baked)
FEATURE [Part::Revolution] Revolve138  label="plugHousing071"
  Angle = 360
  Axis = (0,1,0)
  Base = (0,0,0)
  FaceMakerClass = Part::FaceMakerBullseye
  Placement = pos=(0,0,36.15) rot=(0,0,1;0rad)
  Solid = false
  Source = -> Face129
  Symmetric = false
FEATURE [Part::Feature] Face130
  shape: bbox 10 x 16.5 x 2e-07 mm, 1 faces, 0 solids (baked)
FEATURE [Part::Revolution] Revolve139  label="plugHousing072"
  Angle = 360
  Axis = (0,1,0)
  Base = (0,0,0)
  FaceMakerClass = Part::FaceMakerBullseye
  Placement = pos=(0,0,36.15) rot=(0,0,1;0rad)
  Solid = false
  Source = -> Face130
  Symmetric = false
FEATURE [Part::Feature] Face131
  shape: bbox 10 x 16.5 x 2e-07 mm, 1 faces, 0 solids (baked)
FEATURE [Part::Revolution] Revolve135  label="plugHousing068"
  Angle = 360
  Axis = (0,1,0)
  Base = (0,0,0)
  FaceMakerClass = Part::FaceMakerBullseye
  Placement = pos=(0,0,36.15) rot=(0,0,1;0rad)
  Solid = false
  Source = -> Face131
  Symmetric = false
FEATURE [Part::MultiFuse] Fusion112  label="plugHousing078"
  Placement = pos=(0,0,0) rot=(0,0,1;1.5708rad)
  Shapes = -> [Revolve135,Revolve139]
FEATURE [Part::Feature] Face132
  shape: bbox 10 x 16.5 x 2e-07 mm, 1 faces, 0 solids (baked)
FEATURE [Part::Revolution] Revolve141  label="plugHousing074"
  Angle = 360
  Axis = (0,1,0)
  Base = (0,0,0)
  FaceMakerClass = Part::FaceMakerBullseye
  Placement = pos=(0,0,36.15) rot=(0,0,1;0rad)
  Solid = false
  Source = -> Face132
  Symmetric = false
FEATURE [Part::MultiFuse] Fusion110  label="plugHousing076"
  Placement = pos=(0,0,0) rot=(0,0,1;1.5708rad)
  Shapes = -> [Revolve141,Revolve140]
FEATURE [Part::Feature] Face133
  shape: bbox 10 x 16.5 x 2e-07 mm, 1 faces, 0 solids (baked)
FEATURE [Part::Revolution] Revolve136  label="plugHousing069"
  Angle = 360
  Axis = (0,1,0)
  Base = (0,0,0)
  FaceMakerClass = Part::FaceMakerBullseye
  Placement = pos=(0,0,36.15) rot=(0,0,1;0rad)
  Solid = false
  Source = -> Face133
  Symmetric = false
FEATURE [Part::MultiFuse] Fusion106  label="plugHousing064"
  Placement = pos=(0,0,0) rot=(0,0,1;1.5708rad)
  Shapes = -> [Revolve138,Revolve136]
FEATURE [Part::MultiFuse] Fusion108  label="plugHousing066"
  Placement = pos=(0,19,0) rot=(0,0,1;3.14159rad)
  Shapes = -> [Fusion106,Fusion112]
FEATURE [Part::Feature] Face134
  shape: bbox 10 x 16.5 x 2e-07 mm, 1 faces, 0 solids (baked)
FEATURE [Part::Revolution] Revolve142  label="plugHousing075"
  Angle = 360
  Axis = (0,1,0)
  Base = (0,0,0)
  FaceMakerClass = Part::FaceMakerBullseye
  Placement = pos=(0,0,36.15) rot=(0,0,1;0rad)
  Solid = false
  Source = -> Face134
  Symmetric = false
FEATURE [Part::MultiFuse] Fusion107  label="plugHousing065"
  Placement = pos=(0,0,0) rot=(0,0,1;1.5708rad)
  Shapes = -> [Revolve137,Revolve142]
FEATURE [Part::MultiFuse] Fusion111  label="plugHousing077"
  Placement = pos=(0,19,0) rot=(0,0,1;3.14159rad)
  Shapes = -> [Fusion110,Fusion107]
FEATURE [Part::MultiFuse] Fusion109  label="plugHousing067"
  Placement = pos=(131.236,0,-0.15) rot=(0,0,1;0rad)
  Shapes = -> [Fusion108,Fusion111]
FEATURE [Part::MultiFuse] Fusion113  label="plugHousing079"
  Shapes = -> [Fillet043,Fusion109]
FEATURE [Part::Feature] Face135
  shape: bbox 3.5 x 17.8 x 2e-07 mm, 1 faces, 0 solids (baked)
FEATURE [Part::Revolution] Revolve143  label="removeToCreateScrewAndThreadedInsertHole049"
  Angle = 360
  Axis = (0,1,0)
  Base = (0,0,0)
  FaceMakerClass = Part::FaceMakerBullseye
  Placement = pos=(12.5,0,10) rot=(0,0,1;0rad)
  Solid = false
  Source = -> Face135
  Symmetric = false
FEATURE [Part::Feature] Face136
  shape: bbox 3.5 x 17.8 x 2e-07 mm, 1 faces, 0 solids (baked)
FEATURE [Part::Revolution] Revolve144  label="removeToCreateScrewAndThreadedInsertHole050"
  Angle = 360
  Axis = (0,1,0)
  Base = (0,0,0)
  FaceMakerClass = Part::FaceMakerBullseye
  Placement = pos=(12.5,0,62) rot=(0,0,1;0rad)
  Solid = false
  Source = -> Face136
  Symmetric = false
FEATURE [Part::Feature] Face137
  shape: bbox 3.5 x 17.8 x 2e-07 mm, 1 faces, 0 solids (baked)
FEATURE [Part::Revolution] Revolve145  label="removeToCreateScrewAndThreadedInsertHole051"
  Angle = 360
  Axis = (0,1,0)
  Base = (0,0,0)
  FaceMakerClass = Part::FaceMakerBullseye
  Placement = pos=(89.5,0,68.5) rot=(0,0,1;0rad)
  Solid = false
  Source = -> Face137
  Symmetric = false
FEATURE [Part::Feature] Face138
  shape: bbox 3.5 x 17.8 x 2e-07 mm, 1 faces, 0 solids (baked)
FEATURE [Part::Revolution] Revolve146  label="removeToCreateScrewAndThreadedInsertHole052"
  Angle = 360
  Axis = (0,1,0)
  Base = (0,0,0)
  FaceMakerClass = Part::FaceMakerBullseye
  Placement = pos=(89.5,0,3.5) rot=(0,0,1;0rad)
  Solid = false
  Source = -> Face138
  Symmetric = false
FEATURE [Part::Feature] Face139
  shape: bbox 3.5 x 17.8 x 2e-07 mm, 1 faces, 0 solids (baked)
FEATURE [Part::Revolution] Revolve147  label="removeToCreateScrewAndThreadedInsertHole053"
  Angle = 360
  Axis = (0,1,0)
  Base = (0,0,0)
  FaceMakerClass = Part::FaceMakerBullseye
  Placement = pos=(109.5,4.7,3.5) rot=(0,0,1;0rad)
  Solid = false
  Source = -> Face139
  Symmetric = false
FEATURE [Part::Feature] Face140
  shape: bbox 3.5 x 17.8 x 2e-07 mm, 1 faces, 0 solids (baked)
FEATURE [Part::Revolution] Revolve148  label="removeToCreateScrewAndThreadedInsertHole054"
  Angle = 360
  Axis = (0,1,0)
  Base = (0,0,0)
  FaceMakerClass = Part::FaceMakerBullseye
  Placement = pos=(109.5,4.7,68.5) rot=(0,0,1;0rad)
  Solid = false
  Source = -> Face140
  Symmetric = false
FEATURE [Part::MultiFuse] Fusion114  label="removeToCreateScrewAndThreadedInsertHole055"
  Shapes = -> [Revolve148,Revolve147,Revolve146,Revolve145,Revolve144,Revolve143]
FEATURE [Part::Cut] Cut047  label="casePillars004"
  Base = -> Cut037
  Tool = -> Fusion114
FEATURE [Part::Feature] Face141
  shape: bbox 3.5 x 17.8 x 2e-07 mm, 1 faces, 0 solids (baked)
FEATURE [Part::Feature] Face142
  shape: bbox 3.5 x 17.8 x 2e-07 mm, 1 faces, 0 solids (baked)
FEATURE [Part::Feature] Face143
  shape: bbox 3.5 x 17.8 x 2e-07 mm, 1 faces, 0 solids (baked)
FEATURE [Part::Revolution] Revolve149  label="removeToCreateScrewAndThreadedInsertHole057"
  Angle = 360
  Axis = (0,1,0)
  Base = (0,0,0)
  FaceMakerClass = Part::FaceMakerBullseye
  Placement = pos=(12.5,0,10) rot=(0,0,1;0rad)
  Solid = false
  Source = -> Face141
  Symmetric = false
FEATURE [Part::Feature] Face144
  shape: bbox 3.5 x 17.8 x 2e-07 mm, 1 faces, 0 solids (baked)
FEATURE [Part::Feature] Face145
  shape: bbox 3.5 x 17.8 x 2e-07 mm, 1 faces, 0 solids (baked)
FEATURE [Part::Feature] Face146
  shape: bbox 3.5 x 17.8 x 2e-07 mm, 1 faces, 0 solids (baked)
FEATURE [Part::Revolution] Revolve150  label="removeToCreateScrewAndThreadedInsertHole058"
  Angle = 360
  Axis = (0,1,0)
  Base = (0,0,0)
  FaceMakerClass = Part::FaceMakerBullseye
  Placement = pos=(12.5,0,62) rot=(0,0,1;0rad)
  Solid = false
  Source = -> Face146
  Symmetric = false
FEATURE [Part::Revolution] Revolve151  label="removeToCreateScrewAndThreadedInsertHole059"
  Angle = 360
  Axis = (0,1,0)
  Base = (0,0,0)
  FaceMakerClass = Part::FaceMakerBullseye
  Placement = pos=(89.5,0,68.5) rot=(0,0,1;0rad)
  Solid = false
  Source = -> Face143
  Symmetric = false
FEATURE [Part::Revolution] Revolve152  label="removeToCreateScrewAndThreadedInsertHole060"
  Angle = 360
  Axis = (0,1,0)
  Base = (0,0,0)
  FaceMakerClass = Part::FaceMakerBullseye
  Placement = pos=(89.5,0,3.5) rot=(0,0,1;0rad)
  Solid = false
  Source = -> Face142
  Symmetric = false
FEATURE [Part::Revolution] Revolve153  label="removeToCreateScrewAndThreadedInsertHole061"
  Angle = 360
  Axis = (0,1,0)
  Base = (0,0,0)
  FaceMakerClass = Part::FaceMakerBullseye
  Placement = pos=(109.5,4.7,3.5) rot=(0,0,1;0rad)
  Solid = false
  Source = -> Face145
  Symmetric = false
FEATURE [Part::Revolution] Revolve154  label="removeToCreateScrewAndThreadedInsertHole062"
  Angle = 360
  Axis = (0,1,0)
  Base = (0,0,0)
  FaceMakerClass = Part::FaceMakerBullseye
  Placement = pos=(109.5,4.7,68.5) rot=(0,0,1;0rad)
  Solid = false
  Source = -> Face144
  Symmetric = false
FEATURE [Part::MultiFuse] Fusion115  label="removeToCreateScrewAndThreadedInsertHole056"
  Shapes = -> [Revolve154,Revolve153,Revolve152,Revolve151,Revolve150,Revolve149]
FEATURE [Part::Feature] Face147
  shape: bbox 9.8 x 26.5 x 2e-07 mm, 1 faces, 0 solids (baked)
FEATURE [Part::Revolution] Revolve155
  Angle = 360
  Axis = (0,1,0)
  Base = (0,0,0)
  FaceMakerClass = Part::FaceMakerBullseye
  Placement = pos=(0,0,0) rot=(0,0,1;1.5708rad)
  Solid = false
  Source = -> Face147
  Symmetric = false
FEATURE [Part::Feature] Face148
  shape: bbox 9.8 x 26.5 x 2e-07 mm, 1 faces, 0 solids (baked)
FEATURE [Part::Revolution] Revolve156
  Angle = 360
  Axis = (0,1,0)
  Base = (0,0,0)
  FaceMakerClass = Part::FaceMakerBullseye
  Placement = pos=(0,0,0) rot=(0,0,1;1.5708rad)
  Solid = false
  Source = -> Face148
  Symmetric = false
FEATURE [Part::MultiFuse] Fusion116
  Placement = pos=(-18,19,36) rot=(0,0,1;0rad)
  Shapes = -> [Revolve156,Revolve155]
FEATURE [Part::Box] Box029  label="Cube016"
  AttacherType = Attacher::AttachEngine3D
  Height = 28
  Length = 3
  Placement = pos=(110.7,19,22) rot=(0,0,1;0rad)
  Width = 15.7
FEATURE [Part::Cylinder] Cylinder046
  Angle = 360
  AttacherType = Attacher::AttachEngine3D
  Height = 10
  Placement = pos=(0,0,36.15) rot=(0,0,1;0rad)
  Radius = 4
FEATURE [Part::Cylinder] Cylinder047
  Angle = 360
  AttacherType = Attacher::AttachEngine3D
  Height = 20
  Placement = pos=(0,0,36.15) rot=(0,0,1;0rad)
  Radius = 10.3
FEATURE [Part::MultiFuse] Fusion117  label="removeToCreteHoleForPlugHousing041"
  Placement = pos=(70,19,36) rot=(0,1,0;1.5708rad)
  Shapes = -> [Cylinder047,Cylinder046]
FEATURE [Part::Cut] Cut049  label="plugHousingTab004"
  Base = -> Box029
  Placement = pos=(-107.4,-14,0) rot=(0,0,1;0rad)
  Tool = -> Fusion117
FEATURE [Part::Box] Box030  label="Cube017"
  AttacherType = Attacher::AttachEngine3D
  Height = 28
  Length = 3
  Placement = pos=(110.7,19,22) rot=(0,0,1;0rad)
  Width = 15.7
FEATURE [Part::Cylinder] Cylinder048
  Angle = 360
  AttacherType = Attacher::AttachEngine3D
  Height = 10
  Placement = pos=(0,0,36.15) rot=(0,0,1;0rad)
  Radius = 4
FEATURE [Part::Cylinder] Cylinder049
  Angle = 360
  AttacherType = Attacher::AttachEngine3D
  Height = 20
  Placement = pos=(0,0,36.15) rot=(0,0,1;0rad)
  Radius = 10.3
FEATURE [Part::MultiFuse] Fusion118  label="removeToCreteHoleForPlugHousing042"
  Placement = pos=(70,19,36) rot=(0,1,0;1.5708rad)
  Shapes = -> [Cylinder049,Cylinder048]
FEATURE [Part::Cut] Cut050  label="plugHousingTab005"
  Base = -> Box030
  Placement = pos=(-107.4,-14,0) rot=(0,0,1;0rad)
  Tool = -> Fusion118
FEATURE [Part::MultiFuse] Fusion119
  Placement = pos=(9.6,23,0) rot=(0,0,1;3.14159rad)
  Shapes = -> [Cut049,Cut050]
FEATURE [Part::Box] Box031  label="Cube018"
  AttacherType = Attacher::AttachEngine3D
  Height = 10
  Length = 3
  Placement = pos=(3.3,4,12) rot=(0,0,1;0rad)
  Width = 10
FEATURE [Part::Fillet] Fillet044
  Base = -> Box031
  Edges = 1 edges r=2: [Edge11]
FEATURE [Part::Box] Box032  label="Cube019"
  AttacherType = Attacher::AttachEngine3D
  Height = 10
  Length = 3
  Placement = pos=(3.3,4,50) rot=(0,0,1;0rad)
  Width = 10
FEATURE [Part::Fillet] Fillet045
  Base = -> Box032
  Edges = 1 edges r=2: [Edge12]
FEATURE [Part::Box] Box033  label="Cube020"
  AttacherType = Attacher::AttachEngine3D
  Height = 28
  Length = 4
  Placement = pos=(5,0,22) rot=(0,0,1;0rad)
  Width = 10
FEATURE [Part::Fillet] Fillet046
  Base = -> Box033
  Edges = 1 edges r=1: [Edge7]
FEATURE [Part::Fillet] Fillet047
  Base = -> Fillet046
  Edges = 1 edges r=2: [Edge5]
FEATURE [Part::Fillet] Fillet048
  Base = -> Fillet047
  Edges = 1 edges r=2: [Edge2]
FEATURE [Part::Cylinder] Cylinder050
  Angle = 360
  AttacherType = Attacher::AttachEngine3D
  Height = 20
  Placement = pos=(0,0,36.15) rot=(0,0,1;0rad)
  Radius = 8.2
FEATURE [Part::Cylinder] Cylinder051
  Angle = 360
  AttacherType = Attacher::AttachEngine3D
  Height = 10
  Placement = pos=(0,0,36.15) rot=(0,0,1;0rad)
  Radius = 4
FEATURE [Part::MultiFuse] Fusion120  label="removeToCreteHoleForPlugHousing043"
  Placement = pos=(-42,19,36) rot=(0,1,0;1.5708rad)
  Shapes = -> [Cylinder050,Cylinder051]
FEATURE [Sketcher::SketchObject] Sketch067  label="topSketch018"
  FullyConstrained = true
  sketch-geometry (4):
    g0: LineSegment StartX=16.8446 StartY=31.512 StartZ=0 EndX=16.3251 EndY=34.4666 EndZ=0
    g1: ArcOfCircle CenterX=19 CenterY=19.2524 CenterZ=0 NormalX=0 NormalY=0 NormalZ=1 AngleXU=0 Radius=15.4476 StartAngle=1.74483 EndAngle=2.72717
    g2: ArcOfCircle CenterX=19 CenterY=19.2524 CenterZ=0 NormalX=0 NormalY=0 NormalZ=1 AngleXU=0 Radius=12.4476 StartAngle=1.74483 EndAngle=2.73189
    g3: LineSegment StartX=4.86004 StartY=25.4725 StartZ=0 EndX=7.58253 EndY=24.2107 EndZ=0
  constraints (7):
    c: Block(g0)
    c: Coincident(g1,g0)
    c: Coincident(g2,g0)
    c: Coincident(g3,g1)
    c: Coincident(g3,g2)
    c: Block(g1)
    c: Block(g2)
FEATURE [Part::Extrusion] Extrude058
  Base = -> Sketch067
  Dir = (0,0,1)
  DirMode = 2
  FaceMakerClass = Part::FaceMakerBullseye
  LengthFwd = 10
  LengthRev = 0
  Placement = pos=(0,0,31) rot=(0,0,1;0rad)
  Solid = true
  Symmetric = false
FEATURE [Part::Cut] Cut051
  Base = -> Extrude058
  Tool = -> Fusion120
FEATURE [Part::Fillet] Fillet049
  Base = -> Cut051
  Edges = 1 edges r=2: [Edge1]
FEATURE [Part::Fillet] Fillet050
  Base = -> Fillet049
  Edges = 1 edges r=2.5: [Edge1]
FEATURE [Part::Fillet] Fillet051
  Base = -> Fillet050
  Edges = 1 edges r=2.5: [Edge2]
FEATURE [Part::MultiFuse] Fusion121  label="wireHolder003"
  Shapes = -> [Fusion116,Fillet051]
FEATURE [Part::MultiFuse] Fusion122
  Shapes = -> [Fillet045,Fusion121]
FEATURE [Part::MultiFuse] Fusion123  label="wireHolder004"
  Shapes = -> [Fusion122,Fillet048]
FEATURE [Part::MultiFuse] Fusion124  label="wireHolder005"
  Shapes = -> [Fillet044,Fusion119,Fusion123]
FEATURE [Sketcher::SketchObject] Sketch068  label="topSketch019"
  FullyConstrained = true
  sketch-geometry (6):
    g0: LineSegment StartX=19 StartY=38 StartZ=0 EndX=117 EndY=38 EndZ=0
    g1: ArcOfCircle CenterX=19 CenterY=19 CenterZ=0 NormalX=0 NormalY=0 NormalZ=1 AngleXU=0 Radius=19 StartAngle=1.5708 EndAngle=3.14159
    g2: LineSegment StartX=117 StartY=38 StartZ=0 EndX=117 EndY=19 EndZ=0
    g3: LineSegment StartX=98 StartY=1.0161e-12 StartZ=0 EndX=5.22862e-06 EndY=1.0161e-12 EndZ=0
    g4: LineSegment StartX=5.22862e-06 StartY=19 StartZ=0 EndX=5.22862e-06 EndY=1.0161e-12 EndZ=0
    g5: ArcOfCircle CenterX=98 CenterY=19 CenterZ=0 NormalX=0 NormalY=0 NormalZ=1 AngleXU=0 Radius=19 StartAngle=4.71239 EndAngle=6.28319
  constraints (16):
    c: Horizontal(g0)
    c: Distance(g0) = 98
    c: Coincident(g1,g0)
    c: Block(g1)
    c: Coincident(g2,g0)
    c: Vertical(g2)
    c: Distance(g2) = 19
    c: Horizontal(g3)
    c: Coincident(g4,g1)
    c: Vertical(g4)
    c: Coincident(g3,g4)
    c: Block(g3)
    c: Coincident(g5,g2)
    c: Coincident(g5,g3)
    c: Block(g0)
    c: Block(g5)
FEATURE [Part::Extrusion] Extrude059  label="sideA002"
  Base = -> Sketch068
  Dir = (0,0,1)
  DirMode = 2
  FaceMakerClass = Part::FaceMakerBullseye
  LengthFwd = 3
  LengthRev = 0
  Placement = pos=(0,0,-2.7) rot=(0,0,1;0rad)
  Solid = true
  Symmetric = false
FEATURE [Sketcher::SketchObject] Sketch069  label="topSketch020"
  FullyConstrained = true
  sketch-geometry (6):
    g0: LineSegment StartX=19 StartY=38 StartZ=0 EndX=117 EndY=38 EndZ=0
    g1: ArcOfCircle CenterX=19 CenterY=19 CenterZ=0 NormalX=0 NormalY=0 NormalZ=1 AngleXU=0 Radius=19 StartAngle=1.5708 EndAngle=3.14159
    g2: LineSegment StartX=117 StartY=38 StartZ=0 EndX=117 EndY=19 EndZ=0
    g3: LineSegment StartX=98 StartY=1.0161e-12 StartZ=0 EndX=5.22862e-06 EndY=1.0161e-12 EndZ=0
    g4: LineSegment StartX=5.22862e-06 StartY=19 StartZ=0 EndX=5.22862e-06 EndY=1.0161e-12 EndZ=0
    g5: ArcOfCircle CenterX=98 CenterY=19 CenterZ=0 NormalX=0 NormalY=0 NormalZ=1 AngleXU=0 Radius=19 StartAngle=4.71239 EndAngle=6.28319
  constraints (16):
    c: Horizontal(g0)
    c: Distance(g0) = 98
    c: Coincident(g1,g0)
    c: Block(g1)
    c: Coincident(g2,g0)
    c: Vertical(g2)
    c: Distance(g2) = 19
    c: Horizontal(g3)
    c: Coincident(g4,g1)
    c: Vertical(g4)
    c: Coincident(g3,g4)
    c: Block(g3)
    c: Coincident(g5,g2)
    c: Coincident(g5,g3)
    c: Block(g0)
    c: Block(g5)
FEATURE [Part::Extrusion] Extrude060  label="sideB002"
  Base = -> Sketch069
  Dir = (0,0,1)
  DirMode = 2
  FaceMakerClass = Part::FaceMakerBullseye
  LengthFwd = 3
  LengthRev = 0
  Placement = pos=(0,0,71.7) rot=(0,0,1;0rad)
  Solid = true
  Symmetric = false
FEATURE [Part::MultiFuse] Fusion127  label="removeFromBottom001"
  Placement = pos=(2,0,0) rot=(0,0,1;0rad)
  Shapes = -> [Extrude059,Extrude060]
FEATURE [Part::Cylinder] Cylinder052
  Angle = 360
  AttacherType = Attacher::AttachEngine3D
  Height = 20
  Placement = pos=(0,0,36.15) rot=(0,0,1;0rad)
  Radius = 14
FEATURE [Part::Cylinder] Cylinder053
  Angle = 360
  AttacherType = Attacher::AttachEngine3D
  Height = 10
  Placement = pos=(0,0,36.15) rot=(0,0,1;0rad)
  Radius = 4
FEATURE [Part::MultiFuse] Fusion128  label="removeToCreteHoleForPlugHousing044"
  Placement = pos=(70,19,36) rot=(0,1,0;1.5708rad)
  Shapes = -> [Cylinder052,Cylinder053]
FEATURE [Part::Cut] Cut052  label="bottom011"
  Base = -> Extrude043
  Tool = -> Fusion128
FEATURE [Part::Cut] Cut054  label="bottom012"
  Base = -> Cut052
  Tool = -> Fusion115
FEATURE [Sketcher::SketchObject] Sketch070
  FullyConstrained = true
  Placement = pos=(117,19,0) rot=(0.57735,0.57735,0.57735;2.0944rad)
  sketch-geometry (48):
    g0: LineSegment StartX=-49.19 StartY=69.25 StartZ=0 EndX=-49.19 EndY=66.25 EndZ=0
    g1: LineSegment StartX=-49.19 StartY=63.5 StartZ=0 EndX=-49.19 EndY=60.5 EndZ=0
    g2: LineSegment StartX=-49.19 StartY=57.75 StartZ=0 EndX=-49.19 EndY=54.75 EndZ=0
    g3: LineSegment StartX=-49.19 StartY=52 StartZ=0 EndX=-49.19 EndY=49 EndZ=0
    g4: LineSegment StartX=-49.19 StartY=46.25 StartZ=0 EndX=-49.19 EndY=43.25 EndZ=0
    g5: LineSegment StartX=-49.19 StartY=40.5 StartZ=0 EndX=-49.19 EndY=37.5 EndZ=0
    g6: LineSegment StartX=-49.19 StartY=34.5 StartZ=0 EndX=-49.19 EndY=31.5 EndZ=0
    g7: LineSegment StartX=-49.19 StartY=28.75 StartZ=0 EndX=-49.19 EndY=25.75 EndZ=0
    g8: LineSegment StartX=-49.19 StartY=23 StartZ=0 EndX=-49.19 EndY=20 EndZ=0
    g9: LineSegment StartX=-49.19 StartY=17.25 StartZ=0 EndX=-49.19 EndY=14.25 EndZ=0
    g10: LineSegment StartX=-49.19 StartY=11.5 StartZ=0 EndX=-49.19 EndY=8.5 EndZ=0
    g11: LineSegment StartX=-49.19 StartY=5.75 StartZ=0 EndX=-49.19 EndY=2.75 EndZ=0
    g12: ArcOfCircle CenterX=-1.5 CenterY=67.75 CenterZ=0 NormalX=0 NormalY=0 NormalZ=1 AngleXU=0 Radius=1.5 StartAngle=4.71239 EndAngle=7.85398
    g13: ArcOfCircle CenterX=-1.5 CenterY=62 CenterZ=0 NormalX=0 NormalY=0 NormalZ=1 AngleXU=0 Radius=1.5 StartAngle=4.71239 EndAngle=7.85398
    g14: ArcOfCircle CenterX=-1.5 CenterY=56.25 CenterZ=0 NormalX=0 NormalY=0 NormalZ=1 AngleXU=0 Radius=1.5 StartAngle=4.71239 EndAngle=7.85398
    g15: ArcOfCircle CenterX=-11.49 CenterY=50.5 CenterZ=0 NormalX=0 NormalY=0 NormalZ=1 AngleXU=0 Radius=1.5 StartAngle=4.71239 EndAngle=7.85398
    g16: ArcOfCircle CenterX=-16.28 CenterY=44.75 CenterZ=0 NormalX=0 NormalY=0 NormalZ=1 AngleXU=0 Radius=1.5 StartAngle=4.71239 EndAngle=7.85398
    g17: ArcOfCircle CenterX=-18.2337 CenterY=39 CenterZ=0 NormalX=0 NormalY=0 NormalZ=1 AngleXU=0 Radius=1.5 StartAngle=4.71485 EndAngle=7.85398
    g18: ArcOfCircle CenterX=-16.2837 CenterY=27.25 CenterZ=0 NormalX=0 NormalY=0 NormalZ=1 AngleXU=0 Radius=1.5 StartAngle=4.71485 EndAngle=7.85398
    g19: ArcOfCircle CenterX=-18.2337 CenterY=33 CenterZ=0 NormalX=0 NormalY=0 NormalZ=1 AngleXU=0 Radius=1.5 StartAngle=4.71485 EndAngle=7.85398
    g20: ArcOfCircle CenterX=-11.49 CenterY=21.5 CenterZ=0 NormalX=0 NormalY=0 NormalZ=1 AngleXU=0 Radius=1.5 StartAngle=4.71239 EndAngle=7.85398
    g21: ArcOfCircle CenterX=-1.5 CenterY=4.25 CenterZ=0 NormalX=0 NormalY=0 NormalZ=1 AngleXU=0 Radius=1.5 StartAngle=4.71239 EndAngle=7.85398
    g22: ArcOfCircle CenterX=-1.5 CenterY=10 CenterZ=0 NormalX=0 NormalY=0 NormalZ=1 AngleXU=0 Radius=1.5 StartAngle=4.71239 EndAngle=7.85398
    g23: ArcOfCircle CenterX=-1.5 CenterY=15.75 CenterZ=0 NormalX=0 NormalY=0 NormalZ=1 AngleXU=0 Radius=1.5 StartAngle=4.71239 EndAngle=7.85398
    g24: LineSegment StartX=-49.19 StartY=69.25 StartZ=0 EndX=-1.5 EndY=69.25 EndZ=0
    g25: LineSegment StartX=-49.19 StartY=66.25 StartZ=0 EndX=-1.5 EndY=66.25 EndZ=0
    g26: LineSegment StartX=-49.19 StartY=63.5 StartZ=0 EndX=-1.5 EndY=63.5 EndZ=0
    g27: LineSegment StartX=-49.19 StartY=60.5 StartZ=0 EndX=-1.5 EndY=60.5 EndZ=0
    g28: LineSegment StartX=-49.19 StartY=57.75 StartZ=0 EndX=-1.5 EndY=57.75 EndZ=0
    g29: LineSegment StartX=-49.19 StartY=54.75 StartZ=0 EndX=-1.5 EndY=54.75 EndZ=0
    g30: LineSegment StartX=-49.19 StartY=52 StartZ=0 EndX=-11.49 EndY=52 EndZ=0
    g31: LineSegment StartX=-49.19 StartY=49 StartZ=0 EndX=-11.49 EndY=49 EndZ=0
    g32: LineSegment StartX=-49.19 StartY=46.25 StartZ=0 EndX=-16.28 EndY=46.25 EndZ=0
    g33: LineSegment StartX=-49.19 StartY=43.25 StartZ=0 EndX=-16.28 EndY=43.25 EndZ=0
    g34: LineSegment StartX=-49.19 StartY=40.5 StartZ=0 EndX=-18.2337 EndY=40.5 EndZ=0
    g35: LineSegment StartX=-49.19 StartY=37.5 StartZ=0 EndX=-18.23 EndY=37.5 EndZ=0
    g36: LineSegment StartX=-49.19 StartY=34.5 StartZ=0 EndX=-18.2337 EndY=34.5 EndZ=0
    g37: LineSegment StartX=-49.19 StartY=31.5 StartZ=0 EndX=-18.23 EndY=31.5 EndZ=0
    g38: LineSegment StartX=-49.19 StartY=28.75 StartZ=0 EndX=-16.2837 EndY=28.75 EndZ=0
    g39: LineSegment StartX=-49.19 StartY=25.75 StartZ=0 EndX=-16.28 EndY=25.75 EndZ=0
    g40: LineSegment StartX=-49.19 StartY=23 StartZ=0 EndX=-11.49 EndY=23 EndZ=0
    g41: LineSegment StartX=-49.19 StartY=20 StartZ=0 EndX=-11.49 EndY=20 EndZ=0
    g42: LineSegment StartX=-49.19 StartY=17.25 StartZ=0 EndX=-1.5 EndY=17.25 EndZ=0
    g43: LineSegment StartX=-49.19 StartY=14.25 StartZ=0 EndX=-1.5 EndY=14.25 EndZ=0
    g44: LineSegment StartX=-49.19 StartY=11.5 StartZ=0 EndX=-1.5 EndY=11.5 EndZ=0
    g45: LineSegment StartX=-49.19 StartY=8.5 StartZ=0 EndX=-1.5 EndY=8.5 EndZ=0
    g46: LineSegment StartX=-49.19 StartY=5.75 StartZ=0 EndX=-1.5 EndY=5.75 EndZ=0
    g47: LineSegment StartX=-49.19 StartY=2.75 StartZ=0 EndX=-1.5 EndY=2.75 EndZ=0
  constraints (120):
    c: Vertical(g0)
    c: Distance(g0) = 3
    c: Block(g0)
    c: Vertical(g1)
    c: Distance(g1) = 3
    c: Vertical(g2)
    c: Equal(g0,g2) = 3
    c: Block(g2)
    c: Vertical(g3)
    c: Equal(g1,g3) = 3
    c: Vertical(g4)
    c: Equal(g0,g4) = 3
    c: Block(g4)
    c: Vertical(g5)
    c: Equal(g1,g5) = 3
    c: Vertical(g6)
    c: Equal(g0,g6) = 3
    c: Block(g6)
    c: Vertical(g7)
    c: Equal(g1,g7) = 3
    c: Vertical(g8)
    c: Equal(g0,g8) = 3
    c: Block(g8)
    c: Vertical(g9)
    c: Equal(g1,g9) = 3
    c: Vertical(g10)
    c: Equal(g0,g10) = 3
    c: Block(g10)
    c: Vertical(g11)
    c: Equal(g1,g11) = 3
    c: Block(g12)
    c: Block(g13)
    c: Block(g14)
    c: Block(g15)
    c: Block(g16)
    c: Block(g17)
    c: Block(g18)
    c: Block(g19)
    c: Block(g20)
    c: Block(g21)
    c: Block(g22)
    c: Block(g23)
    c: Block(g11)
    c: Block(g9)
    c: Block(g7)
    c: Block(g5)
    c: Block(g3)
    c: Block(g1)
    c: Coincident(g24,g0)
    c: Coincident(g24,g12)
    c: Horizontal(g24)
    c: Coincident(g25,g0)
    c: Coincident(g25,g12)
    c: Horizontal(g25)
    c: Coincident(g26,g1)
    c: Coincident(g26,g13)
    c: Horizontal(g26)
    c: Coincident(g27,g1)
    c: Coincident(g27,g13)
    c: Horizontal(g27)
    c: Coincident(g28,g2)
    c: Coincident(g28,g14)
    c: Horizontal(g28)
    c: Coincident(g29,g2)
    c: Coincident(g29,g14)
    c: Horizontal(g29)
    c: Coincident(g30,g3)
    c: Coincident(g30,g15)
    c: Horizontal(g30)
    c: Coincident(g31,g3)
    c: Coincident(g31,g15)
    c: Horizontal(g31)
    c: Coincident(g32,g4)
    c: Coincident(g32,g16)
    c: Horizontal(g32)
    c: Coincident(g33,g4)
    c: Coincident(g33,g16)
    c: Horizontal(g33)
    c: Coincident(g34,g5)
    c: Coincident(g34,g17)
    c: Horizontal(g34)
    c: Coincident(g35,g5)
    c: Coincident(g35,g17)
    c: Horizontal(g35)
    c: Coincident(g36,g6)
    c: Coincident(g36,g19)
    c: Horizontal(g36)
    c: Coincident(g37,g6)
    c: Coincident(g37,g19)
    c: Horizontal(g37)
    c: Coincident(g38,g7)
    c: Coincident(g38,g18)
    c: Horizontal(g38)
    c: Coincident(g39,g7)
    c: Coincident(g39,g18)
    c: Horizontal(g39)
    c: Coincident(g40,g8)
    c: Coincident(g40,g20)
    c: Horizontal(g40)
    c: Coincident(g41,g8)
    c: Coincident(g41,g20)
    c: Horizontal(g41)
    c: Coincident(g42,g9)
    c: Coincident(g42,g23)
    c: Horizontal(g42)
    c: Coincident(g43,g9)
    c: Coincident(g43,g23)
    c: Horizontal(g43)
    c: Coincident(g44,g10)
    c: Coincident(g44,g22)
    c: Horizontal(g44)
    c: Coincident(g45,g10)
    c: Coincident(g45,g22)
    c: Horizontal(g45)
    c: Coincident(g46,g11)
    c: Coincident(g46,g21)
    c: Horizontal(g46)
    c: Coincident(g47,g11)
    c: Coincident(g47,g21)
    c: Horizontal(g47)
FEATURE [Part::Extrusion] Extrude061
  Base = -> Sketch070
  Dir = (1,0,0)
  DirMode = 2
  FaceMakerClass = Part::FaceMakerBullseye
  LengthFwd = 23
  LengthRev = 0
  Placement = pos=(-19,0,0) rot=(0,0,1;0rad)
  Solid = true
  Symmetric = false
FEATURE [Part::Fillet] Fillet052  label="removeToCreateVentalationHoles002"
  Base = -> Extrude061
  Edges = <same value as first occurrence — deduplicated (x6 in doc)>
  Placement = pos=(7,0.02,0) rot=(0,0,1;0rad)
FEATURE [Part::MultiFuse] Fusion130  label="bottom013"
  Shapes = -> [Cut054,Cut034]
FEATURE [Part::Cut] Cut055
  Base = -> Fusion130
  Tool = -> Fillet052
FEATURE [Part::Cylinder] Cylinder054
  Angle = 360
  AttacherType = Attacher::AttachEngine3D
  Height = 20
  Placement = pos=(0,0,36.15) rot=(0,0,1;0rad)
  Radius = 4
FEATURE [Sketcher::SketchObject] Sketch071  label="bottomSketch002"
  FullyConstrained = true
  sketch-geometry (32):
    g0: LineSegment StartX=3.3 StartY=-6.03275e-07 StartZ=0 EndX=98 EndY=-6.03275e-07 EndZ=0
    g1: ArcOfCircle CenterX=98 CenterY=19 CenterZ=0 NormalX=0 NormalY=0 NormalZ=1 AngleXU=0 Radius=19 StartAngle=4.71239 EndAngle=5.71103
    g2: LineSegment StartX=6.3 StartY=8 StartZ=0 EndX=3.3 EndY=8 EndZ=0
    g3: LineSegment StartX=3.3 StartY=8 StartZ=0 EndX=3.3 EndY=-6.03275e-07 EndZ=0
    g4: ArcOfCircle CenterX=8.3 CenterY=5 CenterZ=0 NormalX=0 NormalY=0 NormalZ=1 AngleXU=0 Radius=2 StartAngle=3.14159 EndAngle=4.71239
    g5: LineSegment StartX=6.3 StartY=8 StartZ=0 EndX=6.3 EndY=5 EndZ=0
    g6: ArcOfCircle CenterX=98 CenterY=19 CenterZ=0 NormalX=0 NormalY=0 NormalZ=1 AngleXU=0 Radius=12.7 StartAngle=4.71239 EndAngle=6.28319
    g7: LineSegment StartX=94.7 StartY=3 StartZ=0 EndX=8.3 EndY=3 EndZ=0
    g8-g12: Circle x5 (B-spline internal-alignment scaffolding for g13; pole/knot coordinates omitted)
    g13: BSplineCurve PolesCount=5 KnotsCount=3 Degree=3 IsPeriodic=0
    g14: GeomPoint X=98 Y=6.3 Z=0
    g15: GeomPoint X=96.3938 Y=4.71946 Z=0
    g16: GeomPoint X=94.7 Y=3 Z=0
    g17-g23: Circle x7 (B-spline internal-alignment scaffolding for g24; pole/knot coordinates omitted)
    g24: BSplineCurve PolesCount=7 KnotsCount=5 Degree=3 IsPeriodic=0
    g25-g29: GeomPoint x5 (B-spline internal-alignment scaffolding for g24; pole/knot coordinates omitted)
    g30: ArcOfCircle CenterX=98 CenterY=19 CenterZ=0 NormalX=0 NormalY=0 NormalZ=1 AngleXU=0 Radius=15.7 StartAngle=5.81226 EndAngle=6.28319
    g31: LineSegment StartX=110.7 StartY=19 StartZ=0 EndX=113.7 EndY=19 EndZ=0
  constraints (41):
    c: Horizontal(g0)
    c: Coincident(g1,g0)
    c: Block(g1)
    c: Horizontal(g2)
    c: Distance(g2) = 3
    c: Coincident(g3,g2)
    c: Vertical(g3)
    c: Coincident(g3,g0)
    c: Block(g4)
    c: Block(g2)
    c: Coincident(g5,g2)
    c: Coincident(g5,g4)
    c: Vertical(g5)
    c: Coincident(g6,g1)
    c: Block(g6)
    c: Coincident(g7,g4)
    c: Horizontal(g7)
    c: Block(g0)
    c: Block(g7)
    c: Block(g3)
    c: Coincident(g13,g6)
    c: Weight(g8) = 1
    c: Equal(g8, g9-g12) x4
    c: Coincident(g13,g7)
    c: InternalAlignment(g8-g12 -> g13) x5
    c: InternalAlignment(g14,g13)
    c: InternalAlignment(g15,g13)
    c: InternalAlignment(g16,g13)
    c: Block(g13)
    c: Weight(g17) = 1
    c: Equal(g17, g18-g23) x6
    c: Coincident(g24,g1)
    c: InternalAlignment(g17-g23 -> g24) x7
    c: InternalAlignment(g25-g29 -> g24) x5
    c: Block(g24)
    c: Coincident(g30,g24)
    c: Coincident(g31,g6)
    c: Coincident(g31,g30)
    c: Horizontal(g31)
    c: Block(g31)
    c: Block(g30)
FEATURE [Part::Extrusion] Extrude062  label="bottom014"
  Base = -> Sketch071
  Dir = (0,0,1)
  DirMode = 2
  FaceMakerClass = Part::FaceMakerBullseye
  LengthFwd = 71.4
  LengthRev = 0
  Placement = pos=(0,0,0.3) rot=(0,0,1;0rad)
  Solid = true
  Symmetric = false
FEATURE [Part::Fillet] Fillet054
  Base = -> Extrude062
  Edges = 1 edges r=2.4: [Edge17]
FEATURE [Part::Fillet] Fillet055  label="bottom015"
  Base = -> Fillet054
  Edges = 1 edges r=2.4: [Edge36]
FEATURE [Part::Cylinder] Cylinder055
  Angle = 360
  AttacherType = Attacher::AttachEngine3D
  Height = 10
  Placement = pos=(0,0,36.15) rot=(0,0,1;0rad)
  Radius = 4
FEATURE [Part::MultiFuse] Fusion131  label="removeToCreateHoleForPlugHousing002"
  Placement = pos=(70,19,36.15) rot=(0,1,0;1.5708rad)
  Shapes = -> [Cylinder054,Cylinder055]
FEATURE [Part::Cut] Cut056  label="Bottom001"
  Base = -> Fillet055
  Placement = pos=(9,0,0) rot=(0,0,1;0rad)
  Tool = -> Fusion131
FEATURE [Part::Cut] Cut057
  Base = -> Cut055
  Tool = -> Cut056
FEATURE [Sketcher::SketchObject] Sketch072  label="topSketch021"
  FullyConstrained = true
  sketch-geometry (4):
    g0: ArcOfCircle CenterX=105 CenterY=19 CenterZ=0 NormalX=0 NormalY=0 NormalZ=1 AngleXU=0 Radius=20.6155 StartAngle=5.54125 EndAngle=6.28319
    g1: ArcOfCircle CenterX=105 CenterY=19 CenterZ=0 NormalX=0 NormalY=0 NormalZ=1 AngleXU=0 Radius=13 StartAngle=5.54125 EndAngle=6.28319
    g2: LineSegment StartX=118 StartY=19 StartZ=0 EndX=125.616 EndY=19 EndZ=0
    g3: LineSegment StartX=114.583 StartY=10.2157 StartZ=0 EndX=120.197 EndY=5.06982 EndZ=0
  constraints (7):
    c: Block(g0)
    c: Block(g1)
    c: Coincident(g2,g1)
    c: Coincident(g2,g0)
    c: Horizontal(g2)
    c: Coincident(g3,g1)
    c: Coincident(g3,g0)
FEATURE [Part::Extrusion] Extrude063  label="bottomPlugHousingBit003"
  Base = -> Sketch072
  Dir = (0,0,1)
  DirMode = 2
  FaceMakerClass = Part::FaceMakerBullseye
  LengthFwd = 72
  LengthRev = 0
  Solid = true
  Symmetric = false
FEATURE [Part::Cylinder] Cylinder056
  Angle = 360
  AttacherType = Attacher::AttachEngine3D
  Height = 20
  Placement = pos=(0,0,36.15) rot=(0,0,1;0rad)
  Radius = 14.3
FEATURE [Part::Cylinder] Cylinder057
  Angle = 360
  AttacherType = Attacher::AttachEngine3D
  Height = 10
  Placement = pos=(0,0,36.15) rot=(0,0,1;0rad)
  Radius = 4
FEATURE [Part::Box] Box034  label="removeToCreteHoleForPlugHousing047"
  AttacherType = Attacher::AttachEngine3D
  Height = 28.6
  Length = 20
  Placement = pos=(106.15,0,21.7) rot=(0,0,1;0rad)
  Width = 19
FEATURE [Part::Cylinder] Cylinder058
  Angle = 360
  AttacherType = Attacher::AttachEngine3D
  Height = 20
  Placement = pos=(0,0,36.15) rot=(0,0,1;0rad)
  Radius = 14.3
FEATURE [Part::Cylinder] Cylinder059
  Angle = 360
  AttacherType = Attacher::AttachEngine3D
  Height = 10
  Placement = pos=(0,0,36.15) rot=(0,0,1;0rad)
  Radius = 4
FEATURE [Part::MultiFuse] Fusion134  label="removeToCreteHoleForPlugHousing046"
  Placement = pos=(70,19,36) rot=(0,1,0;1.5708rad)
  Shapes = -> [Cylinder058,Cylinder059]
FEATURE [Part::Cylinder] Cylinder060
  Angle = 360
  AttacherType = Attacher::AttachEngine3D
  Height = 20
  Placement = pos=(0,0,36.15) rot=(0,0,1;0rad)
  Radius = 14
FEATURE [Part::Cylinder] Cylinder061
  Angle = 360
  AttacherType = Attacher::AttachEngine3D
  Height = 10
  Placement = pos=(0,0,36.15) rot=(0,0,1;0rad)
  Radius = 4
FEATURE [Part::MultiFuse] Fusion135  label="removeToCreteHoleForPlugHousing048"
  Placement = pos=(70,19,36) rot=(0,1,0;1.5708rad)
  Shapes = -> [Cylinder060,Cylinder061]
FEATURE [Part::Box] Box035  label="removeToCreteHoleForPlugHousing049"
  AttacherType = Attacher::AttachEngine3D
  Height = 28.6
  Length = 20
  Placement = pos=(106.15,0,21.7) rot=(0,0,1;0rad)
  Width = 19
FEATURE [Part::MultiFuse] Fusion133  label="removeToCreteHoleForPlugHousing045"
  Placement = pos=(0,0,-28.3) rot=(0,0,1;0rad)
  Shapes = -> [Box035,Fusion134]
FEATURE [Part::MultiFuse] Fusion138  label="removeToCreteHoleForPlugHousing051"
  Placement = pos=(70,19,36) rot=(0,1,0;1.5708rad)
  Shapes = -> [Cylinder056,Cylinder057]
FEATURE [Part::MultiFuse] Fusion137  label="removeToCreteHoleForPlugHousing050"
  Placement = pos=(0,0,28.3) rot=(0,0,1;0rad)
  Shapes = -> [Box034,Fusion138]
FEATURE [Part::MultiFuse] Fusion132  label="removeToCreatePlugHousingBottomBit002"
  Shapes = -> [Fusion133,Fusion137]
FEATURE [Part::MultiFuse] Fusion136  label="removeToCreatePlugHousingBottomBit003"
  Shapes = -> [Fusion135,Fusion132]
FEATURE [Part::Cut] Cut058  label="bottomPlugHousingBit002"
  Base = -> Extrude063
  Placement = pos=(-0.09,0,0) rot=(0,0,1;0rad)
  Tool = -> Fusion136
FEATURE [Sketcher::SketchObject] Sketch073  label="bottomSketch003"
  FullyConstrained = true
  sketch-geometry (45):
    g0: LineSegment StartX=6.29999 StartY=8 StartZ=0 EndX=3.29999 EndY=8 EndZ=0
    g1: LineSegment StartX=3.29999 StartY=8 StartZ=0 EndX=3.29999 EndY=-6.03275e-07 EndZ=0
    g2: ArcOfCircle CenterX=8.29999 CenterY=5 CenterZ=0 NormalX=0 NormalY=0 NormalZ=1 AngleXU=0 Radius=2 StartAngle=3.14159 EndAngle=4.71239
    g3: LineSegment StartX=6.29999 StartY=8 StartZ=0 EndX=6.29999 EndY=5 EndZ=0
    g4: ArcOfCircle CenterX=105 CenterY=19 CenterZ=0 NormalX=0 NormalY=0 NormalZ=1 AngleXU=0 Radius=12.7 StartAngle=4.71239 EndAngle=5.94289
    g5-g11: Circle x7 (B-spline internal-alignment scaffolding for g12; pole/knot coordinates omitted)
    g12: BSplineCurve PolesCount=7 KnotsCount=5 Degree=3 IsPeriodic=0
    g13-g17: GeomPoint x5 (B-spline internal-alignment scaffolding for g12; pole/knot coordinates omitted)
    g18: ArcOfCircle CenterX=105 CenterY=19 CenterZ=0 NormalX=0 NormalY=0 NormalZ=1 AngleXU=0 Radius=15.7 StartAngle=5.81226 EndAngle=6.28319
    g19: BSplineCurve PolesCount=5 KnotsCount=3 Degree=3 IsPeriodic=0
    g20: LineSegment StartX=8.29999 StartY=3 StartZ=0 EndX=101.7 EndY=3 EndZ=0
    g21: LineSegment StartX=3.29999 StartY=-6.03275e-07 StartZ=0 EndX=105 EndY=-6.03275e-07 EndZ=0
    g22: LineSegment StartX=120.974 StartY=8.71251 StartZ=0 EndX=122.332 EndY=7.83778 EndZ=0
    g23: LineSegment StartX=105 StartY=-6.03274e-07 StartZ=0 EndX=113 EndY=-6.03274e-07 EndZ=0
    g24: ArcOfCircle CenterX=105 CenterY=19 CenterZ=0 NormalX=0 NormalY=0 NormalZ=1 AngleXU=0 Radius=20.6155 StartAngle=5.11091 EndAngle=5.71103
    g25: ArcOfCircle CenterX=117.7 CenterY=19 CenterZ=0 NormalX=0 NormalY=0 NormalZ=1 AngleXU=0 Radius=3 StartAngle=1.2e-15 EndAngle=2.10468
    g26: Circle CenterX=116.345 CenterY=16.3232 CenterZ=0 NormalX=0 NormalY=0 NormalZ=1 AngleXU=0 Radius=1
    g27: Circle CenterX=117.24 CenterY=15.7584 CenterZ=0 NormalX=0 NormalY=0 NormalZ=1 AngleXU=0 Radius=1
    g28: Circle CenterX=116.972 CenterY=14.7612 CenterZ=0 NormalX=0 NormalY=0 NormalZ=1 AngleXU=0 Radius=1
    g29: BSplineCurve PolesCount=3 KnotsCount=2 Degree=2 IsPeriodic=0
    g30: GeomPoint X=116.345 Y=16.3232 Z=0
    g31: GeomPoint X=116.972 Y=14.7612 Z=0
    g32: Circle CenterX=115.828 CenterY=17.157 CenterZ=0 NormalX=0 NormalY=0 NormalZ=1 AngleXU=0 Radius=1
    g33: Circle CenterX=115.841 CenterY=16.639 CenterZ=0 NormalX=0 NormalY=0 NormalZ=1 AngleXU=0 Radius=1
    g34: Circle CenterX=116.345 CenterY=16.3232 CenterZ=0 NormalX=0 NormalY=0 NormalZ=1 AngleXU=0 Radius=1
    g35: BSplineCurve PolesCount=3 KnotsCount=2 Degree=2 IsPeriodic=0
    g36: GeomPoint X=115.828 Y=17.157 Z=0
    g37: GeomPoint X=116.345 Y=16.3232 Z=0
    g38: LineSegment StartX=115.828 StartY=17.157 StartZ=0 EndX=115.828 EndY=20.8307 EndZ=0
    g39: Circle CenterX=115.828 CenterY=20.8307 CenterZ=0 NormalX=0 NormalY=0 NormalZ=1 AngleXU=0 Radius=1
    g40: Circle CenterX=115.831 CenterY=21.3396 CenterZ=0 NormalX=0 NormalY=0 NormalZ=1 AngleXU=0 Radius=1
    g41: Circle CenterX=116.173 CenterY=21.5825 CenterZ=0 NormalX=0 NormalY=0 NormalZ=1 AngleXU=0 Radius=1
    g42: BSplineCurve PolesCount=3 KnotsCount=2 Degree=2 IsPeriodic=0
    g43: GeomPoint X=115.828 Y=20.8307 Z=0
    g44: GeomPoint X=116.173 Y=21.5825 Z=0
  constraints (70):
    c: Horizontal(g0)
    c: Distance(g0) = 3
    c: Coincident(g1,g0)
    c: Vertical(g1)
    c: Block(g2)
    c: Block(g0)
    c: Coincident(g3,g0)
    c: Coincident(g3,g2)
    c: Vertical(g3)
    c: Block(g1)
    c: Block(g4)
    c: Coincident(g19,g4)
    c: Block(g19)
    c: Equal(g5, g6-g11) x6
    c: InternalAlignment(g5-g11 -> g12) x7
    c: InternalAlignment(g13-g17 -> g12) x5
    c: Block(g12)
    c: Coincident(g18,g12)
    c: Block(g18)
    c: Coincident(g20,g2)
    c: Coincident(g20,g19)
    c: Horizontal(g20)
    c: Distance(g20) = 93.4
    c: Coincident(g21,g1)
    c: Horizontal(g21)
    c: Distance(g21) = 101.7
    c: Horizontal(g23)
    c: Distance(g23) = 8
    c: Coincident(g24,g23)
    c: Block(g23)
    c: Coincident(g22,g24)
    c: Block(g24)
    c: Block(g22)
    c: Distance(g22) = 1.61553
    c: Coincident(g25,g18)
    c: Block(g25)
    c: Weight(g26) = 1
    c: Equal(g26,g27)
    c: Equal(g26,g28)
    c: Coincident(g29,g4)
    c: InternalAlignment(g26,g29)
    c: InternalAlignment(g27,g29)
    c: InternalAlignment(g28,g29)
    c: InternalAlignment(g30,g29)
    c: InternalAlignment(g31,g29)
    c: Block(g29)
    c: Weight(g32) = 1
    c: Equal(g32,g33)
    c: Equal(g32,g34)
    c: Coincident(g35,g29)
    c: InternalAlignment(g32,g35)
    c: InternalAlignment(g33,g35)
    c: InternalAlignment(g34,g35)
    c: InternalAlignment(g36,g35)
    c: InternalAlignment(g37,g35)
    c: Block(g35)
    c: Coincident(g38,g35)
    c: Vertical(g38)
    c: Block(g38)
    c: Coincident(g42,g38)
    c: Weight(g39) = 1
    c: Equal(g39,g40)
    c: Equal(g39,g41)
    c: Coincident(g42,g25)
    c: InternalAlignment(g39,g42)
    c: InternalAlignment(g40,g42)
    c: InternalAlignment(g41,g42)
    c: InternalAlignment(g43,g42)
    c: InternalAlignment(g44,g42)
    c: Block(g42)
FEATURE [Part::Extrusion] Extrude064  label="bottom016"
  Base = -> Sketch073
  Dir = (0,0,1)
  DirMode = 2
  FaceMakerClass = Part::FaceMakerBullseye
  LengthFwd = 71.4
  LengthRev = 0
  Placement = pos=(0,0,0.3) rot=(0,0,1;0rad)
  Solid = true
  Symmetric = false
FEATURE [Part::Revolution] Revolve157  label="removeToCreateScrewAndThreadedInsertHole063"
  Angle = 360
  Axis = (0,1,0)
  Base = (0,0,0)
  FaceMakerClass = Part::FaceMakerBullseye
  Placement = pos=(12.5,0,10) rot=(0,0,1;0rad)
  Solid = false
  Source = -> Face141
  Symmetric = false
FEATURE [Sketcher::SketchObject] Sketch074
  FullyConstrained = true
  Placement = pos=(117,19,0) rot=(0.57735,0.57735,0.57735;2.0944rad)
  sketch-geometry (48):
    g0: LineSegment StartX=-49.19 StartY=69.25 StartZ=0 EndX=-49.19 EndY=66.25 EndZ=0
    g1: LineSegment StartX=-49.19 StartY=63.5 StartZ=0 EndX=-49.19 EndY=60.5 EndZ=0
    g2: LineSegment StartX=-49.19 StartY=57.75 StartZ=0 EndX=-49.19 EndY=54.75 EndZ=0
    g3: LineSegment StartX=-49.19 StartY=52 StartZ=0 EndX=-49.19 EndY=49 EndZ=0
    g4: LineSegment StartX=-49.19 StartY=46.25 StartZ=0 EndX=-49.19 EndY=43.25 EndZ=0
    g5: LineSegment StartX=-49.19 StartY=40.5 StartZ=0 EndX=-49.19 EndY=37.5 EndZ=0
    g6: LineSegment StartX=-49.19 StartY=34.5 StartZ=0 EndX=-49.19 EndY=31.5 EndZ=0
    g7: LineSegment StartX=-49.19 StartY=28.75 StartZ=0 EndX=-49.19 EndY=25.75 EndZ=0
    g8: LineSegment StartX=-49.19 StartY=23 StartZ=0 EndX=-49.19 EndY=20 EndZ=0
    g9: LineSegment StartX=-49.19 StartY=17.25 StartZ=0 EndX=-49.19 EndY=14.25 EndZ=0
    g10: LineSegment StartX=-49.19 StartY=11.5 StartZ=0 EndX=-49.19 EndY=8.5 EndZ=0
    g11: LineSegment StartX=-49.19 StartY=5.75 StartZ=0 EndX=-49.19 EndY=2.75 EndZ=0
    g12: ArcOfCircle CenterX=-1.5 CenterY=67.75 CenterZ=0 NormalX=0 NormalY=0 NormalZ=1 AngleXU=0 Radius=1.5 StartAngle=4.71239 EndAngle=7.85398
    g13: ArcOfCircle CenterX=-1.5 CenterY=62 CenterZ=0 NormalX=0 NormalY=0 NormalZ=1 AngleXU=0 Radius=1.5 StartAngle=4.71239 EndAngle=7.85398
    g14: ArcOfCircle CenterX=-1.5 CenterY=56.25 CenterZ=0 NormalX=0 NormalY=0 NormalZ=1 AngleXU=0 Radius=1.5 StartAngle=4.71239 EndAngle=7.85398
    g15: ArcOfCircle CenterX=-11.49 CenterY=50.5 CenterZ=0 NormalX=0 NormalY=0 NormalZ=1 AngleXU=0 Radius=1.5 StartAngle=4.71239 EndAngle=7.85398
    g16: ArcOfCircle CenterX=-16.28 CenterY=44.75 CenterZ=0 NormalX=0 NormalY=0 NormalZ=1 AngleXU=0 Radius=1.5 StartAngle=4.71239 EndAngle=7.85398
    g17: ArcOfCircle CenterX=-18.2337 CenterY=39 CenterZ=0 NormalX=0 NormalY=0 NormalZ=1 AngleXU=0 Radius=1.5 StartAngle=4.71485 EndAngle=7.85398
    g18: ArcOfCircle CenterX=-16.2837 CenterY=27.25 CenterZ=0 NormalX=0 NormalY=0 NormalZ=1 AngleXU=0 Radius=1.5 StartAngle=4.71485 EndAngle=7.85398
    g19: ArcOfCircle CenterX=-18.2337 CenterY=33 CenterZ=0 NormalX=0 NormalY=0 NormalZ=1 AngleXU=0 Radius=1.5 StartAngle=4.71485 EndAngle=7.85398
    g20: ArcOfCircle CenterX=-11.49 CenterY=21.5 CenterZ=0 NormalX=0 NormalY=0 NormalZ=1 AngleXU=0 Radius=1.5 StartAngle=4.71239 EndAngle=7.85398
    g21: ArcOfCircle CenterX=-1.5 CenterY=4.25 CenterZ=0 NormalX=0 NormalY=0 NormalZ=1 AngleXU=0 Radius=1.5 StartAngle=4.71239 EndAngle=7.85398
    g22: ArcOfCircle CenterX=-1.5 CenterY=10 CenterZ=0 NormalX=0 NormalY=0 NormalZ=1 AngleXU=0 Radius=1.5 StartAngle=4.71239 EndAngle=7.85398
    g23: ArcOfCircle CenterX=-1.5 CenterY=15.75 CenterZ=0 NormalX=0 NormalY=0 NormalZ=1 AngleXU=0 Radius=1.5 StartAngle=4.71239 EndAngle=7.85398
    g24: LineSegment StartX=-49.19 StartY=69.25 StartZ=0 EndX=-1.5 EndY=69.25 EndZ=0
    g25: LineSegment StartX=-49.19 StartY=66.25 StartZ=0 EndX=-1.5 EndY=66.25 EndZ=0
    g26: LineSegment StartX=-49.19 StartY=63.5 StartZ=0 EndX=-1.5 EndY=63.5 EndZ=0
    g27: LineSegment StartX=-49.19 StartY=60.5 StartZ=0 EndX=-1.5 EndY=60.5 EndZ=0
    g28: LineSegment StartX=-49.19 StartY=57.75 StartZ=0 EndX=-1.5 EndY=57.75 EndZ=0
    g29: LineSegment StartX=-49.19 StartY=54.75 StartZ=0 EndX=-1.5 EndY=54.75 EndZ=0
    g30: LineSegment StartX=-49.19 StartY=52 StartZ=0 EndX=-11.49 EndY=52 EndZ=0
    g31: LineSegment StartX=-49.19 StartY=49 StartZ=0 EndX=-11.49 EndY=49 EndZ=0
    g32: LineSegment StartX=-49.19 StartY=46.25 StartZ=0 EndX=-16.28 EndY=46.25 EndZ=0
    g33: LineSegment StartX=-49.19 StartY=43.25 StartZ=0 EndX=-16.28 EndY=43.25 EndZ=0
    g34: LineSegment StartX=-49.19 StartY=40.5 StartZ=0 EndX=-18.2337 EndY=40.5 EndZ=0
    g35: LineSegment StartX=-49.19 StartY=37.5 StartZ=0 EndX=-18.23 EndY=37.5 EndZ=0
    g36: LineSegment StartX=-49.19 StartY=34.5 StartZ=0 EndX=-18.2337 EndY=34.5 EndZ=0
    g37: LineSegment StartX=-49.19 StartY=31.5 StartZ=0 EndX=-18.23 EndY=31.5 EndZ=0
    g38: LineSegment StartX=-49.19 StartY=28.75 StartZ=0 EndX=-16.2837 EndY=28.75 EndZ=0
    g39: LineSegment StartX=-49.19 StartY=25.75 StartZ=0 EndX=-16.28 EndY=25.75 EndZ=0
    g40: LineSegment StartX=-49.19 StartY=23 StartZ=0 EndX=-11.49 EndY=23 EndZ=0
    g41: LineSegment StartX=-49.19 StartY=20 StartZ=0 EndX=-11.49 EndY=20 EndZ=0
    g42: LineSegment StartX=-49.19 StartY=17.25 StartZ=0 EndX=-1.5 EndY=17.25 EndZ=0
    g43: LineSegment StartX=-49.19 StartY=14.25 StartZ=0 EndX=-1.5 EndY=14.25 EndZ=0
    g44: LineSegment StartX=-49.19 StartY=11.5 StartZ=0 EndX=-1.5 EndY=11.5 EndZ=0
    g45: LineSegment StartX=-49.19 StartY=8.5 StartZ=0 EndX=-1.5 EndY=8.5 EndZ=0
    g46: LineSegment StartX=-49.19 StartY=5.75 StartZ=0 EndX=-1.5 EndY=5.75 EndZ=0
    g47: LineSegment StartX=-49.19 StartY=2.75 StartZ=0 EndX=-1.5 EndY=2.75 EndZ=0
  constraints (120):
    c: Vertical(g0)
    c: Distance(g0) = 3
    c: Block(g0)
    c: Vertical(g1)
    c: Distance(g1) = 3
    c: Vertical(g2)
    c: Equal(g0,g2) = 3
    c: Block(g2)
    c: Vertical(g3)
    c: Equal(g1,g3) = 3
    c: Vertical(g4)
    c: Equal(g0,g4) = 3
    c: Block(g4)
    c: Vertical(g5)
    c: Equal(g1,g5) = 3
    c: Vertical(g6)
    c: Equal(g0,g6) = 3
    c: Block(g6)
    c: Vertical(g7)
    c: Equal(g1,g7) = 3
    c: Vertical(g8)
    c: Equal(g0,g8) = 3
    c: Block(g8)
    c: Vertical(g9)
    c: Equal(g1,g9) = 3
    c: Vertical(g10)
    c: Equal(g0,g10) = 3
    c: Block(g10)
    c: Vertical(g11)
    c: Equal(g1,g11) = 3
    c: Block(g12)
    c: Block(g13)
    c: Block(g14)
    c: Block(g15)
    c: Block(g16)
    c: Block(g17)
    c: Block(g18)
    c: Block(g19)
    c: Block(g20)
    c: Block(g21)
    c: Block(g22)
    c: Block(g23)
    c: Block(g11)
    c: Block(g9)
    c: Block(g7)
    c: Block(g5)
    c: Block(g3)
    c: Block(g1)
    c: Coincident(g24,g0)
    c: Coincident(g24,g12)
    c: Horizontal(g24)
    c: Coincident(g25,g0)
    c: Coincident(g25,g12)
    c: Horizontal(g25)
    c: Coincident(g26,g1)
    c: Coincident(g26,g13)
    c: Horizontal(g26)
    c: Coincident(g27,g1)
    c: Coincident(g27,g13)
    c: Horizontal(g27)
    c: Coincident(g28,g2)
    c: Coincident(g28,g14)
    c: Horizontal(g28)
    c: Coincident(g29,g2)
    c: Coincident(g29,g14)
    c: Horizontal(g29)
    c: Coincident(g30,g3)
    c: Coincident(g30,g15)
    c: Horizontal(g30)
    c: Coincident(g31,g3)
    c: Coincident(g31,g15)
    c: Horizontal(g31)
    c: Coincident(g32,g4)
    c: Coincident(g32,g16)
    c: Horizontal(g32)
    c: Coincident(g33,g4)
    c: Coincident(g33,g16)
    c: Horizontal(g33)
    c: Coincident(g34,g5)
    c: Coincident(g34,g17)
    c: Horizontal(g34)
    c: Coincident(g35,g5)
    c: Coincident(g35,g17)
    c: Horizontal(g35)
    c: Coincident(g36,g6)
    c: Coincident(g36,g19)
    c: Horizontal(g36)
    c: Coincident(g37,g6)
    c: Coincident(g37,g19)
    c: Horizontal(g37)
    c: Coincident(g38,g7)
    c: Coincident(g38,g18)
    c: Horizontal(g38)
    c: Coincident(g39,g7)
    c: Coincident(g39,g18)
    c: Horizontal(g39)
    c: Coincident(g40,g8)
    c: Coincident(g40,g20)
    c: Horizontal(g40)
    c: Coincident(g41,g8)
    c: Coincident(g41,g20)
    c: Horizontal(g41)
    c: Coincident(g42,g9)
    c: Coincident(g42,g23)
    c: Horizontal(g42)
    c: Coincident(g43,g9)
    c: Coincident(g43,g23)
    c: Horizontal(g43)
    c: Coincident(g44,g10)
    c: Coincident(g44,g22)
    c: Horizontal(g44)
    c: Coincident(g45,g10)
    c: Coincident(g45,g22)
    c: Horizontal(g45)
    c: Coincident(g46,g11)
    c: Coincident(g46,g21)
    c: Horizontal(g46)
    c: Coincident(g47,g11)
    c: Coincident(g47,g21)
    c: Horizontal(g47)
FEATURE [Part::Extrusion] Extrude065
  Base = -> Sketch074
  Dir = (1,0,0)
  DirMode = 2
  FaceMakerClass = Part::FaceMakerBullseye
  LengthFwd = 23
  LengthRev = 0
  Placement = pos=(-19,0,0) rot=(0,0,1;0rad)
  Solid = true
  Symmetric = false
FEATURE [Part::Fillet] Fillet056  label="removeToCreateVentalationHoles003"
  Base = -> Extrude065
  Edges = <same value as first occurrence — deduplicated (x6 in doc)>
  Placement = pos=(7,0.02,0) rot=(0,0,1;0rad)
FEATURE [Part::Revolution] Revolve158  label="removeToCreateScrewAndThreadedInsertHole065"
  Angle = 360
  Axis = (0,1,0)
  Base = (0,0,0)
  FaceMakerClass = Part::FaceMakerBullseye
  Placement = pos=(12.5,0,62) rot=(0,0,1;0rad)
  Solid = false
  Source = -> Face146
  Symmetric = false
FEATURE [Part::Revolution] Revolve159  label="removeToCreateScrewAndThreadedInsertHole066"
  Angle = 360
  Axis = (0,1,0)
  Base = (0,0,0)
  FaceMakerClass = Part::FaceMakerBullseye
  Placement = pos=(89.5,0,68.5) rot=(0,0,1;0rad)
  Solid = false
  Source = -> Face143
  Symmetric = false
FEATURE [Part::Revolution] Revolve160  label="removeToCreateScrewAndThreadedInsertHole067"
  Angle = 360
  Axis = (0,1,0)
  Base = (0,0,0)
  FaceMakerClass = Part::FaceMakerBullseye
  Placement = pos=(89.5,0,3.5) rot=(0,0,1;0rad)
  Solid = false
  Source = -> Face142
  Symmetric = false
FEATURE [Part::Revolution] Revolve161  label="removeToCreateScrewAndThreadedInsertHole068"
  Angle = 360
  Axis = (0,1,0)
  Base = (0,0,0)
  FaceMakerClass = Part::FaceMakerBullseye
  Placement = pos=(109.5,4.7,3.5) rot=(0,0,1;0rad)
  Solid = false
  Source = -> Face145
  Symmetric = false
FEATURE [Part::Revolution] Revolve162  label="removeToCreateScrewAndThreadedInsertHole069"
  Angle = 360
  Axis = (0,1,0)
  Base = (0,0,0)
  FaceMakerClass = Part::FaceMakerBullseye
  Placement = pos=(109.5,4.7,68.5) rot=(0,0,1;0rad)
  Solid = false
  Source = -> Face144
  Symmetric = false
FEATURE [Part::MultiFuse] Fusion141  label="removeToCreateScrewAndThreadedInsertHole064"
  Shapes = -> [Revolve162,Revolve161,Revolve160,Revolve159,Revolve158,Revolve157]
FEATURE [Part::Cylinder] Cylinder062
  Angle = 360
  AttacherType = Attacher::AttachEngine3D
  Height = 20
  Placement = pos=(0,0,36.15) rot=(0,0,1;0rad)
  Radius = 14
FEATURE [Part::Cylinder] Cylinder063
  Angle = 360
  AttacherType = Attacher::AttachEngine3D
  Height = 10
  Placement = pos=(0,0,36.15) rot=(0,0,1;0rad)
  Radius = 4
FEATURE [Part::MultiFuse] Fusion139  label="removeToCreteHoleForPlugHousing052"
  Placement = pos=(70,19,36) rot=(0,1,0;1.5708rad)
  Shapes = -> [Cylinder062,Cylinder063]
FEATURE [Part::Cut] Cut060  label="bottom017"
  Base = -> Extrude064
  Tool = -> Fusion139
FEATURE [Part::Cut] Cut061  label="bottom019"
  Base = -> Cut060
  Tool = -> Fusion141
FEATURE [Part::MultiFuse] Fusion140  label="bottom018"
  Shapes = -> [Cut061,Cut058]
FEATURE [Part::Cut] Cut059  label="bottom020"
  Base = -> Fusion140
  Tool = -> Fillet056
FEATURE [Part::Box] Box036  label="Cube021"
  AttacherType = Attacher::AttachEngine3D
  Height = 80
  Length = 26
  Placement = pos=(0,-1,-5) rot=(0,0,1;0rad)
  Width = 11
FEATURE [Part::Cut] Cut062  label="removeFromBottom002"
  Base = -> Cut057
  Tool = -> Box036
FEATURE [Part::Cut] Cut063
  Base = -> Cut059
  Tool = -> Cut062
FEATURE [Part::Cut] Cut064  label="pcbStands"
  Base = -> Fusion095
  Tool = -> Fusion127
FEATURE [Sketcher::SketchObject] Sketch075  label="topSketch022"
  FullyConstrained = true
  sketch-geometry (6):
    g0: LineSegment StartX=19 StartY=38 StartZ=0 EndX=117 EndY=38 EndZ=0
    g1: ArcOfCircle CenterX=19 CenterY=19 CenterZ=0 NormalX=0 NormalY=0 NormalZ=1 AngleXU=0 Radius=19 StartAngle=1.5708 EndAngle=3.14159
    g2: LineSegment StartX=117 StartY=38 StartZ=0 EndX=117 EndY=19 EndZ=0
    g3: LineSegment StartX=98 StartY=1.0161e-12 StartZ=0 EndX=5.22862e-06 EndY=1.0161e-12 EndZ=0
    g4: LineSegment StartX=5.22862e-06 StartY=19 StartZ=0 EndX=5.22862e-06 EndY=1.0161e-12 EndZ=0
    g5: ArcOfCircle CenterX=98 CenterY=19 CenterZ=0 NormalX=0 NormalY=0 NormalZ=1 AngleXU=0 Radius=19 StartAngle=4.71239 EndAngle=6.28319
  constraints (16):
    c: Horizontal(g0)
    c: Distance(g0) = 98
    c: Coincident(g1,g0)
    c: Block(g1)
    c: Coincident(g2,g0)
    c: Vertical(g2)
    c: Distance(g2) = 19
    c: Horizontal(g3)
    c: Coincident(g4,g1)
    c: Vertical(g4)
    c: Coincident(g3,g4)
    c: Block(g3)
    c: Coincident(g5,g2)
    c: Coincident(g5,g3)
    c: Block(g0)
    c: Block(g5)
FEATURE [Part::Extrusion] Extrude067  label="sideB003"
  Base = -> Sketch075
  Dir = (0,0,1)
  DirMode = 2
  FaceMakerClass = Part::FaceMakerBullseye
  LengthFwd = 3
  LengthRev = 0
  Placement = pos=(0,0,71.7) rot=(0,0,1;0rad)
  Solid = true
  Symmetric = false
FEATURE [Sketcher::SketchObject] Sketch076  label="topSketch023"
  FullyConstrained = true
  sketch-geometry (6):
    g0: LineSegment StartX=19 StartY=38 StartZ=0 EndX=117 EndY=38 EndZ=0
    g1: ArcOfCircle CenterX=19 CenterY=19 CenterZ=0 NormalX=0 NormalY=0 NormalZ=1 AngleXU=0 Radius=19 StartAngle=1.5708 EndAngle=3.14159
    g2: LineSegment StartX=117 StartY=38 StartZ=0 EndX=117 EndY=19 EndZ=0
    g3: LineSegment StartX=98 StartY=1.0161e-12 StartZ=0 EndX=5.22862e-06 EndY=1.0161e-12 EndZ=0
    g4: LineSegment StartX=5.22862e-06 StartY=19 StartZ=0 EndX=5.22862e-06 EndY=1.0161e-12 EndZ=0
    g5: ArcOfCircle CenterX=98 CenterY=19 CenterZ=0 NormalX=0 NormalY=0 NormalZ=1 AngleXU=0 Radius=19 StartAngle=4.71239 EndAngle=6.28319
  constraints (16):
    c: Horizontal(g0)
    c: Distance(g0) = 98
    c: Coincident(g1,g0)
    c: Block(g1)
    c: Coincident(g2,g0)
    c: Vertical(g2)
    c: Distance(g2) = 19
    c: Horizontal(g3)
    c: Coincident(g4,g1)
    c: Vertical(g4)
    c: Coincident(g3,g4)
    c: Block(g3)
    c: Coincident(g5,g2)
    c: Coincident(g5,g3)
    c: Block(g0)
    c: Block(g5)
FEATURE [Part::Extrusion] Extrude066  label="sideA003"
  Base = -> Sketch076
  Dir = (0,0,1)
  DirMode = 2
  FaceMakerClass = Part::FaceMakerBullseye
  LengthFwd = 3
  LengthRev = 0
  Placement = pos=(0,0,-2.7) rot=(0,0,1;0rad)
  Solid = true
  Symmetric = false
FEATURE [Part::MultiFuse] Fusion142  label="removeFromBottom003"
  Placement = pos=(2,0,0) rot=(0,0,1;0rad)
  Shapes = -> [Extrude066,Extrude067]
FEATURE [Part::Cut] Cut065  label="screwRetainers002"
  Base = -> Fusion096
  Tool = -> Fusion142
FEATURE [Sketcher::SketchObject] Sketch077
  FullyConstrained = true
  Placement = pos=(117,19,0) rot=(0.57735,0.57735,0.57735;2.0944rad)
  sketch-geometry (8):
    g0: LineSegment StartX=-49.19 StartY=63.5 StartZ=0 EndX=-49.19 EndY=60.5 EndZ=0
    g1: LineSegment StartX=-49.19 StartY=11.5 StartZ=0 EndX=-49.19 EndY=8.5 EndZ=0
    g2: ArcOfCircle CenterX=-1.5 CenterY=62 CenterZ=0 NormalX=0 NormalY=0 NormalZ=1 AngleXU=0 Radius=1.5 StartAngle=4.71239 EndAngle=7.85398
    g3: ArcOfCircle CenterX=-1.5 CenterY=10 CenterZ=0 NormalX=0 NormalY=0 NormalZ=1 AngleXU=0 Radius=1.5 StartAngle=4.71239 EndAngle=7.85398
    g4: LineSegment StartX=-49.19 StartY=63.5 StartZ=0 EndX=-1.5 EndY=63.5 EndZ=0
    g5: LineSegment StartX=-49.19 StartY=60.5 StartZ=0 EndX=-1.5 EndY=60.5 EndZ=0
    g6: LineSegment StartX=-49.19 StartY=11.5 StartZ=0 EndX=-1.5 EndY=11.5 EndZ=0
    g7: LineSegment StartX=-49.19 StartY=8.5 StartZ=0 EndX=-1.5 EndY=8.5 EndZ=0
  constraints (19):
    c: Vertical(g0)
    c: Distance(g0) = 3
    c: Vertical(g1)
    c: Block(g1)
    c: Block(g2)
    c: Block(g3)
    c: Block(g0)
    c: Coincident(g4,g0)
    c: Coincident(g4,g2)
    c: Horizontal(g4)
    c: Coincident(g5,g0)
    c: Coincident(g5,g2)
    c: Horizontal(g5)
    c: Coincident(g6,g1)
    c: Coincident(g6,g3)
    c: Horizontal(g6)
    c: Coincident(g7,g1)
    c: Coincident(g7,g3)
    c: Horizontal(g7)
FEATURE [Part::Extrusion] Extrude068
  Base = -> Sketch077
  Dir = (1,0,0)
  DirMode = 2
  FaceMakerClass = Part::FaceMakerBullseye
  LengthFwd = 10
  LengthRev = 0
  Solid = true
  Symmetric = false
FEATURE [Part::Fillet] Fillet057  label="removeFromtMoreFrontCaseScrewRetainers002"
  Base = -> Extrude068
  Edges = 4 edges r=1.49: [Edge6,Edge11,Edge18,Edge23]
  Placement = pos=(-12,0,0) rot=(0,0,1;0rad)
FEATURE [Sketcher::SketchObject] Sketch078
  FullyConstrained = true
  Placement = pos=(117,19,0) rot=(0.57735,0.57735,0.57735;2.0944rad)
  sketch-geometry (8):
    g0: LineSegment StartX=-49.19 StartY=69.25 StartZ=0 EndX=-49.19 EndY=66.25 EndZ=0
    g1: LineSegment StartX=-49.19 StartY=5.75 StartZ=0 EndX=-49.19 EndY=2.75 EndZ=0
    g2: ArcOfCircle CenterX=-1.5 CenterY=67.75 CenterZ=0 NormalX=0 NormalY=0 NormalZ=1 AngleXU=0 Radius=1.5 StartAngle=4.71239 EndAngle=7.85398
    g3: ArcOfCircle CenterX=-1.5 CenterY=4.25 CenterZ=0 NormalX=0 NormalY=0 NormalZ=1 AngleXU=0 Radius=1.5 StartAngle=4.71239 EndAngle=7.85398
    g4: LineSegment StartX=-49.19 StartY=69.25 StartZ=0 EndX=-1.5 EndY=69.25 EndZ=0
    g5: LineSegment StartX=-49.19 StartY=66.25 StartZ=0 EndX=-1.5 EndY=66.25 EndZ=0
    g6: LineSegment StartX=-49.19 StartY=5.75 StartZ=0 EndX=-1.5 EndY=5.75 EndZ=0
    g7: LineSegment StartX=-49.19 StartY=2.75 StartZ=0 EndX=-1.5 EndY=2.75 EndZ=0
  constraints (19):
    c: Vertical(g0)
    c: Distance(g0) = 3
    c: Block(g0)
    c: Vertical(g1)
    c: Block(g2)
    c: Block(g3)
    c: Block(g1)
    c: Coincident(g4,g0)
    c: Coincident(g4,g2)
    c: Horizontal(g4)
    c: Coincident(g5,g0)
    c: Coincident(g5,g2)
    c: Horizontal(g5)
    c: Coincident(g6,g1)
    c: Coincident(g6,g3)
    c: Horizontal(g6)
    c: Coincident(g7,g1)
    c: Coincident(g7,g3)
    c: Horizontal(g7)
FEATURE [Part::Extrusion] Extrude069
  Base = -> Sketch078
  Dir = (1,0,0)
  DirMode = 2
  FaceMakerClass = Part::FaceMakerBullseye
  LengthFwd = 10
  LengthRev = 0
  Solid = true
  Symmetric = false
FEATURE [Part::Fillet] Fillet058  label="removeFromtMoreFrontCaseScrewRetainers003"
  Base = -> Extrude069
  Edges = 4 edges r=1.49: [Edge6,Edge11,Edge18,Edge23]
  Placement = pos=(-4,0,0) rot=(0,0,1;0rad)
FEATURE [Part::Cut] Cut066
  Base = -> Cut065
  Tool = -> Fillet058
FEATURE [Part::Cut] Cut067  label="screwPillars"
  Base = -> Cut066
  Tool = -> Fillet057
FEATURE [Part::MultiFuse] Fusion143  label="bottom021"
  Shapes = -> [Cut031,Cut063]
FEATURE [Part::Cylinder] Cylinder
  Angle = 360
  AttacherType = Attacher::AttachEngine3D
  Height = 10
  Placement = pos=(20.65,12,4.68) rot=(1,0,0;1.5708rad)
  Radius = 2
FEATURE [Part::Cylinder] Cylinder064
  Angle = 360
  AttacherType = Attacher::AttachEngine3D
  Height = 10
  Placement = pos=(20.65,12,67.38) rot=(1,0,0;1.5708rad)
  Radius = 2
FEATURE [Part::Cylinder] Cylinder065
  Angle = 360
  AttacherType = Attacher::AttachEngine3D
  Height = 10
  Placement = pos=(77.15,12,67.38) rot=(1,0,0;1.5708rad)
  Radius = 2
FEATURE [Part::Cylinder] Cylinder066
  Angle = 360
  AttacherType = Attacher::AttachEngine3D
  Height = 10
  Placement = pos=(77.15,12,4.68) rot=(1,0,0;1.5708rad)
  Radius = 2
FEATURE [Part::MultiFuse] Fusion144  label="removeFromThreadedInsertHousing"
  Shapes = -> [Cylinder065,Cylinder064,Cylinder,Cylinder066]
FEATURE [Part::Cut] Cut068  label="pcbStands001"
  Base = -> Cut064
  Tool = -> Fusion144
FEATURE [Part::MultiFuse] Fusion145
  Shapes = -> [Cut068,Fusion143]
FEATURE [Part::MultiFuse] Fusion146
  Shapes = -> [Fusion145]
FEATURE [Part::MultiFuse] Fusion147  label="bottom022"
  Shapes = -> [Cut067,Fusion146]
FEATURE [Part::MultiFuse] Fusion148  label="casePillars005"
  Shapes = -> [Cut047,Fusion092]
FEATURE [Part::MultiFuse] Fusion149  label="bottom023"
  Shapes = -> [Fusion124,Fusion113,Fusion147]
FEATURE [Part::MultiFuse] Fusion150  label="topBits"
  Shapes = -> [Cut025,Fusion148,Cut030,Fillet034]
FEATURE [Part::Feature] Face149 .. Face152  x4 (patterned run collapsed; names and placements below)
  shape: bbox 3.2 x 1.5 x 2e-07 mm, 1 faces, 0 solids (baked)
FEATURE [Part::Feature] Face153
  shape: bbox 3.6 x 3.2 x 2e-07 mm, 1 faces, 0 solids (baked)
FEATURE [Part::Feature] Face154
  shape: bbox 3.6 x 3.2 x 2e-07 mm, 1 faces, 0 solids (baked)
FEATURE [Sketcher::SketchObject] Sketch079  label="topSketch024"
  FullyConstrained = true
  sketch-geometry (6):
    g0: LineSegment StartX=19 StartY=38 StartZ=0 EndX=117 EndY=38 EndZ=0
    g1: ArcOfCircle CenterX=19 CenterY=19 CenterZ=0 NormalX=0 NormalY=0 NormalZ=1 AngleXU=0 Radius=19 StartAngle=1.5708 EndAngle=3.14159
    g2: LineSegment StartX=117 StartY=38 StartZ=0 EndX=117 EndY=19 EndZ=0
    g3: LineSegment StartX=98 StartY=1.0161e-12 StartZ=0 EndX=5.22862e-06 EndY=1.0161e-12 EndZ=0
    g4: LineSegment StartX=5.22862e-06 StartY=19 StartZ=0 EndX=5.22862e-06 EndY=1.0161e-12 EndZ=0
    g5: ArcOfCircle CenterX=98 CenterY=19 CenterZ=0 NormalX=0 NormalY=0 NormalZ=1 AngleXU=0 Radius=19 StartAngle=4.71239 EndAngle=6.28319
  constraints (16):
    c: Horizontal(g0)
    c: Distance(g0) = 98
    c: Coincident(g1,g0)
    c: Block(g1)
    c: Coincident(g2,g0)
    c: Vertical(g2)
    c: Distance(g2) = 19
    c: Horizontal(g3)
    c: Coincident(g4,g1)
    c: Vertical(g4)
    c: Coincident(g3,g4)
    c: Block(g3)
    c: Coincident(g5,g2)
    c: Coincident(g5,g3)
    c: Block(g0)
    c: Block(g5)
FEATURE [Sketcher::SketchObject] Sketch080  label="topSketch025"
  FullyConstrained = true
  sketch-geometry (6):
    g0: LineSegment StartX=19 StartY=38 StartZ=0 EndX=117 EndY=38 EndZ=0
    g1: ArcOfCircle CenterX=19 CenterY=19 CenterZ=0 NormalX=0 NormalY=0 NormalZ=1 AngleXU=0 Radius=19 StartAngle=1.5708 EndAngle=3.14159
    g2: LineSegment StartX=117 StartY=38 StartZ=0 EndX=117 EndY=19 EndZ=0
    g3: LineSegment StartX=98 StartY=1.0161e-12 StartZ=0 EndX=5.22862e-06 EndY=1.0161e-12 EndZ=0
    g4: LineSegment StartX=5.22862e-06 StartY=19 StartZ=0 EndX=5.22862e-06 EndY=1.0161e-12 EndZ=0
    g5: ArcOfCircle CenterX=98 CenterY=19 CenterZ=0 NormalX=0 NormalY=0 NormalZ=1 AngleXU=0 Radius=19 StartAngle=4.71239 EndAngle=6.28319
  constraints (16):
    c: Horizontal(g0)
    c: Distance(g0) = 98
    c: Coincident(g1,g0)
    c: Block(g1)
    c: Coincident(g2,g0)
    c: Vertical(g2)
    c: Distance(g2) = 19
    c: Horizontal(g3)
    c: Coincident(g4,g1)
    c: Vertical(g4)
    c: Coincident(g3,g4)
    c: Block(g3)
    c: Coincident(g5,g2)
    c: Coincident(g5,g3)
    c: Block(g0)
    c: Block(g5)
FEATURE [Part::Extrusion] Extrude070  label="sideA004"
  Base = -> Sketch080
  Dir = (0,0,1)
  DirMode = 2
  FaceMakerClass = Part::FaceMakerBullseye
  LengthFwd = 3
  LengthRev = 0
  Placement = pos=(0,0,-2.7) rot=(0,0,1;0rad)
  Solid = true
  Symmetric = false
FEATURE [Sketcher::SketchObject] Sketch081
  FullyConstrained = true
  Placement = pos=(117,19,0) rot=(0.57735,0.57735,0.57735;2.0944rad)
  sketch-geometry (8):
    g0: LineSegment StartX=-49.19 StartY=63.5 StartZ=0 EndX=-49.19 EndY=60.5 EndZ=0
    g1: LineSegment StartX=-49.19 StartY=11.5 StartZ=0 EndX=-49.19 EndY=8.5 EndZ=0
    g2: ArcOfCircle CenterX=-1.5 CenterY=62 CenterZ=0 NormalX=0 NormalY=0 NormalZ=1 AngleXU=0 Radius=1.5 StartAngle=4.71239 EndAngle=7.85398
    g3: ArcOfCircle CenterX=-1.5 CenterY=10 CenterZ=0 NormalX=0 NormalY=0 NormalZ=1 AngleXU=0 Radius=1.5 StartAngle=4.71239 EndAngle=7.85398
    g4: LineSegment StartX=-49.19 StartY=63.5 StartZ=0 EndX=-1.5 EndY=63.5 EndZ=0
    g5: LineSegment StartX=-49.19 StartY=60.5 StartZ=0 EndX=-1.5 EndY=60.5 EndZ=0
    g6: LineSegment StartX=-49.19 StartY=11.5 StartZ=0 EndX=-1.5 EndY=11.5 EndZ=0
    g7: LineSegment StartX=-49.19 StartY=8.5 StartZ=0 EndX=-1.5 EndY=8.5 EndZ=0
  constraints (19):
    c: Vertical(g0)
    c: Distance(g0) = 3
    c: Vertical(g1)
    c: Block(g1)
    c: Block(g2)
    c: Block(g3)
    c: Block(g0)
    c: Coincident(g4,g0)
    c: Coincident(g4,g2)
    c: Horizontal(g4)
    c: Coincident(g5,g0)
    c: Coincident(g5,g2)
    c: Horizontal(g5)
    c: Coincident(g6,g1)
    c: Coincident(g6,g3)
    c: Horizontal(g6)
    c: Coincident(g7,g1)
    c: Coincident(g7,g3)
    c: Horizontal(g7)
FEATURE [Part::Extrusion] Extrude071  label="sideB004"
  Base = -> Sketch079
  Dir = (0,0,1)
  DirMode = 2
  FaceMakerClass = Part::FaceMakerBullseye
  LengthFwd = 3
  LengthRev = 0
  Placement = pos=(0,0,71.7) rot=(0,0,1;0rad)
  Solid = true
  Symmetric = false
FEATURE [Part::MultiFuse] Fusion152  label="removeFromBottom004"
  Placement = pos=(2,0,0) rot=(0,0,1;0rad)
  Shapes = -> [Extrude070,Extrude071]
FEATURE [Part::Extrusion] Extrude072
  Base = -> Sketch081
  Dir = (1,0,0)
  DirMode = 2
  FaceMakerClass = Part::FaceMakerBullseye
  LengthFwd = 10
  LengthRev = 0
  Solid = true
  Symmetric = false
FEATURE [Part::Fillet] Fillet059  label="removeFromtMoreFrontCaseScrewRetainers004"
  Base = -> Extrude072
  Edges = 4 edges r=1.49: [Edge6,Edge11,Edge18,Edge23]
  Placement = pos=(-12,0,0) rot=(0,0,1;0rad)
FEATURE [Sketcher::SketchObject] Sketch082
  FullyConstrained = true
  Placement = pos=(117,19,0) rot=(0.57735,0.57735,0.57735;2.0944rad)
  sketch-geometry (8):
    g0: LineSegment StartX=-49.19 StartY=69.25 StartZ=0 EndX=-49.19 EndY=66.25 EndZ=0
    g1: LineSegment StartX=-49.19 StartY=5.75 StartZ=0 EndX=-49.19 EndY=2.75 EndZ=0
    g2: ArcOfCircle CenterX=-1.5 CenterY=67.75 CenterZ=0 NormalX=0 NormalY=0 NormalZ=1 AngleXU=0 Radius=1.5 StartAngle=4.71239 EndAngle=7.85398
    g3: ArcOfCircle CenterX=-1.5 CenterY=4.25 CenterZ=0 NormalX=0 NormalY=0 NormalZ=1 AngleXU=0 Radius=1.5 StartAngle=4.71239 EndAngle=7.85398
    g4: LineSegment StartX=-49.19 StartY=69.25 StartZ=0 EndX=-1.5 EndY=69.25 EndZ=0
    g5: LineSegment StartX=-49.19 StartY=66.25 StartZ=0 EndX=-1.5 EndY=66.25 EndZ=0
    g6: LineSegment StartX=-49.19 StartY=5.75 StartZ=0 EndX=-1.5 EndY=5.75 EndZ=0
    g7: LineSegment StartX=-49.19 StartY=2.75 StartZ=0 EndX=-1.5 EndY=2.75 EndZ=0
  constraints (19):
    c: Vertical(g0)
    c: Distance(g0) = 3
    c: Block(g0)
    c: Vertical(g1)
    c: Block(g2)
    c: Block(g3)
    c: Block(g1)
    c: Coincident(g4,g0)
    c: Coincident(g4,g2)
    c: Horizontal(g4)
    c: Coincident(g5,g0)
    c: Coincident(g5,g2)
    c: Horizontal(g5)
    c: Coincident(g6,g1)
    c: Coincident(g6,g3)
    c: Horizontal(g6)
    c: Coincident(g7,g1)
    c: Coincident(g7,g3)
    c: Horizontal(g7)
FEATURE [Part::Extrusion] Extrude073
  Base = -> Sketch082
  Dir = (1,0,0)
  DirMode = 2
  FaceMakerClass = Part::FaceMakerBullseye
  LengthFwd = 10
  LengthRev = 0
  Solid = true
  Symmetric = false
FEATURE [Part::Fillet] Fillet060  label="removeFromtMoreFrontCaseScrewRetainers005"
  Base = -> Extrude073
  Edges = 4 edges r=1.49: [Edge6,Edge11,Edge18,Edge23]
  Placement = pos=(-4,0,0) rot=(0,0,1;0rad)
FEATURE [Part::Revolution] Revolve163  label="backCaseScrewRetainer004"
  Angle = 360
  Axis = (0,1,0)
  Base = (0,0,0)
  FaceMakerClass = Part::FaceMakerBullseye
  Placement = pos=(12.5,3,62) rot=(0,0,1;0rad)
  Solid = false
  Source = -> Face149
  Symmetric = false
FEATURE [Part::Revolution] Revolve164  label="frontCaseScrewRetainer006"
  Angle = 360
  Axis = (0,1,0)
  Base = (0,0,0)
  FaceMakerClass = Part::FaceMakerBullseye
  Placement = pos=(89.5,3,68.5) rot=(0,0,1;0rad)
  Solid = false
  Source = -> Face151
  Symmetric = false
FEATURE [Part::Revolution] Revolve165  label="frontCaseScrewRetainer007"
  Angle = 360
  Axis = (0,1,0)
  Base = (0,0,0)
  FaceMakerClass = Part::FaceMakerBullseye
  Placement = pos=(89.5,3,3.5) rot=(0,0,1;0rad)
  Solid = false
  Source = -> Face152
  Symmetric = false
FEATURE [Part::Revolution] Revolve166  label="backCaseScrewRetainer005"
  Angle = 360
  Axis = (0,1,0)
  Base = (0,0,0)
  FaceMakerClass = Part::FaceMakerBullseye
  Placement = pos=(12.5,3,10) rot=(0,0,1;0rad)
  Solid = false
  Source = -> Face150
  Symmetric = false
FEATURE [Part::Revolution] Revolve167  label="moreFrontCaseScrewRetainer006"
  Angle = 360
  Axis = (0,1,0)
  Base = (0,0,0)
  FaceMakerClass = Part::FaceMakerBullseye
  Placement = pos=(109.5,4.5,68.5) rot=(0,0,1;0rad)
  Solid = false
  Source = -> Face153
  Symmetric = false
FEATURE [Part::Revolution] Revolve168  label="moreFrontCaseScrewRetainer007"
  Angle = 360
  Axis = (0,1,0)
  Base = (0,0,0)
  FaceMakerClass = Part::FaceMakerBullseye
  Placement = pos=(109.5,4.5,3.5) rot=(0,0,1;0rad)
  Solid = false
  Source = -> Face154
  Symmetric = false
FEATURE [Part::MultiFuse] Fusion151  label="screwRetainers003"
  Shapes = -> [Revolve168,Revolve167,Revolve166,Revolve165,Revolve164,Revolve163]
FEATURE [Part::Cut] Cut069  label="screwRetainers004"
  Base = -> Fusion151
  Tool = -> Fusion152
FEATURE [Part::Cut] Cut070
  Base = -> Cut069
  Tool = -> Fillet060
FEATURE [Part::Cut] Cut071  label="screwPillars001"
  Base = -> Cut070
  Tool = -> Fillet059
FEATURE [Part::MultiFuse] Fusion153  label="bottom024"
  Shapes = -> [Fusion149,Cut071]
FEATURE [Part::Cylinder] Cylinder067
  Angle = 360
  AttacherType = Attacher::AttachEngine3D
  Height = 10
  Placement = pos=(20.65,12,4.68) rot=(1,0,0;1.5708rad)
  Radius = 2
FEATURE [Part::Cylinder] Cylinder068
  Angle = 360
  AttacherType = Attacher::AttachEngine3D
  Height = 10
  Placement = pos=(20.65,12,67.38) rot=(1,0,0;1.5708rad)
  Radius = 2
FEATURE [Part::Cylinder] Cylinder069
  Angle = 360
  AttacherType = Attacher::AttachEngine3D
  Height = 10
  Placement = pos=(77.15,12,67.38) rot=(1,0,0;1.5708rad)
  Radius = 2
FEATURE [Part::Cylinder] Cylinder070
  Angle = 360
  AttacherType = Attacher::AttachEngine3D
  Height = 10
  Placement = pos=(77.15,12,4.68) rot=(1,0,0;1.5708rad)
  Radius = 2
FEATURE [Part::MultiFuse] Fusion154  label="removeFromThreadedInsertHousing001"
  Shapes = -> [Cylinder069,Cylinder068,Cylinder067,Cylinder070]
FEATURE [Part::Cut] Cut072  label="bottom025"
  Base = -> Fusion153
  Tool = -> Fusion154
FEATURE [Image::ImagePlane] ImagePlane
  XSize = 339
  YSize = 72
FEATURE [Sketcher::SketchObject] Sketch083
  FullyConstrained = true
  MapMode = 5
  Support = -> [XY_Plane]
  sketch-geometry (338):
    g0: LineSegment StartX=-151.619 StartY=28.8932 StartZ=0 EndX=-140.819 EndY=28.8932 EndZ=0
    g1: LineSegment StartX=-151.619 StartY=24.0313 StartZ=0 EndX=-151.619 EndY=28.8932 EndZ=0
    g2: LineSegment StartX=-140.819 StartY=17.7713 StartZ=0 EndX=-151.619 EndY=17.7713 EndZ=0
    g3: LineSegment StartX=-151.619 StartY=17.7713 StartZ=0 EndX=-151.619 EndY=22.6313 EndZ=0
    g4: LineSegment StartX=-151.619 StartY=22.6313 StartZ=0 EndX=-145.128 EndY=22.6313 EndZ=0
    g5: LineSegment StartX=-145.128 StartY=24.0313 StartZ=0 EndX=-140.819 EndY=28.8932 EndZ=0
    g6: LineSegment StartX=-145.128 StartY=22.6313 StartZ=0 EndX=-140.819 EndY=17.7713 EndZ=0
    g7: ArcOfCircle CenterX=-155.157 CenterY=23.3323 CenterZ=0 NormalX=0 NormalY=0 NormalZ=1 AngleXU=0 Radius=6.92354 StartAngle=1.03434 EndAngle=5.24885
    g8: ArcOfCircle CenterX=-155.157 CenterY=23.3323 CenterZ=0 NormalX=0 NormalY=0 NormalZ=1 AngleXU=0 Radius=12.6269 StartAngle=1.28675 EndAngle=4.99643
    g9: LineSegment StartX=-151.619 StartY=35.4532 StartZ=0 EndX=-151.619 EndY=29.2832 EndZ=0
    g10: LineSegment StartX=-151.619 StartY=17.3813 StartZ=0 EndX=-151.619 EndY=11.2113 EndZ=0
    g11-g21: Circle x11 (B-spline internal-alignment scaffolding for g22; pole/knot coordinates omitted)
    g22: BSplineCurve PolesCount=11 KnotsCount=9 Degree=3 IsPeriodic=0
    g23-g31: GeomPoint x9 (B-spline internal-alignment scaffolding for g22; pole/knot coordinates omitted)
    g32-g49: Circle x18 (B-spline internal-alignment scaffolding for g50; pole/knot coordinates omitted)
    g50: BSplineCurve PolesCount=18 KnotsCount=16 Degree=3 IsPeriodic=0
    g51-g66: GeomPoint x16 (B-spline internal-alignment scaffolding for g50; pole/knot coordinates omitted)
    g67: LineSegment StartX=-117.124 StartY=30.093 StartZ=0 EndX=-117.603 EndY=26.5272 EndZ=0
    g68: LineSegment StartX=-117.603 StartY=17.8472 StartZ=0 EndX=-117.124 EndY=14.2659 EndZ=0
    g69: Ellipse CenterX=-109.671 CenterY=20.025 CenterZ=0 NormalX=0 NormalY=0 NormalZ=1 MajorRadius=3.34798 MinorRadius=2.71052 AngleXU=-1.56793
    g70: GeomPoint X=-109.666 Y=18.0598 Z=0
    g71: GeomPoint X=-109.677 Y=21.9902 Z=0
    g72: Ellipse CenterX=-109.671 CenterY=20.0123 CenterZ=0 NormalX=0 NormalY=0 NormalZ=1 MajorRadius=6.93002 MinorRadius=6.36273 AngleXU=-3.13976
    g73: GeomPoint X=-112.417 Y=20.0073 Z=0
    g74: GeomPoint X=-106.925 Y=20.0173 Z=0
    g75: Ellipse CenterX=-51.7682 CenterY=20.1463 CenterZ=0 NormalX=0 NormalY=0 NormalZ=1 MajorRadius=3.19279 MinorRadius=2.71052 AngleXU=-1.52774
    g76: GeomPoint X=-51.6955 Y=18.4606 Z=0
    g77: GeomPoint X=-51.8408 Y=21.832 Z=0
    g78: GeomPoint X=-54.5142 Y=20.1413 Z=0
    g79: GeomPoint X=-49.0221 Y=20.1513 Z=0
    g80: Ellipse CenterX=-51.7682 CenterY=20.1463 CenterZ=0 NormalX=0 NormalY=0 NormalZ=1 MajorRadius=6.93002 MinorRadius=6.36273 AngleXU=-3.13976
    g81: Ellipse CenterX=-22.8436 CenterY=20.1783 CenterZ=0 NormalX=0 NormalY=0 NormalZ=1 MajorRadius=3.31512 MinorRadius=2.71052 AngleXU=-1.60214
    g82: GeomPoint X=-22.9034 Y=18.2706 Z=0
    g83: GeomPoint X=-22.7838 Y=22.0861 Z=0
    g84: GeomPoint X=-25.5897 Y=20.1733 Z=0
    g85: GeomPoint X=-20.0976 Y=20.1833 Z=0
    g86: Ellipse CenterX=-22.8436 CenterY=20.1783 CenterZ=0 NormalX=0 NormalY=0 NormalZ=1 MajorRadius=6.93002 MinorRadius=6.36273 AngleXU=-3.13976
    g87: LineSegment StartX=-101.889 StartY=14.1107 StartZ=0 EndX=-97.7455 EndY=14.1107 EndZ=0
    g88: LineSegment StartX=-93.8155 StartY=14.1107 StartZ=0 EndX=-89.6755 EndY=14.1107 EndZ=0
    g89: LineSegment StartX=-85.7455 StartY=14.1107 StartZ=0 EndX=-81.6055 EndY=14.1107 EndZ=0
    g90: LineSegment StartX=-101.889 StartY=14.1107 StartZ=0 EndX=-101.889 EndY=25.9907 EndZ=0
    g91: LineSegment StartX=-101.889 StartY=25.9907 StartZ=0 EndX=-97.8594 EndY=25.9907 EndZ=0
    g92: LineSegment StartX=-97.8594 StartY=25.9907 StartZ=0 EndX=-97.8594 EndY=24.0907 EndZ=0
    g93: LineSegment StartX=-97.7455 StartY=14.1107 StartZ=0 EndX=-97.7455 EndY=19.9107 EndZ=0
    g94: LineSegment StartX=-89.6755 StartY=14.1107 StartZ=0 EndX=-89.6755 EndY=19.9107 EndZ=0
    g95: LineSegment StartX=-93.8155 StartY=14.1107 StartZ=0 EndX=-93.8155 EndY=21.0107 EndZ=0
    g96-g106: Circle x11 (B-spline internal-alignment scaffolding for g107; pole/knot coordinates omitted)
    g107: BSplineCurve PolesCount=11 KnotsCount=9 Degree=3 IsPeriodic=0
    g108-g116: GeomPoint x9 (B-spline internal-alignment scaffolding for g107; pole/knot coordinates omitted)
    g117: BSplineCurve PolesCount=11 KnotsCount=9 Degree=3 IsPeriodic=0
    g118-g125: Circle x8 (B-spline internal-alignment scaffolding for g126; pole/knot coordinates omitted)
    g126: BSplineCurve PolesCount=8 KnotsCount=6 Degree=3 IsPeriodic=0
    g127-g132: GeomPoint x6 (B-spline internal-alignment scaffolding for g126; pole/knot coordinates omitted)
    g133: BSplineCurve PolesCount=8 KnotsCount=6 Degree=3 IsPeriodic=0
    g134: LineSegment StartX=-85.7455 StartY=21.0107 StartZ=0 EndX=-85.7455 EndY=14.1107 EndZ=0
    g135: LineSegment StartX=-80.0879 StartY=14.1107 StartZ=0 EndX=-75.944 EndY=14.1107 EndZ=0
    g136: LineSegment StartX=-72.014 StartY=14.1107 StartZ=0 EndX=-67.874 EndY=14.1107 EndZ=0
    g137: LineSegment StartX=-63.944 StartY=14.1107 StartZ=0 EndX=-59.804 EndY=14.1107 EndZ=0
    g138: LineSegment StartX=-80.0879 StartY=14.1107 StartZ=0 EndX=-80.0879 EndY=25.9907 EndZ=0
    g139: LineSegment StartX=-80.0879 StartY=25.9907 StartZ=0 EndX=-76.0579 EndY=25.9907 EndZ=0
    g140: LineSegment StartX=-76.0579 StartY=25.9907 StartZ=0 EndX=-76.0579 EndY=24.0907 EndZ=0
    g141: LineSegment StartX=-75.944 StartY=14.1107 StartZ=0 EndX=-75.944 EndY=19.9107 EndZ=0
    g142: LineSegment StartX=-67.874 StartY=14.1107 StartZ=0 EndX=-67.874 EndY=19.9107 EndZ=0
    g143: LineSegment StartX=-72.014 StartY=14.1107 StartZ=0 EndX=-72.014 EndY=21.0107 EndZ=0
    g144-g148: Circle x5 (B-spline internal-alignment scaffolding for g149; pole/knot coordinates omitted)
    g149: BSplineCurve PolesCount=11 KnotsCount=9 Degree=3 IsPeriodic=0
    g150-g158: GeomPoint x9 (B-spline internal-alignment scaffolding for g149; pole/knot coordinates omitted)
    g159: BSplineCurve PolesCount=11 KnotsCount=9 Degree=3 IsPeriodic=0
    g160-g167: Circle x8 (B-spline internal-alignment scaffolding for g168; pole/knot coordinates omitted)
    g168: BSplineCurve PolesCount=8 KnotsCount=6 Degree=3 IsPeriodic=0
    g169-g174: GeomPoint x6 (B-spline internal-alignment scaffolding for g168; pole/knot coordinates omitted)
    g175: BSplineCurve PolesCount=8 KnotsCount=6 Degree=3 IsPeriodic=0
    g176: LineSegment StartX=-63.944 StartY=21.0107 StartZ=0 EndX=-63.944 EndY=14.1107 EndZ=0
    g177: LineSegment StartX=-59.804 StartY=14.1107 StartZ=0 EndX=-59.804 EndY=21.5868 EndZ=0
    g178: BSplineCurve PolesCount=4 KnotsCount=2 Degree=3 IsPeriodic=0
    g179: GeomPoint X=-59.804 Y=21.5868 Z=0
    g180: GeomPoint X=-60.2379 Y=24.0907 Z=0
    g181: LineSegment StartX=-81.6055 StartY=14.1107 StartZ=0 EndX=-81.6055 EndY=21.5868 EndZ=0
    g182: LineSegment StartX=-151.619 StartY=24.0313 StartZ=0 EndX=-145.128 EndY=24.0313 EndZ=0
    g183: Circle CenterX=-82.0394 CenterY=24.0907 CenterZ=0 NormalX=0 NormalY=0 NormalZ=1 AngleXU=0 Radius=1
    g184: Circle CenterX=-81.7131 CenterY=23.2736 CenterZ=0 NormalX=0 NormalY=0 NormalZ=1 AngleXU=0 Radius=1
    g185: Circle CenterX=-81.6055 CenterY=21.5868 CenterZ=0 NormalX=0 NormalY=0 NormalZ=1 AngleXU=0 Radius=1
    g186: BSplineCurve PolesCount=3 KnotsCount=2 Degree=2 IsPeriodic=0
    g187: GeomPoint X=-82.0394 Y=24.0907 Z=0
    g188: GeomPoint X=-81.6055 Y=21.5868 Z=0
    g189: Ellipse CenterX=-37.3522 CenterY=19.9515 CenterZ=0 NormalX=0 NormalY=0 NormalZ=1 MajorRadius=2.99755 MinorRadius=2.49 AngleXU=1.5708
    g190: GeomPoint X=-37.3522 Y=21.6203 Z=0
    g191: GeomPoint X=-37.3522 Y=18.2826 Z=0
    g192: ArcOfEllipse CenterX=-38.7647 CenterY=20.06 CenterZ=0 NormalX=0 NormalY=0 NormalZ=1 MajorRadius=6.30025 MinorRadius=5.3849 AngleXU=1.57276 StartAngle=5.50632 EndAngle=10.3035
    g193: GeomPoint X=-38.7711 Y=23.3304 Z=0
    g194: GeomPoint X=-38.7583 Y=16.7895 Z=0
    g195: LineSegment StartX=-34.6109 StartY=14.1107 StartZ=0 EndX=-30.8984 EndY=14.1107 EndZ=0
    g196: LineSegment StartX=-30.8984 StartY=14.1107 StartZ=0 EndX=-30.8984 EndY=31.1784 EndZ=0
    g197: LineSegment StartX=-30.8984 StartY=31.1784 StartZ=0 EndX=-34.9984 EndY=31.1784 EndZ=0
    g198: LineSegment StartX=-34.9984 StartY=24.5602 StartZ=0 EndX=-34.9984 EndY=31.1784 EndZ=0
    g199: LineSegment StartX=-34.6109 StartY=16.0476 StartZ=0 EndX=-34.6109 EndY=14.1107 EndZ=0
    g200: LineSegment StartX=-14.8781 StartY=14.1107 StartZ=0 EndX=-10.5106 EndY=14.1107 EndZ=0
    g201: LineSegment StartX=-14.8781 StartY=14.1107 StartZ=0 EndX=-14.8781 EndY=25.8504 EndZ=0
    g202: LineSegment StartX=-14.8781 StartY=25.8504 StartZ=0 EndX=-10.8534 EndY=25.8504 EndZ=0
    g203: LineSegment StartX=-10.8534 StartY=25.8504 StartZ=0 EndX=-10.8534 EndY=24.0923 EndZ=0
    g204: LineSegment StartX=-10.5106 StartY=14.1107 StartZ=0 EndX=-10.5106 EndY=19.7752 EndZ=0
    g205: LineSegment StartX=-5.96397 StartY=25.9304 StartZ=0 EndX=-5.96397 EndY=22.574 EndZ=0
    g206-g214: Circle x9 (B-spline internal-alignment scaffolding for g215; pole/knot coordinates omitted)
    g215: BSplineCurve PolesCount=9 KnotsCount=7 Degree=3 IsPeriodic=0
    g216-g222: GeomPoint x7 (B-spline internal-alignment scaffolding for g215; pole/knot coordinates omitted)
    g223-g232: Circle x10 (B-spline internal-alignment scaffolding for g233; pole/knot coordinates omitted)
    g233: BSplineCurve PolesCount=10 KnotsCount=8 Degree=3 IsPeriodic=0
    g234-g241: GeomPoint x8 (B-spline internal-alignment scaffolding for g233; pole/knot coordinates omitted)
    g242: LineSegment StartX=-1.58923 StartY=21.0696 StartZ=0 EndX=2.62034 EndY=21.0696 EndZ=0
    g243: LineSegment StartX=-1.55856 StartY=18.7342 StartZ=0 EndX=6.45946 EndY=18.7342 EndZ=0
    g244: LineSegment StartX=5.29231 StartY=17.386 StartZ=0 EndX=5.29231 EndY=14.3674 EndZ=0
    g245-g269: Circle x25 (B-spline internal-alignment scaffolding for g270; pole/knot coordinates omitted)
    g270: BSplineCurve PolesCount=25 KnotsCount=23 Degree=3 IsPeriodic=0
    g271-g293: GeomPoint x23 (B-spline internal-alignment scaffolding for g270; pole/knot coordinates omitted)
    g294-g304: Circle x11 (B-spline internal-alignment scaffolding for g305; pole/knot coordinates omitted)
    g305: BSplineCurve PolesCount=11 KnotsCount=9 Degree=3 IsPeriodic=0
    g306-g314: GeomPoint x9 (B-spline internal-alignment scaffolding for g305; pole/knot coordinates omitted)
    g315-g326: Circle x12 (B-spline internal-alignment scaffolding for g327; pole/knot coordinates omitted)
    g327: BSplineCurve PolesCount=12 KnotsCount=10 Degree=3 IsPeriodic=0
    g328-g337: GeomPoint x10 (B-spline internal-alignment scaffolding for g327; pole/knot coordinates omitted)
  constraints (252):
    c: Coincident(g1,g0)
    c: Horizontal(g0)
    c: Vertical(g1)
    c: Coincident(g2,g3)
    c: Coincident(g3,g4)
    c: Horizontal(g4)
    c: Horizontal(g2)
    c: Vertical(g3)
    c: Block(g1)
    c: Distance(g3) = 4.86
    c: Block(g4)
    c: Distance(g0) = 10.8
    c: Distance(g2) = 10.8
    c: Coincident(g5,g0)
    c: Coincident(g6,g4)
    c: Coincident(g6,g2)
    c: Block(g8)
    c: Block(g7)
    c: Coincident(g9,g8)
    c: Coincident(g9,g7)
    c: Vertical(g9)
    c: Coincident(g10,g7)
    c: Coincident(g10,g8)
    c: Vertical(g10)
    c: Weight(g11) = 1
    c: Equal(g11, g12-g21) x10
    c: InternalAlignment(g11-g21 -> g22) x11
    c: InternalAlignment(g23-g31 -> g22) x9
    c: Block(g22)
    c: Weight(g32) = 1
    c: Equal(g32, g33-g49) x17
    c: InternalAlignment(g32-g49 -> g50) x18
    c: InternalAlignment(g51-g66 -> g50) x16
    c: Block(g50)
    c: Coincident(g67,g50)
    c: Coincident(g67,g22)
    c: Coincident(g68,g22)
    c: Coincident(g68,g50)
    c: InternalAlignment(g70,g69)
    c: InternalAlignment(g71,g69)
    c: Block(g69)
    c: InternalAlignment(g73,g72)
    c: InternalAlignment(g74,g72)
    c: Block(g72)
    c: InternalAlignment(g76,g75)
    c: InternalAlignment(g77,g75)
    c: InternalAlignment(g78,g80)
    c: InternalAlignment(g79,g80)
    c: Block(g80)
    c: Coincident(g75,g80)
    c: Block(g75)
    c: InternalAlignment(g82,g81)
    c: InternalAlignment(g83,g81)
    c: InternalAlignment(g84,g86)
    c: InternalAlignment(g85,g86)
    c: Block(g86)
    c: Coincident(g81,g86)
    c: Block(g81)
    c: Horizontal(g87)
    c: Block(g87)
    c: Horizontal(g88)
    c: Distance(g88) = 4.14
    c: Horizontal(g89)
    c: Equal(g88,g89) = 4.14
    c: Block(g89)
    c: Block(g88)
    c: Coincident(g90,g87)
    c: Vertical(g90)
    c: Distance(g90) = 11.88
    c: Coincident(g91,g90)
    c: Horizontal(g91)
    c: Coincident(g92,g91)
    c: Vertical(g92)
    c: Distance(g91) = 4.03
    c: Distance(g92) = 1.9
    c: Coincident(g93,g87)
    c: Vertical(g93)
    c: Vertical(g94)
    c: Coincident(g94,g88)
    c: Distance(g93) = 5.8
    c: Distance(g94) = 5.8
    c: Vertical(g95)
    c: Coincident(g95,g88)
    c: Distance(g95) = 6.9
    c: Coincident(g107,g92)
    c: Weight(g96) = 1
    c: Equal(g96, g97-g106) x10
    c: InternalAlignment(g96-g106 -> g107) x11
    c: InternalAlignment(g108-g116 -> g107) x9
    c: Block(g107)
    c: Block(g117)
    c: Coincident(g126,g93)
    c: Weight(g118) = 1
    c: Equal(g118, g119-g125) x7
    c: Coincident(g126,g95)
    c: InternalAlignment(g118-g125 -> g126) x8
    c: InternalAlignment(g127-g132 -> g126) x6
    c: Coincident(g133,g94)
    c: Block(g126)
    c: Block(g133)
    c: Coincident(g134,g133)
    c: Coincident(g134,g89)
    c: Vertical(g134)
    c: Horizontal(g135)
    c: Block(g135)
    c: Horizontal(g136)
    c: Equal(g88,g136) = 4.14
    c: Horizontal(g137)
    c: Equal(g136,g137) = 4.14
    c: Block(g137)
    c: Block(g136)
    c: Coincident(g138,g135)
    c: Vertical(g138)
    c: Equal(g90,g138) = 11.88
    c: Coincident(g139,g138)
    c: Horizontal(g139)
    c: Coincident(g140,g139)
    c: Vertical(g140)
    c: Equal(g91,g139) = 4.03
    c: Equal(g92,g140) = 1.9
    c: Coincident(g141,g135)
    c: Vertical(g141)
    c: Vertical(g142)
    c: Coincident(g142,g136)
    c: Equal(g93,g141) = 5.8
    c: Equal(g94,g142) = 5.8
    c: Vertical(g143)
    c: Coincident(g143,g136)
    c: Equal(g95,g143) = 6.9
    c: Coincident(g149,g140)
    c: Equal(g96,g144) = 1
    c: Equal(g144, g145-g148) x4
    c: InternalAlignment(g144-g148 -> g149) x5
    c: InternalAlignment(g150-g158 -> g149) x9
    c: Block(g149)
    c: Block(g159)
    c: Coincident(g168,g141)
    c: Equal(g118,g160) = 1
    c: Equal(g160, g161-g167) x7
    c: Coincident(g168,g143)
    c: InternalAlignment(g160-g167 -> g168) x8
    c: InternalAlignment(g169-g174 -> g168) x6
    c: Coincident(g175,g142)
    c: Block(g168)
    c: Block(g175)
    c: Coincident(g176,g175)
    c: Coincident(g176,g137)
    c: Vertical(g176)
    c: Coincident(g177,g137)
    c: Vertical(g177)
    c: Coincident(g178,g177)
    c: Coincident(g178,g159)
    c: InternalAlignment(g179,g178)
    c: InternalAlignment(g180,g178)
    c: Block(g178)
    c: Vertical(g181)
    c: Coincident(g181,g89)
    c: Block(g5)
    c: Coincident(g182,g1)
    c: Coincident(g182,g5)
    c: Horizontal(g182)
    c: Coincident(g186,g117)
    c: Weight(g183) = 1
    c: Equal(g183,g184)
    c: Equal(g183,g185)
    c: Coincident(g186,g181)
    c: InternalAlignment(g183,g186)
    c: InternalAlignment(g184,g186)
    c: InternalAlignment(g185,g186)
    c: InternalAlignment(g187,g186)
    c: InternalAlignment(g188,g186)
    c: Block(g186)
    c: InternalAlignment(g190,g189)
    c: InternalAlignment(g191,g189)
    c: Block(g189)
    c: InternalAlignment(g193,g192)
    c: InternalAlignment(g194,g192)
    c: Block(g192)
    c: Horizontal(g195)
    c: Block(g195)
    c: Coincident(g196,g195)
    c: Vertical(g196)
    c: Block(g196)
    c: Distance(g195) = 3.71244
    c: Coincident(g197,g196)
    c: Horizontal(g197)
    c: Distance(g197) = 4.1
    c: Coincident(g198,g192)
    c: Coincident(g198,g197)
    c: Vertical(g198)
    c: Block(g198)
    c: Coincident(g199,g192)
    c: Coincident(g199,g195)
    c: Vertical(g199)
    c: Block(g199)
    c: Horizontal(g200)
    c: Block(g200)
    c: Coincident(g201,g200)
    c: Vertical(g201)
    c: Block(g201)
    c: Coincident(g202,g201)
    c: Horizontal(g202)
    c: Block(g202)
    c: Coincident(g203,g202)
    c: Vertical(g203)
    c: Block(g203)
    c: Coincident(g204,g200)
    c: Vertical(g204)
    c: Block(g204)
    c: Coincident(g215,g203)
    c: Weight(g206) = 1
    c: Equal(g206, g207-g214) x8
    c: Coincident(g215,g205)
    c: InternalAlignment(g206-g214 -> g215) x9
    c: InternalAlignment(g216-g222 -> g215) x7
    c: Coincident(g233,g204)
    c: Weight(g223) = 1
    c: Equal(g223, g224-g232) x9
    c: Coincident(g233,g205)
    c: InternalAlignment(g223-g232 -> g233) x10
    c: InternalAlignment(g234-g241 -> g233) x8
    c: Vertical(g205)
    c: Block(g205)
    c: Block(g215)
    c: Block(g233)
    c: Horizontal(g242)
    c: Horizontal(g243)
    c: Block(g242)
    c: Block(g243)
    c: Vertical(g244)
    c: Block(g244)
    c: Coincident(g270,g243)
    c: Weight(g245) = 1
    c: Equal(g245, g246-g269) x24
    c: Coincident(g270,g244)
    c: InternalAlignment(g245-g269 -> g270) x25
    c: InternalAlignment(g271-g293 -> g270) x23
    c: Coincident(g305,g242)
    c: Weight(g294) = 1
    c: Equal(g294, g295-g304) x10
    c: Coincident(g305,g242)
    c: InternalAlignment(g294-g304 -> g305) x11
    c: InternalAlignment(g306-g314 -> g305) x9
    c: Block(g305)
    c: Coincident(g327,g243)
    c: Weight(g315) = 1
    c: Equal(g315, g316-g326) x11
    c: Coincident(g327,g244)
    c: InternalAlignment(g315-g326 -> g327) x12
    c: InternalAlignment(g328-g337 -> g327) x10
    c: Block(g327)
    c: Block(g270)
FEATURE [PartDesign::Body] Body  label="CommodoreLogoAndText"
  Group = -> [Sketch083]
  Origin = -> Origin
FEATURE [Part::Extrusion] Extrude074  label="CommodoreLogoAndText001"
  Base = -> Sketch083
  Dir = (0,0,1)
  DirMode = 2
  FaceMakerClass = Part::FaceMakerBullseye
  LengthFwd = 10
  LengthRev = 0
  Solid = true
  Symmetric = false
FEATURE [Part::FeaturePython] Clone  label="CommodoreLogoAndTextScale"  # Draft clone (typed FeaturePython)
  AttacherType = Attacher::AttachEngine3D
  Fuse = false
  Objects = -> [Extrude074]
  Placement = pos=(111,5.37,-11.6) rot=(0,0,1;0rad)
  Scale = (0.62,0.62,1)
FEATURE [Part::Mirroring] Part__Mirroring  label="CommodoreLogoAndTextScale (Mirror #1)"
  Base = (0,0,0)
  Normal = (1,0,0)
  Placement = pos=(123.576,0,0) rot=(0,0,1;0rad)
  Source = -> Clone
FEATURE [Sketcher::SketchObject] Sketch084
  FullyConstrained = true
  MapMode = 5
  Support = -> [XY_Plane001]
  sketch-geometry (338):
    g0: LineSegment StartX=-151.619 StartY=28.8932 StartZ=0 EndX=-140.819 EndY=28.8932 EndZ=0
    g1: LineSegment StartX=-151.619 StartY=24.0313 StartZ=0 EndX=-151.619 EndY=28.8932 EndZ=0
    g2: LineSegment StartX=-140.819 StartY=17.7713 StartZ=0 EndX=-151.619 EndY=17.7713 EndZ=0
    g3: LineSegment StartX=-151.619 StartY=17.7713 StartZ=0 EndX=-151.619 EndY=22.6313 EndZ=0
    g4: LineSegment StartX=-151.619 StartY=22.6313 StartZ=0 EndX=-145.128 EndY=22.6313 EndZ=0
    g5: LineSegment StartX=-145.128 StartY=24.0313 StartZ=0 EndX=-140.819 EndY=28.8932 EndZ=0
    g6: LineSegment StartX=-145.128 StartY=22.6313 StartZ=0 EndX=-140.819 EndY=17.7713 EndZ=0
    g7: ArcOfCircle CenterX=-155.157 CenterY=23.3323 CenterZ=0 NormalX=0 NormalY=0 NormalZ=1 AngleXU=0 Radius=6.92354 StartAngle=1.03434 EndAngle=5.24885
    g8: ArcOfCircle CenterX=-155.157 CenterY=23.3323 CenterZ=0 NormalX=0 NormalY=0 NormalZ=1 AngleXU=0 Radius=12.6269 StartAngle=1.28675 EndAngle=4.99643
    g9: LineSegment StartX=-151.619 StartY=35.4532 StartZ=0 EndX=-151.619 EndY=29.2832 EndZ=0
    g10: LineSegment StartX=-151.619 StartY=17.3813 StartZ=0 EndX=-151.619 EndY=11.2113 EndZ=0
    g11-g21: Circle x11 (B-spline internal-alignment scaffolding for g22; pole/knot coordinates omitted)
    g22: BSplineCurve PolesCount=11 KnotsCount=9 Degree=3 IsPeriodic=0
    g23-g31: GeomPoint x9 (B-spline internal-alignment scaffolding for g22; pole/knot coordinates omitted)
    g32-g49: Circle x18 (B-spline internal-alignment scaffolding for g50; pole/knot coordinates omitted)
    g50: BSplineCurve PolesCount=18 KnotsCount=16 Degree=3 IsPeriodic=0
    g51-g66: GeomPoint x16 (B-spline internal-alignment scaffolding for g50; pole/knot coordinates omitted)
    g67: LineSegment StartX=-117.124 StartY=30.093 StartZ=0 EndX=-117.603 EndY=26.5272 EndZ=0
    g68: LineSegment StartX=-117.603 StartY=17.8472 StartZ=0 EndX=-117.124 EndY=14.2659 EndZ=0
    g69: Ellipse CenterX=-109.671 CenterY=20.025 CenterZ=0 NormalX=0 NormalY=0 NormalZ=1 MajorRadius=3.34798 MinorRadius=2.71052 AngleXU=-1.56793
    g70: GeomPoint X=-109.666 Y=18.0598 Z=0
    g71: GeomPoint X=-109.677 Y=21.9902 Z=0
    g72: Ellipse CenterX=-109.671 CenterY=20.0123 CenterZ=0 NormalX=0 NormalY=0 NormalZ=1 MajorRadius=6.93002 MinorRadius=6.36273 AngleXU=-3.13976
    g73: GeomPoint X=-112.417 Y=20.0073 Z=0
    g74: GeomPoint X=-106.925 Y=20.0173 Z=0
    g75: Ellipse CenterX=-51.7682 CenterY=20.1463 CenterZ=0 NormalX=0 NormalY=0 NormalZ=1 MajorRadius=3.19279 MinorRadius=2.71052 AngleXU=-1.52774
    g76: GeomPoint X=-51.6955 Y=18.4606 Z=0
    g77: GeomPoint X=-51.8408 Y=21.832 Z=0
    g78: GeomPoint X=-54.5142 Y=20.1413 Z=0
    g79: GeomPoint X=-49.0221 Y=20.1513 Z=0
    g80: Ellipse CenterX=-51.7682 CenterY=20.1463 CenterZ=0 NormalX=0 NormalY=0 NormalZ=1 MajorRadius=6.93002 MinorRadius=6.36273 AngleXU=-3.13976
    g81: Ellipse CenterX=-22.8436 CenterY=20.1783 CenterZ=0 NormalX=0 NormalY=0 NormalZ=1 MajorRadius=3.31512 MinorRadius=2.71052 AngleXU=-1.60214
    g82: GeomPoint X=-22.9034 Y=18.2706 Z=0
    g83: GeomPoint X=-22.7838 Y=22.0861 Z=0
    g84: GeomPoint X=-25.5897 Y=20.1733 Z=0
    g85: GeomPoint X=-20.0976 Y=20.1833 Z=0
    g86: Ellipse CenterX=-22.8436 CenterY=20.1783 CenterZ=0 NormalX=0 NormalY=0 NormalZ=1 MajorRadius=6.93002 MinorRadius=6.36273 AngleXU=-3.13976
    g87: LineSegment StartX=-101.889 StartY=14.1107 StartZ=0 EndX=-97.7455 EndY=14.1107 EndZ=0
    g88: LineSegment StartX=-93.8155 StartY=14.1107 StartZ=0 EndX=-89.6755 EndY=14.1107 EndZ=0
    g89: LineSegment StartX=-85.7455 StartY=14.1107 StartZ=0 EndX=-81.6055 EndY=14.1107 EndZ=0
    g90: LineSegment StartX=-101.889 StartY=14.1107 StartZ=0 EndX=-101.889 EndY=25.9907 EndZ=0
    g91: LineSegment StartX=-101.889 StartY=25.9907 StartZ=0 EndX=-97.8594 EndY=25.9907 EndZ=0
    g92: LineSegment StartX=-97.8594 StartY=25.9907 StartZ=0 EndX=-97.8594 EndY=24.0907 EndZ=0
    g93: LineSegment StartX=-97.7455 StartY=14.1107 StartZ=0 EndX=-97.7455 EndY=19.9107 EndZ=0
    g94: LineSegment StartX=-89.6755 StartY=14.1107 StartZ=0 EndX=-89.6755 EndY=19.9107 EndZ=0
    g95: LineSegment StartX=-93.8155 StartY=14.1107 StartZ=0 EndX=-93.8155 EndY=21.0107 EndZ=0
    g96-g106: Circle x11 (B-spline internal-alignment scaffolding for g107; pole/knot coordinates omitted)
    g107: BSplineCurve PolesCount=11 KnotsCount=9 Degree=3 IsPeriodic=0
    g108-g116: GeomPoint x9 (B-spline internal-alignment scaffolding for g107; pole/knot coordinates omitted)
    g117: BSplineCurve PolesCount=11 KnotsCount=9 Degree=3 IsPeriodic=0
    g118-g125: Circle x8 (B-spline internal-alignment scaffolding for g126; pole/knot coordinates omitted)
    g126: BSplineCurve PolesCount=8 KnotsCount=6 Degree=3 IsPeriodic=0
    g127-g132: GeomPoint x6 (B-spline internal-alignment scaffolding for g126; pole/knot coordinates omitted)
    g133: BSplineCurve PolesCount=8 KnotsCount=6 Degree=3 IsPeriodic=0
    g134: LineSegment StartX=-85.7455 StartY=21.0107 StartZ=0 EndX=-85.7455 EndY=14.1107 EndZ=0
    g135: LineSegment StartX=-80.0879 StartY=14.1107 StartZ=0 EndX=-75.944 EndY=14.1107 EndZ=0
    g136: LineSegment StartX=-72.014 StartY=14.1107 StartZ=0 EndX=-67.874 EndY=14.1107 EndZ=0
    g137: LineSegment StartX=-63.944 StartY=14.1107 StartZ=0 EndX=-59.804 EndY=14.1107 EndZ=0
    g138: LineSegment StartX=-80.0879 StartY=14.1107 StartZ=0 EndX=-80.0879 EndY=25.9907 EndZ=0
    g139: LineSegment StartX=-80.0879 StartY=25.9907 StartZ=0 EndX=-76.0579 EndY=25.9907 EndZ=0
    g140: LineSegment StartX=-76.0579 StartY=25.9907 StartZ=0 EndX=-76.0579 EndY=24.0907 EndZ=0
    g141: LineSegment StartX=-75.944 StartY=14.1107 StartZ=0 EndX=-75.944 EndY=19.9107 EndZ=0
    g142: LineSegment StartX=-67.874 StartY=14.1107 StartZ=0 EndX=-67.874 EndY=19.9107 EndZ=0
    g143: LineSegment StartX=-72.014 StartY=14.1107 StartZ=0 EndX=-72.014 EndY=21.0107 EndZ=0
    g144-g148: Circle x5 (B-spline internal-alignment scaffolding for g149; pole/knot coordinates omitted)
    g149: BSplineCurve PolesCount=11 KnotsCount=9 Degree=3 IsPeriodic=0
    g150-g158: GeomPoint x9 (B-spline internal-alignment scaffolding for g149; pole/knot coordinates omitted)
    g159: BSplineCurve PolesCount=11 KnotsCount=9 Degree=3 IsPeriodic=0
    g160-g167: Circle x8 (B-spline internal-alignment scaffolding for g168; pole/knot coordinates omitted)
    g168: BSplineCurve PolesCount=8 KnotsCount=6 Degree=3 IsPeriodic=0
    g169-g174: GeomPoint x6 (B-spline internal-alignment scaffolding for g168; pole/knot coordinates omitted)
    g175: BSplineCurve PolesCount=8 KnotsCount=6 Degree=3 IsPeriodic=0
    g176: LineSegment StartX=-63.944 StartY=21.0107 StartZ=0 EndX=-63.944 EndY=14.1107 EndZ=0
    g177: LineSegment StartX=-59.804 StartY=14.1107 StartZ=0 EndX=-59.804 EndY=21.5868 EndZ=0
    g178: BSplineCurve PolesCount=4 KnotsCount=2 Degree=3 IsPeriodic=0
    g179: GeomPoint X=-59.804 Y=21.5868 Z=0
    g180: GeomPoint X=-60.2379 Y=24.0907 Z=0
    g181: LineSegment StartX=-81.6055 StartY=14.1107 StartZ=0 EndX=-81.6055 EndY=21.5868 EndZ=0
    g182: LineSegment StartX=-151.619 StartY=24.0313 StartZ=0 EndX=-145.128 EndY=24.0313 EndZ=0
    g183: Circle CenterX=-82.0394 CenterY=24.0907 CenterZ=0 NormalX=0 NormalY=0 NormalZ=1 AngleXU=0 Radius=1
    g184: Circle CenterX=-81.7131 CenterY=23.2736 CenterZ=0 NormalX=0 NormalY=0 NormalZ=1 AngleXU=0 Radius=1
    g185: Circle CenterX=-81.6055 CenterY=21.5868 CenterZ=0 NormalX=0 NormalY=0 NormalZ=1 AngleXU=0 Radius=1
    g186: BSplineCurve PolesCount=3 KnotsCount=2 Degree=2 IsPeriodic=0
    g187: GeomPoint X=-82.0394 Y=24.0907 Z=0
    g188: GeomPoint X=-81.6055 Y=21.5868 Z=0
    g189: Ellipse CenterX=-37.3522 CenterY=19.9515 CenterZ=0 NormalX=0 NormalY=0 NormalZ=1 MajorRadius=2.99755 MinorRadius=2.49 AngleXU=1.5708
    g190: GeomPoint X=-37.3522 Y=21.6203 Z=0
    g191: GeomPoint X=-37.3522 Y=18.2826 Z=0
    g192: ArcOfEllipse CenterX=-38.7647 CenterY=20.06 CenterZ=0 NormalX=0 NormalY=0 NormalZ=1 MajorRadius=6.30025 MinorRadius=5.3849 AngleXU=1.57276 StartAngle=5.50632 EndAngle=10.3035
    g193: GeomPoint X=-38.7711 Y=23.3304 Z=0
    g194: GeomPoint X=-38.7583 Y=16.7895 Z=0
    g195: LineSegment StartX=-34.6109 StartY=14.1107 StartZ=0 EndX=-30.8984 EndY=14.1107 EndZ=0
    g196: LineSegment StartX=-30.8984 StartY=14.1107 StartZ=0 EndX=-30.8984 EndY=31.1784 EndZ=0
    g197: LineSegment StartX=-30.8984 StartY=31.1784 StartZ=0 EndX=-34.9984 EndY=31.1784 EndZ=0
    g198: LineSegment StartX=-34.9984 StartY=24.5602 StartZ=0 EndX=-34.9984 EndY=31.1784 EndZ=0
    g199: LineSegment StartX=-34.6109 StartY=16.0476 StartZ=0 EndX=-34.6109 EndY=14.1107 EndZ=0
    g200: LineSegment StartX=-14.8781 StartY=14.1107 StartZ=0 EndX=-10.5106 EndY=14.1107 EndZ=0
    g201: LineSegment StartX=-14.8781 StartY=14.1107 StartZ=0 EndX=-14.8781 EndY=25.8504 EndZ=0
    g202: LineSegment StartX=-14.8781 StartY=25.8504 StartZ=0 EndX=-10.8534 EndY=25.8504 EndZ=0
    g203: LineSegment StartX=-10.8534 StartY=25.8504 StartZ=0 EndX=-10.8534 EndY=24.0923 EndZ=0
    g204: LineSegment StartX=-10.5106 StartY=14.1107 StartZ=0 EndX=-10.5106 EndY=19.7752 EndZ=0
    g205: LineSegment StartX=-5.96397 StartY=25.9304 StartZ=0 EndX=-5.96397 EndY=22.574 EndZ=0
    g206-g214: Circle x9 (B-spline internal-alignment scaffolding for g215; pole/knot coordinates omitted)
    g215: BSplineCurve PolesCount=9 KnotsCount=7 Degree=3 IsPeriodic=0
    g216-g222: GeomPoint x7 (B-spline internal-alignment scaffolding for g215; pole/knot coordinates omitted)
    g223-g232: Circle x10 (B-spline internal-alignment scaffolding for g233; pole/knot coordinates omitted)
    g233: BSplineCurve PolesCount=10 KnotsCount=8 Degree=3 IsPeriodic=0
    g234-g241: GeomPoint x8 (B-spline internal-alignment scaffolding for g233; pole/knot coordinates omitted)
    g242: LineSegment StartX=-1.58923 StartY=21.0696 StartZ=0 EndX=2.62034 EndY=21.0696 EndZ=0
    g243: LineSegment StartX=-1.55856 StartY=18.7342 StartZ=0 EndX=6.45946 EndY=18.7342 EndZ=0
    g244: LineSegment StartX=5.29231 StartY=17.386 StartZ=0 EndX=5.29231 EndY=14.3674 EndZ=0
    g245-g269: Circle x25 (B-spline internal-alignment scaffolding for g270; pole/knot coordinates omitted)
    g270: BSplineCurve PolesCount=25 KnotsCount=23 Degree=3 IsPeriodic=0
    g271-g293: GeomPoint x23 (B-spline internal-alignment scaffolding for g270; pole/knot coordinates omitted)
    g294-g304: Circle x11 (B-spline internal-alignment scaffolding for g305; pole/knot coordinates omitted)
    g305: BSplineCurve PolesCount=11 KnotsCount=9 Degree=3 IsPeriodic=0
    g306-g314: GeomPoint x9 (B-spline internal-alignment scaffolding for g305; pole/knot coordinates omitted)
    g315-g326: Circle x12 (B-spline internal-alignment scaffolding for g327; pole/knot coordinates omitted)
    g327: BSplineCurve PolesCount=12 KnotsCount=10 Degree=3 IsPeriodic=0
    g328-g337: GeomPoint x10 (B-spline internal-alignment scaffolding for g327; pole/knot coordinates omitted)
  constraints (252):
    c: Coincident(g1,g0)
    c: Horizontal(g0)
    c: Vertical(g1)
    c: Coincident(g2,g3)
    c: Coincident(g3,g4)
    c: Horizontal(g4)
    c: Horizontal(g2)
    c: Vertical(g3)
    c: Block(g1)
    c: Distance(g3) = 4.86
    c: Block(g4)
    c: Distance(g0) = 10.8
    c: Distance(g2) = 10.8
    c: Coincident(g5,g0)
    c: Coincident(g6,g4)
    c: Coincident(g6,g2)
    c: Block(g8)
    c: Block(g7)
    c: Coincident(g9,g8)
    c: Coincident(g9,g7)
    c: Vertical(g9)
    c: Coincident(g10,g7)
    c: Coincident(g10,g8)
    c: Vertical(g10)
    c: Weight(g11) = 1
    c: Equal(g11, g12-g21) x10
    c: InternalAlignment(g11-g21 -> g22) x11
    c: InternalAlignment(g23-g31 -> g22) x9
    c: Block(g22)
    c: Weight(g32) = 1
    c: Equal(g32, g33-g49) x17
    c: InternalAlignment(g32-g49 -> g50) x18
    c: InternalAlignment(g51-g66 -> g50) x16
    c: Block(g50)
    c: Coincident(g67,g50)
    c: Coincident(g67,g22)
    c: Coincident(g68,g22)
    c: Coincident(g68,g50)
    c: InternalAlignment(g70,g69)
    c: InternalAlignment(g71,g69)
    c: Block(g69)
    c: InternalAlignment(g73,g72)
    c: InternalAlignment(g74,g72)
    c: Block(g72)
    c: InternalAlignment(g76,g75)
    c: InternalAlignment(g77,g75)
    c: InternalAlignment(g78,g80)
    c: InternalAlignment(g79,g80)
    c: Block(g80)
    c: Coincident(g75,g80)
    c: Block(g75)
    c: InternalAlignment(g82,g81)
    c: InternalAlignment(g83,g81)
    c: InternalAlignment(g84,g86)
    c: InternalAlignment(g85,g86)
    c: Block(g86)
    c: Coincident(g81,g86)
    c: Block(g81)
    c: Horizontal(g87)
    c: Block(g87)
    c: Horizontal(g88)
    c: Distance(g88) = 4.14
    c: Horizontal(g89)
    c: Equal(g88,g89) = 4.14
    c: Block(g89)
    c: Block(g88)
    c: Coincident(g90,g87)
    c: Vertical(g90)
    c: Distance(g90) = 11.88
    c: Coincident(g91,g90)
    c: Horizontal(g91)
    c: Coincident(g92,g91)
    c: Vertical(g92)
    c: Distance(g91) = 4.03
    c: Distance(g92) = 1.9
    c: Coincident(g93,g87)
    c: Vertical(g93)
    c: Vertical(g94)
    c: Coincident(g94,g88)
    c: Distance(g93) = 5.8
    c: Distance(g94) = 5.8
    c: Vertical(g95)
    c: Coincident(g95,g88)
    c: Distance(g95) = 6.9
    c: Coincident(g107,g92)
    c: Weight(g96) = 1
    c: Equal(g96, g97-g106) x10
    c: InternalAlignment(g96-g106 -> g107) x11
    c: InternalAlignment(g108-g116 -> g107) x9
    c: Block(g107)
    c: Block(g117)
    c: Coincident(g126,g93)
    c: Weight(g118) = 1
    c: Equal(g118, g119-g125) x7
    c: Coincident(g126,g95)
    c: InternalAlignment(g118-g125 -> g126) x8
    c: InternalAlignment(g127-g132 -> g126) x6
    c: Coincident(g133,g94)
    c: Block(g126)
    c: Block(g133)
    c: Coincident(g134,g133)
    c: Coincident(g134,g89)
    c: Vertical(g134)
    c: Horizontal(g135)
    c: Block(g135)
    c: Horizontal(g136)
    c: Equal(g88,g136) = 4.14
    c: Horizontal(g137)
    c: Equal(g136,g137) = 4.14
    c: Block(g137)
    c: Block(g136)
    c: Coincident(g138,g135)
    c: Vertical(g138)
    c: Equal(g90,g138) = 11.88
    c: Coincident(g139,g138)
    c: Horizontal(g139)
    c: Coincident(g140,g139)
    c: Vertical(g140)
    c: Equal(g91,g139) = 4.03
    c: Equal(g92,g140) = 1.9
    c: Coincident(g141,g135)
    c: Vertical(g141)
    c: Vertical(g142)
    c: Coincident(g142,g136)
    c: Equal(g93,g141) = 5.8
    c: Equal(g94,g142) = 5.8
    c: Vertical(g143)
    c: Coincident(g143,g136)
    c: Equal(g95,g143) = 6.9
    c: Coincident(g149,g140)
    c: Equal(g96,g144) = 1
    c: Equal(g144, g145-g148) x4
    c: InternalAlignment(g144-g148 -> g149) x5
    c: InternalAlignment(g150-g158 -> g149) x9
    c: Block(g149)
    c: Block(g159)
    c: Coincident(g168,g141)
    c: Equal(g118,g160) = 1
    c: Equal(g160, g161-g167) x7
    c: Coincident(g168,g143)
    c: InternalAlignment(g160-g167 -> g168) x8
    c: InternalAlignment(g169-g174 -> g168) x6
    c: Coincident(g175,g142)
    c: Block(g168)
    c: Block(g175)
    c: Coincident(g176,g175)
    c: Coincident(g176,g137)
    c: Vertical(g176)
    c: Coincident(g177,g137)
    c: Vertical(g177)
    c: Coincident(g178,g177)
    c: Coincident(g178,g159)
    c: InternalAlignment(g179,g178)
    c: InternalAlignment(g180,g178)
    c: Block(g178)
    c: Vertical(g181)
    c: Coincident(g181,g89)
    c: Block(g5)
    c: Coincident(g182,g1)
    c: Coincident(g182,g5)
    c: Horizontal(g182)
    c: Coincident(g186,g117)
    c: Weight(g183) = 1
    c: Equal(g183,g184)
    c: Equal(g183,g185)
    c: Coincident(g186,g181)
    c: InternalAlignment(g183,g186)
    c: InternalAlignment(g184,g186)
    c: InternalAlignment(g185,g186)
    c: InternalAlignment(g187,g186)
    c: InternalAlignment(g188,g186)
    c: Block(g186)
    c: InternalAlignment(g190,g189)
    c: InternalAlignment(g191,g189)
    c: Block(g189)
    c: InternalAlignment(g193,g192)
    c: InternalAlignment(g194,g192)
    c: Block(g192)
    c: Horizontal(g195)
    c: Block(g195)
    c: Coincident(g196,g195)
    c: Vertical(g196)
    c: Block(g196)
    c: Distance(g195) = 3.71244
    c: Coincident(g197,g196)
    c: Horizontal(g197)
    c: Distance(g197) = 4.1
    c: Coincident(g198,g192)
    c: Coincident(g198,g197)
    c: Vertical(g198)
    c: Block(g198)
    c: Coincident(g199,g192)
    c: Coincident(g199,g195)
    c: Vertical(g199)
    c: Block(g199)
    c: Horizontal(g200)
    c: Block(g200)
    c: Coincident(g201,g200)
    c: Vertical(g201)
    c: Block(g201)
    c: Coincident(g202,g201)
    c: Horizontal(g202)
    c: Block(g202)
    c: Coincident(g203,g202)
    c: Vertical(g203)
    c: Block(g203)
    c: Coincident(g204,g200)
    c: Vertical(g204)
    c: Block(g204)
    c: Coincident(g215,g203)
    c: Weight(g206) = 1
    c: Equal(g206, g207-g214) x8
    c: Coincident(g215,g205)
    c: InternalAlignment(g206-g214 -> g215) x9
    c: InternalAlignment(g216-g222 -> g215) x7
    c: Coincident(g233,g204)
    c: Weight(g223) = 1
    c: Equal(g223, g224-g232) x9
    c: Coincident(g233,g205)
    c: InternalAlignment(g223-g232 -> g233) x10
    c: InternalAlignment(g234-g241 -> g233) x8
    c: Vertical(g205)
    c: Block(g205)
    c: Block(g215)
    c: Block(g233)
    c: Horizontal(g242)
    c: Horizontal(g243)
    c: Block(g242)
    c: Block(g243)
    c: Vertical(g244)
    c: Block(g244)
    c: Coincident(g270,g243)
    c: Weight(g245) = 1
    c: Equal(g245, g246-g269) x24
    c: Coincident(g270,g244)
    c: InternalAlignment(g245-g269 -> g270) x25
    c: InternalAlignment(g271-g293 -> g270) x23
    c: Coincident(g305,g242)
    c: Weight(g294) = 1
    c: Equal(g294, g295-g304) x10
    c: Coincident(g305,g242)
    c: InternalAlignment(g294-g304 -> g305) x11
    c: InternalAlignment(g306-g314 -> g305) x9
    c: Block(g305)
    c: Coincident(g327,g243)
    c: Weight(g315) = 1
    c: Equal(g315, g316-g326) x11
    c: Coincident(g327,g244)
    c: InternalAlignment(g315-g326 -> g327) x12
    c: InternalAlignment(g328-g337 -> g327) x10
    c: Block(g327)
    c: Block(g270)
FEATURE [Part::Extrusion] Extrude075  label="CommodoreLogoAndText002"
  Base = -> Sketch084
  Dir = (0,0,1)
  DirMode = 2
  FaceMakerClass = Part::FaceMakerBullseye
  LengthFwd = 10
  LengthRev = 0
  Solid = true
  Symmetric = false
FEATURE [Part::FeaturePython] Clone001  label="CommodoreLogoAndTextScale001"  # Draft clone (typed FeaturePython)
  AttacherType = Attacher::AttachEngine3D
  Fuse = false
  Objects = -> [Extrude075]
  Placement = pos=(112.566,5.37,73.6) rot=(0,0,1;0rad)
  Scale = (0.62,0.62,1)
FEATURE [Part::Cut] Cut073  label="sideA005"
  Base = -> Extrude002
  Tool = -> Part__Mirroring
FEATURE [Part::Cut] Cut074  label="sideB005"
  Base = -> Extrude028
  Tool = -> Clone001
FEATURE [Sketcher::SketchObject] Sketch085
  FullyConstrained = true
  Placement = pos=(0,0,0) rot=(-1,0,0;4.71239rad)
  sketch-geometry (10):
    g0: LineSegment StartX=0 StartY=0 StartZ=0 EndX=-7 EndY=0 EndZ=0
    g1: LineSegment StartX=-7 StartY=10 StartZ=0 EndX=-6.5 EndY=10 EndZ=0
    g2: LineSegment StartX=0 StartY=10 StartZ=0 EndX=-0.5 EndY=10 EndZ=0
    g3: ArcOfCircle CenterX=-3.5 CenterY=10 CenterZ=0 NormalX=0 NormalY=0 NormalZ=1 AngleXU=0 Radius=3 StartAngle=3.14159 EndAngle=6.28319
    g4: LineSegment StartX=-7 StartY=0 StartZ=0 EndX=-10.5 EndY=0 EndZ=0
    g5: LineSegment StartX=0 StartY=0 StartZ=0 EndX=3.5 EndY=0 EndZ=0
    g6: ArcOfCircle CenterX=-10.5 CenterY=3.5 CenterZ=0 NormalX=0 NormalY=0 NormalZ=1 AngleXU=0 Radius=3.5 StartAngle=4.71239 EndAngle=6.28319
    g7: ArcOfCircle CenterX=3.5 CenterY=3.5 CenterZ=0 NormalX=0 NormalY=0 NormalZ=1 AngleXU=0 Radius=3.5 StartAngle=3.14159 EndAngle=4.71239
    g8: LineSegment StartX=-7 StartY=3.5 StartZ=0 EndX=-7 EndY=10 EndZ=0
    g9: LineSegment StartX=0 StartY=10 StartZ=0 EndX=0 EndY=3.5 EndZ=0
  constraints (26):
    c: Coincident(g0,g-1)
    c: Horizontal(g0)
    c: Distance(g0) = 7
    c: Horizontal(g1)
    c: Distance(g1) = 0.5
    c: Horizontal(g2)
    c: Distance(g2) = 0.5
    c: Coincident(g3,g1)
    c: Coincident(g3,g2)
    c: Block(g3)
    c: Coincident(g4,g0)
    c: Horizontal(g4)
    c: Distance(g4) = 3.5
    c: Coincident(g5,g0)
    c: Distance(g5) = 3.5
    c: Horizontal(g5)
    c: Coincident(g6,g4)
    c: Block(g6)
    c: Coincident(g7,g5)
    c: Block(g7)
    c: Coincident(g8,g6)
    c: Coincident(g8,g1)
    c: Vertical(g8)
    c: Coincident(g9,g2)
    c: Coincident(g9,g7)
    c: Vertical(g9)
FEATURE [Part::Extrusion] Extrude076  label="backRightCasePillarSideBracket"
  Base = -> Sketch085
  Dir = (0,-1,3e-16)
  DirMode = 2
  FaceMakerClass = Part::FaceMakerBullseye
  LengthFwd = 6.7
  LengthRev = 0
  Placement = pos=(16,11.5,0) rot=(0,0,1;0rad)
  Solid = true
  Symmetric = false
FEATURE [Sketcher::SketchObject] Sketch086
  FullyConstrained = true
  Placement = pos=(0,0,0) rot=(1,0,0;1.5708rad)
  sketch-geometry (10):
    g0: LineSegment StartX=0 StartY=0 StartZ=0 EndX=-7 EndY=0 EndZ=0
    g1: LineSegment StartX=-7 StartY=10 StartZ=0 EndX=-6.5 EndY=10 EndZ=0
    g2: LineSegment StartX=0 StartY=10 StartZ=0 EndX=-0.5 EndY=10 EndZ=0
    g3: ArcOfCircle CenterX=-3.5 CenterY=10 CenterZ=0 NormalX=0 NormalY=0 NormalZ=1 AngleXU=0 Radius=3 StartAngle=3.14159 EndAngle=6.28319
    g4: LineSegment StartX=-7 StartY=0 StartZ=0 EndX=-10.5 EndY=0 EndZ=0
    g5: LineSegment StartX=0 StartY=0 StartZ=0 EndX=3.5 EndY=0 EndZ=0
    g6: ArcOfCircle CenterX=-10.5 CenterY=3.5 CenterZ=0 NormalX=0 NormalY=0 NormalZ=1 AngleXU=0 Radius=3.5 StartAngle=4.71239 EndAngle=6.28319
    g7: ArcOfCircle CenterX=3.5 CenterY=3.5 CenterZ=0 NormalX=0 NormalY=0 NormalZ=1 AngleXU=0 Radius=3.5 StartAngle=3.14159 EndAngle=4.71239
    g8: LineSegment StartX=-7 StartY=3.5 StartZ=0 EndX=-7 EndY=10 EndZ=0
    g9: LineSegment StartX=0 StartY=10 StartZ=0 EndX=0 EndY=3.5 EndZ=0
  constraints (26):
    c: Coincident(g0,g-1)
    c: Horizontal(g0)
    c: Distance(g0) = 7
    c: Horizontal(g1)
    c: Distance(g1) = 0.5
    c: Horizontal(g2)
    c: Distance(g2) = 0.5
    c: Coincident(g3,g1)
    c: Coincident(g3,g2)
    c: Block(g3)
    c: Coincident(g4,g0)
    c: Horizontal(g4)
    c: Distance(g4) = 3.5
    c: Coincident(g5,g0)
    c: Distance(g5) = 3.5
    c: Horizontal(g5)
    c: Coincident(g6,g4)
    c: Block(g6)
    c: Coincident(g7,g5)
    c: Block(g7)
    c: Coincident(g8,g6)
    c: Coincident(g8,g1)
    c: Vertical(g8)
    c: Coincident(g9,g2)
    c: Coincident(g9,g7)
    c: Vertical(g9)
FEATURE [Part::Extrusion] Extrude077  label="backLeftCasePillarSideBracket001"
  Base = -> Sketch086
  Dir = (0,-1,3e-16)
  DirMode = 2
  FaceMakerClass = Part::FaceMakerBullseye
  LengthFwd = 6.7
  LengthRev = 0
  Placement = pos=(9,11.5,72) rot=(0,1,0;3.14159rad)
  Solid = true
  Symmetric = false
FEATURE [Sketcher::SketchObject] Sketch087
  FullyConstrained = true
  Placement = pos=(0,0,0) rot=(1,0,0;1.5708rad)
  sketch-geometry (8):
    g0: LineSegment StartX=0 StartY=4e-16 StartZ=0 EndX=-7 EndY=4e-16 EndZ=0
    g1: LineSegment StartX=-7 StartY=4e-16 StartZ=0 EndX=-10.5 EndY=4e-16 EndZ=0
    g2: LineSegment StartX=0 StartY=4e-16 StartZ=0 EndX=3.5 EndY=4e-16 EndZ=0
    g3: ArcOfCircle CenterX=-10.5 CenterY=3.5 CenterZ=0 NormalX=0 NormalY=0 NormalZ=1 AngleXU=0 Radius=3.5 StartAngle=4.71239 EndAngle=6.28319
    g4: ArcOfCircle CenterX=3.5 CenterY=3.5 CenterZ=0 NormalX=0 NormalY=0 NormalZ=1 AngleXU=0 Radius=3.5 StartAngle=3.14159 EndAngle=4.71239
    g5: ArcOfCircle CenterX=-3.5 CenterY=3.5 CenterZ=0 NormalX=0 NormalY=0 NormalZ=1 AngleXU=0 Radius=3 StartAngle=3.14159 EndAngle=6.28319
    g6: LineSegment StartX=-7 StartY=3.5 StartZ=0 EndX=-6.5 EndY=3.5 EndZ=0
    g7: LineSegment StartX=-0.5 StartY=3.5 StartZ=0 EndX=0 EndY=3.5 EndZ=0
  constraints (20):
    c: Coincident(g0,g-1)
    c: Horizontal(g0)
    c: Distance(g0) = 7
    c: Coincident(g1,g0)
    c: Horizontal(g1)
    c: Distance(g1) = 3.5
    c: Coincident(g2,g0)
    c: Distance(g2) = 3.5
    c: Horizontal(g2)
    c: Coincident(g3,g1)
    c: Block(g3)
    c: Coincident(g4,g2)
    c: Block(g4)
    c: Horizontal(g6)
    c: Coincident(g5,g6)
    c: Block(g5)
    c: Coincident(g6,g3)
    c: Coincident(g7,g5)
    c: Coincident(g7,g4)
    c: Horizontal(g7)
FEATURE [Part::Extrusion] Extrude078  label="frontBackLeftCasePillarSideBracket001"
  Base = -> Sketch087
  Dir = (0,-1,2e-16)
  DirMode = 2
  FaceMakerClass = Part::FaceMakerBullseye
  LengthFwd = 6.7
  LengthRev = 0
  Placement = pos=(93,11.5,0) rot=(0,0,1;0rad)
  Solid = true
  Symmetric = false
FEATURE [Sketcher::SketchObject] Sketch088
  FullyConstrained = true
  Placement = pos=(0,0,0) rot=(1,0,0;1.5708rad)
  sketch-geometry (8):
    g0: LineSegment StartX=0 StartY=4e-16 StartZ=0 EndX=-7 EndY=4e-16 EndZ=0
    g1: LineSegment StartX=-7 StartY=4e-16 StartZ=0 EndX=-10.5 EndY=4e-16 EndZ=0
    g2: LineSegment StartX=0 StartY=4e-16 StartZ=0 EndX=3.5 EndY=4e-16 EndZ=0
    g3: ArcOfCircle CenterX=-10.5 CenterY=3.5 CenterZ=0 NormalX=0 NormalY=0 NormalZ=1 AngleXU=0 Radius=3.5 StartAngle=4.71239 EndAngle=6.28319
    g4: ArcOfCircle CenterX=3.5 CenterY=3.5 CenterZ=0 NormalX=0 NormalY=0 NormalZ=1 AngleXU=0 Radius=3.5 StartAngle=3.14159 EndAngle=4.71239
    g5: ArcOfCircle CenterX=-3.5 CenterY=3.5 CenterZ=0 NormalX=0 NormalY=0 NormalZ=1 AngleXU=0 Radius=3 StartAngle=3.14159 EndAngle=6.28319
    g6: LineSegment StartX=-7 StartY=3.5 StartZ=0 EndX=-6.5 EndY=3.5 EndZ=0
    g7: LineSegment StartX=-0.5 StartY=3.5 StartZ=0 EndX=0 EndY=3.5 EndZ=0
  constraints (20):
    c: Coincident(g0,g-1)
    c: Horizontal(g0)
    c: Distance(g0) = 7
    c: Coincident(g1,g0)
    c: Horizontal(g1)
    c: Distance(g1) = 3.5
    c: Coincident(g2,g0)
    c: Distance(g2) = 3.5
    c: Horizontal(g2)
    c: Coincident(g3,g1)
    c: Block(g3)
    c: Coincident(g4,g2)
    c: Block(g4)
    c: Horizontal(g6)
    c: Coincident(g5,g6)
    c: Block(g5)
    c: Coincident(g6,g3)
    c: Coincident(g7,g5)
    c: Coincident(g7,g4)
    c: Horizontal(g7)
FEATURE [Part::Extrusion] Extrude079  label="frontFrontRightCasePillarSideBracket002"
  Base = -> Sketch088
  Dir = (0,-1,2e-16)
  DirMode = 2
  FaceMakerClass = Part::FaceMakerBullseye
  LengthFwd = 2
  LengthRev = 0
  Placement = pos=(106,11.5,72) rot=(0,1,0;3.14159rad)
  Solid = true
  Symmetric = false
FEATURE [Part::Chamfer] Chamfer
  Base = -> Extrude076
  Edges = 1 edges r=3: [Edge19]
FEATURE [Part::Chamfer] Chamfer002
  Base = -> Extrude077
  Edges = 1 edges r=3: [Edge7]
FEATURE [Part::Chamfer] Chamfer003  label="backLeftCasePillarSideBracket002"
  Base = -> Chamfer002
  Edges = 1 edges r=3.8: [Edge29]
FEATURE [Part::Chamfer] Chamfer004  label="backRightCasePillarSideBracket001"
  Base = -> Chamfer
  Edges = 1 edges r=3.8: [Edge24]
FEATURE [Sketcher::SketchObject] Sketch089
  FullyConstrained = true
  Placement = pos=(0,0,0) rot=(1,0,0;1.5708rad)
  sketch-geometry (8):
    g0: LineSegment StartX=0 StartY=4e-16 StartZ=0 EndX=-7 EndY=4e-16 EndZ=0
    g1: LineSegment StartX=-7 StartY=4e-16 StartZ=0 EndX=-10.5 EndY=4e-16 EndZ=0
    g2: LineSegment StartX=0 StartY=4e-16 StartZ=0 EndX=3.5 EndY=4e-16 EndZ=0
    g3: ArcOfCircle CenterX=-10.5 CenterY=3.5 CenterZ=0 NormalX=0 NormalY=0 NormalZ=1 AngleXU=0 Radius=3.5 StartAngle=4.71239 EndAngle=6.28319
    g4: ArcOfCircle CenterX=3.5 CenterY=3.5 CenterZ=0 NormalX=0 NormalY=0 NormalZ=1 AngleXU=0 Radius=3.5 StartAngle=3.14159 EndAngle=4.71239
    g5: ArcOfCircle CenterX=-3.5 CenterY=3.5 CenterZ=0 NormalX=0 NormalY=0 NormalZ=1 AngleXU=0 Radius=3 StartAngle=3.14159 EndAngle=6.28319
    g6: LineSegment StartX=-7 StartY=3.5 StartZ=0 EndX=-6.5 EndY=3.5 EndZ=0
    g7: LineSegment StartX=-0.5 StartY=3.5 StartZ=0 EndX=0 EndY=3.5 EndZ=0
  constraints (20):
    c: Coincident(g0,g-1)
    c: Horizontal(g0)
    c: Distance(g0) = 7
    c: Coincident(g1,g0)
    c: Horizontal(g1)
    c: Distance(g1) = 3.5
    c: Coincident(g2,g0)
    c: Distance(g2) = 3.5
    c: Horizontal(g2)
    c: Coincident(g3,g1)
    c: Block(g3)
    c: Coincident(g4,g2)
    c: Block(g4)
    c: Horizontal(g6)
    c: Coincident(g5,g6)
    c: Block(g5)
    c: Coincident(g6,g3)
    c: Coincident(g7,g5)
    c: Coincident(g7,g4)
    c: Horizontal(g7)
FEATURE [Part::Extrusion] Extrude080  label="frontBackLeftCasePillarSideBracket002"
  Base = -> Sketch089
  Dir = (0,-1,2e-16)
  DirMode = 2
  FaceMakerClass = Part::FaceMakerBullseye
  LengthFwd = 6.7
  LengthRev = 0
  Placement = pos=(86,11.5,72) rot=(0,1,0;3.14159rad)
  Solid = true
  Symmetric = false
FEATURE [Sketcher::SketchObject] Sketch090
  FullyConstrained = false
  Placement = pos=(0,0,0) rot=(1,0,0;1.5708rad)
  sketch-geometry (14):
    g0: LineSegment StartX=0 StartY=0 StartZ=0 EndX=-7 EndY=0 EndZ=0
    g1: LineSegment StartX=-7 StartY=0 StartZ=0 EndX=-10.5 EndY=0 EndZ=0
    g2: LineSegment StartX=0 StartY=0 StartZ=0 EndX=3.5 EndY=0 EndZ=0
    g3: ArcOfCircle CenterX=3.5 CenterY=3.5 CenterZ=0 NormalX=0 NormalY=0 NormalZ=1 AngleXU=0 Radius=3.5 StartAngle=3.14159 EndAngle=4.71239
    g4: LineSegment StartX=4e-16 StartY=10 StartZ=0 EndX=4e-16 EndY=3.5 EndZ=0
    g5: LineSegment StartX=-10.5 StartY=0 StartZ=0 EndX=-5.22039 EndY=7.5423 EndZ=0
    g6: LineSegment StartX=-5.22039 StartY=7.5423 StartZ=0 EndX=-4.81077 EndY=7.25557 EndZ=0
    g7: LineSegment StartX=-4.81077 StartY=7.25557 StartZ=0 EndX=0.104621 EndY=3.8148 EndZ=0
    g8: LineSegment StartX=0.104621 StartY=3.8148 StartZ=0 EndX=0.514237 EndY=3.52807 EndZ=0
    g9: LineSegment StartX=0.514237 StartY=3.52807 StartZ=0 EndX=-4.76538 EndY=-4.01424 EndZ=0
    g10: LineSegment StartX=-10.5 StartY=0 StartZ=0 EndX=-10.5 EndY=2.5 EndZ=0
    g11: LineSegment StartX=-4.76538 StartY=-4.01424 StartZ=0 EndX=-2.26538 EndY=-4.01424 EndZ=0
    g12: LineSegment StartX=-9.79174 StartY=-0.637389 StartZ=0 EndX=-8.12948 EndY=1.22993 EndZ=0
    g13: LineSegment StartX=-5.57831 StartY=-2.69239 StartZ=0 EndX=-4.08286 EndY=-0.688983 EndZ=0
  constraints (36):
    c: Coincident(g0,g-1)
    c: Horizontal(g0)
    c: Distance(g0) = 7
    c: Coincident(g1,g0)
    c: Horizontal(g1)
    c: Distance(g1) = 3.5
    c: Coincident(g2,g0)
    c: Distance(g2) = 3.5
    c: Horizontal(g2)
    c: Coincident(g3,g2)
    c: Block(g3)
    c: Coincident(g4,g3)
    c: Vertical(g4)
    c: Coincident(g5,g1)
    c: Coincident(g6,g5)
    c: Perpendicular(g5,g6)
    c: Block(g5)
    c: Distance(g6) = 0.5
    c: Distance(g7) = 6
    c: Coincident(g7,g6)
    c: Parallel(g7,g6)
    c: Coincident(g8,g7)
    c: Distance(g8) = 0.5
    c: Parallel(g8,g7)
    c: Coincident(g9,g8)
    c: Distance(g5) = 9.20656
    c: Equal(g9,g5)
    c: Parallel(g9,g5)
    c: Coincident(g10,g1)
    c: Vertical(g10)
    c: Distance(g10) = 2.5
    c: Coincident(g11,g9)
    c: Horizontal(g11)
    c: Distance(g11) = 2.5
    c: Distance(g12) = 2.5
    c: Distance(g13) = 2.5
